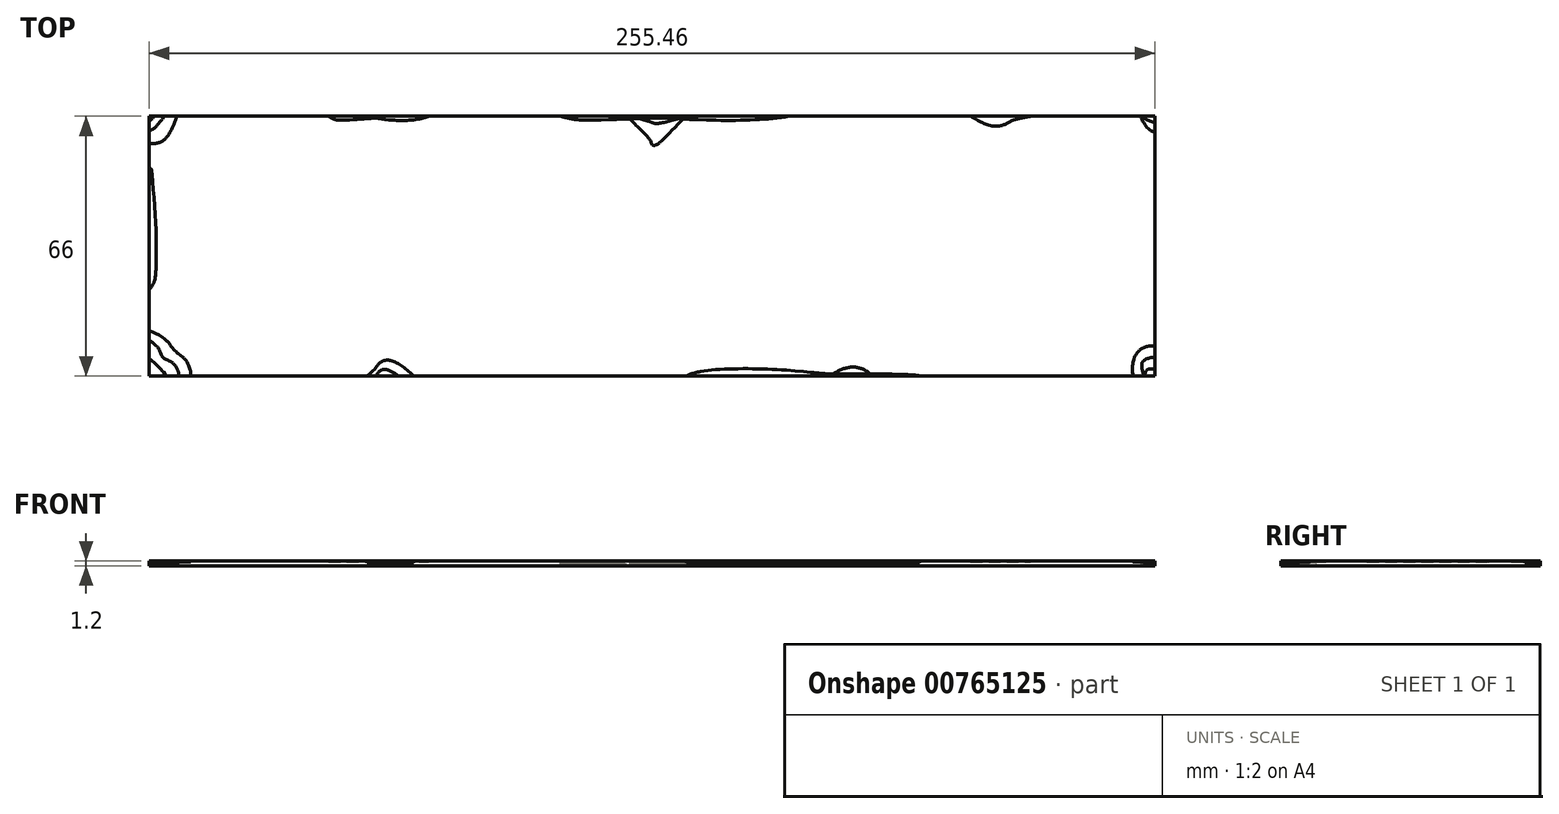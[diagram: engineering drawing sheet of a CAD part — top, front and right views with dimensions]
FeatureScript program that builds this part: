
annotation { "Feature Type Name" : "Feature", "Feature Type Description" : "" }
export const myFeature = defineFeature(function(context is Context, id is Id, definition is map)
    precondition{}
    {
        {
            var Q0;
            Q0=qCreatedBy(makeId("Top.planeOp"),FACE);
            var sketch = newSketch(context, id + "F0", { "sketchPlane" : qUnion([Q0])});
            skLineSegment(sketch, "E0.bottom", {"start": v(2.88, 34.46) * mm, "end": v(258.34, 34.46) * mm});
            skLineSegment(sketch, "E0.top", {"start": v(2.88, 100.46) * mm, "end": v(258.34, 100.46) * mm});
            skLineSegment(sketch, "E0.left", {"start": v(2.88, 34.46) * mm, "end": v(2.88, 100.46) * mm});
            skLineSegment(sketch, "E0.right", {"start": v(258.34, 34.46) * mm, "end": v(258.34, 100.46) * mm});
            skSolve(sketch);
        }
        {
            var Q0;
            Q0 = qSketchRegion(id + "F0", true);
            extrude(context, id + "F1", {"entities" : qUnion([Q0]), "depth" : 1.2 * mm, "offsetDistance" : 25 * mm});
        }
        {
            var Q0;
            Q0=makeQuery(id+"F1.opExtrude","CAP_FACE",FACE,{"disambiguationData":[OSD([sQuery(id+"F0.wireOp",EDGE,"E0.bottom"),sQuery(id+"F0.wireOp",EDGE,"E0.top"),sQuery(id+"F0.wireOp",EDGE,"E0.left"),sQuery(id+"F0.wireOp",EDGE,"E0.right")])],"isStart":false});
            var sketch = newSketch(context, id + "F2", { "sketchPlane" : qUnion([Q0])});
            skLineSegment(sketch, "E1", {"start": v(93.94, 37.46) * mm, "end": v(93.94, 97.46) * mm});
            skLineSegment(sketch, "E2", {"start": v(167.28, 38.41) * mm, "end": v(167.28, 98.41) * mm});
            skLineSegment(sketch, "E3", {"start": v(216.3, 60.97) * mm, "end": v(218.16, 60.97) * mm});
            skLineSegment(sketch, "E4", {"start": v(218.16, 60.97) * mm, "end": v(218.22, 60.98) * mm});
            skLineSegment(sketch, "E5", {"start": v(218.22, 60.98) * mm, "end": v(218.27, 61) * mm});
            skLineSegment(sketch, "E6", {"start": v(218.27, 61) * mm, "end": v(218.32, 61.03) * mm});
            skLineSegment(sketch, "E7", {"start": v(218.32, 61.03) * mm, "end": v(218.36, 61.07) * mm});
            skLineSegment(sketch, "E8", {"start": v(218.36, 61.07) * mm, "end": v(218.4, 61.12) * mm});
            skLineSegment(sketch, "E9", {"start": v(218.4, 61.12) * mm, "end": v(218.43, 61.2) * mm});
            skLineSegment(sketch, "E10", {"start": v(218.43, 61.2) * mm, "end": v(218.48, 61.42) * mm});
            skLineSegment(sketch, "E11", {"start": v(218.48, 61.42) * mm, "end": v(218.51, 61.51) * mm});
            skLineSegment(sketch, "E12", {"start": v(218.51, 61.51) * mm, "end": v(218.55, 61.56) * mm});
            skLineSegment(sketch, "E13", {"start": v(218.55, 61.56) * mm, "end": v(218.63, 61.6) * mm});
            skLineSegment(sketch, "E14", {"start": v(218.63, 61.6) * mm, "end": v(218.76, 61.6) * mm});
            skLineSegment(sketch, "E15", {"start": v(218.76, 61.6) * mm, "end": v(218.86, 61.6) * mm});
            skLineSegment(sketch, "E16", {"start": v(218.86, 61.6) * mm, "end": v(218.93, 61.57) * mm});
            skLineSegment(sketch, "E17", {"start": v(218.93, 61.57) * mm, "end": v(218.97, 61.54) * mm});
            skLineSegment(sketch, "E18", {"start": v(218.97, 61.54) * mm, "end": v(218.99, 61.5) * mm});
            skLineSegment(sketch, "E19", {"start": v(218.99, 61.5) * mm, "end": v(218.98, 61.42) * mm});
            skLineSegment(sketch, "E20", {"start": v(218.98, 61.42) * mm, "end": v(218.9, 60.94) * mm});
            skLineSegment(sketch, "E21", {"start": v(218.9, 60.94) * mm, "end": v(218.77, 60.22) * mm});
            skLineSegment(sketch, "E22", {"start": v(218.77, 60.22) * mm, "end": v(218.71, 59.99) * mm});
            skLineSegment(sketch, "E23", {"start": v(218.71, 59.99) * mm, "end": v(218.69, 59.92) * mm});
            skLineSegment(sketch, "E24", {"start": v(218.69, 59.92) * mm, "end": v(218.67, 59.89) * mm});
            skLineSegment(sketch, "E25", {"start": v(218.67, 59.89) * mm, "end": v(218.61, 59.86) * mm});
            skLineSegment(sketch, "E26", {"start": v(218.61, 59.86) * mm, "end": v(218.5, 59.86) * mm});
            skLineSegment(sketch, "E27", {"start": v(218.5, 59.86) * mm, "end": v(215.57, 59.86) * mm});
            skLineSegment(sketch, "E28", {"start": v(215.57, 59.86) * mm, "end": v(215.57, 60.73) * mm});
            skLineSegment(sketch, "E29", {"start": v(215.57, 60.73) * mm, "end": v(215.58, 60.82) * mm});
            skLineSegment(sketch, "E30", {"start": v(215.58, 60.82) * mm, "end": v(215.64, 60.93) * mm});
            skLineSegment(sketch, "E31", {"start": v(215.64, 60.93) * mm, "end": v(215.74, 61.05) * mm});
            skLineSegment(sketch, "E32", {"start": v(215.74, 61.05) * mm, "end": v(215.88, 61.19) * mm});
            skLineSegment(sketch, "E33", {"start": v(215.88, 61.19) * mm, "end": v(215.98, 61.3) * mm});
            skLineSegment(sketch, "E34", {"start": v(215.98, 61.3) * mm, "end": v(216.14, 61.47) * mm});
            skLineSegment(sketch, "E35", {"start": v(216.14, 61.47) * mm, "end": v(216.6, 62.04) * mm});
            skLineSegment(sketch, "E36", {"start": v(216.6, 62.04) * mm, "end": v(216.86, 62.38) * mm});
            skLineSegment(sketch, "E37", {"start": v(216.86, 62.38) * mm, "end": v(217.07, 62.68) * mm});
            skLineSegment(sketch, "E38", {"start": v(217.07, 62.68) * mm, "end": v(217.23, 62.96) * mm});
            skLineSegment(sketch, "E39", {"start": v(217.23, 62.96) * mm, "end": v(217.33, 63.2) * mm});
            skLineSegment(sketch, "E40", {"start": v(217.33, 63.2) * mm, "end": v(217.4, 63.44) * mm});
            skLineSegment(sketch, "E41", {"start": v(217.4, 63.44) * mm, "end": v(217.46, 63.72) * mm});
            skLineSegment(sketch, "E42", {"start": v(217.46, 63.72) * mm, "end": v(217.5, 64.04) * mm});
            skLineSegment(sketch, "E43", {"start": v(217.5, 64.04) * mm, "end": v(217.5, 64.4) * mm});
            skLineSegment(sketch, "E44", {"start": v(217.5, 64.4) * mm, "end": v(217.5, 64.69) * mm});
            skLineSegment(sketch, "E45", {"start": v(217.5, 64.69) * mm, "end": v(217.47, 64.92) * mm});
            skLineSegment(sketch, "E46", {"start": v(217.47, 64.92) * mm, "end": v(217.43, 65.09) * mm});
            skLineSegment(sketch, "E47", {"start": v(217.43, 65.09) * mm, "end": v(217.4, 65.16) * mm});
            skLineSegment(sketch, "E48", {"start": v(217.4, 65.16) * mm, "end": v(217.38, 65.2) * mm});
            skLineSegment(sketch, "E49", {"start": v(217.38, 65.2) * mm, "end": v(217.31, 65.29) * mm});
            skLineSegment(sketch, "E50", {"start": v(217.31, 65.29) * mm, "end": v(217.23, 65.34) * mm});
            skLineSegment(sketch, "E51", {"start": v(217.23, 65.34) * mm, "end": v(217.14, 65.38) * mm});
            skLineSegment(sketch, "E52", {"start": v(217.14, 65.38) * mm, "end": v(217.03, 65.39) * mm});
            skLineSegment(sketch, "E53", {"start": v(217.03, 65.39) * mm, "end": v(216.95, 65.38) * mm});
            skLineSegment(sketch, "E54", {"start": v(216.95, 65.38) * mm, "end": v(216.88, 65.36) * mm});
            skLineSegment(sketch, "E55", {"start": v(216.88, 65.36) * mm, "end": v(216.82, 65.33) * mm});
            skLineSegment(sketch, "E56", {"start": v(216.82, 65.33) * mm, "end": v(216.77, 65.3) * mm});
            skLineSegment(sketch, "E57", {"start": v(216.77, 65.3) * mm, "end": v(216.72, 65.24) * mm});
            skLineSegment(sketch, "E58", {"start": v(216.72, 65.24) * mm, "end": v(216.7, 65.18) * mm});
            skLineSegment(sketch, "E59", {"start": v(216.7, 65.18) * mm, "end": v(216.68, 65.11) * mm});
            skLineSegment(sketch, "E60", {"start": v(216.68, 65.11) * mm, "end": v(216.67, 65.04) * mm});
            skLineSegment(sketch, "E61", {"start": v(216.67, 65.04) * mm, "end": v(216.69, 64.82) * mm});
            skLineSegment(sketch, "E62", {"start": v(216.69, 64.82) * mm, "end": v(216.7, 64.66) * mm});
            skLineSegment(sketch, "E63", {"start": v(216.7, 64.66) * mm, "end": v(216.71, 64.5) * mm});
            skLineSegment(sketch, "E64", {"start": v(216.71, 64.5) * mm, "end": v(216.7, 64.34) * mm});
            skLineSegment(sketch, "E65", {"start": v(216.7, 64.34) * mm, "end": v(216.67, 64.2) * mm});
            skLineSegment(sketch, "E66", {"start": v(216.67, 64.2) * mm, "end": v(216.62, 64.08) * mm});
            skLineSegment(sketch, "E67", {"start": v(216.62, 64.08) * mm, "end": v(216.56, 63.98) * mm});
            skLineSegment(sketch, "E68", {"start": v(216.56, 63.98) * mm, "end": v(216.47, 63.9) * mm});
            skLineSegment(sketch, "E69", {"start": v(216.47, 63.9) * mm, "end": v(216.38, 63.84) * mm});
            skLineSegment(sketch, "E70", {"start": v(216.38, 63.84) * mm, "end": v(216.28, 63.8) * mm});
            skLineSegment(sketch, "E71", {"start": v(216.28, 63.8) * mm, "end": v(216.16, 63.79) * mm});
            skLineSegment(sketch, "E72", {"start": v(216.16, 63.79) * mm, "end": v(216.04, 63.8) * mm});
            skLineSegment(sketch, "E73", {"start": v(216.04, 63.8) * mm, "end": v(215.94, 63.84) * mm});
            skLineSegment(sketch, "E74", {"start": v(215.94, 63.84) * mm, "end": v(215.84, 63.9) * mm});
            skLineSegment(sketch, "E75", {"start": v(215.84, 63.9) * mm, "end": v(215.76, 64) * mm});
            skLineSegment(sketch, "E76", {"start": v(215.76, 64) * mm, "end": v(215.7, 64.1) * mm});
            skLineSegment(sketch, "E77", {"start": v(215.7, 64.1) * mm, "end": v(215.65, 64.21) * mm});
            skLineSegment(sketch, "E78", {"start": v(215.65, 64.21) * mm, "end": v(215.62, 64.34) * mm});
            skLineSegment(sketch, "E79", {"start": v(215.62, 64.34) * mm, "end": v(215.61, 64.47) * mm});
            skLineSegment(sketch, "E80", {"start": v(215.61, 64.47) * mm, "end": v(215.62, 64.62) * mm});
            skLineSegment(sketch, "E81", {"start": v(215.62, 64.62) * mm, "end": v(215.64, 64.76) * mm});
            skLineSegment(sketch, "E82", {"start": v(215.64, 64.76) * mm, "end": v(215.68, 64.89) * mm});
            skLineSegment(sketch, "E83", {"start": v(215.68, 64.89) * mm, "end": v(215.72, 65.02) * mm});
            skLineSegment(sketch, "E84", {"start": v(215.72, 65.02) * mm, "end": v(215.79, 65.14) * mm});
            skLineSegment(sketch, "E85", {"start": v(215.79, 65.14) * mm, "end": v(215.86, 65.26) * mm});
            skLineSegment(sketch, "E86", {"start": v(215.86, 65.26) * mm, "end": v(215.95, 65.37) * mm});
            skLineSegment(sketch, "E87", {"start": v(215.95, 65.37) * mm, "end": v(216.05, 65.47) * mm});
            skLineSegment(sketch, "E88", {"start": v(216.05, 65.47) * mm, "end": v(216.17, 65.57) * mm});
            skLineSegment(sketch, "E89", {"start": v(216.17, 65.57) * mm, "end": v(216.3, 65.65) * mm});
            skLineSegment(sketch, "E90", {"start": v(216.3, 65.65) * mm, "end": v(216.42, 65.72) * mm});
            skLineSegment(sketch, "E91", {"start": v(216.42, 65.72) * mm, "end": v(216.57, 65.78) * mm});
            skLineSegment(sketch, "E92", {"start": v(216.57, 65.78) * mm, "end": v(216.72, 65.82) * mm});
            skLineSegment(sketch, "E93", {"start": v(216.72, 65.82) * mm, "end": v(216.88, 65.86) * mm});
            skLineSegment(sketch, "E94", {"start": v(216.88, 65.86) * mm, "end": v(217.05, 65.88) * mm});
            skLineSegment(sketch, "E95", {"start": v(217.05, 65.88) * mm, "end": v(217.23, 65.88) * mm});
            skLineSegment(sketch, "E96", {"start": v(217.23, 65.88) * mm, "end": v(217.4, 65.88) * mm});
            skLineSegment(sketch, "E97", {"start": v(217.4, 65.88) * mm, "end": v(217.58, 65.85) * mm});
            skLineSegment(sketch, "E98", {"start": v(217.58, 65.85) * mm, "end": v(217.75, 65.82) * mm});
            skLineSegment(sketch, "E99", {"start": v(217.75, 65.82) * mm, "end": v(217.9, 65.76) * mm});
            skLineSegment(sketch, "E100", {"start": v(217.9, 65.76) * mm, "end": v(218.06, 65.7) * mm});
            skLineSegment(sketch, "E101", {"start": v(218.06, 65.7) * mm, "end": v(218.2, 65.62) * mm});
            skLineSegment(sketch, "E102", {"start": v(218.2, 65.62) * mm, "end": v(218.33, 65.52) * mm});
            skLineSegment(sketch, "E103", {"start": v(218.33, 65.52) * mm, "end": v(218.46, 65.41) * mm});
            skLineSegment(sketch, "E104", {"start": v(218.46, 65.41) * mm, "end": v(218.57, 65.29) * mm});
            skLineSegment(sketch, "E105", {"start": v(218.57, 65.29) * mm, "end": v(218.67, 65.16) * mm});
            skLineSegment(sketch, "E106", {"start": v(218.67, 65.16) * mm, "end": v(218.75, 65.02) * mm});
            skLineSegment(sketch, "E107", {"start": v(218.75, 65.02) * mm, "end": v(218.82, 64.87) * mm});
            skLineSegment(sketch, "E108", {"start": v(218.82, 64.87) * mm, "end": v(218.87, 64.71) * mm});
            skLineSegment(sketch, "E109", {"start": v(218.87, 64.71) * mm, "end": v(218.9, 64.55) * mm});
            skLineSegment(sketch, "E110", {"start": v(218.9, 64.55) * mm, "end": v(218.93, 64.37) * mm});
            skLineSegment(sketch, "E111", {"start": v(218.93, 64.37) * mm, "end": v(218.94, 64.19) * mm});
            skLineSegment(sketch, "E112", {"start": v(218.94, 64.19) * mm, "end": v(218.93, 63.98) * mm});
            skLineSegment(sketch, "E113", {"start": v(218.93, 63.98) * mm, "end": v(218.9, 63.78) * mm});
            skLineSegment(sketch, "E114", {"start": v(218.9, 63.78) * mm, "end": v(218.84, 63.58) * mm});
            skLineSegment(sketch, "E115", {"start": v(218.84, 63.58) * mm, "end": v(218.77, 63.39) * mm});
            skLineSegment(sketch, "E116", {"start": v(218.77, 63.39) * mm, "end": v(218.67, 63.2) * mm});
            skLineSegment(sketch, "E117", {"start": v(218.67, 63.2) * mm, "end": v(218.56, 63.03) * mm});
            skLineSegment(sketch, "E118", {"start": v(218.56, 63.03) * mm, "end": v(218.44, 62.87) * mm});
            skLineSegment(sketch, "E119", {"start": v(218.44, 62.87) * mm, "end": v(218.3, 62.71) * mm});
            skLineSegment(sketch, "E120", {"start": v(218.3, 62.71) * mm, "end": v(218.13, 62.56) * mm});
            skLineSegment(sketch, "E121", {"start": v(218.13, 62.56) * mm, "end": v(217.94, 62.38) * mm});
            skLineSegment(sketch, "E122", {"start": v(217.94, 62.38) * mm, "end": v(217.44, 61.97) * mm});
            skLineSegment(sketch, "E123", {"start": v(217.44, 61.97) * mm, "end": v(217.07, 61.68) * mm});
            skLineSegment(sketch, "E124", {"start": v(217.07, 61.68) * mm, "end": v(216.76, 61.42) * mm});
            skLineSegment(sketch, "E125", {"start": v(216.76, 61.42) * mm, "end": v(216.5, 61.18) * mm});
            skLineSegment(sketch, "E126", {"start": v(216.5, 61.18) * mm, "end": v(216.3, 60.97) * mm});
            skLineSegment(sketch, "E127", {"start": v(191.83, 62) * mm, "end": v(192.15, 62) * mm});
            skLineSegment(sketch, "E128", {"start": v(192.15, 62) * mm, "end": v(192.25, 62) * mm});
            skLineSegment(sketch, "E129", {"start": v(192.25, 62) * mm, "end": v(192.28, 61.98) * mm});
            skLineSegment(sketch, "E130", {"start": v(192.28, 61.98) * mm, "end": v(192.3, 61.96) * mm});
            skLineSegment(sketch, "E131", {"start": v(192.3, 61.96) * mm, "end": v(192.33, 61.9) * mm});
            skLineSegment(sketch, "E132", {"start": v(192.33, 61.9) * mm, "end": v(192.34, 61.8) * mm});
            skLineSegment(sketch, "E133", {"start": v(192.34, 61.8) * mm, "end": v(192.34, 61.58) * mm});
            skLineSegment(sketch, "E134", {"start": v(192.34, 61.58) * mm, "end": v(192.33, 61.5) * mm});
            skLineSegment(sketch, "E135", {"start": v(192.33, 61.5) * mm, "end": v(192.31, 61.45) * mm});
            skLineSegment(sketch, "E136", {"start": v(192.31, 61.45) * mm, "end": v(192.26, 61.43) * mm});
            skLineSegment(sketch, "E137", {"start": v(192.26, 61.43) * mm, "end": v(192.17, 61.42) * mm});
            skLineSegment(sketch, "E138", {"start": v(192.17, 61.42) * mm, "end": v(191.83, 61.42) * mm});
            skLineSegment(sketch, "E139", {"start": v(191.83, 61.42) * mm, "end": v(191.83, 60.72) * mm});
            skLineSegment(sketch, "E140", {"start": v(191.83, 60.72) * mm, "end": v(191.85, 60.6) * mm});
            skLineSegment(sketch, "E141", {"start": v(191.85, 60.6) * mm, "end": v(191.89, 60.5) * mm});
            skLineSegment(sketch, "E142", {"start": v(191.89, 60.5) * mm, "end": v(191.95, 60.42) * mm});
            skLineSegment(sketch, "E143", {"start": v(191.95, 60.42) * mm, "end": v(192.04, 60.36) * mm});
            skLineSegment(sketch, "E144", {"start": v(192.04, 60.36) * mm, "end": v(192.1, 60.32) * mm});
            skLineSegment(sketch, "E145", {"start": v(192.1, 60.32) * mm, "end": v(192.13, 60.28) * mm});
            skLineSegment(sketch, "E146", {"start": v(192.13, 60.28) * mm, "end": v(192.15, 60.22) * mm});
            skLineSegment(sketch, "E147", {"start": v(192.15, 60.22) * mm, "end": v(192.16, 60.15) * mm});
            skLineSegment(sketch, "E148", {"start": v(192.16, 60.15) * mm, "end": v(192.16, 59.98) * mm});
            skLineSegment(sketch, "E149", {"start": v(192.16, 59.98) * mm, "end": v(192.15, 59.92) * mm});
            skLineSegment(sketch, "E150", {"start": v(192.15, 59.92) * mm, "end": v(192.13, 59.88) * mm});
            skLineSegment(sketch, "E151", {"start": v(192.13, 59.88) * mm, "end": v(192.08, 59.86) * mm});
            skLineSegment(sketch, "E152", {"start": v(192.08, 59.86) * mm, "end": v(192, 59.86) * mm});
            skLineSegment(sketch, "E153", {"start": v(192, 59.86) * mm, "end": v(190.43, 59.86) * mm});
            skLineSegment(sketch, "E154", {"start": v(190.43, 59.86) * mm, "end": v(190.34, 59.87) * mm});
            skLineSegment(sketch, "E155", {"start": v(190.34, 59.87) * mm, "end": v(190.3, 59.88) * mm});
            skLineSegment(sketch, "E156", {"start": v(190.3, 59.88) * mm, "end": v(190.29, 59.9) * mm});
            skLineSegment(sketch, "E157", {"start": v(190.29, 59.9) * mm, "end": v(190.27, 59.98) * mm});
            skLineSegment(sketch, "E158", {"start": v(190.27, 59.98) * mm, "end": v(190.26, 60.16) * mm});
            skLineSegment(sketch, "E159", {"start": v(190.26, 60.16) * mm, "end": v(190.27, 60.22) * mm});
            skLineSegment(sketch, "E160", {"start": v(190.27, 60.22) * mm, "end": v(190.3, 60.27) * mm});
            skLineSegment(sketch, "E161", {"start": v(190.3, 60.27) * mm, "end": v(190.33, 60.32) * mm});
            skLineSegment(sketch, "E162", {"start": v(190.33, 60.32) * mm, "end": v(190.38, 60.35) * mm});
            skLineSegment(sketch, "E163", {"start": v(190.38, 60.35) * mm, "end": v(190.44, 60.4) * mm});
            skLineSegment(sketch, "E164", {"start": v(190.44, 60.4) * mm, "end": v(190.48, 60.45) * mm});
            skLineSegment(sketch, "E165", {"start": v(190.48, 60.45) * mm, "end": v(190.5, 60.51) * mm});
            skLineSegment(sketch, "E166", {"start": v(190.5, 60.51) * mm, "end": v(190.52, 60.58) * mm});
            skLineSegment(sketch, "E167", {"start": v(190.52, 60.58) * mm, "end": v(190.52, 61.42) * mm});
            skLineSegment(sketch, "E168", {"start": v(190.52, 61.42) * mm, "end": v(189.04, 61.42) * mm});
            skLineSegment(sketch, "E169", {"start": v(189.04, 61.42) * mm, "end": v(188.95, 61.42) * mm});
            skLineSegment(sketch, "E170", {"start": v(188.95, 61.42) * mm, "end": v(188.9, 61.45) * mm});
            skLineSegment(sketch, "E171", {"start": v(188.9, 61.45) * mm, "end": v(188.89, 61.5) * mm});
            skLineSegment(sketch, "E172", {"start": v(188.89, 61.5) * mm, "end": v(188.88, 61.57) * mm});
            skLineSegment(sketch, "E173", {"start": v(188.88, 61.57) * mm, "end": v(188.88, 62) * mm});
            skLineSegment(sketch, "E174", {"start": v(188.88, 62) * mm, "end": v(188.9, 62.11) * mm});
            skLineSegment(sketch, "E175", {"start": v(188.9, 62.11) * mm, "end": v(188.94, 62.2) * mm});
            skLineSegment(sketch, "E176", {"start": v(188.94, 62.2) * mm, "end": v(189.05, 62.39) * mm});
            skLineSegment(sketch, "E177", {"start": v(189.05, 62.39) * mm, "end": v(191.14, 65.73) * mm});
            skLineSegment(sketch, "E178", {"start": v(191.14, 65.73) * mm, "end": v(191.2, 65.8) * mm});
            skLineSegment(sketch, "E179", {"start": v(191.2, 65.8) * mm, "end": v(191.28, 65.85) * mm});
            skLineSegment(sketch, "E180", {"start": v(191.28, 65.85) * mm, "end": v(191.39, 65.87) * mm});
            skLineSegment(sketch, "E181", {"start": v(191.39, 65.87) * mm, "end": v(191.57, 65.88) * mm});
            skLineSegment(sketch, "E182", {"start": v(191.57, 65.88) * mm, "end": v(191.73, 65.88) * mm});
            skLineSegment(sketch, "E183", {"start": v(191.73, 65.88) * mm, "end": v(191.8, 65.86) * mm});
            skLineSegment(sketch, "E184", {"start": v(191.8, 65.86) * mm, "end": v(191.82, 65.81) * mm});
            skLineSegment(sketch, "E185", {"start": v(191.82, 65.81) * mm, "end": v(191.83, 65.73) * mm});
            skLineSegment(sketch, "E186", {"start": v(191.83, 65.73) * mm, "end": v(191.83, 62) * mm});
            skLineSegment(sketch, "E187", {"start": v(190.52, 63.83) * mm, "end": v(189.38, 62) * mm});
            skLineSegment(sketch, "E188", {"start": v(189.38, 62) * mm, "end": v(190.52, 62) * mm});
            skLineSegment(sketch, "E189", {"start": v(190.52, 62) * mm, "end": v(190.52, 63.83) * mm});
            skLineSegment(sketch, "E190", {"start": v(156.99, 63.9) * mm, "end": v(157.07, 63.98) * mm});
            skLineSegment(sketch, "E191", {"start": v(157.07, 63.98) * mm, "end": v(157.16, 64.06) * mm});
            skLineSegment(sketch, "E192", {"start": v(157.16, 64.06) * mm, "end": v(157.25, 64.13) * mm});
            skLineSegment(sketch, "E193", {"start": v(157.25, 64.13) * mm, "end": v(157.34, 64.18) * mm});
            skLineSegment(sketch, "E194", {"start": v(157.34, 64.18) * mm, "end": v(157.43, 64.22) * mm});
            skLineSegment(sketch, "E195", {"start": v(157.43, 64.22) * mm, "end": v(157.52, 64.25) * mm});
            skLineSegment(sketch, "E196", {"start": v(157.52, 64.25) * mm, "end": v(157.62, 64.27) * mm});
            skLineSegment(sketch, "E197", {"start": v(157.62, 64.27) * mm, "end": v(157.71, 64.27) * mm});
            skLineSegment(sketch, "E198", {"start": v(157.71, 64.27) * mm, "end": v(157.84, 64.27) * mm});
            skLineSegment(sketch, "E199", {"start": v(157.84, 64.27) * mm, "end": v(157.97, 64.24) * mm});
            skLineSegment(sketch, "E200", {"start": v(157.97, 64.24) * mm, "end": v(158.09, 64.2) * mm});
            skLineSegment(sketch, "E201", {"start": v(158.09, 64.2) * mm, "end": v(158.2, 64.14) * mm});
            skLineSegment(sketch, "E202", {"start": v(158.2, 64.14) * mm, "end": v(158.31, 64.07) * mm});
            skLineSegment(sketch, "E203", {"start": v(158.31, 64.07) * mm, "end": v(158.42, 63.98) * mm});
            skLineSegment(sketch, "E204", {"start": v(158.42, 63.98) * mm, "end": v(158.52, 63.87) * mm});
            skLineSegment(sketch, "E205", {"start": v(158.52, 63.87) * mm, "end": v(158.62, 63.75) * mm});
            skLineSegment(sketch, "E206", {"start": v(158.62, 63.75) * mm, "end": v(158.7, 63.61) * mm});
            skLineSegment(sketch, "E207", {"start": v(158.7, 63.61) * mm, "end": v(158.78, 63.46) * mm});
            skLineSegment(sketch, "E208", {"start": v(158.78, 63.46) * mm, "end": v(158.85, 63.3) * mm});
            skLineSegment(sketch, "E209", {"start": v(158.85, 63.3) * mm, "end": v(158.9, 63.1) * mm});
            skLineSegment(sketch, "E210", {"start": v(158.9, 63.1) * mm, "end": v(158.94, 62.9) * mm});
            skLineSegment(sketch, "E211", {"start": v(158.94, 62.9) * mm, "end": v(158.97, 62.7) * mm});
            skLineSegment(sketch, "E212", {"start": v(158.97, 62.7) * mm, "end": v(158.99, 62.47) * mm});
            skLineSegment(sketch, "E213", {"start": v(158.99, 62.47) * mm, "end": v(159, 62.23) * mm});
            skLineSegment(sketch, "E214", {"start": v(159, 62.23) * mm, "end": v(158.99, 61.97) * mm});
            skLineSegment(sketch, "E215", {"start": v(158.99, 61.97) * mm, "end": v(158.96, 61.73) * mm});
            skLineSegment(sketch, "E216", {"start": v(158.96, 61.73) * mm, "end": v(158.93, 61.5) * mm});
            skLineSegment(sketch, "E217", {"start": v(158.93, 61.5) * mm, "end": v(158.88, 61.27) * mm});
            skLineSegment(sketch, "E218", {"start": v(158.88, 61.27) * mm, "end": v(158.8, 61.06) * mm});
            skLineSegment(sketch, "E219", {"start": v(158.8, 61.06) * mm, "end": v(158.73, 60.87) * mm});
            skLineSegment(sketch, "E220", {"start": v(158.73, 60.87) * mm, "end": v(158.63, 60.68) * mm});
            skLineSegment(sketch, "E221", {"start": v(158.63, 60.68) * mm, "end": v(158.52, 60.5) * mm});
            skLineSegment(sketch, "E222", {"start": v(158.52, 60.5) * mm, "end": v(158.4, 60.34) * mm});
            skLineSegment(sketch, "E223", {"start": v(158.4, 60.34) * mm, "end": v(158.27, 60.2) * mm});
            skLineSegment(sketch, "E224", {"start": v(158.27, 60.2) * mm, "end": v(158.13, 60.09) * mm});
            skLineSegment(sketch, "E225", {"start": v(158.13, 60.09) * mm, "end": v(157.97, 60) * mm});
            skLineSegment(sketch, "E226", {"start": v(157.97, 60) * mm, "end": v(157.81, 59.92) * mm});
            skLineSegment(sketch, "E227", {"start": v(157.81, 59.92) * mm, "end": v(157.64, 59.86) * mm});
            skLineSegment(sketch, "E228", {"start": v(157.64, 59.86) * mm, "end": v(157.46, 59.83) * mm});
            skLineSegment(sketch, "E229", {"start": v(157.46, 59.83) * mm, "end": v(157.27, 59.82) * mm});
            skLineSegment(sketch, "E230", {"start": v(157.27, 59.82) * mm, "end": v(157.14, 59.83) * mm});
            skLineSegment(sketch, "E231", {"start": v(157.14, 59.83) * mm, "end": v(157.02, 59.84) * mm});
            skLineSegment(sketch, "E232", {"start": v(157.02, 59.84) * mm, "end": v(156.9, 59.86) * mm});
            skLineSegment(sketch, "E233", {"start": v(156.9, 59.86) * mm, "end": v(156.8, 59.9) * mm});
            skLineSegment(sketch, "E234", {"start": v(156.8, 59.9) * mm, "end": v(156.68, 59.93) * mm});
            skLineSegment(sketch, "E235", {"start": v(156.68, 59.93) * mm, "end": v(156.58, 59.98) * mm});
            skLineSegment(sketch, "E236", {"start": v(156.58, 59.98) * mm, "end": v(156.48, 60.04) * mm});
            skLineSegment(sketch, "E237", {"start": v(156.48, 60.04) * mm, "end": v(156.39, 60.1) * mm});
            skLineSegment(sketch, "E238", {"start": v(156.39, 60.1) * mm, "end": v(156.3, 60.18) * mm});
            skLineSegment(sketch, "E239", {"start": v(156.3, 60.18) * mm, "end": v(156.2, 60.26) * mm});
            skLineSegment(sketch, "E240", {"start": v(156.2, 60.26) * mm, "end": v(156.13, 60.36) * mm});
            skLineSegment(sketch, "E241", {"start": v(156.13, 60.36) * mm, "end": v(156.05, 60.47) * mm});
            skLineSegment(sketch, "E242", {"start": v(156.05, 60.47) * mm, "end": v(155.98, 60.59) * mm});
            skLineSegment(sketch, "E243", {"start": v(155.98, 60.59) * mm, "end": v(155.91, 60.71) * mm});
            skLineSegment(sketch, "E244", {"start": v(155.91, 60.71) * mm, "end": v(155.79, 61) * mm});
            skLineSegment(sketch, "E245", {"start": v(155.79, 61) * mm, "end": v(155.74, 61.16) * mm});
            skLineSegment(sketch, "E246", {"start": v(155.74, 61.16) * mm, "end": v(155.69, 61.33) * mm});
            skLineSegment(sketch, "E247", {"start": v(155.69, 61.33) * mm, "end": v(155.65, 61.52) * mm});
            skLineSegment(sketch, "E248", {"start": v(155.65, 61.52) * mm, "end": v(155.62, 61.71) * mm});
            skLineSegment(sketch, "E249", {"start": v(155.62, 61.71) * mm, "end": v(155.58, 62.14) * mm});
            skLineSegment(sketch, "E250", {"start": v(155.58, 62.14) * mm, "end": v(155.56, 62.61) * mm});
            skLineSegment(sketch, "E251", {"start": v(155.56, 62.61) * mm, "end": v(155.57, 62.9) * mm});
            skLineSegment(sketch, "E252", {"start": v(155.57, 62.9) * mm, "end": v(155.58, 63.18) * mm});
            skLineSegment(sketch, "E253", {"start": v(155.58, 63.18) * mm, "end": v(155.6, 63.44) * mm});
            skLineSegment(sketch, "E254", {"start": v(155.6, 63.44) * mm, "end": v(155.65, 63.7) * mm});
            skLineSegment(sketch, "E255", {"start": v(155.65, 63.7) * mm, "end": v(155.7, 63.93) * mm});
            skLineSegment(sketch, "E256", {"start": v(155.7, 63.93) * mm, "end": v(155.75, 64.15) * mm});
            skLineSegment(sketch, "E257", {"start": v(155.75, 64.15) * mm, "end": v(155.82, 64.35) * mm});
            skLineSegment(sketch, "E258", {"start": v(155.82, 64.35) * mm, "end": v(155.9, 64.54) * mm});
            skLineSegment(sketch, "E259", {"start": v(155.9, 64.54) * mm, "end": v(155.99, 64.72) * mm});
            skLineSegment(sketch, "E260", {"start": v(155.99, 64.72) * mm, "end": v(156.09, 64.88) * mm});
            skLineSegment(sketch, "E261", {"start": v(156.09, 64.88) * mm, "end": v(156.2, 65.03) * mm});
            skLineSegment(sketch, "E262", {"start": v(156.2, 65.03) * mm, "end": v(156.31, 65.17) * mm});
            skLineSegment(sketch, "E263", {"start": v(156.31, 65.17) * mm, "end": v(156.44, 65.3) * mm});
            skLineSegment(sketch, "E264", {"start": v(156.44, 65.3) * mm, "end": v(156.57, 65.4) * mm});
            skLineSegment(sketch, "E265", {"start": v(156.57, 65.4) * mm, "end": v(156.72, 65.5) * mm});
            skLineSegment(sketch, "E266", {"start": v(156.72, 65.5) * mm, "end": v(156.87, 65.6) * mm});
            skLineSegment(sketch, "E267", {"start": v(156.87, 65.6) * mm, "end": v(157.03, 65.67) * mm});
            skLineSegment(sketch, "E268", {"start": v(157.03, 65.67) * mm, "end": v(157.2, 65.74) * mm});
            skLineSegment(sketch, "E269", {"start": v(157.2, 65.74) * mm, "end": v(157.36, 65.8) * mm});
            skLineSegment(sketch, "E270", {"start": v(157.36, 65.8) * mm, "end": v(157.53, 65.84) * mm});
            skLineSegment(sketch, "E271", {"start": v(157.53, 65.84) * mm, "end": v(157.7, 65.87) * mm});
            skLineSegment(sketch, "E272", {"start": v(157.7, 65.87) * mm, "end": v(157.87, 65.9) * mm});
            skLineSegment(sketch, "E273", {"start": v(157.87, 65.9) * mm, "end": v(158.05, 65.91) * mm});
            skLineSegment(sketch, "E274", {"start": v(158.05, 65.91) * mm, "end": v(158.22, 65.92) * mm});
            skLineSegment(sketch, "E275", {"start": v(158.22, 65.92) * mm, "end": v(158.39, 65.91) * mm});
            skLineSegment(sketch, "E276", {"start": v(158.39, 65.91) * mm, "end": v(158.49, 65.9) * mm});
            skLineSegment(sketch, "E277", {"start": v(158.49, 65.9) * mm, "end": v(158.52, 65.88) * mm});
            skLineSegment(sketch, "E278", {"start": v(158.52, 65.88) * mm, "end": v(158.54, 65.85) * mm});
            skLineSegment(sketch, "E279", {"start": v(158.54, 65.85) * mm, "end": v(158.56, 65.83) * mm});
            skLineSegment(sketch, "E280", {"start": v(158.56, 65.83) * mm, "end": v(158.56, 65.8) * mm});
            skLineSegment(sketch, "E281", {"start": v(158.56, 65.8) * mm, "end": v(158.56, 65.57) * mm});
            skLineSegment(sketch, "E282", {"start": v(158.56, 65.57) * mm, "end": v(158.54, 65.46) * mm});
            skLineSegment(sketch, "E283", {"start": v(158.54, 65.46) * mm, "end": v(158.51, 65.44) * mm});
            skLineSegment(sketch, "E284", {"start": v(158.51, 65.44) * mm, "end": v(158.48, 65.42) * mm});
            skLineSegment(sketch, "E285", {"start": v(158.48, 65.42) * mm, "end": v(158.35, 65.4) * mm});
            skLineSegment(sketch, "E286", {"start": v(158.35, 65.4) * mm, "end": v(158.18, 65.4) * mm});
            skLineSegment(sketch, "E287", {"start": v(158.18, 65.4) * mm, "end": v(158, 65.36) * mm});
            skLineSegment(sketch, "E288", {"start": v(158, 65.36) * mm, "end": v(157.82, 65.31) * mm});
            skLineSegment(sketch, "E289", {"start": v(157.82, 65.31) * mm, "end": v(157.64, 65.24) * mm});
            skLineSegment(sketch, "E290", {"start": v(157.64, 65.24) * mm, "end": v(157.47, 65.15) * mm});
            skLineSegment(sketch, "E291", {"start": v(157.47, 65.15) * mm, "end": v(157.33, 65.05) * mm});
            skLineSegment(sketch, "E292", {"start": v(157.33, 65.05) * mm, "end": v(157.22, 64.93) * mm});
            skLineSegment(sketch, "E293", {"start": v(157.22, 64.93) * mm, "end": v(157.13, 64.79) * mm});
            skLineSegment(sketch, "E294", {"start": v(157.13, 64.79) * mm, "end": v(157.07, 64.62) * mm});
            skLineSegment(sketch, "E295", {"start": v(157.07, 64.62) * mm, "end": v(157.02, 64.41) * mm});
            skLineSegment(sketch, "E296", {"start": v(157.02, 64.41) * mm, "end": v(157, 64.17) * mm});
            skLineSegment(sketch, "E297", {"start": v(157, 64.17) * mm, "end": v(156.99, 63.9) * mm});
            skLineSegment(sketch, "E298", {"start": v(157.55, 63.36) * mm, "end": v(157.54, 63.47) * mm});
            skLineSegment(sketch, "E299", {"start": v(157.54, 63.47) * mm, "end": v(157.52, 63.52) * mm});
            skLineSegment(sketch, "E300", {"start": v(157.52, 63.52) * mm, "end": v(157.49, 63.56) * mm});
            skLineSegment(sketch, "E301", {"start": v(157.49, 63.56) * mm, "end": v(157.45, 63.6) * mm});
            skLineSegment(sketch, "E302", {"start": v(157.45, 63.6) * mm, "end": v(157.4, 63.63) * mm});
            skLineSegment(sketch, "E303", {"start": v(157.4, 63.63) * mm, "end": v(157.36, 63.64) * mm});
            skLineSegment(sketch, "E304", {"start": v(157.36, 63.64) * mm, "end": v(157.3, 63.65) * mm});
            skLineSegment(sketch, "E305", {"start": v(157.3, 63.65) * mm, "end": v(157.24, 63.64) * mm});
            skLineSegment(sketch, "E306", {"start": v(157.24, 63.64) * mm, "end": v(157.18, 63.62) * mm});
            skLineSegment(sketch, "E307", {"start": v(157.18, 63.62) * mm, "end": v(157.13, 63.59) * mm});
            skLineSegment(sketch, "E308", {"start": v(157.13, 63.59) * mm, "end": v(157.1, 63.54) * mm});
            skLineSegment(sketch, "E309", {"start": v(157.1, 63.54) * mm, "end": v(157.06, 63.48) * mm});
            skLineSegment(sketch, "E310", {"start": v(157.06, 63.48) * mm, "end": v(157.04, 63.4) * mm});
            skLineSegment(sketch, "E311", {"start": v(157.04, 63.4) * mm, "end": v(157.02, 63.32) * mm});
            skLineSegment(sketch, "E312", {"start": v(157.02, 63.32) * mm, "end": v(157.02, 63.22) * mm});
            skLineSegment(sketch, "E313", {"start": v(157.02, 63.22) * mm, "end": v(157.02, 60.56) * mm});
            skLineSegment(sketch, "E314", {"start": v(157.02, 60.56) * mm, "end": v(157.02, 60.5) * mm});
            skLineSegment(sketch, "E315", {"start": v(157.02, 60.5) * mm, "end": v(157.04, 60.46) * mm});
            skLineSegment(sketch, "E316", {"start": v(157.04, 60.46) * mm, "end": v(157.06, 60.41) * mm});
            skLineSegment(sketch, "E317", {"start": v(157.06, 60.41) * mm, "end": v(157.1, 60.38) * mm});
            skLineSegment(sketch, "E318", {"start": v(157.1, 60.38) * mm, "end": v(157.14, 60.34) * mm});
            skLineSegment(sketch, "E319", {"start": v(157.14, 60.34) * mm, "end": v(157.18, 60.32) * mm});
            skLineSegment(sketch, "E320", {"start": v(157.18, 60.32) * mm, "end": v(157.23, 60.3) * mm});
            skLineSegment(sketch, "E321", {"start": v(157.23, 60.3) * mm, "end": v(157.28, 60.3) * mm});
            skLineSegment(sketch, "E322", {"start": v(157.28, 60.3) * mm, "end": v(157.34, 60.3) * mm});
            skLineSegment(sketch, "E323", {"start": v(157.34, 60.3) * mm, "end": v(157.4, 60.33) * mm});
            skLineSegment(sketch, "E324", {"start": v(157.4, 60.33) * mm, "end": v(157.44, 60.36) * mm});
            skLineSegment(sketch, "E325", {"start": v(157.44, 60.36) * mm, "end": v(157.48, 60.41) * mm});
            skLineSegment(sketch, "E326", {"start": v(157.48, 60.41) * mm, "end": v(157.51, 60.48) * mm});
            skLineSegment(sketch, "E327", {"start": v(157.51, 60.48) * mm, "end": v(157.54, 60.58) * mm});
            skLineSegment(sketch, "E328", {"start": v(157.54, 60.58) * mm, "end": v(157.55, 60.72) * mm});
            skLineSegment(sketch, "E329", {"start": v(157.55, 60.72) * mm, "end": v(157.55, 60.88) * mm});
            skLineSegment(sketch, "E330", {"start": v(157.55, 60.88) * mm, "end": v(157.55, 63.36) * mm});
            skLineSegment(sketch, "E331", {"start": v(129.75, 62.91) * mm, "end": v(129.58, 63.07) * mm});
            skLineSegment(sketch, "E332", {"start": v(129.58, 63.07) * mm, "end": v(129.44, 63.23) * mm});
            skLineSegment(sketch, "E333", {"start": v(129.44, 63.23) * mm, "end": v(129.32, 63.4) * mm});
            skLineSegment(sketch, "E334", {"start": v(129.32, 63.4) * mm, "end": v(129.22, 63.57) * mm});
            skLineSegment(sketch, "E335", {"start": v(129.22, 63.57) * mm, "end": v(129.14, 63.76) * mm});
            skLineSegment(sketch, "E336", {"start": v(129.14, 63.76) * mm, "end": v(129.09, 63.96) * mm});
            skLineSegment(sketch, "E337", {"start": v(129.09, 63.96) * mm, "end": v(129.05, 64.16) * mm});
            skLineSegment(sketch, "E338", {"start": v(129.05, 64.16) * mm, "end": v(129.04, 64.38) * mm});
            skLineSegment(sketch, "E339", {"start": v(129.04, 64.38) * mm, "end": v(129.05, 64.55) * mm});
            skLineSegment(sketch, "E340", {"start": v(129.05, 64.55) * mm, "end": v(129.07, 64.7) * mm});
            skLineSegment(sketch, "E341", {"start": v(129.07, 64.7) * mm, "end": v(129.1, 64.86) * mm});
            skLineSegment(sketch, "E342", {"start": v(129.1, 64.86) * mm, "end": v(129.15, 65) * mm});
            skLineSegment(sketch, "E343", {"start": v(129.15, 65) * mm, "end": v(129.21, 65.14) * mm});
            skLineSegment(sketch, "E344", {"start": v(129.21, 65.14) * mm, "end": v(129.29, 65.27) * mm});
            skLineSegment(sketch, "E345", {"start": v(129.29, 65.27) * mm, "end": v(129.38, 65.39) * mm});
            skLineSegment(sketch, "E346", {"start": v(129.38, 65.39) * mm, "end": v(129.48, 65.5) * mm});
            skLineSegment(sketch, "E347", {"start": v(129.48, 65.5) * mm, "end": v(129.59, 65.6) * mm});
            skLineSegment(sketch, "E348", {"start": v(129.59, 65.6) * mm, "end": v(129.71, 65.68) * mm});
            skLineSegment(sketch, "E349", {"start": v(129.71, 65.68) * mm, "end": v(129.84, 65.75) * mm});
            skLineSegment(sketch, "E350", {"start": v(129.84, 65.75) * mm, "end": v(129.98, 65.81) * mm});
            skLineSegment(sketch, "E351", {"start": v(129.98, 65.81) * mm, "end": v(130.13, 65.86) * mm});
            skLineSegment(sketch, "E352", {"start": v(130.13, 65.86) * mm, "end": v(130.29, 65.9) * mm});
            skLineSegment(sketch, "E353", {"start": v(130.29, 65.9) * mm, "end": v(130.46, 65.91) * mm});
            skLineSegment(sketch, "E354", {"start": v(130.46, 65.91) * mm, "end": v(130.63, 65.92) * mm});
            skLineSegment(sketch, "E355", {"start": v(130.63, 65.92) * mm, "end": v(130.81, 65.91) * mm});
            skLineSegment(sketch, "E356", {"start": v(130.81, 65.91) * mm, "end": v(130.98, 65.9) * mm});
            skLineSegment(sketch, "E357", {"start": v(130.98, 65.9) * mm, "end": v(131.14, 65.86) * mm});
            skLineSegment(sketch, "E358", {"start": v(131.14, 65.86) * mm, "end": v(131.29, 65.82) * mm});
            skLineSegment(sketch, "E359", {"start": v(131.29, 65.82) * mm, "end": v(131.43, 65.76) * mm});
            skLineSegment(sketch, "E360", {"start": v(131.43, 65.76) * mm, "end": v(131.56, 65.7) * mm});
            skLineSegment(sketch, "E361", {"start": v(131.56, 65.7) * mm, "end": v(131.68, 65.6) * mm});
            skLineSegment(sketch, "E362", {"start": v(131.68, 65.6) * mm, "end": v(131.79, 65.51) * mm});
            skLineSegment(sketch, "E363", {"start": v(131.79, 65.51) * mm, "end": v(131.89, 65.41) * mm});
            skLineSegment(sketch, "E364", {"start": v(131.89, 65.41) * mm, "end": v(131.97, 65.3) * mm});
            skLineSegment(sketch, "E365", {"start": v(131.97, 65.3) * mm, "end": v(132.04, 65.19) * mm});
            skLineSegment(sketch, "E366", {"start": v(132.04, 65.19) * mm, "end": v(132.1, 65.07) * mm});
            skLineSegment(sketch, "E367", {"start": v(132.1, 65.07) * mm, "end": v(132.15, 64.95) * mm});
            skLineSegment(sketch, "E368", {"start": v(132.15, 64.95) * mm, "end": v(132.18, 64.82) * mm});
            skLineSegment(sketch, "E369", {"start": v(132.18, 64.82) * mm, "end": v(132.2, 64.7) * mm});
            skLineSegment(sketch, "E370", {"start": v(132.2, 64.7) * mm, "end": v(132.2, 64.56) * mm});
            skLineSegment(sketch, "E371", {"start": v(132.2, 64.56) * mm, "end": v(132.2, 64.38) * mm});
            skLineSegment(sketch, "E372", {"start": v(132.2, 64.38) * mm, "end": v(132.16, 64.2) * mm});
            skLineSegment(sketch, "E373", {"start": v(132.16, 64.2) * mm, "end": v(132.1, 64.04) * mm});
            skLineSegment(sketch, "E374", {"start": v(132.1, 64.04) * mm, "end": v(132.02, 63.89) * mm});
            skLineSegment(sketch, "E375", {"start": v(132.02, 63.89) * mm, "end": v(131.91, 63.74) * mm});
            skLineSegment(sketch, "E376", {"start": v(131.91, 63.74) * mm, "end": v(131.78, 63.6) * mm});
            skLineSegment(sketch, "E377", {"start": v(131.78, 63.6) * mm, "end": v(131.63, 63.47) * mm});
            skLineSegment(sketch, "E378", {"start": v(131.63, 63.47) * mm, "end": v(131.46, 63.35) * mm});
            skLineSegment(sketch, "E379", {"start": v(131.46, 63.35) * mm, "end": v(131.67, 63.17) * mm});
            skLineSegment(sketch, "E380", {"start": v(131.67, 63.17) * mm, "end": v(131.85, 62.98) * mm});
            skLineSegment(sketch, "E381", {"start": v(131.85, 62.98) * mm, "end": v(132, 62.8) * mm});
            skLineSegment(sketch, "E382", {"start": v(132, 62.8) * mm, "end": v(132.11, 62.6) * mm});
            skLineSegment(sketch, "E383", {"start": v(132.11, 62.6) * mm, "end": v(132.2, 62.41) * mm});
            skLineSegment(sketch, "E384", {"start": v(132.2, 62.41) * mm, "end": v(132.26, 62.2) * mm});
            skLineSegment(sketch, "E385", {"start": v(132.26, 62.2) * mm, "end": v(132.3, 61.98) * mm});
            skLineSegment(sketch, "E386", {"start": v(132.3, 61.98) * mm, "end": v(132.3, 61.74) * mm});
            skLineSegment(sketch, "E387", {"start": v(132.3, 61.74) * mm, "end": v(132.3, 61.52) * mm});
            skLineSegment(sketch, "E388", {"start": v(132.3, 61.52) * mm, "end": v(132.28, 61.32) * mm});
            skLineSegment(sketch, "E389", {"start": v(132.28, 61.32) * mm, "end": v(132.24, 61.13) * mm});
            skLineSegment(sketch, "E390", {"start": v(132.24, 61.13) * mm, "end": v(132.18, 60.95) * mm});
            skLineSegment(sketch, "E391", {"start": v(132.18, 60.95) * mm, "end": v(132.1, 60.78) * mm});
            skLineSegment(sketch, "E392", {"start": v(132.1, 60.78) * mm, "end": v(132.02, 60.62) * mm});
            skLineSegment(sketch, "E393", {"start": v(132.02, 60.62) * mm, "end": v(131.91, 60.47) * mm});
            skLineSegment(sketch, "E394", {"start": v(131.91, 60.47) * mm, "end": v(131.8, 60.34) * mm});
            skLineSegment(sketch, "E395", {"start": v(131.8, 60.34) * mm, "end": v(131.66, 60.22) * mm});
            skLineSegment(sketch, "E396", {"start": v(131.66, 60.22) * mm, "end": v(131.52, 60.11) * mm});
            skLineSegment(sketch, "E397", {"start": v(131.52, 60.11) * mm, "end": v(131.38, 60.02) * mm});
            skLineSegment(sketch, "E398", {"start": v(131.38, 60.02) * mm, "end": v(131.22, 59.95) * mm});
            skLineSegment(sketch, "E399", {"start": v(131.22, 59.95) * mm, "end": v(131.06, 59.9) * mm});
            skLineSegment(sketch, "E400", {"start": v(131.06, 59.9) * mm, "end": v(130.9, 59.85) * mm});
            skLineSegment(sketch, "E401", {"start": v(130.9, 59.85) * mm, "end": v(130.73, 59.83) * mm});
            skLineSegment(sketch, "E402", {"start": v(130.73, 59.83) * mm, "end": v(130.55, 59.82) * mm});
            skLineSegment(sketch, "E403", {"start": v(130.55, 59.82) * mm, "end": v(130.37, 59.83) * mm});
            skLineSegment(sketch, "E404", {"start": v(130.37, 59.83) * mm, "end": v(130.2, 59.85) * mm});
            skLineSegment(sketch, "E405", {"start": v(130.2, 59.85) * mm, "end": v(130.05, 59.89) * mm});
            skLineSegment(sketch, "E406", {"start": v(130.05, 59.89) * mm, "end": v(129.9, 59.94) * mm});
            skLineSegment(sketch, "E407", {"start": v(129.9, 59.94) * mm, "end": v(129.76, 60) * mm});
            skLineSegment(sketch, "E408", {"start": v(129.76, 60) * mm, "end": v(129.62, 60.09) * mm});
            skLineSegment(sketch, "E409", {"start": v(129.62, 60.09) * mm, "end": v(129.5, 60.19) * mm});
            skLineSegment(sketch, "E410", {"start": v(129.5, 60.19) * mm, "end": v(129.38, 60.3) * mm});
            skLineSegment(sketch, "E411", {"start": v(129.38, 60.3) * mm, "end": v(129.27, 60.42) * mm});
            skLineSegment(sketch, "E412", {"start": v(129.27, 60.42) * mm, "end": v(129.17, 60.55) * mm});
            skLineSegment(sketch, "E413", {"start": v(129.17, 60.55) * mm, "end": v(129.1, 60.69) * mm});
            skLineSegment(sketch, "E414", {"start": v(129.1, 60.69) * mm, "end": v(129.03, 60.83) * mm});
            skLineSegment(sketch, "E415", {"start": v(129.03, 60.83) * mm, "end": v(128.98, 60.98) * mm});
            skLineSegment(sketch, "E416", {"start": v(128.98, 60.98) * mm, "end": v(128.94, 61.14) * mm});
            skLineSegment(sketch, "E417", {"start": v(128.94, 61.14) * mm, "end": v(128.92, 61.3) * mm});
            skLineSegment(sketch, "E418", {"start": v(128.92, 61.3) * mm, "end": v(128.91, 61.48) * mm});
            skLineSegment(sketch, "E419", {"start": v(128.91, 61.48) * mm, "end": v(128.93, 61.7) * mm});
            skLineSegment(sketch, "E420", {"start": v(128.93, 61.7) * mm, "end": v(128.97, 61.9) * mm});
            skLineSegment(sketch, "E421", {"start": v(128.97, 61.9) * mm, "end": v(129.03, 62.1) * mm});
            skLineSegment(sketch, "E422", {"start": v(129.03, 62.1) * mm, "end": v(129.12, 62.3) * mm});
            skLineSegment(sketch, "E423", {"start": v(129.12, 62.3) * mm, "end": v(129.24, 62.47) * mm});
            skLineSegment(sketch, "E424", {"start": v(129.24, 62.47) * mm, "end": v(129.38, 62.63) * mm});
            skLineSegment(sketch, "E425", {"start": v(129.38, 62.63) * mm, "end": v(129.55, 62.78) * mm});
            skLineSegment(sketch, "E426", {"start": v(129.55, 62.78) * mm, "end": v(129.75, 62.91) * mm});
            skLineSegment(sketch, "E427", {"start": v(131.06, 63.65) * mm, "end": v(131.14, 63.73) * mm});
            skLineSegment(sketch, "E428", {"start": v(131.14, 63.73) * mm, "end": v(131.2, 63.81) * mm});
            skLineSegment(sketch, "E429", {"start": v(131.2, 63.81) * mm, "end": v(131.25, 63.91) * mm});
            skLineSegment(sketch, "E430", {"start": v(131.25, 63.91) * mm, "end": v(131.3, 64.02) * mm});
            skLineSegment(sketch, "E431", {"start": v(131.3, 64.02) * mm, "end": v(131.33, 64.13) * mm});
            skLineSegment(sketch, "E432", {"start": v(131.33, 64.13) * mm, "end": v(131.36, 64.26) * mm});
            skLineSegment(sketch, "E433", {"start": v(131.36, 64.26) * mm, "end": v(131.37, 64.4) * mm});
            skLineSegment(sketch, "E434", {"start": v(131.37, 64.4) * mm, "end": v(131.37, 64.54) * mm});
            skLineSegment(sketch, "E435", {"start": v(131.37, 64.54) * mm, "end": v(131.36, 64.75) * mm});
            skLineSegment(sketch, "E436", {"start": v(131.36, 64.75) * mm, "end": v(131.33, 64.93) * mm});
            skLineSegment(sketch, "E437", {"start": v(131.33, 64.93) * mm, "end": v(131.28, 65.08) * mm});
            skLineSegment(sketch, "E438", {"start": v(131.28, 65.08) * mm, "end": v(131.21, 65.2) * mm});
            skLineSegment(sketch, "E439", {"start": v(131.21, 65.2) * mm, "end": v(131.12, 65.3) * mm});
            skLineSegment(sketch, "E440", {"start": v(131.12, 65.3) * mm, "end": v(131, 65.38) * mm});
            skLineSegment(sketch, "E441", {"start": v(131, 65.38) * mm, "end": v(130.87, 65.42) * mm});
            skLineSegment(sketch, "E442", {"start": v(130.87, 65.42) * mm, "end": v(130.72, 65.43) * mm});
            skLineSegment(sketch, "E443", {"start": v(130.72, 65.43) * mm, "end": v(130.58, 65.42) * mm});
            skLineSegment(sketch, "E444", {"start": v(130.58, 65.42) * mm, "end": v(130.46, 65.38) * mm});
            skLineSegment(sketch, "E445", {"start": v(130.46, 65.38) * mm, "end": v(130.34, 65.32) * mm});
            skLineSegment(sketch, "E446", {"start": v(130.34, 65.32) * mm, "end": v(130.25, 65.23) * mm});
            skLineSegment(sketch, "E447", {"start": v(130.25, 65.23) * mm, "end": v(130.17, 65.13) * mm});
            skLineSegment(sketch, "E448", {"start": v(130.17, 65.13) * mm, "end": v(130.11, 65.02) * mm});
            skLineSegment(sketch, "E449", {"start": v(130.11, 65.02) * mm, "end": v(130.08, 64.9) * mm});
            skLineSegment(sketch, "E450", {"start": v(130.08, 64.9) * mm, "end": v(130.07, 64.79) * mm});
            skLineSegment(sketch, "E451", {"start": v(130.07, 64.79) * mm, "end": v(130.08, 64.66) * mm});
            skLineSegment(sketch, "E452", {"start": v(130.08, 64.66) * mm, "end": v(130.12, 64.53) * mm});
            skLineSegment(sketch, "E453", {"start": v(130.12, 64.53) * mm, "end": v(130.2, 64.4) * mm});
            skLineSegment(sketch, "E454", {"start": v(130.2, 64.4) * mm, "end": v(130.29, 64.27) * mm});
            skLineSegment(sketch, "E455", {"start": v(130.29, 64.27) * mm, "end": v(130.41, 64.14) * mm});
            skLineSegment(sketch, "E456", {"start": v(130.41, 64.14) * mm, "end": v(130.59, 63.99) * mm});
            skLineSegment(sketch, "E457", {"start": v(130.59, 63.99) * mm, "end": v(130.8, 63.83) * mm});
            skLineSegment(sketch, "E458", {"start": v(130.8, 63.83) * mm, "end": v(131.06, 63.65) * mm});
            skLineSegment(sketch, "E459", {"start": v(130.11, 62.6) * mm, "end": v(130.03, 62.52) * mm});
            skLineSegment(sketch, "E460", {"start": v(130.03, 62.52) * mm, "end": v(129.96, 62.43) * mm});
            skLineSegment(sketch, "E461", {"start": v(129.96, 62.43) * mm, "end": v(129.9, 62.33) * mm});
            skLineSegment(sketch, "E462", {"start": v(129.9, 62.33) * mm, "end": v(129.86, 62.23) * mm});
            skLineSegment(sketch, "E463", {"start": v(129.86, 62.23) * mm, "end": v(129.83, 62.1) * mm});
            skLineSegment(sketch, "E464", {"start": v(129.83, 62.1) * mm, "end": v(129.8, 61.95) * mm});
            skLineSegment(sketch, "E465", {"start": v(129.8, 61.95) * mm, "end": v(129.8, 61.78) * mm});
            skLineSegment(sketch, "E466", {"start": v(129.8, 61.78) * mm, "end": v(129.8, 61.57) * mm});
            skLineSegment(sketch, "E467", {"start": v(129.8, 61.57) * mm, "end": v(129.8, 61.28) * mm});
            skLineSegment(sketch, "E468", {"start": v(129.8, 61.28) * mm, "end": v(129.84, 61.03) * mm});
            skLineSegment(sketch, "E469", {"start": v(129.84, 61.03) * mm, "end": v(129.9, 60.82) * mm});
            skLineSegment(sketch, "E470", {"start": v(129.9, 60.82) * mm, "end": v(129.93, 60.73) * mm});
            skLineSegment(sketch, "E471", {"start": v(129.93, 60.73) * mm, "end": v(129.97, 60.66) * mm});
            skLineSegment(sketch, "E472", {"start": v(129.97, 60.66) * mm, "end": v(130.02, 60.59) * mm});
            skLineSegment(sketch, "E473", {"start": v(130.02, 60.59) * mm, "end": v(130.08, 60.53) * mm});
            skLineSegment(sketch, "E474", {"start": v(130.08, 60.53) * mm, "end": v(130.15, 60.48) * mm});
            skLineSegment(sketch, "E475", {"start": v(130.15, 60.48) * mm, "end": v(130.22, 60.44) * mm});
            skLineSegment(sketch, "E476", {"start": v(130.22, 60.44) * mm, "end": v(130.3, 60.4) * mm});
            skLineSegment(sketch, "E477", {"start": v(130.3, 60.4) * mm, "end": v(130.38, 60.38) * mm});
            skLineSegment(sketch, "E478", {"start": v(130.38, 60.38) * mm, "end": v(130.48, 60.37) * mm});
            skLineSegment(sketch, "E479", {"start": v(130.48, 60.37) * mm, "end": v(130.58, 60.36) * mm});
            skLineSegment(sketch, "E480", {"start": v(130.58, 60.36) * mm, "end": v(130.73, 60.38) * mm});
            skLineSegment(sketch, "E481", {"start": v(130.73, 60.38) * mm, "end": v(130.88, 60.41) * mm});
            skLineSegment(sketch, "E482", {"start": v(130.88, 60.41) * mm, "end": v(131, 60.48) * mm});
            skLineSegment(sketch, "E483", {"start": v(131, 60.48) * mm, "end": v(131.12, 60.56) * mm});
            skLineSegment(sketch, "E484", {"start": v(131.12, 60.56) * mm, "end": v(131.21, 60.67) * mm});
            skLineSegment(sketch, "E485", {"start": v(131.21, 60.67) * mm, "end": v(131.28, 60.8) * mm});
            skLineSegment(sketch, "E486", {"start": v(131.28, 60.8) * mm, "end": v(131.32, 60.95) * mm});
            skLineSegment(sketch, "E487", {"start": v(131.32, 60.95) * mm, "end": v(131.33, 61.11) * mm});
            skLineSegment(sketch, "E488", {"start": v(131.33, 61.11) * mm, "end": v(131.32, 61.27) * mm});
            skLineSegment(sketch, "E489", {"start": v(131.32, 61.27) * mm, "end": v(131.3, 61.42) * mm});
            skLineSegment(sketch, "E490", {"start": v(131.3, 61.42) * mm, "end": v(131.25, 61.55) * mm});
            skLineSegment(sketch, "E491", {"start": v(131.25, 61.55) * mm, "end": v(131.18, 61.67) * mm});
            skLineSegment(sketch, "E492", {"start": v(131.18, 61.67) * mm, "end": v(131.08, 61.78) * mm});
            skLineSegment(sketch, "E493", {"start": v(131.08, 61.78) * mm, "end": v(130.96, 61.91) * mm});
            skLineSegment(sketch, "E494", {"start": v(130.96, 61.91) * mm, "end": v(130.81, 62.05) * mm});
            skLineSegment(sketch, "E495", {"start": v(130.81, 62.05) * mm, "end": v(130.63, 62.2) * mm});
            skLineSegment(sketch, "E496", {"start": v(130.63, 62.2) * mm, "end": v(130.11, 62.6) * mm});
            skLineSegment(sketch, "E497", {"start": v(101.46, 64.29) * mm, "end": v(101.3, 64.24) * mm});
            skLineSegment(sketch, "E498", {"start": v(101.3, 64.24) * mm, "end": v(101.15, 64.2) * mm});
            skLineSegment(sketch, "E499", {"start": v(101.15, 64.2) * mm, "end": v(101.02, 64.18) * mm});
            skLineSegment(sketch, "E500", {"start": v(101.02, 64.18) * mm, "end": v(100.9, 64.17) * mm});
            skLineSegment(sketch, "E501", {"start": v(100.9, 64.17) * mm, "end": v(100.85, 64.18) * mm});
            skLineSegment(sketch, "E502", {"start": v(100.85, 64.18) * mm, "end": v(100.8, 64.2) * mm});
            skLineSegment(sketch, "E503", {"start": v(100.8, 64.2) * mm, "end": v(100.79, 64.24) * mm});
            skLineSegment(sketch, "E504", {"start": v(100.79, 64.24) * mm, "end": v(100.78, 64.3) * mm});
            skLineSegment(sketch, "E505", {"start": v(100.78, 64.3) * mm, "end": v(100.78, 64.45) * mm});
            skLineSegment(sketch, "E506", {"start": v(100.78, 64.45) * mm, "end": v(100.79, 64.52) * mm});
            skLineSegment(sketch, "E507", {"start": v(100.79, 64.52) * mm, "end": v(100.81, 64.57) * mm});
            skLineSegment(sketch, "E508", {"start": v(100.81, 64.57) * mm, "end": v(100.87, 64.62) * mm});
            skLineSegment(sketch, "E509", {"start": v(100.87, 64.62) * mm, "end": v(100.98, 64.67) * mm});
            skLineSegment(sketch, "E510", {"start": v(100.98, 64.67) * mm, "end": v(101.08, 64.72) * mm});
            skLineSegment(sketch, "E511", {"start": v(101.08, 64.72) * mm, "end": v(101.2, 64.78) * mm});
            skLineSegment(sketch, "E512", {"start": v(101.2, 64.78) * mm, "end": v(101.47, 64.97) * mm});
            skLineSegment(sketch, "E513", {"start": v(101.47, 64.97) * mm, "end": v(101.62, 65.1) * mm});
            skLineSegment(sketch, "E514", {"start": v(101.62, 65.1) * mm, "end": v(101.77, 65.23) * mm});
            skLineSegment(sketch, "E515", {"start": v(101.77, 65.23) * mm, "end": v(101.92, 65.4) * mm});
            skLineSegment(sketch, "E516", {"start": v(101.92, 65.4) * mm, "end": v(102.07, 65.58) * mm});
            skLineSegment(sketch, "E517", {"start": v(102.07, 65.58) * mm, "end": v(102.25, 65.8) * mm});
            skLineSegment(sketch, "E518", {"start": v(102.25, 65.8) * mm, "end": v(102.34, 65.9) * mm});
            skLineSegment(sketch, "E519", {"start": v(102.34, 65.9) * mm, "end": v(102.4, 65.91) * mm});
            skLineSegment(sketch, "E520", {"start": v(102.4, 65.91) * mm, "end": v(102.48, 65.92) * mm});
            skLineSegment(sketch, "E521", {"start": v(102.48, 65.92) * mm, "end": v(102.79, 65.92) * mm});
            skLineSegment(sketch, "E522", {"start": v(102.79, 65.92) * mm, "end": v(102.79, 60.54) * mm});
            skLineSegment(sketch, "E523", {"start": v(102.79, 60.54) * mm, "end": v(102.8, 60.5) * mm});
            skLineSegment(sketch, "E524", {"start": v(102.8, 60.5) * mm, "end": v(102.82, 60.46) * mm});
            skLineSegment(sketch, "E525", {"start": v(102.82, 60.46) * mm, "end": v(102.86, 60.43) * mm});
            skLineSegment(sketch, "E526", {"start": v(102.86, 60.43) * mm, "end": v(102.91, 60.4) * mm});
            skLineSegment(sketch, "E527", {"start": v(102.91, 60.4) * mm, "end": v(103, 60.34) * mm});
            skLineSegment(sketch, "E528", {"start": v(103, 60.34) * mm, "end": v(103.05, 60.28) * mm});
            skLineSegment(sketch, "E529", {"start": v(103.05, 60.28) * mm, "end": v(103.06, 60.18) * mm});
            skLineSegment(sketch, "E530", {"start": v(103.06, 60.18) * mm, "end": v(103.07, 59.98) * mm});
            skLineSegment(sketch, "E531", {"start": v(103.07, 59.98) * mm, "end": v(103.06, 59.94) * mm});
            skLineSegment(sketch, "E532", {"start": v(103.06, 59.94) * mm, "end": v(103.04, 59.9) * mm});
            skLineSegment(sketch, "E533", {"start": v(103.04, 59.9) * mm, "end": v(103, 59.9) * mm});
            skLineSegment(sketch, "E534", {"start": v(103, 59.9) * mm, "end": v(102.94, 59.88) * mm});
            skLineSegment(sketch, "E535", {"start": v(102.94, 59.88) * mm, "end": v(101.24, 59.88) * mm});
            skLineSegment(sketch, "E536", {"start": v(101.24, 59.88) * mm, "end": v(101.15, 59.9) * mm});
            skLineSegment(sketch, "E537", {"start": v(101.15, 59.9) * mm, "end": v(101.1, 59.92) * mm});
            skLineSegment(sketch, "E538", {"start": v(101.1, 59.92) * mm, "end": v(101.09, 59.98) * mm});
            skLineSegment(sketch, "E539", {"start": v(101.09, 59.98) * mm, "end": v(101.08, 60.08) * mm});
            skLineSegment(sketch, "E540", {"start": v(101.08, 60.08) * mm, "end": v(101.09, 60.23) * mm});
            skLineSegment(sketch, "E541", {"start": v(101.09, 60.23) * mm, "end": v(101.1, 60.31) * mm});
            skLineSegment(sketch, "E542", {"start": v(101.1, 60.31) * mm, "end": v(101.12, 60.33) * mm});
            skLineSegment(sketch, "E543", {"start": v(101.12, 60.33) * mm, "end": v(101.15, 60.36) * mm});
            skLineSegment(sketch, "E544", {"start": v(101.15, 60.36) * mm, "end": v(101.26, 60.4) * mm});
            skLineSegment(sketch, "E545", {"start": v(101.26, 60.4) * mm, "end": v(101.35, 60.43) * mm});
            skLineSegment(sketch, "E546", {"start": v(101.35, 60.43) * mm, "end": v(101.41, 60.47) * mm});
            skLineSegment(sketch, "E547", {"start": v(101.41, 60.47) * mm, "end": v(101.45, 60.52) * mm});
            skLineSegment(sketch, "E548", {"start": v(101.45, 60.52) * mm, "end": v(101.46, 60.58) * mm});
            skLineSegment(sketch, "E549", {"start": v(101.46, 60.58) * mm, "end": v(101.46, 64.29) * mm});
            skLineSegment(sketch, "E550", {"start": v(105.43, 65.91) * mm, "end": v(105.55, 65.9) * mm});
            skLineSegment(sketch, "E551", {"start": v(105.55, 65.9) * mm, "end": v(105.66, 65.89) * mm});
            skLineSegment(sketch, "E552", {"start": v(105.66, 65.89) * mm, "end": v(105.77, 65.86) * mm});
            skLineSegment(sketch, "E553", {"start": v(105.77, 65.86) * mm, "end": v(105.88, 65.81) * mm});
            skLineSegment(sketch, "E554", {"start": v(105.88, 65.81) * mm, "end": v(106, 65.76) * mm});
            skLineSegment(sketch, "E555", {"start": v(106, 65.76) * mm, "end": v(106.1, 65.7) * mm});
            skLineSegment(sketch, "E556", {"start": v(106.1, 65.7) * mm, "end": v(106.2, 65.61) * mm});
            skLineSegment(sketch, "E557", {"start": v(106.2, 65.61) * mm, "end": v(106.3, 65.52) * mm});
            skLineSegment(sketch, "E558", {"start": v(106.3, 65.52) * mm, "end": v(106.4, 65.42) * mm});
            skLineSegment(sketch, "E559", {"start": v(106.4, 65.42) * mm, "end": v(106.5, 65.31) * mm});
            skLineSegment(sketch, "E560", {"start": v(106.5, 65.31) * mm, "end": v(106.58, 65.2) * mm});
            skLineSegment(sketch, "E561", {"start": v(106.58, 65.2) * mm, "end": v(106.66, 65.07) * mm});
            skLineSegment(sketch, "E562", {"start": v(106.66, 65.07) * mm, "end": v(106.73, 64.93) * mm});
            skLineSegment(sketch, "E563", {"start": v(106.73, 64.93) * mm, "end": v(106.8, 64.79) * mm});
            skLineSegment(sketch, "E564", {"start": v(106.8, 64.79) * mm, "end": v(106.9, 64.47) * mm});
            skLineSegment(sketch, "E565", {"start": v(106.9, 64.47) * mm, "end": v(107, 64.13) * mm});
            skLineSegment(sketch, "E566", {"start": v(107, 64.13) * mm, "end": v(107.06, 63.75) * mm});
            skLineSegment(sketch, "E567", {"start": v(107.06, 63.75) * mm, "end": v(107.1, 63.34) * mm});
            skLineSegment(sketch, "E568", {"start": v(107.1, 63.34) * mm, "end": v(107.1, 62.9) * mm});
            skLineSegment(sketch, "E569", {"start": v(107.1, 62.9) * mm, "end": v(107.1, 62.53) * mm});
            skLineSegment(sketch, "E570", {"start": v(107.1, 62.53) * mm, "end": v(107.08, 62.19) * mm});
            skLineSegment(sketch, "E571", {"start": v(107.08, 62.19) * mm, "end": v(107.04, 61.87) * mm});
            skLineSegment(sketch, "E572", {"start": v(107.04, 61.87) * mm, "end": v(106.98, 61.57) * mm});
            skLineSegment(sketch, "E573", {"start": v(106.98, 61.57) * mm, "end": v(106.91, 61.3) * mm});
            skLineSegment(sketch, "E574", {"start": v(106.91, 61.3) * mm, "end": v(106.82, 61.04) * mm});
            skLineSegment(sketch, "E575", {"start": v(106.82, 61.04) * mm, "end": v(106.72, 60.8) * mm});
            skLineSegment(sketch, "E576", {"start": v(106.72, 60.8) * mm, "end": v(106.6, 60.6) * mm});
            skLineSegment(sketch, "E577", {"start": v(106.6, 60.6) * mm, "end": v(106.47, 60.42) * mm});
            skLineSegment(sketch, "E578", {"start": v(106.47, 60.42) * mm, "end": v(106.34, 60.26) * mm});
            skLineSegment(sketch, "E579", {"start": v(106.34, 60.26) * mm, "end": v(106.2, 60.13) * mm});
            skLineSegment(sketch, "E580", {"start": v(106.2, 60.13) * mm, "end": v(106.05, 60.02) * mm});
            skLineSegment(sketch, "E581", {"start": v(106.05, 60.02) * mm, "end": v(105.89, 59.93) * mm});
            skLineSegment(sketch, "E582", {"start": v(105.89, 59.93) * mm, "end": v(105.73, 59.87) * mm});
            skLineSegment(sketch, "E583", {"start": v(105.73, 59.87) * mm, "end": v(105.56, 59.83) * mm});
            skLineSegment(sketch, "E584", {"start": v(105.56, 59.83) * mm, "end": v(105.38, 59.82) * mm});
            skLineSegment(sketch, "E585", {"start": v(105.38, 59.82) * mm, "end": v(105.21, 59.83) * mm});
            skLineSegment(sketch, "E586", {"start": v(105.21, 59.83) * mm, "end": v(105.05, 59.87) * mm});
            skLineSegment(sketch, "E587", {"start": v(105.05, 59.87) * mm, "end": v(104.9, 59.93) * mm});
            skLineSegment(sketch, "E588", {"start": v(104.9, 59.93) * mm, "end": v(104.74, 60) * mm});
            skLineSegment(sketch, "E589", {"start": v(104.74, 60) * mm, "end": v(104.6, 60.11) * mm});
            skLineSegment(sketch, "E590", {"start": v(104.6, 60.11) * mm, "end": v(104.46, 60.24) * mm});
            skLineSegment(sketch, "E591", {"start": v(104.46, 60.24) * mm, "end": v(104.33, 60.4) * mm});
            skLineSegment(sketch, "E592", {"start": v(104.33, 60.4) * mm, "end": v(104.2, 60.56) * mm});
            skLineSegment(sketch, "E593", {"start": v(104.2, 60.56) * mm, "end": v(104.08, 60.76) * mm});
            skLineSegment(sketch, "E594", {"start": v(104.08, 60.76) * mm, "end": v(103.98, 60.99) * mm});
            skLineSegment(sketch, "E595", {"start": v(103.98, 60.99) * mm, "end": v(103.9, 61.23) * mm});
            skLineSegment(sketch, "E596", {"start": v(103.9, 61.23) * mm, "end": v(103.83, 61.5) * mm});
            skLineSegment(sketch, "E597", {"start": v(103.83, 61.5) * mm, "end": v(103.78, 61.8) * mm});
            skLineSegment(sketch, "E598", {"start": v(103.78, 61.8) * mm, "end": v(103.74, 62.12) * mm});
            skLineSegment(sketch, "E599", {"start": v(103.74, 62.12) * mm, "end": v(103.71, 62.47) * mm});
            skLineSegment(sketch, "E600", {"start": v(103.71, 62.47) * mm, "end": v(103.7, 62.84) * mm});
            skLineSegment(sketch, "E601", {"start": v(103.7, 62.84) * mm, "end": v(103.71, 63.2) * mm});
            skLineSegment(sketch, "E602", {"start": v(103.71, 63.2) * mm, "end": v(103.74, 63.55) * mm});
            skLineSegment(sketch, "E603", {"start": v(103.74, 63.55) * mm, "end": v(103.77, 63.88) * mm});
            skLineSegment(sketch, "E604", {"start": v(103.77, 63.88) * mm, "end": v(103.83, 64.18) * mm});
            skLineSegment(sketch, "E605", {"start": v(103.83, 64.18) * mm, "end": v(103.9, 64.45) * mm});
            skLineSegment(sketch, "E606", {"start": v(103.9, 64.45) * mm, "end": v(103.98, 64.7) * mm});
            skLineSegment(sketch, "E607", {"start": v(103.98, 64.7) * mm, "end": v(104.08, 64.93) * mm});
            skLineSegment(sketch, "E608", {"start": v(104.08, 64.93) * mm, "end": v(104.2, 65.14) * mm});
            skLineSegment(sketch, "E609", {"start": v(104.2, 65.14) * mm, "end": v(104.32, 65.32) * mm});
            skLineSegment(sketch, "E610", {"start": v(104.32, 65.32) * mm, "end": v(104.46, 65.48) * mm});
            skLineSegment(sketch, "E611", {"start": v(104.46, 65.48) * mm, "end": v(104.6, 65.6) * mm});
            skLineSegment(sketch, "E612", {"start": v(104.6, 65.6) * mm, "end": v(104.75, 65.72) * mm});
            skLineSegment(sketch, "E613", {"start": v(104.75, 65.72) * mm, "end": v(104.9, 65.8) * mm});
            skLineSegment(sketch, "E614", {"start": v(104.9, 65.8) * mm, "end": v(105.07, 65.86) * mm});
            skLineSegment(sketch, "E615", {"start": v(105.07, 65.86) * mm, "end": v(105.25, 65.9) * mm});
            skLineSegment(sketch, "E616", {"start": v(105.25, 65.9) * mm, "end": v(105.43, 65.91) * mm});
            skLineSegment(sketch, "E617", {"start": v(105.66, 64.96) * mm, "end": v(105.66, 65.08) * mm});
            skLineSegment(sketch, "E618", {"start": v(105.66, 65.08) * mm, "end": v(105.65, 65.18) * mm});
            skLineSegment(sketch, "E619", {"start": v(105.65, 65.18) * mm, "end": v(105.63, 65.26) * mm});
            skLineSegment(sketch, "E620", {"start": v(105.63, 65.26) * mm, "end": v(105.6, 65.32) * mm});
            skLineSegment(sketch, "E621", {"start": v(105.6, 65.32) * mm, "end": v(105.56, 65.37) * mm});
            skLineSegment(sketch, "E622", {"start": v(105.56, 65.37) * mm, "end": v(105.52, 65.4) * mm});
            skLineSegment(sketch, "E623", {"start": v(105.52, 65.4) * mm, "end": v(105.46, 65.42) * mm});
            skLineSegment(sketch, "E624", {"start": v(105.46, 65.42) * mm, "end": v(105.4, 65.43) * mm});
            skLineSegment(sketch, "E625", {"start": v(105.4, 65.43) * mm, "end": v(105.33, 65.42) * mm});
            skLineSegment(sketch, "E626", {"start": v(105.33, 65.42) * mm, "end": v(105.28, 65.4) * mm});
            skLineSegment(sketch, "E627", {"start": v(105.28, 65.4) * mm, "end": v(105.23, 65.36) * mm});
            skLineSegment(sketch, "E628", {"start": v(105.23, 65.36) * mm, "end": v(105.2, 65.3) * mm});
            skLineSegment(sketch, "E629", {"start": v(105.2, 65.3) * mm, "end": v(105.16, 65.24) * mm});
            skLineSegment(sketch, "E630", {"start": v(105.16, 65.24) * mm, "end": v(105.14, 65.16) * mm});
            skLineSegment(sketch, "E631", {"start": v(105.14, 65.16) * mm, "end": v(105.13, 65.07) * mm});
            skLineSegment(sketch, "E632", {"start": v(105.13, 65.07) * mm, "end": v(105.12, 64.96) * mm});
            skLineSegment(sketch, "E633", {"start": v(105.12, 64.96) * mm, "end": v(105.12, 60.65) * mm});
            skLineSegment(sketch, "E634", {"start": v(105.12, 60.65) * mm, "end": v(105.13, 60.57) * mm});
            skLineSegment(sketch, "E635", {"start": v(105.13, 60.57) * mm, "end": v(105.14, 60.5) * mm});
            skLineSegment(sketch, "E636", {"start": v(105.14, 60.5) * mm, "end": v(105.16, 60.43) * mm});
            skLineSegment(sketch, "E637", {"start": v(105.16, 60.43) * mm, "end": v(105.19, 60.38) * mm});
            skLineSegment(sketch, "E638", {"start": v(105.19, 60.38) * mm, "end": v(105.22, 60.34) * mm});
            skLineSegment(sketch, "E639", {"start": v(105.22, 60.34) * mm, "end": v(105.27, 60.31) * mm});
            skLineSegment(sketch, "E640", {"start": v(105.27, 60.31) * mm, "end": v(105.32, 60.3) * mm});
            skLineSegment(sketch, "E641", {"start": v(105.32, 60.3) * mm, "end": v(105.38, 60.29) * mm});
            skLineSegment(sketch, "E642", {"start": v(105.38, 60.29) * mm, "end": v(105.44, 60.3) * mm});
            skLineSegment(sketch, "E643", {"start": v(105.44, 60.3) * mm, "end": v(105.5, 60.32) * mm});
            skLineSegment(sketch, "E644", {"start": v(105.5, 60.32) * mm, "end": v(105.54, 60.35) * mm});
            skLineSegment(sketch, "E645", {"start": v(105.54, 60.35) * mm, "end": v(105.59, 60.4) * mm});
            skLineSegment(sketch, "E646", {"start": v(105.59, 60.4) * mm, "end": v(105.62, 60.45) * mm});
            skLineSegment(sketch, "E647", {"start": v(105.62, 60.45) * mm, "end": v(105.64, 60.52) * mm});
            skLineSegment(sketch, "E648", {"start": v(105.64, 60.52) * mm, "end": v(105.66, 60.58) * mm});
            skLineSegment(sketch, "E649", {"start": v(105.66, 60.58) * mm, "end": v(105.66, 60.65) * mm});
            skLineSegment(sketch, "E650", {"start": v(105.66, 60.65) * mm, "end": v(105.66, 64.96) * mm});
            skLineSegment(sketch, "E651", {"start": v(68.12, 64.25) * mm, "end": v(67.96, 64.2) * mm});
            skLineSegment(sketch, "E652", {"start": v(67.96, 64.2) * mm, "end": v(67.8, 64.17) * mm});
            skLineSegment(sketch, "E653", {"start": v(67.8, 64.17) * mm, "end": v(67.67, 64.15) * mm});
            skLineSegment(sketch, "E654", {"start": v(67.67, 64.15) * mm, "end": v(67.55, 64.14) * mm});
            skLineSegment(sketch, "E655", {"start": v(67.55, 64.14) * mm, "end": v(67.5, 64.15) * mm});
            skLineSegment(sketch, "E656", {"start": v(67.5, 64.15) * mm, "end": v(67.46, 64.17) * mm});
            skLineSegment(sketch, "E657", {"start": v(67.46, 64.17) * mm, "end": v(67.44, 64.21) * mm});
            skLineSegment(sketch, "E658", {"start": v(67.44, 64.21) * mm, "end": v(67.43, 64.27) * mm});
            skLineSegment(sketch, "E659", {"start": v(67.43, 64.27) * mm, "end": v(67.43, 64.41) * mm});
            skLineSegment(sketch, "E660", {"start": v(67.43, 64.41) * mm, "end": v(67.44, 64.49) * mm});
            skLineSegment(sketch, "E661", {"start": v(67.44, 64.49) * mm, "end": v(67.47, 64.54) * mm});
            skLineSegment(sketch, "E662", {"start": v(67.47, 64.54) * mm, "end": v(67.52, 64.59) * mm});
            skLineSegment(sketch, "E663", {"start": v(67.52, 64.59) * mm, "end": v(67.63, 64.64) * mm});
            skLineSegment(sketch, "E664", {"start": v(67.63, 64.64) * mm, "end": v(67.73, 64.68) * mm});
            skLineSegment(sketch, "E665", {"start": v(67.73, 64.68) * mm, "end": v(67.84, 64.75) * mm});
            skLineSegment(sketch, "E666", {"start": v(67.84, 64.75) * mm, "end": v(68.12, 64.94) * mm});
            skLineSegment(sketch, "E667", {"start": v(68.12, 64.94) * mm, "end": v(68.27, 65.06) * mm});
            skLineSegment(sketch, "E668", {"start": v(68.27, 65.06) * mm, "end": v(68.42, 65.2) * mm});
            skLineSegment(sketch, "E669", {"start": v(68.42, 65.2) * mm, "end": v(68.57, 65.36) * mm});
            skLineSegment(sketch, "E670", {"start": v(68.57, 65.36) * mm, "end": v(68.72, 65.54) * mm});
            skLineSegment(sketch, "E671", {"start": v(68.72, 65.54) * mm, "end": v(68.9, 65.77) * mm});
            skLineSegment(sketch, "E672", {"start": v(68.9, 65.77) * mm, "end": v(68.99, 65.86) * mm});
            skLineSegment(sketch, "E673", {"start": v(68.99, 65.86) * mm, "end": v(69.05, 65.88) * mm});
            skLineSegment(sketch, "E674", {"start": v(69.05, 65.88) * mm, "end": v(69.13, 65.89) * mm});
            skLineSegment(sketch, "E675", {"start": v(69.13, 65.89) * mm, "end": v(69.44, 65.89) * mm});
            skLineSegment(sketch, "E676", {"start": v(69.44, 65.89) * mm, "end": v(69.44, 60.5) * mm});
            skLineSegment(sketch, "E677", {"start": v(69.44, 60.5) * mm, "end": v(69.45, 60.47) * mm});
            skLineSegment(sketch, "E678", {"start": v(69.45, 60.47) * mm, "end": v(69.47, 60.43) * mm});
            skLineSegment(sketch, "E679", {"start": v(69.47, 60.43) * mm, "end": v(69.51, 60.4) * mm});
            skLineSegment(sketch, "E680", {"start": v(69.51, 60.4) * mm, "end": v(69.57, 60.36) * mm});
            skLineSegment(sketch, "E681", {"start": v(69.57, 60.36) * mm, "end": v(69.65, 60.3) * mm});
            skLineSegment(sketch, "E682", {"start": v(69.65, 60.3) * mm, "end": v(69.7, 60.25) * mm});
            skLineSegment(sketch, "E683", {"start": v(69.7, 60.25) * mm, "end": v(69.72, 60.15) * mm});
            skLineSegment(sketch, "E684", {"start": v(69.72, 60.15) * mm, "end": v(69.72, 59.95) * mm});
            skLineSegment(sketch, "E685", {"start": v(69.72, 59.95) * mm, "end": v(69.71, 59.9) * mm});
            skLineSegment(sketch, "E686", {"start": v(69.71, 59.9) * mm, "end": v(69.69, 59.88) * mm});
            skLineSegment(sketch, "E687", {"start": v(69.69, 59.88) * mm, "end": v(69.65, 59.86) * mm});
            skLineSegment(sketch, "E688", {"start": v(69.65, 59.86) * mm, "end": v(69.6, 59.85) * mm});
            skLineSegment(sketch, "E689", {"start": v(69.6, 59.85) * mm, "end": v(67.89, 59.85) * mm});
            skLineSegment(sketch, "E690", {"start": v(67.89, 59.85) * mm, "end": v(67.8, 59.86) * mm});
            skLineSegment(sketch, "E691", {"start": v(67.8, 59.86) * mm, "end": v(67.76, 59.89) * mm});
            skLineSegment(sketch, "E692", {"start": v(67.76, 59.89) * mm, "end": v(67.74, 59.94) * mm});
            skLineSegment(sketch, "E693", {"start": v(67.74, 59.94) * mm, "end": v(67.73, 60.05) * mm});
            skLineSegment(sketch, "E694", {"start": v(67.73, 60.05) * mm, "end": v(67.74, 60.2) * mm});
            skLineSegment(sketch, "E695", {"start": v(67.74, 60.2) * mm, "end": v(67.75, 60.28) * mm});
            skLineSegment(sketch, "E696", {"start": v(67.75, 60.28) * mm, "end": v(67.77, 60.3) * mm});
            skLineSegment(sketch, "E697", {"start": v(67.77, 60.3) * mm, "end": v(67.8, 60.32) * mm});
            skLineSegment(sketch, "E698", {"start": v(67.8, 60.32) * mm, "end": v(67.9, 60.37) * mm});
            skLineSegment(sketch, "E699", {"start": v(67.9, 60.37) * mm, "end": v(68, 60.4) * mm});
            skLineSegment(sketch, "E700", {"start": v(68, 60.4) * mm, "end": v(68.06, 60.44) * mm});
            skLineSegment(sketch, "E701", {"start": v(68.06, 60.44) * mm, "end": v(68.1, 60.5) * mm});
            skLineSegment(sketch, "E702", {"start": v(68.1, 60.5) * mm, "end": v(68.12, 60.55) * mm});
            skLineSegment(sketch, "E703", {"start": v(68.12, 60.55) * mm, "end": v(68.12, 64.25) * mm});
            skLineSegment(sketch, "E704", {"start": v(71.1, 60.97) * mm, "end": v(72.96, 60.97) * mm});
            skLineSegment(sketch, "E705", {"start": v(72.96, 60.97) * mm, "end": v(73.02, 60.97) * mm});
            skLineSegment(sketch, "E706", {"start": v(73.02, 60.97) * mm, "end": v(73.07, 61) * mm});
            skLineSegment(sketch, "E707", {"start": v(73.07, 61) * mm, "end": v(73.12, 61.02) * mm});
            skLineSegment(sketch, "E708", {"start": v(73.12, 61.02) * mm, "end": v(73.16, 61.06) * mm});
            skLineSegment(sketch, "E709", {"start": v(73.16, 61.06) * mm, "end": v(73.2, 61.12) * mm});
            skLineSegment(sketch, "E710", {"start": v(73.2, 61.12) * mm, "end": v(73.23, 61.2) * mm});
            skLineSegment(sketch, "E711", {"start": v(73.23, 61.2) * mm, "end": v(73.28, 61.42) * mm});
            skLineSegment(sketch, "E712", {"start": v(73.28, 61.42) * mm, "end": v(73.31, 61.5) * mm});
            skLineSegment(sketch, "E713", {"start": v(73.31, 61.5) * mm, "end": v(73.35, 61.56) * mm});
            skLineSegment(sketch, "E714", {"start": v(73.35, 61.56) * mm, "end": v(73.43, 61.59) * mm});
            skLineSegment(sketch, "E715", {"start": v(73.43, 61.59) * mm, "end": v(73.56, 61.6) * mm});
            skLineSegment(sketch, "E716", {"start": v(73.56, 61.6) * mm, "end": v(73.66, 61.59) * mm});
            skLineSegment(sketch, "E717", {"start": v(73.66, 61.59) * mm, "end": v(73.73, 61.57) * mm});
            skLineSegment(sketch, "E718", {"start": v(73.73, 61.57) * mm, "end": v(73.77, 61.54) * mm});
            skLineSegment(sketch, "E719", {"start": v(73.77, 61.54) * mm, "end": v(73.79, 61.5) * mm});
            skLineSegment(sketch, "E720", {"start": v(73.79, 61.5) * mm, "end": v(73.78, 61.42) * mm});
            skLineSegment(sketch, "E721", {"start": v(73.78, 61.42) * mm, "end": v(73.7, 60.94) * mm});
            skLineSegment(sketch, "E722", {"start": v(73.7, 60.94) * mm, "end": v(73.57, 60.22) * mm});
            skLineSegment(sketch, "E723", {"start": v(73.57, 60.22) * mm, "end": v(73.51, 59.98) * mm});
            skLineSegment(sketch, "E724", {"start": v(73.51, 59.98) * mm, "end": v(73.49, 59.91) * mm});
            skLineSegment(sketch, "E725", {"start": v(73.49, 59.91) * mm, "end": v(73.47, 59.88) * mm});
            skLineSegment(sketch, "E726", {"start": v(73.47, 59.88) * mm, "end": v(73.41, 59.86) * mm});
            skLineSegment(sketch, "E727", {"start": v(73.41, 59.86) * mm, "end": v(73.3, 59.85) * mm});
            skLineSegment(sketch, "E728", {"start": v(73.3, 59.85) * mm, "end": v(70.37, 59.85) * mm});
            skLineSegment(sketch, "E729", {"start": v(70.37, 59.85) * mm, "end": v(70.37, 60.72) * mm});
            skLineSegment(sketch, "E730", {"start": v(70.37, 60.72) * mm, "end": v(70.38, 60.82) * mm});
            skLineSegment(sketch, "E731", {"start": v(70.38, 60.82) * mm, "end": v(70.44, 60.93) * mm});
            skLineSegment(sketch, "E732", {"start": v(70.44, 60.93) * mm, "end": v(70.54, 61.05) * mm});
            skLineSegment(sketch, "E733", {"start": v(70.54, 61.05) * mm, "end": v(70.68, 61.18) * mm});
            skLineSegment(sketch, "E734", {"start": v(70.68, 61.18) * mm, "end": v(70.78, 61.29) * mm});
            skLineSegment(sketch, "E735", {"start": v(70.78, 61.29) * mm, "end": v(70.94, 61.47) * mm});
            skLineSegment(sketch, "E736", {"start": v(70.94, 61.47) * mm, "end": v(71.4, 62.03) * mm});
            skLineSegment(sketch, "E737", {"start": v(71.4, 62.03) * mm, "end": v(71.66, 62.37) * mm});
            skLineSegment(sketch, "E738", {"start": v(71.66, 62.37) * mm, "end": v(71.87, 62.68) * mm});
            skLineSegment(sketch, "E739", {"start": v(71.87, 62.68) * mm, "end": v(72.03, 62.95) * mm});
            skLineSegment(sketch, "E740", {"start": v(72.03, 62.95) * mm, "end": v(72.13, 63.2) * mm});
            skLineSegment(sketch, "E741", {"start": v(72.13, 63.2) * mm, "end": v(72.2, 63.44) * mm});
            skLineSegment(sketch, "E742", {"start": v(72.2, 63.44) * mm, "end": v(72.26, 63.72) * mm});
            skLineSegment(sketch, "E743", {"start": v(72.26, 63.72) * mm, "end": v(72.3, 64.04) * mm});
            skLineSegment(sketch, "E744", {"start": v(72.3, 64.04) * mm, "end": v(72.3, 64.4) * mm});
            skLineSegment(sketch, "E745", {"start": v(72.3, 64.4) * mm, "end": v(72.3, 64.68) * mm});
            skLineSegment(sketch, "E746", {"start": v(72.3, 64.68) * mm, "end": v(72.27, 64.91) * mm});
            skLineSegment(sketch, "E747", {"start": v(72.27, 64.91) * mm, "end": v(72.23, 65.09) * mm});
            skLineSegment(sketch, "E748", {"start": v(72.23, 65.09) * mm, "end": v(72.2, 65.15) * mm});
            skLineSegment(sketch, "E749", {"start": v(72.2, 65.15) * mm, "end": v(72.18, 65.2) * mm});
            skLineSegment(sketch, "E750", {"start": v(72.18, 65.2) * mm, "end": v(72.11, 65.28) * mm});
            skLineSegment(sketch, "E751", {"start": v(72.11, 65.28) * mm, "end": v(72.03, 65.34) * mm});
            skLineSegment(sketch, "E752", {"start": v(72.03, 65.34) * mm, "end": v(71.94, 65.37) * mm});
            skLineSegment(sketch, "E753", {"start": v(71.94, 65.37) * mm, "end": v(71.83, 65.38) * mm});
            skLineSegment(sketch, "E754", {"start": v(71.83, 65.38) * mm, "end": v(71.75, 65.38) * mm});
            skLineSegment(sketch, "E755", {"start": v(71.75, 65.38) * mm, "end": v(71.68, 65.36) * mm});
            skLineSegment(sketch, "E756", {"start": v(71.68, 65.36) * mm, "end": v(71.62, 65.33) * mm});
            skLineSegment(sketch, "E757", {"start": v(71.62, 65.33) * mm, "end": v(71.57, 65.29) * mm});
            skLineSegment(sketch, "E758", {"start": v(71.57, 65.29) * mm, "end": v(71.52, 65.24) * mm});
            skLineSegment(sketch, "E759", {"start": v(71.52, 65.24) * mm, "end": v(71.5, 65.18) * mm});
            skLineSegment(sketch, "E760", {"start": v(71.5, 65.18) * mm, "end": v(71.48, 65.1) * mm});
            skLineSegment(sketch, "E761", {"start": v(71.48, 65.1) * mm, "end": v(71.47, 65.03) * mm});
            skLineSegment(sketch, "E762", {"start": v(71.47, 65.03) * mm, "end": v(71.49, 64.82) * mm});
            skLineSegment(sketch, "E763", {"start": v(71.49, 64.82) * mm, "end": v(71.5, 64.65) * mm});
            skLineSegment(sketch, "E764", {"start": v(71.5, 64.65) * mm, "end": v(71.51, 64.5) * mm});
            skLineSegment(sketch, "E765", {"start": v(71.51, 64.5) * mm, "end": v(71.5, 64.34) * mm});
            skLineSegment(sketch, "E766", {"start": v(71.5, 64.34) * mm, "end": v(71.47, 64.2) * mm});
            skLineSegment(sketch, "E767", {"start": v(71.47, 64.2) * mm, "end": v(71.42, 64.07) * mm});
            skLineSegment(sketch, "E768", {"start": v(71.42, 64.07) * mm, "end": v(71.36, 63.97) * mm});
            skLineSegment(sketch, "E769", {"start": v(71.36, 63.97) * mm, "end": v(71.27, 63.9) * mm});
            skLineSegment(sketch, "E770", {"start": v(71.27, 63.9) * mm, "end": v(71.18, 63.83) * mm});
            skLineSegment(sketch, "E771", {"start": v(71.18, 63.83) * mm, "end": v(71.08, 63.8) * mm});
            skLineSegment(sketch, "E772", {"start": v(71.08, 63.8) * mm, "end": v(70.96, 63.79) * mm});
            skLineSegment(sketch, "E773", {"start": v(70.96, 63.79) * mm, "end": v(70.84, 63.8) * mm});
            skLineSegment(sketch, "E774", {"start": v(70.84, 63.8) * mm, "end": v(70.74, 63.84) * mm});
            skLineSegment(sketch, "E775", {"start": v(70.74, 63.84) * mm, "end": v(70.64, 63.9) * mm});
            skLineSegment(sketch, "E776", {"start": v(70.64, 63.9) * mm, "end": v(70.56, 63.99) * mm});
            skLineSegment(sketch, "E777", {"start": v(70.56, 63.99) * mm, "end": v(70.5, 64.1) * mm});
            skLineSegment(sketch, "E778", {"start": v(70.5, 64.1) * mm, "end": v(70.45, 64.2) * mm});
            skLineSegment(sketch, "E779", {"start": v(70.45, 64.2) * mm, "end": v(70.42, 64.33) * mm});
            skLineSegment(sketch, "E780", {"start": v(70.42, 64.33) * mm, "end": v(70.41, 64.47) * mm});
            skLineSegment(sketch, "E781", {"start": v(70.41, 64.47) * mm, "end": v(70.42, 64.61) * mm});
            skLineSegment(sketch, "E782", {"start": v(70.42, 64.61) * mm, "end": v(70.44, 64.75) * mm});
            skLineSegment(sketch, "E783", {"start": v(70.44, 64.75) * mm, "end": v(70.48, 64.89) * mm});
            skLineSegment(sketch, "E784", {"start": v(70.48, 64.89) * mm, "end": v(70.52, 65.01) * mm});
            skLineSegment(sketch, "E785", {"start": v(70.52, 65.01) * mm, "end": v(70.58, 65.14) * mm});
            skLineSegment(sketch, "E786", {"start": v(70.58, 65.14) * mm, "end": v(70.66, 65.25) * mm});
            skLineSegment(sketch, "E787", {"start": v(70.66, 65.25) * mm, "end": v(70.75, 65.36) * mm});
            skLineSegment(sketch, "E788", {"start": v(70.75, 65.36) * mm, "end": v(70.85, 65.47) * mm});
            skLineSegment(sketch, "E789", {"start": v(70.85, 65.47) * mm, "end": v(70.97, 65.56) * mm});
            skLineSegment(sketch, "E790", {"start": v(70.97, 65.56) * mm, "end": v(71.1, 65.65) * mm});
            skLineSegment(sketch, "E791", {"start": v(71.1, 65.65) * mm, "end": v(71.22, 65.72) * mm});
            skLineSegment(sketch, "E792", {"start": v(71.22, 65.72) * mm, "end": v(71.37, 65.78) * mm});
            skLineSegment(sketch, "E793", {"start": v(71.37, 65.78) * mm, "end": v(71.52, 65.82) * mm});
            skLineSegment(sketch, "E794", {"start": v(71.52, 65.82) * mm, "end": v(71.68, 65.85) * mm});
            skLineSegment(sketch, "E795", {"start": v(71.68, 65.85) * mm, "end": v(71.85, 65.87) * mm});
            skLineSegment(sketch, "E796", {"start": v(71.85, 65.87) * mm, "end": v(72.03, 65.88) * mm});
            skLineSegment(sketch, "E797", {"start": v(72.03, 65.88) * mm, "end": v(72.2, 65.87) * mm});
            skLineSegment(sketch, "E798", {"start": v(72.2, 65.87) * mm, "end": v(72.38, 65.85) * mm});
            skLineSegment(sketch, "E799", {"start": v(72.38, 65.85) * mm, "end": v(72.55, 65.81) * mm});
            skLineSegment(sketch, "E800", {"start": v(72.55, 65.81) * mm, "end": v(72.7, 65.76) * mm});
            skLineSegment(sketch, "E801", {"start": v(72.7, 65.76) * mm, "end": v(72.86, 65.7) * mm});
            skLineSegment(sketch, "E802", {"start": v(72.86, 65.7) * mm, "end": v(73, 65.61) * mm});
            skLineSegment(sketch, "E803", {"start": v(73, 65.61) * mm, "end": v(73.13, 65.52) * mm});
            skLineSegment(sketch, "E804", {"start": v(73.13, 65.52) * mm, "end": v(73.26, 65.4) * mm});
            skLineSegment(sketch, "E805", {"start": v(73.26, 65.4) * mm, "end": v(73.37, 65.28) * mm});
            skLineSegment(sketch, "E806", {"start": v(73.37, 65.28) * mm, "end": v(73.47, 65.15) * mm});
            skLineSegment(sketch, "E807", {"start": v(73.47, 65.15) * mm, "end": v(73.55, 65.01) * mm});
            skLineSegment(sketch, "E808", {"start": v(73.55, 65.01) * mm, "end": v(73.62, 64.86) * mm});
            skLineSegment(sketch, "E809", {"start": v(73.62, 64.86) * mm, "end": v(73.67, 64.7) * mm});
            skLineSegment(sketch, "E810", {"start": v(73.67, 64.7) * mm, "end": v(73.7, 64.54) * mm});
            skLineSegment(sketch, "E811", {"start": v(73.7, 64.54) * mm, "end": v(73.73, 64.37) * mm});
            skLineSegment(sketch, "E812", {"start": v(73.73, 64.37) * mm, "end": v(73.74, 64.18) * mm});
            skLineSegment(sketch, "E813", {"start": v(73.74, 64.18) * mm, "end": v(73.73, 63.98) * mm});
            skLineSegment(sketch, "E814", {"start": v(73.73, 63.98) * mm, "end": v(73.7, 63.78) * mm});
            skLineSegment(sketch, "E815", {"start": v(73.7, 63.78) * mm, "end": v(73.64, 63.58) * mm});
            skLineSegment(sketch, "E816", {"start": v(73.64, 63.58) * mm, "end": v(73.57, 63.39) * mm});
            skLineSegment(sketch, "E817", {"start": v(73.57, 63.39) * mm, "end": v(73.47, 63.2) * mm});
            skLineSegment(sketch, "E818", {"start": v(73.47, 63.2) * mm, "end": v(73.36, 63.03) * mm});
            skLineSegment(sketch, "E819", {"start": v(73.36, 63.03) * mm, "end": v(73.24, 62.86) * mm});
            skLineSegment(sketch, "E820", {"start": v(73.24, 62.86) * mm, "end": v(73.1, 62.7) * mm});
            skLineSegment(sketch, "E821", {"start": v(73.1, 62.7) * mm, "end": v(72.93, 62.55) * mm});
            skLineSegment(sketch, "E822", {"start": v(72.93, 62.55) * mm, "end": v(72.74, 62.38) * mm});
            skLineSegment(sketch, "E823", {"start": v(72.74, 62.38) * mm, "end": v(72.24, 61.97) * mm});
            skLineSegment(sketch, "E824", {"start": v(72.24, 61.97) * mm, "end": v(71.87, 61.68) * mm});
            skLineSegment(sketch, "E825", {"start": v(71.87, 61.68) * mm, "end": v(71.56, 61.42) * mm});
            skLineSegment(sketch, "E826", {"start": v(71.56, 61.42) * mm, "end": v(71.3, 61.18) * mm});
            skLineSegment(sketch, "E827", {"start": v(71.3, 61.18) * mm, "end": v(71.1, 60.97) * mm});
            skLineSegment(sketch, "E828", {"start": v(41.45, 64.25) * mm, "end": v(41.29, 64.2) * mm});
            skLineSegment(sketch, "E829", {"start": v(41.29, 64.2) * mm, "end": v(41.14, 64.17) * mm});
            skLineSegment(sketch, "E830", {"start": v(41.14, 64.17) * mm, "end": v(41, 64.15) * mm});
            skLineSegment(sketch, "E831", {"start": v(41, 64.15) * mm, "end": v(40.88, 64.14) * mm});
            skLineSegment(sketch, "E832", {"start": v(40.88, 64.14) * mm, "end": v(40.83, 64.15) * mm});
            skLineSegment(sketch, "E833", {"start": v(40.83, 64.15) * mm, "end": v(40.8, 64.17) * mm});
            skLineSegment(sketch, "E834", {"start": v(40.8, 64.17) * mm, "end": v(40.77, 64.21) * mm});
            skLineSegment(sketch, "E835", {"start": v(40.77, 64.21) * mm, "end": v(40.76, 64.27) * mm});
            skLineSegment(sketch, "E836", {"start": v(40.76, 64.27) * mm, "end": v(40.76, 64.41) * mm});
            skLineSegment(sketch, "E837", {"start": v(40.76, 64.41) * mm, "end": v(40.77, 64.49) * mm});
            skLineSegment(sketch, "E838", {"start": v(40.77, 64.49) * mm, "end": v(40.8, 64.54) * mm});
            skLineSegment(sketch, "E839", {"start": v(40.8, 64.54) * mm, "end": v(40.86, 64.59) * mm});
            skLineSegment(sketch, "E840", {"start": v(40.86, 64.59) * mm, "end": v(40.96, 64.64) * mm});
            skLineSegment(sketch, "E841", {"start": v(40.96, 64.64) * mm, "end": v(41.06, 64.68) * mm});
            skLineSegment(sketch, "E842", {"start": v(41.06, 64.68) * mm, "end": v(41.18, 64.75) * mm});
            skLineSegment(sketch, "E843", {"start": v(41.18, 64.75) * mm, "end": v(41.45, 64.94) * mm});
            skLineSegment(sketch, "E844", {"start": v(41.45, 64.94) * mm, "end": v(41.6, 65.06) * mm});
            skLineSegment(sketch, "E845", {"start": v(41.6, 65.06) * mm, "end": v(41.76, 65.2) * mm});
            skLineSegment(sketch, "E846", {"start": v(41.76, 65.2) * mm, "end": v(41.9, 65.36) * mm});
            skLineSegment(sketch, "E847", {"start": v(41.9, 65.36) * mm, "end": v(42.05, 65.54) * mm});
            skLineSegment(sketch, "E848", {"start": v(42.05, 65.54) * mm, "end": v(42.23, 65.77) * mm});
            skLineSegment(sketch, "E849", {"start": v(42.23, 65.77) * mm, "end": v(42.32, 65.86) * mm});
            skLineSegment(sketch, "E850", {"start": v(42.32, 65.86) * mm, "end": v(42.38, 65.88) * mm});
            skLineSegment(sketch, "E851", {"start": v(42.38, 65.88) * mm, "end": v(42.46, 65.89) * mm});
            skLineSegment(sketch, "E852", {"start": v(42.46, 65.89) * mm, "end": v(42.77, 65.89) * mm});
            skLineSegment(sketch, "E853", {"start": v(42.77, 65.89) * mm, "end": v(42.77, 60.5) * mm});
            skLineSegment(sketch, "E854", {"start": v(42.77, 60.5) * mm, "end": v(42.78, 60.47) * mm});
            skLineSegment(sketch, "E855", {"start": v(42.78, 60.47) * mm, "end": v(42.8, 60.43) * mm});
            skLineSegment(sketch, "E856", {"start": v(42.8, 60.43) * mm, "end": v(42.84, 60.4) * mm});
            skLineSegment(sketch, "E857", {"start": v(42.84, 60.4) * mm, "end": v(42.9, 60.36) * mm});
            skLineSegment(sketch, "E858", {"start": v(42.9, 60.36) * mm, "end": v(42.98, 60.3) * mm});
            skLineSegment(sketch, "E859", {"start": v(42.98, 60.3) * mm, "end": v(43.03, 60.25) * mm});
            skLineSegment(sketch, "E860", {"start": v(43.03, 60.25) * mm, "end": v(43.05, 60.15) * mm});
            skLineSegment(sketch, "E861", {"start": v(43.05, 60.15) * mm, "end": v(43.05, 59.95) * mm});
            skLineSegment(sketch, "E862", {"start": v(43.05, 59.95) * mm, "end": v(43.05, 59.9) * mm});
            skLineSegment(sketch, "E863", {"start": v(43.05, 59.9) * mm, "end": v(43.02, 59.88) * mm});
            skLineSegment(sketch, "E864", {"start": v(43.02, 59.88) * mm, "end": v(42.98, 59.86) * mm});
            skLineSegment(sketch, "E865", {"start": v(42.98, 59.86) * mm, "end": v(42.92, 59.85) * mm});
            skLineSegment(sketch, "E866", {"start": v(42.92, 59.85) * mm, "end": v(41.22, 59.85) * mm});
            skLineSegment(sketch, "E867", {"start": v(41.22, 59.85) * mm, "end": v(41.13, 59.86) * mm});
            skLineSegment(sketch, "E868", {"start": v(41.13, 59.86) * mm, "end": v(41.09, 59.89) * mm});
            skLineSegment(sketch, "E869", {"start": v(41.09, 59.89) * mm, "end": v(41.07, 59.94) * mm});
            skLineSegment(sketch, "E870", {"start": v(41.07, 59.94) * mm, "end": v(41.06, 60.05) * mm});
            skLineSegment(sketch, "E871", {"start": v(41.06, 60.05) * mm, "end": v(41.07, 60.2) * mm});
            skLineSegment(sketch, "E872", {"start": v(41.07, 60.2) * mm, "end": v(41.09, 60.28) * mm});
            skLineSegment(sketch, "E873", {"start": v(41.09, 60.28) * mm, "end": v(41.1, 60.3) * mm});
            skLineSegment(sketch, "E874", {"start": v(41.1, 60.3) * mm, "end": v(41.13, 60.32) * mm});
            skLineSegment(sketch, "E875", {"start": v(41.13, 60.32) * mm, "end": v(41.24, 60.37) * mm});
            skLineSegment(sketch, "E876", {"start": v(41.24, 60.37) * mm, "end": v(41.33, 60.4) * mm});
            skLineSegment(sketch, "E877", {"start": v(41.33, 60.4) * mm, "end": v(41.4, 60.44) * mm});
            skLineSegment(sketch, "E878", {"start": v(41.4, 60.44) * mm, "end": v(41.43, 60.5) * mm});
            skLineSegment(sketch, "E879", {"start": v(41.43, 60.5) * mm, "end": v(41.45, 60.55) * mm});
            skLineSegment(sketch, "E880", {"start": v(41.45, 60.55) * mm, "end": v(41.45, 64.25) * mm});
            skLineSegment(sketch, "E881", {"start": v(46.61, 62) * mm, "end": v(46.93, 62) * mm});
            skLineSegment(sketch, "E882", {"start": v(46.93, 62) * mm, "end": v(47.03, 62) * mm});
            skLineSegment(sketch, "E883", {"start": v(47.03, 62) * mm, "end": v(47.06, 61.98) * mm});
            skLineSegment(sketch, "E884", {"start": v(47.06, 61.98) * mm, "end": v(47.09, 61.96) * mm});
            skLineSegment(sketch, "E885", {"start": v(47.09, 61.96) * mm, "end": v(47.11, 61.9) * mm});
            skLineSegment(sketch, "E886", {"start": v(47.11, 61.9) * mm, "end": v(47.12, 61.8) * mm});
            skLineSegment(sketch, "E887", {"start": v(47.12, 61.8) * mm, "end": v(47.12, 61.58) * mm});
            skLineSegment(sketch, "E888", {"start": v(47.12, 61.58) * mm, "end": v(47.12, 61.5) * mm});
            skLineSegment(sketch, "E889", {"start": v(47.12, 61.5) * mm, "end": v(47.1, 61.45) * mm});
            skLineSegment(sketch, "E890", {"start": v(47.1, 61.45) * mm, "end": v(47.04, 61.42) * mm});
            skLineSegment(sketch, "E891", {"start": v(47.04, 61.42) * mm, "end": v(46.95, 61.41) * mm});
            skLineSegment(sketch, "E892", {"start": v(46.95, 61.41) * mm, "end": v(46.61, 61.41) * mm});
            skLineSegment(sketch, "E893", {"start": v(46.61, 61.41) * mm, "end": v(46.61, 60.72) * mm});
            skLineSegment(sketch, "E894", {"start": v(46.61, 60.72) * mm, "end": v(46.63, 60.6) * mm});
            skLineSegment(sketch, "E895", {"start": v(46.63, 60.6) * mm, "end": v(46.67, 60.5) * mm});
            skLineSegment(sketch, "E896", {"start": v(46.67, 60.5) * mm, "end": v(46.73, 60.42) * mm});
            skLineSegment(sketch, "E897", {"start": v(46.73, 60.42) * mm, "end": v(46.83, 60.35) * mm});
            skLineSegment(sketch, "E898", {"start": v(46.83, 60.35) * mm, "end": v(46.88, 60.32) * mm});
            skLineSegment(sketch, "E899", {"start": v(46.88, 60.32) * mm, "end": v(46.91, 60.27) * mm});
            skLineSegment(sketch, "E900", {"start": v(46.91, 60.27) * mm, "end": v(46.93, 60.22) * mm});
            skLineSegment(sketch, "E901", {"start": v(46.93, 60.22) * mm, "end": v(46.94, 60.15) * mm});
            skLineSegment(sketch, "E902", {"start": v(46.94, 60.15) * mm, "end": v(46.94, 59.98) * mm});
            skLineSegment(sketch, "E903", {"start": v(46.94, 59.98) * mm, "end": v(46.93, 59.91) * mm});
            skLineSegment(sketch, "E904", {"start": v(46.93, 59.91) * mm, "end": v(46.91, 59.88) * mm});
            skLineSegment(sketch, "E905", {"start": v(46.91, 59.88) * mm, "end": v(46.86, 59.86) * mm});
            skLineSegment(sketch, "E906", {"start": v(46.86, 59.86) * mm, "end": v(46.77, 59.85) * mm});
            skLineSegment(sketch, "E907", {"start": v(46.77, 59.85) * mm, "end": v(45.2, 59.85) * mm});
            skLineSegment(sketch, "E908", {"start": v(45.2, 59.85) * mm, "end": v(45.12, 59.86) * mm});
            skLineSegment(sketch, "E909", {"start": v(45.12, 59.86) * mm, "end": v(45.1, 59.87) * mm});
            skLineSegment(sketch, "E910", {"start": v(45.1, 59.87) * mm, "end": v(45.07, 59.9) * mm});
            skLineSegment(sketch, "E911", {"start": v(45.07, 59.9) * mm, "end": v(45.05, 59.98) * mm});
            skLineSegment(sketch, "E912", {"start": v(45.05, 59.98) * mm, "end": v(45.05, 60.15) * mm});
            skLineSegment(sketch, "E913", {"start": v(45.05, 60.15) * mm, "end": v(45.05, 60.22) * mm});
            skLineSegment(sketch, "E914", {"start": v(45.05, 60.22) * mm, "end": v(45.07, 60.27) * mm});
            skLineSegment(sketch, "E915", {"start": v(45.07, 60.27) * mm, "end": v(45.1, 60.31) * mm});
            skLineSegment(sketch, "E916", {"start": v(45.1, 60.31) * mm, "end": v(45.16, 60.35) * mm});
            skLineSegment(sketch, "E917", {"start": v(45.16, 60.35) * mm, "end": v(45.22, 60.4) * mm});
            skLineSegment(sketch, "E918", {"start": v(45.22, 60.4) * mm, "end": v(45.26, 60.45) * mm});
            skLineSegment(sketch, "E919", {"start": v(45.26, 60.45) * mm, "end": v(45.3, 60.5) * mm});
            skLineSegment(sketch, "E920", {"start": v(45.3, 60.5) * mm, "end": v(45.3, 60.58) * mm});
            skLineSegment(sketch, "E921", {"start": v(45.3, 60.58) * mm, "end": v(45.3, 61.41) * mm});
            skLineSegment(sketch, "E922", {"start": v(45.3, 61.41) * mm, "end": v(43.83, 61.41) * mm});
            skLineSegment(sketch, "E923", {"start": v(43.83, 61.41) * mm, "end": v(43.73, 61.42) * mm});
            skLineSegment(sketch, "E924", {"start": v(43.73, 61.42) * mm, "end": v(43.69, 61.44) * mm});
            skLineSegment(sketch, "E925", {"start": v(43.69, 61.44) * mm, "end": v(43.67, 61.49) * mm});
            skLineSegment(sketch, "E926", {"start": v(43.67, 61.49) * mm, "end": v(43.66, 61.57) * mm});
            skLineSegment(sketch, "E927", {"start": v(43.66, 61.57) * mm, "end": v(43.66, 62) * mm});
            skLineSegment(sketch, "E928", {"start": v(43.66, 62) * mm, "end": v(43.67, 62.1) * mm});
            skLineSegment(sketch, "E929", {"start": v(43.67, 62.1) * mm, "end": v(43.72, 62.2) * mm});
            skLineSegment(sketch, "E930", {"start": v(43.72, 62.2) * mm, "end": v(43.83, 62.38) * mm});
            skLineSegment(sketch, "E931", {"start": v(43.83, 62.38) * mm, "end": v(45.92, 65.73) * mm});
            skLineSegment(sketch, "E932", {"start": v(45.92, 65.73) * mm, "end": v(45.98, 65.8) * mm});
            skLineSegment(sketch, "E933", {"start": v(45.98, 65.8) * mm, "end": v(46.06, 65.85) * mm});
            skLineSegment(sketch, "E934", {"start": v(46.06, 65.85) * mm, "end": v(46.17, 65.87) * mm});
            skLineSegment(sketch, "E935", {"start": v(46.17, 65.87) * mm, "end": v(46.35, 65.88) * mm});
            skLineSegment(sketch, "E936", {"start": v(46.35, 65.88) * mm, "end": v(46.51, 65.87) * mm});
            skLineSegment(sketch, "E937", {"start": v(46.51, 65.87) * mm, "end": v(46.59, 65.85) * mm});
            skLineSegment(sketch, "E938", {"start": v(46.59, 65.85) * mm, "end": v(46.6, 65.8) * mm});
            skLineSegment(sketch, "E939", {"start": v(46.6, 65.8) * mm, "end": v(46.61, 65.72) * mm});
            skLineSegment(sketch, "E940", {"start": v(46.61, 65.72) * mm, "end": v(46.61, 62) * mm});
            skLineSegment(sketch, "E941", {"start": v(14.63, 65.65) * mm, "end": v(21.12, 62.96) * mm});
            skLineSegment(sketch, "E942", {"start": v(21.12, 62.96) * mm, "end": v(14.63, 60.1) * mm});
            skLineSegment(sketch, "E943", {"start": v(14.63, 60.1) * mm, "end": v(15.81, 62.9) * mm});
            skLineSegment(sketch, "E944", {"start": v(15.81, 62.9) * mm, "end": v(14.63, 65.65) * mm});
            skLineSegment(sketch, "E945", {"start": v(246.6, 60.1) * mm, "end": v(240.1, 62.78) * mm});
            skLineSegment(sketch, "E946", {"start": v(240.1, 62.78) * mm, "end": v(246.6, 65.65) * mm});
            skLineSegment(sketch, "E947", {"start": v(246.6, 65.65) * mm, "end": v(245.41, 62.84) * mm});
            skLineSegment(sketch, "E948", {"start": v(245.41, 62.84) * mm, "end": v(246.6, 60.1) * mm});
            skLineSegment(sketch, "E949", {"start": v(2.88, 34.46) * mm, "end": v(2.88, 100.46) * mm});
            skLineSegment(sketch, "E950", {"start": v(2.88, 100.46) * mm, "end": v(258.34, 100.46) * mm});
            skLineSegment(sketch, "E951", {"start": v(258.34, 100.46) * mm, "end": v(258.34, 34.46) * mm});
            skLineSegment(sketch, "E952", {"start": v(258.34, 34.46) * mm, "end": v(2.88, 34.46) * mm});
            skLineSegment(sketch, "E953", {"start": v(82.53, 76.9) * mm, "end": v(81.7, 77.49) * mm});
            skLineSegment(sketch, "E954", {"start": v(81.7, 77.49) * mm, "end": v(80.59, 77.49) * mm});
            skLineSegment(sketch, "E955", {"start": v(80.59, 77.49) * mm, "end": v(79.63, 77) * mm});
            skLineSegment(sketch, "E956", {"start": v(79.63, 77) * mm, "end": v(79.16, 76.07) * mm});
            skLineSegment(sketch, "E957", {"start": v(79.16, 76.07) * mm, "end": v(79.03, 74.76) * mm});
            skLineSegment(sketch, "E958", {"start": v(79.03, 74.76) * mm, "end": v(79.18, 73.77) * mm});
            skLineSegment(sketch, "E959", {"start": v(79.18, 73.77) * mm, "end": v(79.89, 72.87) * mm});
            skLineSegment(sketch, "E960", {"start": v(79.89, 72.87) * mm, "end": v(80.9, 72.33) * mm});
            skLineSegment(sketch, "E961", {"start": v(80.9, 72.33) * mm, "end": v(81.93, 72.22) * mm});
            skLineSegment(sketch, "E962", {"start": v(81.93, 72.22) * mm, "end": v(82.23, 72.44) * mm});
            skLineSegment(sketch, "E963", {"start": v(82.23, 72.44) * mm, "end": v(82.23, 73.38) * mm});
            skLineSegment(sketch, "E964", {"start": v(82.23, 73.38) * mm, "end": v(82.03, 73.85) * mm});
            skLineSegment(sketch, "E965", {"start": v(82.03, 73.85) * mm, "end": v(81.44, 74) * mm});
            skLineSegment(sketch, "E966", {"start": v(81.44, 74) * mm, "end": v(81.56, 74.43) * mm});
            skLineSegment(sketch, "E967", {"start": v(81.56, 74.43) * mm, "end": v(82.53, 74.29) * mm});
            skLineSegment(sketch, "E968", {"start": v(82.53, 74.29) * mm, "end": v(83.57, 74.43) * mm});
            skLineSegment(sketch, "E969", {"start": v(83.57, 74.43) * mm, "end": v(83.59, 74.1) * mm});
            skLineSegment(sketch, "E970", {"start": v(83.59, 74.1) * mm, "end": v(83.07, 73.79) * mm});
            skLineSegment(sketch, "E971", {"start": v(83.07, 73.79) * mm, "end": v(83.12, 72.85) * mm});
            skLineSegment(sketch, "E972", {"start": v(83.12, 72.85) * mm, "end": v(83.46, 72.39) * mm});
            skLineSegment(sketch, "E973", {"start": v(83.46, 72.39) * mm, "end": v(82.6, 71.97) * mm});
            skLineSegment(sketch, "E974", {"start": v(82.6, 71.97) * mm, "end": v(81.77, 71.85) * mm});
            skLineSegment(sketch, "E975", {"start": v(81.77, 71.85) * mm, "end": v(80.32, 71.85) * mm});
            skLineSegment(sketch, "E976", {"start": v(80.32, 71.85) * mm, "end": v(79.03, 72.4) * mm});
            skLineSegment(sketch, "E977", {"start": v(79.03, 72.4) * mm, "end": v(78.1, 73.53) * mm});
            skLineSegment(sketch, "E978", {"start": v(78.1, 73.53) * mm, "end": v(77.94, 75.4) * mm});
            skLineSegment(sketch, "E979", {"start": v(77.94, 75.4) * mm, "end": v(78.63, 76.78) * mm});
            skLineSegment(sketch, "E980", {"start": v(78.63, 76.78) * mm, "end": v(79.94, 77.74) * mm});
            skLineSegment(sketch, "E981", {"start": v(79.94, 77.74) * mm, "end": v(81.64, 77.9) * mm});
            skLineSegment(sketch, "E982", {"start": v(81.64, 77.9) * mm, "end": v(83.27, 77.56) * mm});
            skLineSegment(sketch, "E983", {"start": v(83.27, 77.56) * mm, "end": v(83.1, 76.8) * mm});
            skLineSegment(sketch, "E984", {"start": v(83.1, 76.8) * mm, "end": v(83.16, 75.9) * mm});
            skLineSegment(sketch, "E985", {"start": v(83.16, 75.9) * mm, "end": v(82.84, 75.94) * mm});
            skLineSegment(sketch, "E986", {"start": v(82.84, 75.94) * mm, "end": v(82.53, 76.9) * mm});
            skLineSegment(sketch, "E987", {"start": v(86.23, 77.45) * mm, "end": v(85.74, 77.43) * mm});
            skLineSegment(sketch, "E988", {"start": v(85.74, 77.43) * mm, "end": v(85.74, 73.3) * mm});
            skLineSegment(sketch, "E989", {"start": v(85.74, 73.3) * mm, "end": v(85.89, 72.72) * mm});
            skLineSegment(sketch, "E990", {"start": v(85.89, 72.72) * mm, "end": v(86.53, 72.23) * mm});
            skLineSegment(sketch, "E991", {"start": v(86.53, 72.23) * mm, "end": v(87.6, 72.38) * mm});
            skLineSegment(sketch, "E992", {"start": v(87.6, 72.38) * mm, "end": v(88.36, 72.99) * mm});
            skLineSegment(sketch, "E993", {"start": v(88.36, 72.99) * mm, "end": v(88.78, 73.92) * mm});
            skLineSegment(sketch, "E994", {"start": v(88.78, 73.92) * mm, "end": v(88.78, 75.28) * mm});
            skLineSegment(sketch, "E995", {"start": v(88.78, 75.28) * mm, "end": v(88.34, 76.43) * mm});
            skLineSegment(sketch, "E996", {"start": v(88.34, 76.43) * mm, "end": v(87.36, 77.13) * mm});
            skLineSegment(sketch, "E997", {"start": v(87.36, 77.13) * mm, "end": v(86.23, 77.45) * mm});
            skLineSegment(sketch, "E998", {"start": v(85.16, 77.74) * mm, "end": v(85.98, 77.87) * mm});
            skLineSegment(sketch, "E999", {"start": v(85.98, 77.87) * mm, "end": v(86.9, 77.87) * mm});
            skLineSegment(sketch, "E1000", {"start": v(86.9, 77.87) * mm, "end": v(88.24, 77.47) * mm});
            skLineSegment(sketch, "E1001", {"start": v(88.24, 77.47) * mm, "end": v(89.49, 76.48) * mm});
            skLineSegment(sketch, "E1002", {"start": v(89.49, 76.48) * mm, "end": v(89.94, 75.1) * mm});
            skLineSegment(sketch, "E1003", {"start": v(89.94, 75.1) * mm, "end": v(89.74, 73.59) * mm});
            skLineSegment(sketch, "E1004", {"start": v(89.74, 73.59) * mm, "end": v(88.7, 72.5) * mm});
            skLineSegment(sketch, "E1005", {"start": v(88.7, 72.5) * mm, "end": v(87.52, 71.96) * mm});
            skLineSegment(sketch, "E1006", {"start": v(87.52, 71.96) * mm, "end": v(86.32, 71.87) * mm});
            skLineSegment(sketch, "E1007", {"start": v(86.32, 71.87) * mm, "end": v(85.34, 71.93) * mm});
            skLineSegment(sketch, "E1008", {"start": v(85.34, 71.93) * mm, "end": v(84.14, 71.83) * mm});
            skLineSegment(sketch, "E1009", {"start": v(84.14, 71.83) * mm, "end": v(84.09, 72.18) * mm});
            skLineSegment(sketch, "E1010", {"start": v(84.09, 72.18) * mm, "end": v(84.62, 72.36) * mm});
            skLineSegment(sketch, "E1011", {"start": v(84.62, 72.36) * mm, "end": v(84.93, 72.9) * mm});
            skLineSegment(sketch, "E1012", {"start": v(84.93, 72.9) * mm, "end": v(84.93, 76.83) * mm});
            skLineSegment(sketch, "E1013", {"start": v(84.93, 76.83) * mm, "end": v(84.63, 77.39) * mm});
            skLineSegment(sketch, "E1014", {"start": v(84.63, 77.39) * mm, "end": v(84.18, 77.39) * mm});
            skLineSegment(sketch, "E1015", {"start": v(84.18, 77.39) * mm, "end": v(84.17, 77.77) * mm});
            skLineSegment(sketch, "E1016", {"start": v(84.17, 77.77) * mm, "end": v(85.16, 77.74) * mm});
            skLineSegment(sketch, "E1017", {"start": v(155.86, 53.08) * mm, "end": v(155.03, 53.67) * mm});
            skLineSegment(sketch, "E1018", {"start": v(155.03, 53.67) * mm, "end": v(153.92, 53.67) * mm});
            skLineSegment(sketch, "E1019", {"start": v(153.92, 53.67) * mm, "end": v(152.97, 53.18) * mm});
            skLineSegment(sketch, "E1020", {"start": v(152.97, 53.18) * mm, "end": v(152.5, 52.25) * mm});
            skLineSegment(sketch, "E1021", {"start": v(152.5, 52.25) * mm, "end": v(152.36, 50.94) * mm});
            skLineSegment(sketch, "E1022", {"start": v(152.36, 50.94) * mm, "end": v(152.51, 49.95) * mm});
            skLineSegment(sketch, "E1023", {"start": v(152.51, 49.95) * mm, "end": v(153.22, 49.05) * mm});
            skLineSegment(sketch, "E1024", {"start": v(153.22, 49.05) * mm, "end": v(154.24, 48.5) * mm});
            skLineSegment(sketch, "E1025", {"start": v(154.24, 48.5) * mm, "end": v(155.26, 48.4) * mm});
            skLineSegment(sketch, "E1026", {"start": v(155.26, 48.4) * mm, "end": v(155.57, 48.62) * mm});
            skLineSegment(sketch, "E1027", {"start": v(155.57, 48.62) * mm, "end": v(155.57, 49.56) * mm});
            skLineSegment(sketch, "E1028", {"start": v(155.57, 49.56) * mm, "end": v(155.36, 50.03) * mm});
            skLineSegment(sketch, "E1029", {"start": v(155.36, 50.03) * mm, "end": v(154.78, 50.18) * mm});
            skLineSegment(sketch, "E1030", {"start": v(154.78, 50.18) * mm, "end": v(154.9, 50.6) * mm});
            skLineSegment(sketch, "E1031", {"start": v(154.9, 50.6) * mm, "end": v(155.87, 50.47) * mm});
            skLineSegment(sketch, "E1032", {"start": v(155.87, 50.47) * mm, "end": v(156.9, 50.6) * mm});
            skLineSegment(sketch, "E1033", {"start": v(156.9, 50.6) * mm, "end": v(156.92, 50.28) * mm});
            skLineSegment(sketch, "E1034", {"start": v(156.92, 50.28) * mm, "end": v(156.4, 49.97) * mm});
            skLineSegment(sketch, "E1035", {"start": v(156.4, 49.97) * mm, "end": v(156.45, 49.03) * mm});
            skLineSegment(sketch, "E1036", {"start": v(156.45, 49.03) * mm, "end": v(156.8, 48.57) * mm});
            skLineSegment(sketch, "E1037", {"start": v(156.8, 48.57) * mm, "end": v(155.94, 48.15) * mm});
            skLineSegment(sketch, "E1038", {"start": v(155.94, 48.15) * mm, "end": v(155.1, 48.03) * mm});
            skLineSegment(sketch, "E1039", {"start": v(155.1, 48.03) * mm, "end": v(153.65, 48.03) * mm});
            skLineSegment(sketch, "E1040", {"start": v(153.65, 48.03) * mm, "end": v(152.36, 48.58) * mm});
            skLineSegment(sketch, "E1041", {"start": v(152.36, 48.58) * mm, "end": v(151.44, 49.71) * mm});
            skLineSegment(sketch, "E1042", {"start": v(151.44, 49.71) * mm, "end": v(151.28, 51.58) * mm});
            skLineSegment(sketch, "E1043", {"start": v(151.28, 51.58) * mm, "end": v(151.96, 52.96) * mm});
            skLineSegment(sketch, "E1044", {"start": v(151.96, 52.96) * mm, "end": v(153.28, 53.92) * mm});
            skLineSegment(sketch, "E1045", {"start": v(153.28, 53.92) * mm, "end": v(154.98, 54.08) * mm});
            skLineSegment(sketch, "E1046", {"start": v(154.98, 54.08) * mm, "end": v(156.6, 53.74) * mm});
            skLineSegment(sketch, "E1047", {"start": v(156.6, 53.74) * mm, "end": v(156.44, 52.98) * mm});
            skLineSegment(sketch, "E1048", {"start": v(156.44, 52.98) * mm, "end": v(156.5, 52.08) * mm});
            skLineSegment(sketch, "E1049", {"start": v(156.5, 52.08) * mm, "end": v(156.18, 52.12) * mm});
            skLineSegment(sketch, "E1050", {"start": v(156.18, 52.12) * mm, "end": v(155.86, 53.08) * mm});
            skLineSegment(sketch, "E1051", {"start": v(159.57, 53.63) * mm, "end": v(159.08, 53.61) * mm});
            skLineSegment(sketch, "E1052", {"start": v(159.08, 53.61) * mm, "end": v(159.08, 49.48) * mm});
            skLineSegment(sketch, "E1053", {"start": v(159.08, 49.48) * mm, "end": v(159.22, 48.9) * mm});
            skLineSegment(sketch, "E1054", {"start": v(159.22, 48.9) * mm, "end": v(159.87, 48.41) * mm});
            skLineSegment(sketch, "E1055", {"start": v(159.87, 48.41) * mm, "end": v(160.93, 48.56) * mm});
            skLineSegment(sketch, "E1056", {"start": v(160.93, 48.56) * mm, "end": v(161.7, 49.17) * mm});
            skLineSegment(sketch, "E1057", {"start": v(161.7, 49.17) * mm, "end": v(162.11, 50.1) * mm});
            skLineSegment(sketch, "E1058", {"start": v(162.11, 50.1) * mm, "end": v(162.11, 51.46) * mm});
            skLineSegment(sketch, "E1059", {"start": v(162.11, 51.46) * mm, "end": v(161.68, 52.61) * mm});
            skLineSegment(sketch, "E1060", {"start": v(161.68, 52.61) * mm, "end": v(160.7, 53.3) * mm});
            skLineSegment(sketch, "E1061", {"start": v(160.7, 53.3) * mm, "end": v(159.57, 53.63) * mm});
            skLineSegment(sketch, "E1062", {"start": v(158.5, 53.92) * mm, "end": v(159.31, 54.05) * mm});
            skLineSegment(sketch, "E1063", {"start": v(159.31, 54.05) * mm, "end": v(160.24, 54.05) * mm});
            skLineSegment(sketch, "E1064", {"start": v(160.24, 54.05) * mm, "end": v(161.58, 53.65) * mm});
            skLineSegment(sketch, "E1065", {"start": v(161.58, 53.65) * mm, "end": v(162.82, 52.66) * mm});
            skLineSegment(sketch, "E1066", {"start": v(162.82, 52.66) * mm, "end": v(163.28, 51.28) * mm});
            skLineSegment(sketch, "E1067", {"start": v(163.28, 51.28) * mm, "end": v(163.08, 49.77) * mm});
            skLineSegment(sketch, "E1068", {"start": v(163.08, 49.77) * mm, "end": v(162.04, 48.68) * mm});
            skLineSegment(sketch, "E1069", {"start": v(162.04, 48.68) * mm, "end": v(160.85, 48.14) * mm});
            skLineSegment(sketch, "E1070", {"start": v(160.85, 48.14) * mm, "end": v(159.65, 48.05) * mm});
            skLineSegment(sketch, "E1071", {"start": v(159.65, 48.05) * mm, "end": v(158.68, 48.11) * mm});
            skLineSegment(sketch, "E1072", {"start": v(158.68, 48.11) * mm, "end": v(157.48, 48.01) * mm});
            skLineSegment(sketch, "E1073", {"start": v(157.48, 48.01) * mm, "end": v(157.42, 48.36) * mm});
            skLineSegment(sketch, "E1074", {"start": v(157.42, 48.36) * mm, "end": v(157.95, 48.54) * mm});
            skLineSegment(sketch, "E1075", {"start": v(157.95, 48.54) * mm, "end": v(158.26, 49.08) * mm});
            skLineSegment(sketch, "E1076", {"start": v(158.26, 49.08) * mm, "end": v(158.26, 53) * mm});
            skLineSegment(sketch, "E1077", {"start": v(158.26, 53) * mm, "end": v(157.96, 53.57) * mm});
            skLineSegment(sketch, "E1078", {"start": v(157.96, 53.57) * mm, "end": v(157.51, 53.57) * mm});
            skLineSegment(sketch, "E1079", {"start": v(157.51, 53.57) * mm, "end": v(157.5, 53.95) * mm});
            skLineSegment(sketch, "E1080", {"start": v(157.5, 53.95) * mm, "end": v(158.5, 53.92) * mm});
            skLineSegment(sketch, "E1081", {"start": v(230.15, 88.25) * mm, "end": v(229.99, 88.2) * mm});
            skLineSegment(sketch, "E1082", {"start": v(229.99, 88.2) * mm, "end": v(229.84, 88.17) * mm});
            skLineSegment(sketch, "E1083", {"start": v(229.84, 88.17) * mm, "end": v(229.7, 88.15) * mm});
            skLineSegment(sketch, "E1084", {"start": v(229.7, 88.15) * mm, "end": v(229.58, 88.14) * mm});
            skLineSegment(sketch, "E1085", {"start": v(229.58, 88.14) * mm, "end": v(229.53, 88.15) * mm});
            skLineSegment(sketch, "E1086", {"start": v(229.53, 88.15) * mm, "end": v(229.5, 88.17) * mm});
            skLineSegment(sketch, "E1087", {"start": v(229.5, 88.17) * mm, "end": v(229.47, 88.21) * mm});
            skLineSegment(sketch, "E1088", {"start": v(229.47, 88.21) * mm, "end": v(229.47, 88.27) * mm});
            skLineSegment(sketch, "E1089", {"start": v(229.47, 88.27) * mm, "end": v(229.47, 88.41) * mm});
            skLineSegment(sketch, "E1090", {"start": v(229.47, 88.41) * mm, "end": v(229.47, 88.49) * mm});
            skLineSegment(sketch, "E1091", {"start": v(229.47, 88.49) * mm, "end": v(229.5, 88.54) * mm});
            skLineSegment(sketch, "E1092", {"start": v(229.5, 88.54) * mm, "end": v(229.56, 88.59) * mm});
            skLineSegment(sketch, "E1093", {"start": v(229.56, 88.59) * mm, "end": v(229.67, 88.64) * mm});
            skLineSegment(sketch, "E1094", {"start": v(229.67, 88.64) * mm, "end": v(229.76, 88.68) * mm});
            skLineSegment(sketch, "E1095", {"start": v(229.76, 88.68) * mm, "end": v(229.88, 88.75) * mm});
            skLineSegment(sketch, "E1096", {"start": v(229.88, 88.75) * mm, "end": v(230.15, 88.94) * mm});
            skLineSegment(sketch, "E1097", {"start": v(230.15, 88.94) * mm, "end": v(230.3, 89.06) * mm});
            skLineSegment(sketch, "E1098", {"start": v(230.3, 89.06) * mm, "end": v(230.46, 89.2) * mm});
            skLineSegment(sketch, "E1099", {"start": v(230.46, 89.2) * mm, "end": v(230.6, 89.36) * mm});
            skLineSegment(sketch, "E1100", {"start": v(230.6, 89.36) * mm, "end": v(230.76, 89.54) * mm});
            skLineSegment(sketch, "E1101", {"start": v(230.76, 89.54) * mm, "end": v(230.94, 89.77) * mm});
            skLineSegment(sketch, "E1102", {"start": v(230.94, 89.77) * mm, "end": v(231.02, 89.86) * mm});
            skLineSegment(sketch, "E1103", {"start": v(231.02, 89.86) * mm, "end": v(231.08, 89.88) * mm});
            skLineSegment(sketch, "E1104", {"start": v(231.08, 89.88) * mm, "end": v(231.16, 89.89) * mm});
            skLineSegment(sketch, "E1105", {"start": v(231.16, 89.89) * mm, "end": v(231.47, 89.89) * mm});
            skLineSegment(sketch, "E1106", {"start": v(231.47, 89.89) * mm, "end": v(231.47, 84.5) * mm});
            skLineSegment(sketch, "E1107", {"start": v(231.47, 84.5) * mm, "end": v(231.48, 84.47) * mm});
            skLineSegment(sketch, "E1108", {"start": v(231.48, 84.47) * mm, "end": v(231.5, 84.43) * mm});
            skLineSegment(sketch, "E1109", {"start": v(231.5, 84.43) * mm, "end": v(231.54, 84.4) * mm});
            skLineSegment(sketch, "E1110", {"start": v(231.54, 84.4) * mm, "end": v(231.6, 84.36) * mm});
            skLineSegment(sketch, "E1111", {"start": v(231.6, 84.36) * mm, "end": v(231.69, 84.3) * mm});
            skLineSegment(sketch, "E1112", {"start": v(231.69, 84.3) * mm, "end": v(231.73, 84.25) * mm});
            skLineSegment(sketch, "E1113", {"start": v(231.73, 84.25) * mm, "end": v(231.75, 84.15) * mm});
            skLineSegment(sketch, "E1114", {"start": v(231.75, 84.15) * mm, "end": v(231.76, 83.95) * mm});
            skLineSegment(sketch, "E1115", {"start": v(231.76, 83.95) * mm, "end": v(231.75, 83.9) * mm});
            skLineSegment(sketch, "E1116", {"start": v(231.75, 83.9) * mm, "end": v(231.72, 83.88) * mm});
            skLineSegment(sketch, "E1117", {"start": v(231.72, 83.88) * mm, "end": v(231.68, 83.86) * mm});
            skLineSegment(sketch, "E1118", {"start": v(231.68, 83.86) * mm, "end": v(231.63, 83.85) * mm});
            skLineSegment(sketch, "E1119", {"start": v(231.63, 83.85) * mm, "end": v(229.92, 83.85) * mm});
            skLineSegment(sketch, "E1120", {"start": v(229.92, 83.85) * mm, "end": v(229.84, 83.86) * mm});
            skLineSegment(sketch, "E1121", {"start": v(229.84, 83.86) * mm, "end": v(229.8, 83.89) * mm});
            skLineSegment(sketch, "E1122", {"start": v(229.8, 83.89) * mm, "end": v(229.77, 83.94) * mm});
            skLineSegment(sketch, "E1123", {"start": v(229.77, 83.94) * mm, "end": v(229.77, 84.05) * mm});
            skLineSegment(sketch, "E1124", {"start": v(229.77, 84.05) * mm, "end": v(229.77, 84.2) * mm});
            skLineSegment(sketch, "E1125", {"start": v(229.77, 84.2) * mm, "end": v(229.79, 84.28) * mm});
            skLineSegment(sketch, "E1126", {"start": v(229.79, 84.28) * mm, "end": v(229.8, 84.3) * mm});
            skLineSegment(sketch, "E1127", {"start": v(229.8, 84.3) * mm, "end": v(229.84, 84.32) * mm});
            skLineSegment(sketch, "E1128", {"start": v(229.84, 84.32) * mm, "end": v(229.94, 84.37) * mm});
            skLineSegment(sketch, "E1129", {"start": v(229.94, 84.37) * mm, "end": v(230.03, 84.4) * mm});
            skLineSegment(sketch, "E1130", {"start": v(230.03, 84.4) * mm, "end": v(230.1, 84.44) * mm});
            skLineSegment(sketch, "E1131", {"start": v(230.1, 84.44) * mm, "end": v(230.14, 84.5) * mm});
            skLineSegment(sketch, "E1132", {"start": v(230.14, 84.5) * mm, "end": v(230.15, 84.55) * mm});
            skLineSegment(sketch, "E1133", {"start": v(230.15, 84.55) * mm, "end": v(230.15, 88.25) * mm});
            skLineSegment(sketch, "E1134", {"start": v(204.25, 87.08) * mm, "end": v(204.4, 87.04) * mm});
            skLineSegment(sketch, "E1135", {"start": v(204.4, 87.04) * mm, "end": v(204.56, 86.98) * mm});
            skLineSegment(sketch, "E1136", {"start": v(204.56, 86.98) * mm, "end": v(204.7, 86.92) * mm});
            skLineSegment(sketch, "E1137", {"start": v(204.7, 86.92) * mm, "end": v(204.83, 86.86) * mm});
            skLineSegment(sketch, "E1138", {"start": v(204.83, 86.86) * mm, "end": v(204.95, 86.78) * mm});
            skLineSegment(sketch, "E1139", {"start": v(204.95, 86.78) * mm, "end": v(205.06, 86.7) * mm});
            skLineSegment(sketch, "E1140", {"start": v(205.06, 86.7) * mm, "end": v(205.16, 86.61) * mm});
            skLineSegment(sketch, "E1141", {"start": v(205.16, 86.61) * mm, "end": v(205.25, 86.52) * mm});
            skLineSegment(sketch, "E1142", {"start": v(205.25, 86.52) * mm, "end": v(205.32, 86.42) * mm});
            skLineSegment(sketch, "E1143", {"start": v(205.32, 86.42) * mm, "end": v(205.4, 86.31) * mm});
            skLineSegment(sketch, "E1144", {"start": v(205.4, 86.31) * mm, "end": v(205.45, 86.2) * mm});
            skLineSegment(sketch, "E1145", {"start": v(205.45, 86.2) * mm, "end": v(205.5, 86.08) * mm});
            skLineSegment(sketch, "E1146", {"start": v(205.5, 86.08) * mm, "end": v(205.53, 85.95) * mm});
            skLineSegment(sketch, "E1147", {"start": v(205.53, 85.95) * mm, "end": v(205.56, 85.81) * mm});
            skLineSegment(sketch, "E1148", {"start": v(205.56, 85.81) * mm, "end": v(205.57, 85.67) * mm});
            skLineSegment(sketch, "E1149", {"start": v(205.57, 85.67) * mm, "end": v(205.58, 85.52) * mm});
            skLineSegment(sketch, "E1150", {"start": v(205.58, 85.52) * mm, "end": v(205.56, 85.27) * mm});
            skLineSegment(sketch, "E1151", {"start": v(205.56, 85.27) * mm, "end": v(205.52, 85.04) * mm});
            skLineSegment(sketch, "E1152", {"start": v(205.52, 85.04) * mm, "end": v(205.44, 84.82) * mm});
            skLineSegment(sketch, "E1153", {"start": v(205.44, 84.82) * mm, "end": v(205.33, 84.61) * mm});
            skLineSegment(sketch, "E1154", {"start": v(205.33, 84.61) * mm, "end": v(205.2, 84.43) * mm});
            skLineSegment(sketch, "E1155", {"start": v(205.2, 84.43) * mm, "end": v(205.04, 84.27) * mm});
            skLineSegment(sketch, "E1156", {"start": v(205.04, 84.27) * mm, "end": v(204.86, 84.13) * mm});
            skLineSegment(sketch, "E1157", {"start": v(204.86, 84.13) * mm, "end": v(204.66, 84.01) * mm});
            skLineSegment(sketch, "E1158", {"start": v(204.66, 84.01) * mm, "end": v(204.44, 83.92) * mm});
            skLineSegment(sketch, "E1159", {"start": v(204.44, 83.92) * mm, "end": v(204.21, 83.85) * mm});
            skLineSegment(sketch, "E1160", {"start": v(204.21, 83.85) * mm, "end": v(203.98, 83.81) * mm});
            skLineSegment(sketch, "E1161", {"start": v(203.98, 83.81) * mm, "end": v(203.75, 83.8) * mm});
            skLineSegment(sketch, "E1162", {"start": v(203.75, 83.8) * mm, "end": v(203.59, 83.8) * mm});
            skLineSegment(sketch, "E1163", {"start": v(203.59, 83.8) * mm, "end": v(203.44, 83.82) * mm});
            skLineSegment(sketch, "E1164", {"start": v(203.44, 83.82) * mm, "end": v(203.3, 83.85) * mm});
            skLineSegment(sketch, "E1165", {"start": v(203.3, 83.85) * mm, "end": v(203.16, 83.9) * mm});
            skLineSegment(sketch, "E1166", {"start": v(203.16, 83.9) * mm, "end": v(203.03, 83.95) * mm});
            skLineSegment(sketch, "E1167", {"start": v(203.03, 83.95) * mm, "end": v(202.91, 84.02) * mm});
            skLineSegment(sketch, "E1168", {"start": v(202.91, 84.02) * mm, "end": v(202.8, 84.1) * mm});
            skLineSegment(sketch, "E1169", {"start": v(202.8, 84.1) * mm, "end": v(202.7, 84.2) * mm});
            skLineSegment(sketch, "E1170", {"start": v(202.7, 84.2) * mm, "end": v(202.61, 84.3) * mm});
            skLineSegment(sketch, "E1171", {"start": v(202.61, 84.3) * mm, "end": v(202.53, 84.4) * mm});
            skLineSegment(sketch, "E1172", {"start": v(202.53, 84.4) * mm, "end": v(202.46, 84.51) * mm});
            skLineSegment(sketch, "E1173", {"start": v(202.46, 84.51) * mm, "end": v(202.4, 84.63) * mm});
            skLineSegment(sketch, "E1174", {"start": v(202.4, 84.63) * mm, "end": v(202.37, 84.75) * mm});
            skLineSegment(sketch, "E1175", {"start": v(202.37, 84.75) * mm, "end": v(202.33, 84.87) * mm});
            skLineSegment(sketch, "E1176", {"start": v(202.33, 84.87) * mm, "end": v(202.32, 85) * mm});
            skLineSegment(sketch, "E1177", {"start": v(202.32, 85) * mm, "end": v(202.31, 85.13) * mm});
            skLineSegment(sketch, "E1178", {"start": v(202.31, 85.13) * mm, "end": v(202.32, 85.26) * mm});
            skLineSegment(sketch, "E1179", {"start": v(202.32, 85.26) * mm, "end": v(202.34, 85.38) * mm});
            skLineSegment(sketch, "E1180", {"start": v(202.34, 85.38) * mm, "end": v(202.39, 85.49) * mm});
            skLineSegment(sketch, "E1181", {"start": v(202.39, 85.49) * mm, "end": v(202.45, 85.59) * mm});
            skLineSegment(sketch, "E1182", {"start": v(202.45, 85.59) * mm, "end": v(202.52, 85.67) * mm});
            skLineSegment(sketch, "E1183", {"start": v(202.52, 85.67) * mm, "end": v(202.61, 85.73) * mm});
            skLineSegment(sketch, "E1184", {"start": v(202.61, 85.73) * mm, "end": v(202.72, 85.76) * mm});
            skLineSegment(sketch, "E1185", {"start": v(202.72, 85.76) * mm, "end": v(202.84, 85.77) * mm});
            skLineSegment(sketch, "E1186", {"start": v(202.84, 85.77) * mm, "end": v(202.95, 85.76) * mm});
            skLineSegment(sketch, "E1187", {"start": v(202.95, 85.76) * mm, "end": v(203.06, 85.73) * mm});
            skLineSegment(sketch, "E1188", {"start": v(203.06, 85.73) * mm, "end": v(203.14, 85.68) * mm});
            skLineSegment(sketch, "E1189", {"start": v(203.14, 85.68) * mm, "end": v(203.22, 85.6) * mm});
            skLineSegment(sketch, "E1190", {"start": v(203.22, 85.6) * mm, "end": v(203.28, 85.52) * mm});
            skLineSegment(sketch, "E1191", {"start": v(203.28, 85.52) * mm, "end": v(203.32, 85.42) * mm});
            skLineSegment(sketch, "E1192", {"start": v(203.32, 85.42) * mm, "end": v(203.34, 85.31) * mm});
            skLineSegment(sketch, "E1193", {"start": v(203.34, 85.31) * mm, "end": v(203.35, 85.2) * mm});
            skLineSegment(sketch, "E1194", {"start": v(203.35, 85.2) * mm, "end": v(203.34, 85.06) * mm});
            skLineSegment(sketch, "E1195", {"start": v(203.34, 85.06) * mm, "end": v(203.31, 84.86) * mm});
            skLineSegment(sketch, "E1196", {"start": v(203.31, 84.86) * mm, "end": v(203.3, 84.76) * mm});
            skLineSegment(sketch, "E1197", {"start": v(203.3, 84.76) * mm, "end": v(203.29, 84.67) * mm});
            skLineSegment(sketch, "E1198", {"start": v(203.29, 84.67) * mm, "end": v(203.3, 84.59) * mm});
            skLineSegment(sketch, "E1199", {"start": v(203.3, 84.59) * mm, "end": v(203.31, 84.52) * mm});
            skLineSegment(sketch, "E1200", {"start": v(203.31, 84.52) * mm, "end": v(203.34, 84.45) * mm});
            skLineSegment(sketch, "E1201", {"start": v(203.34, 84.45) * mm, "end": v(203.39, 84.4) * mm});
            skLineSegment(sketch, "E1202", {"start": v(203.39, 84.4) * mm, "end": v(203.44, 84.34) * mm});
            skLineSegment(sketch, "E1203", {"start": v(203.44, 84.34) * mm, "end": v(203.5, 84.3) * mm});
            skLineSegment(sketch, "E1204", {"start": v(203.5, 84.3) * mm, "end": v(203.58, 84.29) * mm});
            skLineSegment(sketch, "E1205", {"start": v(203.58, 84.29) * mm, "end": v(203.67, 84.28) * mm});
            skLineSegment(sketch, "E1206", {"start": v(203.67, 84.28) * mm, "end": v(203.78, 84.3) * mm});
            skLineSegment(sketch, "E1207", {"start": v(203.78, 84.3) * mm, "end": v(203.87, 84.33) * mm});
            skLineSegment(sketch, "E1208", {"start": v(203.87, 84.33) * mm, "end": v(203.95, 84.4) * mm});
            skLineSegment(sketch, "E1209", {"start": v(203.95, 84.4) * mm, "end": v(204.01, 84.48) * mm});
            skLineSegment(sketch, "E1210", {"start": v(204.01, 84.48) * mm, "end": v(204.06, 84.59) * mm});
            skLineSegment(sketch, "E1211", {"start": v(204.06, 84.59) * mm, "end": v(204.1, 84.73) * mm});
            skLineSegment(sketch, "E1212", {"start": v(204.1, 84.73) * mm, "end": v(204.12, 84.9) * mm});
            skLineSegment(sketch, "E1213", {"start": v(204.12, 84.9) * mm, "end": v(204.13, 85.1) * mm});
            skLineSegment(sketch, "E1214", {"start": v(204.13, 85.1) * mm, "end": v(204.12, 85.32) * mm});
            skLineSegment(sketch, "E1215", {"start": v(204.12, 85.32) * mm, "end": v(204.08, 86.24) * mm});
            skLineSegment(sketch, "E1216", {"start": v(204.08, 86.24) * mm, "end": v(204.04, 86.37) * mm});
            skLineSegment(sketch, "E1217", {"start": v(204.04, 86.37) * mm, "end": v(204, 86.48) * mm});
            skLineSegment(sketch, "E1218", {"start": v(204, 86.48) * mm, "end": v(203.95, 86.57) * mm});
            skLineSegment(sketch, "E1219", {"start": v(203.95, 86.57) * mm, "end": v(203.9, 86.64) * mm});
            skLineSegment(sketch, "E1220", {"start": v(203.9, 86.64) * mm, "end": v(203.83, 86.7) * mm});
            skLineSegment(sketch, "E1221", {"start": v(203.83, 86.7) * mm, "end": v(203.76, 86.74) * mm});
            skLineSegment(sketch, "E1222", {"start": v(203.76, 86.74) * mm, "end": v(203.7, 86.78) * mm});
            skLineSegment(sketch, "E1223", {"start": v(203.7, 86.78) * mm, "end": v(203.63, 86.8) * mm});
            skLineSegment(sketch, "E1224", {"start": v(203.63, 86.8) * mm, "end": v(203.45, 86.82) * mm});
            skLineSegment(sketch, "E1225", {"start": v(203.45, 86.82) * mm, "end": v(203.18, 86.82) * mm});
            skLineSegment(sketch, "E1226", {"start": v(203.18, 86.82) * mm, "end": v(203.08, 86.82) * mm});
            skLineSegment(sketch, "E1227", {"start": v(203.08, 86.82) * mm, "end": v(203.03, 86.83) * mm});
            skLineSegment(sketch, "E1228", {"start": v(203.03, 86.83) * mm, "end": v(203, 86.85) * mm});
            skLineSegment(sketch, "E1229", {"start": v(203, 86.85) * mm, "end": v(202.97, 86.88) * mm});
            skLineSegment(sketch, "E1230", {"start": v(202.97, 86.88) * mm, "end": v(202.96, 86.93) * mm});
            skLineSegment(sketch, "E1231", {"start": v(202.96, 86.93) * mm, "end": v(202.95, 87.1) * mm});
            skLineSegment(sketch, "E1232", {"start": v(202.95, 87.1) * mm, "end": v(202.95, 87.14) * mm});
            skLineSegment(sketch, "E1233", {"start": v(202.95, 87.14) * mm, "end": v(202.96, 87.22) * mm});
            skLineSegment(sketch, "E1234", {"start": v(202.96, 87.22) * mm, "end": v(202.99, 87.27) * mm});
            skLineSegment(sketch, "E1235", {"start": v(202.99, 87.27) * mm, "end": v(203.04, 87.3) * mm});
            skLineSegment(sketch, "E1236", {"start": v(203.04, 87.3) * mm, "end": v(203.11, 87.3) * mm});
            skLineSegment(sketch, "E1237", {"start": v(203.11, 87.3) * mm, "end": v(203.31, 87.31) * mm});
            skLineSegment(sketch, "E1238", {"start": v(203.31, 87.31) * mm, "end": v(203.48, 87.33) * mm});
            skLineSegment(sketch, "E1239", {"start": v(203.48, 87.33) * mm, "end": v(203.61, 87.35) * mm});
            skLineSegment(sketch, "E1240", {"start": v(203.61, 87.35) * mm, "end": v(203.72, 87.38) * mm});
            skLineSegment(sketch, "E1241", {"start": v(203.72, 87.38) * mm, "end": v(203.8, 87.42) * mm});
            skLineSegment(sketch, "E1242", {"start": v(203.8, 87.42) * mm, "end": v(203.87, 87.47) * mm});
            skLineSegment(sketch, "E1243", {"start": v(203.87, 87.47) * mm, "end": v(203.93, 87.53) * mm});
            skLineSegment(sketch, "E1244", {"start": v(203.93, 87.53) * mm, "end": v(203.97, 87.6) * mm});
            skLineSegment(sketch, "E1245", {"start": v(203.97, 87.6) * mm, "end": v(204, 87.7) * mm});
            skLineSegment(sketch, "E1246", {"start": v(204, 87.7) * mm, "end": v(204.02, 87.84) * mm});
            skLineSegment(sketch, "E1247", {"start": v(204.02, 87.84) * mm, "end": v(204.03, 88.03) * mm});
            skLineSegment(sketch, "E1248", {"start": v(204.03, 88.03) * mm, "end": v(204.03, 88.25) * mm});
            skLineSegment(sketch, "E1249", {"start": v(204.03, 88.25) * mm, "end": v(204.03, 88.58) * mm});
            skLineSegment(sketch, "E1250", {"start": v(204.03, 88.58) * mm, "end": v(204.01, 88.85) * mm});
            skLineSegment(sketch, "E1251", {"start": v(204.01, 88.85) * mm, "end": v(203.99, 89.05) * mm});
            skLineSegment(sketch, "E1252", {"start": v(203.99, 89.05) * mm, "end": v(203.96, 89.2) * mm});
            skLineSegment(sketch, "E1253", {"start": v(203.96, 89.2) * mm, "end": v(203.91, 89.3) * mm});
            skLineSegment(sketch, "E1254", {"start": v(203.91, 89.3) * mm, "end": v(203.84, 89.37) * mm});
            skLineSegment(sketch, "E1255", {"start": v(203.84, 89.37) * mm, "end": v(203.76, 89.42) * mm});
            skLineSegment(sketch, "E1256", {"start": v(203.76, 89.42) * mm, "end": v(203.65, 89.43) * mm});
            skLineSegment(sketch, "E1257", {"start": v(203.65, 89.43) * mm, "end": v(203.58, 89.43) * mm});
            skLineSegment(sketch, "E1258", {"start": v(203.58, 89.43) * mm, "end": v(203.52, 89.4) * mm});
            skLineSegment(sketch, "E1259", {"start": v(203.52, 89.4) * mm, "end": v(203.46, 89.38) * mm});
            skLineSegment(sketch, "E1260", {"start": v(203.46, 89.38) * mm, "end": v(203.4, 89.34) * mm});
            skLineSegment(sketch, "E1261", {"start": v(203.4, 89.34) * mm, "end": v(203.36, 89.29) * mm});
            skLineSegment(sketch, "E1262", {"start": v(203.36, 89.29) * mm, "end": v(203.33, 89.23) * mm});
            skLineSegment(sketch, "E1263", {"start": v(203.33, 89.23) * mm, "end": v(203.3, 89.17) * mm});
            skLineSegment(sketch, "E1264", {"start": v(203.3, 89.17) * mm, "end": v(203.3, 89.1) * mm});
            skLineSegment(sketch, "E1265", {"start": v(203.3, 89.1) * mm, "end": v(203.3, 88.98) * mm});
            skLineSegment(sketch, "E1266", {"start": v(203.3, 88.98) * mm, "end": v(203.33, 88.82) * mm});
            skLineSegment(sketch, "E1267", {"start": v(203.33, 88.82) * mm, "end": v(203.37, 88.6) * mm});
            skLineSegment(sketch, "E1268", {"start": v(203.37, 88.6) * mm, "end": v(203.38, 88.44) * mm});
            skLineSegment(sketch, "E1269", {"start": v(203.38, 88.44) * mm, "end": v(203.37, 88.33) * mm});
            skLineSegment(sketch, "E1270", {"start": v(203.37, 88.33) * mm, "end": v(203.34, 88.24) * mm});
            skLineSegment(sketch, "E1271", {"start": v(203.34, 88.24) * mm, "end": v(203.3, 88.16) * mm});
            skLineSegment(sketch, "E1272", {"start": v(203.3, 88.16) * mm, "end": v(203.24, 88.1) * mm});
            skLineSegment(sketch, "E1273", {"start": v(203.24, 88.1) * mm, "end": v(203.16, 88.04) * mm});
            skLineSegment(sketch, "E1274", {"start": v(203.16, 88.04) * mm, "end": v(203.08, 88) * mm});
            skLineSegment(sketch, "E1275", {"start": v(203.08, 88) * mm, "end": v(202.99, 87.98) * mm});
            skLineSegment(sketch, "E1276", {"start": v(202.99, 87.98) * mm, "end": v(202.9, 87.97) * mm});
            skLineSegment(sketch, "E1277", {"start": v(202.9, 87.97) * mm, "end": v(202.77, 87.98) * mm});
            skLineSegment(sketch, "E1278", {"start": v(202.77, 87.98) * mm, "end": v(202.67, 88.02) * mm});
            skLineSegment(sketch, "E1279", {"start": v(202.67, 88.02) * mm, "end": v(202.58, 88.08) * mm});
            skLineSegment(sketch, "E1280", {"start": v(202.58, 88.08) * mm, "end": v(202.5, 88.16) * mm});
            skLineSegment(sketch, "E1281", {"start": v(202.5, 88.16) * mm, "end": v(202.44, 88.27) * mm});
            skLineSegment(sketch, "E1282", {"start": v(202.44, 88.27) * mm, "end": v(202.4, 88.39) * mm});
            skLineSegment(sketch, "E1283", {"start": v(202.4, 88.39) * mm, "end": v(202.37, 88.51) * mm});
            skLineSegment(sketch, "E1284", {"start": v(202.37, 88.51) * mm, "end": v(202.36, 88.66) * mm});
            skLineSegment(sketch, "E1285", {"start": v(202.36, 88.66) * mm, "end": v(202.37, 88.78) * mm});
            skLineSegment(sketch, "E1286", {"start": v(202.37, 88.78) * mm, "end": v(202.39, 88.9) * mm});
            skLineSegment(sketch, "E1287", {"start": v(202.39, 88.9) * mm, "end": v(202.42, 89.02) * mm});
            skLineSegment(sketch, "E1288", {"start": v(202.42, 89.02) * mm, "end": v(202.46, 89.14) * mm});
            skLineSegment(sketch, "E1289", {"start": v(202.46, 89.14) * mm, "end": v(202.52, 89.25) * mm});
            skLineSegment(sketch, "E1290", {"start": v(202.52, 89.25) * mm, "end": v(202.59, 89.35) * mm});
            skLineSegment(sketch, "E1291", {"start": v(202.59, 89.35) * mm, "end": v(202.67, 89.46) * mm});
            skLineSegment(sketch, "E1292", {"start": v(202.67, 89.46) * mm, "end": v(202.76, 89.56) * mm});
            skLineSegment(sketch, "E1293", {"start": v(202.76, 89.56) * mm, "end": v(202.86, 89.65) * mm});
            skLineSegment(sketch, "E1294", {"start": v(202.86, 89.65) * mm, "end": v(202.98, 89.72) * mm});
            skLineSegment(sketch, "E1295", {"start": v(202.98, 89.72) * mm, "end": v(203.1, 89.8) * mm});
            skLineSegment(sketch, "E1296", {"start": v(203.1, 89.8) * mm, "end": v(203.23, 89.85) * mm});
            skLineSegment(sketch, "E1297", {"start": v(203.23, 89.85) * mm, "end": v(203.37, 89.89) * mm});
            skLineSegment(sketch, "E1298", {"start": v(203.37, 89.89) * mm, "end": v(203.51, 89.92) * mm});
            skLineSegment(sketch, "E1299", {"start": v(203.51, 89.92) * mm, "end": v(203.67, 89.94) * mm});
            skLineSegment(sketch, "E1300", {"start": v(203.67, 89.94) * mm, "end": v(203.83, 89.94) * mm});
            skLineSegment(sketch, "E1301", {"start": v(203.83, 89.94) * mm, "end": v(204.02, 89.93) * mm});
            skLineSegment(sketch, "E1302", {"start": v(204.02, 89.93) * mm, "end": v(204.2, 89.91) * mm});
            skLineSegment(sketch, "E1303", {"start": v(204.2, 89.91) * mm, "end": v(204.37, 89.87) * mm});
            skLineSegment(sketch, "E1304", {"start": v(204.37, 89.87) * mm, "end": v(204.52, 89.82) * mm});
            skLineSegment(sketch, "E1305", {"start": v(204.52, 89.82) * mm, "end": v(204.66, 89.76) * mm});
            skLineSegment(sketch, "E1306", {"start": v(204.66, 89.76) * mm, "end": v(204.8, 89.67) * mm});
            skLineSegment(sketch, "E1307", {"start": v(204.8, 89.67) * mm, "end": v(204.92, 89.58) * mm});
            skLineSegment(sketch, "E1308", {"start": v(204.92, 89.58) * mm, "end": v(205.02, 89.47) * mm});
            skLineSegment(sketch, "E1309", {"start": v(205.02, 89.47) * mm, "end": v(205.12, 89.35) * mm});
            skLineSegment(sketch, "E1310", {"start": v(205.12, 89.35) * mm, "end": v(205.2, 89.22) * mm});
            skLineSegment(sketch, "E1311", {"start": v(205.2, 89.22) * mm, "end": v(205.27, 89.1) * mm});
            skLineSegment(sketch, "E1312", {"start": v(205.27, 89.1) * mm, "end": v(205.33, 88.97) * mm});
            skLineSegment(sketch, "E1313", {"start": v(205.33, 88.97) * mm, "end": v(205.38, 88.83) * mm});
            skLineSegment(sketch, "E1314", {"start": v(205.38, 88.83) * mm, "end": v(205.4, 88.7) * mm});
            skLineSegment(sketch, "E1315", {"start": v(205.4, 88.7) * mm, "end": v(205.43, 88.56) * mm});
            skLineSegment(sketch, "E1316", {"start": v(205.43, 88.56) * mm, "end": v(205.43, 88.42) * mm});
            skLineSegment(sketch, "E1317", {"start": v(205.43, 88.42) * mm, "end": v(205.42, 88.2) * mm});
            skLineSegment(sketch, "E1318", {"start": v(205.42, 88.2) * mm, "end": v(205.4, 88.1) * mm});
            skLineSegment(sketch, "E1319", {"start": v(205.4, 88.1) * mm, "end": v(205.36, 88) * mm});
            skLineSegment(sketch, "E1320", {"start": v(205.36, 88) * mm, "end": v(205.33, 87.9) * mm});
            skLineSegment(sketch, "E1321", {"start": v(205.33, 87.9) * mm, "end": v(205.28, 87.8) * mm});
            skLineSegment(sketch, "E1322", {"start": v(205.28, 87.8) * mm, "end": v(205.16, 87.62) * mm});
            skLineSegment(sketch, "E1323", {"start": v(205.16, 87.62) * mm, "end": v(205.09, 87.54) * mm});
            skLineSegment(sketch, "E1324", {"start": v(205.09, 87.54) * mm, "end": v(205, 87.46) * mm});
            skLineSegment(sketch, "E1325", {"start": v(205, 87.46) * mm, "end": v(204.92, 87.38) * mm});
            skLineSegment(sketch, "E1326", {"start": v(204.92, 87.38) * mm, "end": v(204.82, 87.32) * mm});
            skLineSegment(sketch, "E1327", {"start": v(204.82, 87.32) * mm, "end": v(204.72, 87.26) * mm});
            skLineSegment(sketch, "E1328", {"start": v(204.72, 87.26) * mm, "end": v(204.6, 87.2) * mm});
            skLineSegment(sketch, "E1329", {"start": v(204.6, 87.2) * mm, "end": v(204.36, 87.12) * mm});
            skLineSegment(sketch, "E1330", {"start": v(204.36, 87.12) * mm, "end": v(204.25, 87.08) * mm});
            skLineSegment(sketch, "E1331", {"start": v(176.08, 89.8) * mm, "end": v(177.86, 89.8) * mm});
            skLineSegment(sketch, "E1332", {"start": v(177.86, 89.8) * mm, "end": v(177.96, 89.8) * mm});
            skLineSegment(sketch, "E1333", {"start": v(177.96, 89.8) * mm, "end": v(178, 89.83) * mm});
            skLineSegment(sketch, "E1334", {"start": v(178, 89.83) * mm, "end": v(178.03, 89.85) * mm});
            skLineSegment(sketch, "E1335", {"start": v(178.03, 89.85) * mm, "end": v(178.08, 89.9) * mm});
            skLineSegment(sketch, "E1336", {"start": v(178.08, 89.9) * mm, "end": v(178.12, 89.93) * mm});
            skLineSegment(sketch, "E1337", {"start": v(178.12, 89.93) * mm, "end": v(178.17, 89.94) * mm});
            skLineSegment(sketch, "E1338", {"start": v(178.17, 89.94) * mm, "end": v(178.25, 89.94) * mm});
            skLineSegment(sketch, "E1339", {"start": v(178.25, 89.94) * mm, "end": v(178.38, 89.94) * mm});
            skLineSegment(sketch, "E1340", {"start": v(178.38, 89.94) * mm, "end": v(178.45, 89.92) * mm});
            skLineSegment(sketch, "E1341", {"start": v(178.45, 89.92) * mm, "end": v(178.48, 89.88) * mm});
            skLineSegment(sketch, "E1342", {"start": v(178.48, 89.88) * mm, "end": v(178.49, 89.82) * mm});
            skLineSegment(sketch, "E1343", {"start": v(178.49, 89.82) * mm, "end": v(178.48, 89.7) * mm});
            skLineSegment(sketch, "E1344", {"start": v(178.48, 89.7) * mm, "end": v(178.41, 88.9) * mm});
            skLineSegment(sketch, "E1345", {"start": v(178.41, 88.9) * mm, "end": v(178.4, 88.8) * mm});
            skLineSegment(sketch, "E1346", {"start": v(178.4, 88.8) * mm, "end": v(178.37, 88.75) * mm});
            skLineSegment(sketch, "E1347", {"start": v(178.37, 88.75) * mm, "end": v(178.32, 88.73) * mm});
            skLineSegment(sketch, "E1348", {"start": v(178.32, 88.73) * mm, "end": v(178.24, 88.72) * mm});
            skLineSegment(sketch, "E1349", {"start": v(178.24, 88.72) * mm, "end": v(176.49, 88.72) * mm});
            skLineSegment(sketch, "E1350", {"start": v(176.49, 88.72) * mm, "end": v(176.43, 87.58) * mm});
            skLineSegment(sketch, "E1351", {"start": v(176.43, 87.58) * mm, "end": v(176.61, 87.68) * mm});
            skLineSegment(sketch, "E1352", {"start": v(176.61, 87.68) * mm, "end": v(176.81, 87.76) * mm});
            skLineSegment(sketch, "E1353", {"start": v(176.81, 87.76) * mm, "end": v(177.02, 87.8) * mm});
            skLineSegment(sketch, "E1354", {"start": v(177.02, 87.8) * mm, "end": v(177.24, 87.82) * mm});
            skLineSegment(sketch, "E1355", {"start": v(177.24, 87.82) * mm, "end": v(177.42, 87.81) * mm});
            skLineSegment(sketch, "E1356", {"start": v(177.42, 87.81) * mm, "end": v(177.6, 87.79) * mm});
            skLineSegment(sketch, "E1357", {"start": v(177.6, 87.79) * mm, "end": v(177.75, 87.74) * mm});
            skLineSegment(sketch, "E1358", {"start": v(177.75, 87.74) * mm, "end": v(177.9, 87.68) * mm});
            skLineSegment(sketch, "E1359", {"start": v(177.9, 87.68) * mm, "end": v(178.06, 87.6) * mm});
            skLineSegment(sketch, "E1360", {"start": v(178.06, 87.6) * mm, "end": v(178.2, 87.51) * mm});
            skLineSegment(sketch, "E1361", {"start": v(178.2, 87.51) * mm, "end": v(178.32, 87.4) * mm});
            skLineSegment(sketch, "E1362", {"start": v(178.32, 87.4) * mm, "end": v(178.44, 87.27) * mm});
            skLineSegment(sketch, "E1363", {"start": v(178.44, 87.27) * mm, "end": v(178.55, 87.13) * mm});
            skLineSegment(sketch, "E1364", {"start": v(178.55, 87.13) * mm, "end": v(178.65, 86.98) * mm});
            skLineSegment(sketch, "E1365", {"start": v(178.65, 86.98) * mm, "end": v(178.73, 86.82) * mm});
            skLineSegment(sketch, "E1366", {"start": v(178.73, 86.82) * mm, "end": v(178.8, 86.64) * mm});
            skLineSegment(sketch, "E1367", {"start": v(178.8, 86.64) * mm, "end": v(178.85, 86.46) * mm});
            skLineSegment(sketch, "E1368", {"start": v(178.85, 86.46) * mm, "end": v(178.88, 86.27) * mm});
            skLineSegment(sketch, "E1369", {"start": v(178.88, 86.27) * mm, "end": v(178.9, 86.07) * mm});
            skLineSegment(sketch, "E1370", {"start": v(178.9, 86.07) * mm, "end": v(178.91, 85.87) * mm});
            skLineSegment(sketch, "E1371", {"start": v(178.91, 85.87) * mm, "end": v(178.9, 85.64) * mm});
            skLineSegment(sketch, "E1372", {"start": v(178.9, 85.64) * mm, "end": v(178.88, 85.42) * mm});
            skLineSegment(sketch, "E1373", {"start": v(178.88, 85.42) * mm, "end": v(178.84, 85.22) * mm});
            skLineSegment(sketch, "E1374", {"start": v(178.84, 85.22) * mm, "end": v(178.78, 85.03) * mm});
            skLineSegment(sketch, "E1375", {"start": v(178.78, 85.03) * mm, "end": v(178.7, 84.85) * mm});
            skLineSegment(sketch, "E1376", {"start": v(178.7, 84.85) * mm, "end": v(178.6, 84.68) * mm});
            skLineSegment(sketch, "E1377", {"start": v(178.6, 84.68) * mm, "end": v(178.5, 84.52) * mm});
            skLineSegment(sketch, "E1378", {"start": v(178.5, 84.52) * mm, "end": v(178.37, 84.37) * mm});
            skLineSegment(sketch, "E1379", {"start": v(178.37, 84.37) * mm, "end": v(178.23, 84.23) * mm});
            skLineSegment(sketch, "E1380", {"start": v(178.23, 84.23) * mm, "end": v(178.09, 84.12) * mm});
            skLineSegment(sketch, "E1381", {"start": v(178.09, 84.12) * mm, "end": v(177.93, 84.02) * mm});
            skLineSegment(sketch, "E1382", {"start": v(177.93, 84.02) * mm, "end": v(177.77, 83.94) * mm});
            skLineSegment(sketch, "E1383", {"start": v(177.77, 83.94) * mm, "end": v(177.6, 83.88) * mm});
            skLineSegment(sketch, "E1384", {"start": v(177.6, 83.88) * mm, "end": v(177.41, 83.83) * mm});
            skLineSegment(sketch, "E1385", {"start": v(177.41, 83.83) * mm, "end": v(177.22, 83.8) * mm});
            skLineSegment(sketch, "E1386", {"start": v(177.22, 83.8) * mm, "end": v(177.03, 83.8) * mm});
            skLineSegment(sketch, "E1387", {"start": v(177.03, 83.8) * mm, "end": v(176.87, 83.8) * mm});
            skLineSegment(sketch, "E1388", {"start": v(176.87, 83.8) * mm, "end": v(176.71, 83.82) * mm});
            skLineSegment(sketch, "E1389", {"start": v(176.71, 83.82) * mm, "end": v(176.57, 83.85) * mm});
            skLineSegment(sketch, "E1390", {"start": v(176.57, 83.85) * mm, "end": v(176.44, 83.9) * mm});
            skLineSegment(sketch, "E1391", {"start": v(176.44, 83.9) * mm, "end": v(176.32, 83.96) * mm});
            skLineSegment(sketch, "E1392", {"start": v(176.32, 83.96) * mm, "end": v(176.2, 84.03) * mm});
            skLineSegment(sketch, "E1393", {"start": v(176.2, 84.03) * mm, "end": v(176.1, 84.12) * mm});
            skLineSegment(sketch, "E1394", {"start": v(176.1, 84.12) * mm, "end": v(176, 84.22) * mm});
            skLineSegment(sketch, "E1395", {"start": v(176, 84.22) * mm, "end": v(175.92, 84.32) * mm});
            skLineSegment(sketch, "E1396", {"start": v(175.92, 84.32) * mm, "end": v(175.84, 84.43) * mm});
            skLineSegment(sketch, "E1397", {"start": v(175.84, 84.43) * mm, "end": v(175.78, 84.54) * mm});
            skLineSegment(sketch, "E1398", {"start": v(175.78, 84.54) * mm, "end": v(175.73, 84.64) * mm});
            skLineSegment(sketch, "E1399", {"start": v(175.73, 84.64) * mm, "end": v(175.7, 84.75) * mm});
            skLineSegment(sketch, "E1400", {"start": v(175.7, 84.75) * mm, "end": v(175.66, 84.87) * mm});
            skLineSegment(sketch, "E1401", {"start": v(175.66, 84.87) * mm, "end": v(175.65, 84.98) * mm});
            skLineSegment(sketch, "E1402", {"start": v(175.65, 84.98) * mm, "end": v(175.64, 85.1) * mm});
            skLineSegment(sketch, "E1403", {"start": v(175.64, 85.1) * mm, "end": v(175.65, 85.22) * mm});
            skLineSegment(sketch, "E1404", {"start": v(175.65, 85.22) * mm, "end": v(175.68, 85.34) * mm});
            skLineSegment(sketch, "E1405", {"start": v(175.68, 85.34) * mm, "end": v(175.72, 85.45) * mm});
            skLineSegment(sketch, "E1406", {"start": v(175.72, 85.45) * mm, "end": v(175.78, 85.55) * mm});
            skLineSegment(sketch, "E1407", {"start": v(175.78, 85.55) * mm, "end": v(175.86, 85.63) * mm});
            skLineSegment(sketch, "E1408", {"start": v(175.86, 85.63) * mm, "end": v(175.95, 85.7) * mm});
            skLineSegment(sketch, "E1409", {"start": v(175.95, 85.7) * mm, "end": v(176.05, 85.73) * mm});
            skLineSegment(sketch, "E1410", {"start": v(176.05, 85.73) * mm, "end": v(176.17, 85.74) * mm});
            skLineSegment(sketch, "E1411", {"start": v(176.17, 85.74) * mm, "end": v(176.28, 85.73) * mm});
            skLineSegment(sketch, "E1412", {"start": v(176.28, 85.73) * mm, "end": v(176.38, 85.7) * mm});
            skLineSegment(sketch, "E1413", {"start": v(176.38, 85.7) * mm, "end": v(176.46, 85.66) * mm});
            skLineSegment(sketch, "E1414", {"start": v(176.46, 85.66) * mm, "end": v(176.53, 85.6) * mm});
            skLineSegment(sketch, "E1415", {"start": v(176.53, 85.6) * mm, "end": v(176.6, 85.5) * mm});
            skLineSegment(sketch, "E1416", {"start": v(176.6, 85.5) * mm, "end": v(176.63, 85.41) * mm});
            skLineSegment(sketch, "E1417", {"start": v(176.63, 85.41) * mm, "end": v(176.66, 85.3) * mm});
            skLineSegment(sketch, "E1418", {"start": v(176.66, 85.3) * mm, "end": v(176.67, 85.18) * mm});
            skLineSegment(sketch, "E1419", {"start": v(176.67, 85.18) * mm, "end": v(176.66, 85.06) * mm});
            skLineSegment(sketch, "E1420", {"start": v(176.66, 85.06) * mm, "end": v(176.64, 84.93) * mm});
            skLineSegment(sketch, "E1421", {"start": v(176.64, 84.93) * mm, "end": v(176.6, 84.75) * mm});
            skLineSegment(sketch, "E1422", {"start": v(176.6, 84.75) * mm, "end": v(176.59, 84.64) * mm});
            skLineSegment(sketch, "E1423", {"start": v(176.59, 84.64) * mm, "end": v(176.6, 84.58) * mm});
            skLineSegment(sketch, "E1424", {"start": v(176.6, 84.58) * mm, "end": v(176.61, 84.52) * mm});
            skLineSegment(sketch, "E1425", {"start": v(176.61, 84.52) * mm, "end": v(176.64, 84.46) * mm});
            skLineSegment(sketch, "E1426", {"start": v(176.64, 84.46) * mm, "end": v(176.69, 84.4) * mm});
            skLineSegment(sketch, "E1427", {"start": v(176.69, 84.4) * mm, "end": v(176.74, 84.35) * mm});
            skLineSegment(sketch, "E1428", {"start": v(176.74, 84.35) * mm, "end": v(176.81, 84.3) * mm});
            skLineSegment(sketch, "E1429", {"start": v(176.81, 84.3) * mm, "end": v(176.9, 84.29) * mm});
            skLineSegment(sketch, "E1430", {"start": v(176.9, 84.29) * mm, "end": v(176.99, 84.28) * mm});
            skLineSegment(sketch, "E1431", {"start": v(176.99, 84.28) * mm, "end": v(177.07, 84.28) * mm});
            skLineSegment(sketch, "E1432", {"start": v(177.07, 84.28) * mm, "end": v(177.15, 84.3) * mm});
            skLineSegment(sketch, "E1433", {"start": v(177.15, 84.3) * mm, "end": v(177.22, 84.33) * mm});
            skLineSegment(sketch, "E1434", {"start": v(177.22, 84.33) * mm, "end": v(177.28, 84.37) * mm});
            skLineSegment(sketch, "E1435", {"start": v(177.28, 84.37) * mm, "end": v(177.34, 84.42) * mm});
            skLineSegment(sketch, "E1436", {"start": v(177.34, 84.42) * mm, "end": v(177.38, 84.48) * mm});
            skLineSegment(sketch, "E1437", {"start": v(177.38, 84.48) * mm, "end": v(177.41, 84.55) * mm});
            skLineSegment(sketch, "E1438", {"start": v(177.41, 84.55) * mm, "end": v(177.44, 84.63) * mm});
            skLineSegment(sketch, "E1439", {"start": v(177.44, 84.63) * mm, "end": v(177.45, 84.73) * mm});
            skLineSegment(sketch, "E1440", {"start": v(177.45, 84.73) * mm, "end": v(177.47, 84.88) * mm});
            skLineSegment(sketch, "E1441", {"start": v(177.47, 84.88) * mm, "end": v(177.47, 85.3) * mm});
            skLineSegment(sketch, "E1442", {"start": v(177.47, 85.3) * mm, "end": v(177.47, 85.97) * mm});
            skLineSegment(sketch, "E1443", {"start": v(177.47, 85.97) * mm, "end": v(177.46, 86.32) * mm});
            skLineSegment(sketch, "E1444", {"start": v(177.46, 86.32) * mm, "end": v(177.44, 86.6) * mm});
            skLineSegment(sketch, "E1445", {"start": v(177.44, 86.6) * mm, "end": v(177.4, 86.84) * mm});
            skLineSegment(sketch, "E1446", {"start": v(177.4, 86.84) * mm, "end": v(177.35, 87.01) * mm});
            skLineSegment(sketch, "E1447", {"start": v(177.35, 87.01) * mm, "end": v(177.28, 87.13) * mm});
            skLineSegment(sketch, "E1448", {"start": v(177.28, 87.13) * mm, "end": v(177.24, 87.18) * mm});
            skLineSegment(sketch, "E1449", {"start": v(177.24, 87.18) * mm, "end": v(177.2, 87.22) * mm});
            skLineSegment(sketch, "E1450", {"start": v(177.2, 87.22) * mm, "end": v(177.14, 87.25) * mm});
            skLineSegment(sketch, "E1451", {"start": v(177.14, 87.25) * mm, "end": v(177.08, 87.28) * mm});
            skLineSegment(sketch, "E1452", {"start": v(177.08, 87.28) * mm, "end": v(177.02, 87.29) * mm});
            skLineSegment(sketch, "E1453", {"start": v(177.02, 87.29) * mm, "end": v(176.95, 87.3) * mm});
            skLineSegment(sketch, "E1454", {"start": v(176.95, 87.3) * mm, "end": v(176.86, 87.29) * mm});
            skLineSegment(sketch, "E1455", {"start": v(176.86, 87.29) * mm, "end": v(176.77, 87.26) * mm});
            skLineSegment(sketch, "E1456", {"start": v(176.77, 87.26) * mm, "end": v(176.69, 87.22) * mm});
            skLineSegment(sketch, "E1457", {"start": v(176.69, 87.22) * mm, "end": v(176.62, 87.17) * mm});
            skLineSegment(sketch, "E1458", {"start": v(176.62, 87.17) * mm, "end": v(176.55, 87.1) * mm});
            skLineSegment(sketch, "E1459", {"start": v(176.55, 87.1) * mm, "end": v(176.5, 87) * mm});
            skLineSegment(sketch, "E1460", {"start": v(176.5, 87) * mm, "end": v(176.44, 86.9) * mm});
            skLineSegment(sketch, "E1461", {"start": v(176.44, 86.9) * mm, "end": v(176.4, 86.78) * mm});
            skLineSegment(sketch, "E1462", {"start": v(176.4, 86.78) * mm, "end": v(176.36, 86.69) * mm});
            skLineSegment(sketch, "E1463", {"start": v(176.36, 86.69) * mm, "end": v(176.32, 86.63) * mm});
            skLineSegment(sketch, "E1464", {"start": v(176.32, 86.63) * mm, "end": v(176.27, 86.6) * mm});
            skLineSegment(sketch, "E1465", {"start": v(176.27, 86.6) * mm, "end": v(176.18, 86.6) * mm});
            skLineSegment(sketch, "E1466", {"start": v(176.18, 86.6) * mm, "end": v(176.02, 86.59) * mm});
            skLineSegment(sketch, "E1467", {"start": v(176.02, 86.59) * mm, "end": v(175.96, 86.6) * mm});
            skLineSegment(sketch, "E1468", {"start": v(175.96, 86.6) * mm, "end": v(175.92, 86.61) * mm});
            skLineSegment(sketch, "E1469", {"start": v(175.92, 86.61) * mm, "end": v(175.9, 86.65) * mm});
            skLineSegment(sketch, "E1470", {"start": v(175.9, 86.65) * mm, "end": v(175.88, 86.7) * mm});
            skLineSegment(sketch, "E1471", {"start": v(175.88, 86.7) * mm, "end": v(175.89, 86.8) * mm});
            skLineSegment(sketch, "E1472", {"start": v(175.89, 86.8) * mm, "end": v(176.08, 89.8) * mm});
            skLineSegment(sketch, "E1473", {"start": v(144.68, 88.7) * mm, "end": v(143.13, 88.7) * mm});
            skLineSegment(sketch, "E1474", {"start": v(143.13, 88.7) * mm, "end": v(143.04, 88.7) * mm});
            skLineSegment(sketch, "E1475", {"start": v(143.04, 88.7) * mm, "end": v(142.97, 88.65) * mm});
            skLineSegment(sketch, "E1476", {"start": v(142.97, 88.65) * mm, "end": v(142.9, 88.57) * mm});
            skLineSegment(sketch, "E1477", {"start": v(142.9, 88.57) * mm, "end": v(142.85, 88.46) * mm});
            skLineSegment(sketch, "E1478", {"start": v(142.85, 88.46) * mm, "end": v(142.76, 88.28) * mm});
            skLineSegment(sketch, "E1479", {"start": v(142.76, 88.28) * mm, "end": v(142.72, 88.26) * mm});
            skLineSegment(sketch, "E1480", {"start": v(142.72, 88.26) * mm, "end": v(142.65, 88.24) * mm});
            skLineSegment(sketch, "E1481", {"start": v(142.65, 88.24) * mm, "end": v(142.54, 88.23) * mm});
            skLineSegment(sketch, "E1482", {"start": v(142.54, 88.23) * mm, "end": v(142.4, 88.22) * mm});
            skLineSegment(sketch, "E1483", {"start": v(142.4, 88.22) * mm, "end": v(142.34, 88.23) * mm});
            skLineSegment(sketch, "E1484", {"start": v(142.34, 88.23) * mm, "end": v(142.3, 88.25) * mm});
            skLineSegment(sketch, "E1485", {"start": v(142.3, 88.25) * mm, "end": v(142.28, 88.27) * mm});
            skLineSegment(sketch, "E1486", {"start": v(142.28, 88.27) * mm, "end": v(142.28, 88.3) * mm});
            skLineSegment(sketch, "E1487", {"start": v(142.28, 88.3) * mm, "end": v(142.28, 88.35) * mm});
            skLineSegment(sketch, "E1488", {"start": v(142.28, 88.35) * mm, "end": v(142.38, 89.61) * mm});
            skLineSegment(sketch, "E1489", {"start": v(142.38, 89.61) * mm, "end": v(142.4, 89.74) * mm});
            skLineSegment(sketch, "E1490", {"start": v(142.4, 89.74) * mm, "end": v(142.42, 89.78) * mm});
            skLineSegment(sketch, "E1491", {"start": v(142.42, 89.78) * mm, "end": v(142.44, 89.8) * mm});
            skLineSegment(sketch, "E1492", {"start": v(142.44, 89.8) * mm, "end": v(142.47, 89.82) * mm});
            skLineSegment(sketch, "E1493", {"start": v(142.47, 89.82) * mm, "end": v(142.51, 89.83) * mm});
            skLineSegment(sketch, "E1494", {"start": v(142.51, 89.83) * mm, "end": v(142.64, 89.84) * mm});
            skLineSegment(sketch, "E1495", {"start": v(142.64, 89.84) * mm, "end": v(145.5, 89.84) * mm});
            skLineSegment(sketch, "E1496", {"start": v(145.5, 89.84) * mm, "end": v(145.56, 89.84) * mm});
            skLineSegment(sketch, "E1497", {"start": v(145.56, 89.84) * mm, "end": v(145.6, 89.83) * mm});
            skLineSegment(sketch, "E1498", {"start": v(145.6, 89.83) * mm, "end": v(145.6, 89.8) * mm});
            skLineSegment(sketch, "E1499", {"start": v(145.6, 89.8) * mm, "end": v(145.61, 89.75) * mm});
            skLineSegment(sketch, "E1500", {"start": v(145.61, 89.75) * mm, "end": v(145.61, 89.6) * mm});
            skLineSegment(sketch, "E1501", {"start": v(145.61, 89.6) * mm, "end": v(145.6, 89.53) * mm});
            skLineSegment(sketch, "E1502", {"start": v(145.6, 89.53) * mm, "end": v(145.59, 89.46) * mm});
            skLineSegment(sketch, "E1503", {"start": v(145.59, 89.46) * mm, "end": v(145.5, 89.29) * mm});
            skLineSegment(sketch, "E1504", {"start": v(145.5, 89.29) * mm, "end": v(145.37, 89) * mm});
            skLineSegment(sketch, "E1505", {"start": v(145.37, 89) * mm, "end": v(145.23, 88.63) * mm});
            skLineSegment(sketch, "E1506", {"start": v(145.23, 88.63) * mm, "end": v(145.07, 88.18) * mm});
            skLineSegment(sketch, "E1507", {"start": v(145.07, 88.18) * mm, "end": v(144.9, 87.65) * mm});
            skLineSegment(sketch, "E1508", {"start": v(144.9, 87.65) * mm, "end": v(144.82, 87.36) * mm});
            skLineSegment(sketch, "E1509", {"start": v(144.82, 87.36) * mm, "end": v(144.75, 87.07) * mm});
            skLineSegment(sketch, "E1510", {"start": v(144.75, 87.07) * mm, "end": v(144.7, 86.77) * mm});
            skLineSegment(sketch, "E1511", {"start": v(144.7, 86.77) * mm, "end": v(144.64, 86.47) * mm});
            skLineSegment(sketch, "E1512", {"start": v(144.64, 86.47) * mm, "end": v(144.6, 86.15) * mm});
            skLineSegment(sketch, "E1513", {"start": v(144.6, 86.15) * mm, "end": v(144.58, 85.84) * mm});
            skLineSegment(sketch, "E1514", {"start": v(144.58, 85.84) * mm, "end": v(144.56, 85.51) * mm});
            skLineSegment(sketch, "E1515", {"start": v(144.56, 85.51) * mm, "end": v(144.56, 85.18) * mm});
            skLineSegment(sketch, "E1516", {"start": v(144.56, 85.18) * mm, "end": v(144.57, 84.75) * mm});
            skLineSegment(sketch, "E1517", {"start": v(144.57, 84.75) * mm, "end": v(144.58, 84.61) * mm});
            skLineSegment(sketch, "E1518", {"start": v(144.58, 84.61) * mm, "end": v(144.6, 84.53) * mm});
            skLineSegment(sketch, "E1519", {"start": v(144.6, 84.53) * mm, "end": v(144.62, 84.48) * mm});
            skLineSegment(sketch, "E1520", {"start": v(144.62, 84.48) * mm, "end": v(144.66, 84.44) * mm});
            skLineSegment(sketch, "E1521", {"start": v(144.66, 84.44) * mm, "end": v(144.7, 84.4) * mm});
            skLineSegment(sketch, "E1522", {"start": v(144.7, 84.4) * mm, "end": v(144.76, 84.37) * mm});
            skLineSegment(sketch, "E1523", {"start": v(144.76, 84.37) * mm, "end": v(144.8, 84.34) * mm});
            skLineSegment(sketch, "E1524", {"start": v(144.8, 84.34) * mm, "end": v(144.81, 84.3) * mm});
            skLineSegment(sketch, "E1525", {"start": v(144.81, 84.3) * mm, "end": v(144.83, 84.24) * mm});
            skLineSegment(sketch, "E1526", {"start": v(144.83, 84.24) * mm, "end": v(144.83, 84.16) * mm});
            skLineSegment(sketch, "E1527", {"start": v(144.83, 84.16) * mm, "end": v(144.83, 84) * mm});
            skLineSegment(sketch, "E1528", {"start": v(144.83, 84) * mm, "end": v(144.82, 83.93) * mm});
            skLineSegment(sketch, "E1529", {"start": v(144.82, 83.93) * mm, "end": v(144.78, 83.9) * mm});
            skLineSegment(sketch, "E1530", {"start": v(144.78, 83.9) * mm, "end": v(144.7, 83.9) * mm});
            skLineSegment(sketch, "E1531", {"start": v(144.7, 83.9) * mm, "end": v(143.12, 83.9) * mm});
            skLineSegment(sketch, "E1532", {"start": v(143.12, 83.9) * mm, "end": v(143.04, 83.9) * mm});
            skLineSegment(sketch, "E1533", {"start": v(143.04, 83.9) * mm, "end": v(143, 83.93) * mm});
            skLineSegment(sketch, "E1534", {"start": v(143, 83.93) * mm, "end": v(142.98, 84) * mm});
            skLineSegment(sketch, "E1535", {"start": v(142.98, 84) * mm, "end": v(142.97, 84.12) * mm});
            skLineSegment(sketch, "E1536", {"start": v(142.97, 84.12) * mm, "end": v(142.98, 84.25) * mm});
            skLineSegment(sketch, "E1537", {"start": v(142.98, 84.25) * mm, "end": v(143, 84.32) * mm});
            skLineSegment(sketch, "E1538", {"start": v(143, 84.32) * mm, "end": v(143.03, 84.37) * mm});
            skLineSegment(sketch, "E1539", {"start": v(143.03, 84.37) * mm, "end": v(143.11, 84.41) * mm});
            skLineSegment(sketch, "E1540", {"start": v(143.11, 84.41) * mm, "end": v(143.17, 84.46) * mm});
            skLineSegment(sketch, "E1541", {"start": v(143.17, 84.46) * mm, "end": v(143.2, 84.51) * mm});
            skLineSegment(sketch, "E1542", {"start": v(143.2, 84.51) * mm, "end": v(143.21, 84.6) * mm});
            skLineSegment(sketch, "E1543", {"start": v(143.21, 84.6) * mm, "end": v(143.22, 84.73) * mm});
            skLineSegment(sketch, "E1544", {"start": v(143.22, 84.73) * mm, "end": v(143.23, 85) * mm});
            skLineSegment(sketch, "E1545", {"start": v(143.23, 85) * mm, "end": v(143.27, 85.3) * mm});
            skLineSegment(sketch, "E1546", {"start": v(143.27, 85.3) * mm, "end": v(143.34, 85.65) * mm});
            skLineSegment(sketch, "E1547", {"start": v(143.34, 85.65) * mm, "end": v(143.44, 86.04) * mm});
            skLineSegment(sketch, "E1548", {"start": v(143.44, 86.04) * mm, "end": v(143.57, 86.44) * mm});
            skLineSegment(sketch, "E1549", {"start": v(143.57, 86.44) * mm, "end": v(143.72, 86.84) * mm});
            skLineSegment(sketch, "E1550", {"start": v(143.72, 86.84) * mm, "end": v(143.9, 87.24) * mm});
            skLineSegment(sketch, "E1551", {"start": v(143.9, 87.24) * mm, "end": v(144.1, 87.62) * mm});
            skLineSegment(sketch, "E1552", {"start": v(144.1, 87.62) * mm, "end": v(144.68, 88.7) * mm});
            skLineSegment(sketch, "E1553", {"start": v(117.54, 85.87) * mm, "end": v(117.45, 85.78) * mm});
            skLineSegment(sketch, "E1554", {"start": v(117.45, 85.78) * mm, "end": v(117.36, 85.7) * mm});
            skLineSegment(sketch, "E1555", {"start": v(117.36, 85.7) * mm, "end": v(117.27, 85.64) * mm});
            skLineSegment(sketch, "E1556", {"start": v(117.27, 85.64) * mm, "end": v(117.18, 85.59) * mm});
            skLineSegment(sketch, "E1557", {"start": v(117.18, 85.59) * mm, "end": v(117.09, 85.55) * mm});
            skLineSegment(sketch, "E1558", {"start": v(117.09, 85.55) * mm, "end": v(117, 85.52) * mm});
            skLineSegment(sketch, "E1559", {"start": v(117, 85.52) * mm, "end": v(116.9, 85.5) * mm});
            skLineSegment(sketch, "E1560", {"start": v(116.9, 85.5) * mm, "end": v(116.8, 85.5) * mm});
            skLineSegment(sketch, "E1561", {"start": v(116.8, 85.5) * mm, "end": v(116.67, 85.5) * mm});
            skLineSegment(sketch, "E1562", {"start": v(116.67, 85.5) * mm, "end": v(116.56, 85.53) * mm});
            skLineSegment(sketch, "E1563", {"start": v(116.56, 85.53) * mm, "end": v(116.44, 85.57) * mm});
            skLineSegment(sketch, "E1564", {"start": v(116.44, 85.57) * mm, "end": v(116.33, 85.63) * mm});
            skLineSegment(sketch, "E1565", {"start": v(116.33, 85.63) * mm, "end": v(116.22, 85.7) * mm});
            skLineSegment(sketch, "E1566", {"start": v(116.22, 85.7) * mm, "end": v(116.12, 85.8) * mm});
            skLineSegment(sketch, "E1567", {"start": v(116.12, 85.8) * mm, "end": v(116.03, 85.9) * mm});
            skLineSegment(sketch, "E1568", {"start": v(116.03, 85.9) * mm, "end": v(115.93, 86.02) * mm});
            skLineSegment(sketch, "E1569", {"start": v(115.93, 86.02) * mm, "end": v(115.85, 86.16) * mm});
            skLineSegment(sketch, "E1570", {"start": v(115.85, 86.16) * mm, "end": v(115.77, 86.31) * mm});
            skLineSegment(sketch, "E1571", {"start": v(115.77, 86.31) * mm, "end": v(115.7, 86.48) * mm});
            skLineSegment(sketch, "E1572", {"start": v(115.7, 86.48) * mm, "end": v(115.66, 86.66) * mm});
            skLineSegment(sketch, "E1573", {"start": v(115.66, 86.66) * mm, "end": v(115.62, 86.85) * mm});
            skLineSegment(sketch, "E1574", {"start": v(115.62, 86.85) * mm, "end": v(115.59, 87.06) * mm});
            skLineSegment(sketch, "E1575", {"start": v(115.59, 87.06) * mm, "end": v(115.57, 87.27) * mm});
            skLineSegment(sketch, "E1576", {"start": v(115.57, 87.27) * mm, "end": v(115.57, 87.5) * mm});
            skLineSegment(sketch, "E1577", {"start": v(115.57, 87.5) * mm, "end": v(115.58, 87.78) * mm});
            skLineSegment(sketch, "E1578", {"start": v(115.58, 87.78) * mm, "end": v(115.6, 88.06) * mm});
            skLineSegment(sketch, "E1579", {"start": v(115.6, 88.06) * mm, "end": v(115.66, 88.33) * mm});
            skLineSegment(sketch, "E1580", {"start": v(115.66, 88.33) * mm, "end": v(115.73, 88.6) * mm});
            skLineSegment(sketch, "E1581", {"start": v(115.73, 88.6) * mm, "end": v(115.83, 88.87) * mm});
            skLineSegment(sketch, "E1582", {"start": v(115.83, 88.87) * mm, "end": v(115.95, 89.11) * mm});
            skLineSegment(sketch, "E1583", {"start": v(115.95, 89.11) * mm, "end": v(116.1, 89.33) * mm});
            skLineSegment(sketch, "E1584", {"start": v(116.1, 89.33) * mm, "end": v(116.28, 89.53) * mm});
            skLineSegment(sketch, "E1585", {"start": v(116.28, 89.53) * mm, "end": v(116.38, 89.62) * mm});
            skLineSegment(sketch, "E1586", {"start": v(116.38, 89.62) * mm, "end": v(116.48, 89.7) * mm});
            skLineSegment(sketch, "E1587", {"start": v(116.48, 89.7) * mm, "end": v(116.6, 89.77) * mm});
            skLineSegment(sketch, "E1588", {"start": v(116.6, 89.77) * mm, "end": v(116.72, 89.82) * mm});
            skLineSegment(sketch, "E1589", {"start": v(116.72, 89.82) * mm, "end": v(116.85, 89.86) * mm});
            skLineSegment(sketch, "E1590", {"start": v(116.85, 89.86) * mm, "end": v(116.98, 89.9) * mm});
            skLineSegment(sketch, "E1591", {"start": v(116.98, 89.9) * mm, "end": v(117.13, 89.9) * mm});
            skLineSegment(sketch, "E1592", {"start": v(117.13, 89.9) * mm, "end": v(117.28, 89.91) * mm});
            skLineSegment(sketch, "E1593", {"start": v(117.28, 89.91) * mm, "end": v(117.47, 89.9) * mm});
            skLineSegment(sketch, "E1594", {"start": v(117.47, 89.9) * mm, "end": v(117.65, 89.87) * mm});
            skLineSegment(sketch, "E1595", {"start": v(117.65, 89.87) * mm, "end": v(117.83, 89.82) * mm});
            skLineSegment(sketch, "E1596", {"start": v(117.83, 89.82) * mm, "end": v(117.99, 89.75) * mm});
            skLineSegment(sketch, "E1597", {"start": v(117.99, 89.75) * mm, "end": v(118.14, 89.66) * mm});
            skLineSegment(sketch, "E1598", {"start": v(118.14, 89.66) * mm, "end": v(118.28, 89.55) * mm});
            skLineSegment(sketch, "E1599", {"start": v(118.28, 89.55) * mm, "end": v(118.41, 89.42) * mm});
            skLineSegment(sketch, "E1600", {"start": v(118.41, 89.42) * mm, "end": v(118.53, 89.27) * mm});
            skLineSegment(sketch, "E1601", {"start": v(118.53, 89.27) * mm, "end": v(118.64, 89.1) * mm});
            skLineSegment(sketch, "E1602", {"start": v(118.64, 89.1) * mm, "end": v(118.73, 88.9) * mm});
            skLineSegment(sketch, "E1603", {"start": v(118.73, 88.9) * mm, "end": v(118.8, 88.66) * mm});
            skLineSegment(sketch, "E1604", {"start": v(118.8, 88.66) * mm, "end": v(118.87, 88.4) * mm});
            skLineSegment(sketch, "E1605", {"start": v(118.87, 88.4) * mm, "end": v(118.92, 88.12) * mm});
            skLineSegment(sketch, "E1606", {"start": v(118.92, 88.12) * mm, "end": v(118.96, 87.8) * mm});
            skLineSegment(sketch, "E1607", {"start": v(118.96, 87.8) * mm, "end": v(118.98, 87.46) * mm});
            skLineSegment(sketch, "E1608", {"start": v(118.98, 87.46) * mm, "end": v(118.99, 87.09) * mm});
            skLineSegment(sketch, "E1609", {"start": v(118.99, 87.09) * mm, "end": v(118.98, 86.66) * mm});
            skLineSegment(sketch, "E1610", {"start": v(118.98, 86.66) * mm, "end": v(118.94, 86.27) * mm});
            skLineSegment(sketch, "E1611", {"start": v(118.94, 86.27) * mm, "end": v(118.88, 85.9) * mm});
            skLineSegment(sketch, "E1612", {"start": v(118.88, 85.9) * mm, "end": v(118.8, 85.58) * mm});
            skLineSegment(sketch, "E1613", {"start": v(118.8, 85.58) * mm, "end": v(118.7, 85.28) * mm});
            skLineSegment(sketch, "E1614", {"start": v(118.7, 85.28) * mm, "end": v(118.57, 85.02) * mm});
            skLineSegment(sketch, "E1615", {"start": v(118.57, 85.02) * mm, "end": v(118.5, 84.9) * mm});
            skLineSegment(sketch, "E1616", {"start": v(118.5, 84.9) * mm, "end": v(118.42, 84.78) * mm});
            skLineSegment(sketch, "E1617", {"start": v(118.42, 84.78) * mm, "end": v(118.34, 84.68) * mm});
            skLineSegment(sketch, "E1618", {"start": v(118.34, 84.68) * mm, "end": v(118.25, 84.58) * mm});
            skLineSegment(sketch, "E1619", {"start": v(118.25, 84.58) * mm, "end": v(118.05, 84.4) * mm});
            skLineSegment(sketch, "E1620", {"start": v(118.05, 84.4) * mm, "end": v(117.84, 84.25) * mm});
            skLineSegment(sketch, "E1621", {"start": v(117.84, 84.25) * mm, "end": v(117.62, 84.12) * mm});
            skLineSegment(sketch, "E1622", {"start": v(117.62, 84.12) * mm, "end": v(117.39, 84.01) * mm});
            skLineSegment(sketch, "E1623", {"start": v(117.39, 84.01) * mm, "end": v(117.13, 83.93) * mm});
            skLineSegment(sketch, "E1624", {"start": v(117.13, 83.93) * mm, "end": v(116.87, 83.87) * mm});
            skLineSegment(sketch, "E1625", {"start": v(116.87, 83.87) * mm, "end": v(116.59, 83.84) * mm});
            skLineSegment(sketch, "E1626", {"start": v(116.59, 83.84) * mm, "end": v(116.3, 83.82) * mm});
            skLineSegment(sketch, "E1627", {"start": v(116.3, 83.82) * mm, "end": v(116.12, 83.83) * mm});
            skLineSegment(sketch, "E1628", {"start": v(116.12, 83.83) * mm, "end": v(116.03, 83.85) * mm});
            skLineSegment(sketch, "E1629", {"start": v(116.03, 83.85) * mm, "end": v(116.01, 83.87) * mm});
            skLineSegment(sketch, "E1630", {"start": v(116.01, 83.87) * mm, "end": v(116, 83.9) * mm});
            skLineSegment(sketch, "E1631", {"start": v(116, 83.9) * mm, "end": v(115.99, 84.01) * mm});
            skLineSegment(sketch, "E1632", {"start": v(115.99, 84.01) * mm, "end": v(116, 84.18) * mm});
            skLineSegment(sketch, "E1633", {"start": v(116, 84.18) * mm, "end": v(116, 84.27) * mm});
            skLineSegment(sketch, "E1634", {"start": v(116, 84.27) * mm, "end": v(116.04, 84.3) * mm});
            skLineSegment(sketch, "E1635", {"start": v(116.04, 84.3) * mm, "end": v(116.1, 84.33) * mm});
            skLineSegment(sketch, "E1636", {"start": v(116.1, 84.33) * mm, "end": v(116.35, 84.36) * mm});
            skLineSegment(sketch, "E1637", {"start": v(116.35, 84.36) * mm, "end": v(116.58, 84.4) * mm});
            skLineSegment(sketch, "E1638", {"start": v(116.58, 84.4) * mm, "end": v(116.77, 84.45) * mm});
            skLineSegment(sketch, "E1639", {"start": v(116.77, 84.45) * mm, "end": v(116.94, 84.51) * mm});
            skLineSegment(sketch, "E1640", {"start": v(116.94, 84.51) * mm, "end": v(117.07, 84.58) * mm});
            skLineSegment(sketch, "E1641", {"start": v(117.07, 84.58) * mm, "end": v(117.2, 84.67) * mm});
            skLineSegment(sketch, "E1642", {"start": v(117.2, 84.67) * mm, "end": v(117.3, 84.78) * mm});
            skLineSegment(sketch, "E1643", {"start": v(117.3, 84.78) * mm, "end": v(117.39, 84.9) * mm});
            skLineSegment(sketch, "E1644", {"start": v(117.39, 84.9) * mm, "end": v(117.46, 85.05) * mm});
            skLineSegment(sketch, "E1645", {"start": v(117.46, 85.05) * mm, "end": v(117.5, 85.22) * mm});
            skLineSegment(sketch, "E1646", {"start": v(117.5, 85.22) * mm, "end": v(117.54, 85.4) * mm});
            skLineSegment(sketch, "E1647", {"start": v(117.54, 85.4) * mm, "end": v(117.55, 85.62) * mm});
            skLineSegment(sketch, "E1648", {"start": v(117.55, 85.62) * mm, "end": v(117.54, 85.87) * mm});
            skLineSegment(sketch, "E1649", {"start": v(117.54, 89.13) * mm, "end": v(117.53, 89.2) * mm});
            skLineSegment(sketch, "E1650", {"start": v(117.53, 89.2) * mm, "end": v(117.52, 89.27) * mm});
            skLineSegment(sketch, "E1651", {"start": v(117.52, 89.27) * mm, "end": v(117.5, 89.33) * mm});
            skLineSegment(sketch, "E1652", {"start": v(117.5, 89.33) * mm, "end": v(117.47, 89.38) * mm});
            skLineSegment(sketch, "E1653", {"start": v(117.47, 89.38) * mm, "end": v(117.43, 89.41) * mm});
            skLineSegment(sketch, "E1654", {"start": v(117.43, 89.41) * mm, "end": v(117.39, 89.44) * mm});
            skLineSegment(sketch, "E1655", {"start": v(117.39, 89.44) * mm, "end": v(117.33, 89.45) * mm});
            skLineSegment(sketch, "E1656", {"start": v(117.33, 89.45) * mm, "end": v(117.27, 89.46) * mm});
            skLineSegment(sketch, "E1657", {"start": v(117.27, 89.46) * mm, "end": v(117.2, 89.45) * mm});
            skLineSegment(sketch, "E1658", {"start": v(117.2, 89.45) * mm, "end": v(117.15, 89.43) * mm});
            skLineSegment(sketch, "E1659", {"start": v(117.15, 89.43) * mm, "end": v(117.1, 89.4) * mm});
            skLineSegment(sketch, "E1660", {"start": v(117.1, 89.4) * mm, "end": v(117.07, 89.37) * mm});
            skLineSegment(sketch, "E1661", {"start": v(117.07, 89.37) * mm, "end": v(117.04, 89.32) * mm});
            skLineSegment(sketch, "E1662", {"start": v(117.04, 89.32) * mm, "end": v(117.02, 89.26) * mm});
            skLineSegment(sketch, "E1663", {"start": v(117.02, 89.26) * mm, "end": v(117, 89.18) * mm});
            skLineSegment(sketch, "E1664", {"start": v(117, 89.18) * mm, "end": v(117, 89.1) * mm});
            skLineSegment(sketch, "E1665", {"start": v(117, 89.1) * mm, "end": v(117, 86.43) * mm});
            skLineSegment(sketch, "E1666", {"start": v(117, 86.43) * mm, "end": v(117, 86.37) * mm});
            skLineSegment(sketch, "E1667", {"start": v(117, 86.37) * mm, "end": v(117.02, 86.3) * mm});
            skLineSegment(sketch, "E1668", {"start": v(117.02, 86.3) * mm, "end": v(117.04, 86.25) * mm});
            skLineSegment(sketch, "E1669", {"start": v(117.04, 86.25) * mm, "end": v(117.07, 86.2) * mm});
            skLineSegment(sketch, "E1670", {"start": v(117.07, 86.2) * mm, "end": v(117.11, 86.15) * mm});
            skLineSegment(sketch, "E1671", {"start": v(117.11, 86.15) * mm, "end": v(117.16, 86.12) * mm});
            skLineSegment(sketch, "E1672", {"start": v(117.16, 86.12) * mm, "end": v(117.2, 86.1) * mm});
            skLineSegment(sketch, "E1673", {"start": v(117.2, 86.1) * mm, "end": v(117.26, 86.1) * mm});
            skLineSegment(sketch, "E1674", {"start": v(117.26, 86.1) * mm, "end": v(117.32, 86.1) * mm});
            skLineSegment(sketch, "E1675", {"start": v(117.32, 86.1) * mm, "end": v(117.37, 86.13) * mm});
            skLineSegment(sketch, "E1676", {"start": v(117.37, 86.13) * mm, "end": v(117.42, 86.17) * mm});
            skLineSegment(sketch, "E1677", {"start": v(117.42, 86.17) * mm, "end": v(117.46, 86.22) * mm});
            skLineSegment(sketch, "E1678", {"start": v(117.46, 86.22) * mm, "end": v(117.5, 86.29) * mm});
            skLineSegment(sketch, "E1679", {"start": v(117.5, 86.29) * mm, "end": v(117.52, 86.35) * mm});
            skLineSegment(sketch, "E1680", {"start": v(117.52, 86.35) * mm, "end": v(117.53, 86.43) * mm});
            skLineSegment(sketch, "E1681", {"start": v(117.53, 86.43) * mm, "end": v(117.54, 86.5) * mm});
            skLineSegment(sketch, "E1682", {"start": v(117.54, 86.5) * mm, "end": v(117.54, 89.13) * mm});
            skLineSegment(sketch, "E1683", {"start": v(82.06, 88.25) * mm, "end": v(81.9, 88.2) * mm});
            skLineSegment(sketch, "E1684", {"start": v(81.9, 88.2) * mm, "end": v(81.75, 88.17) * mm});
            skLineSegment(sketch, "E1685", {"start": v(81.75, 88.17) * mm, "end": v(81.61, 88.15) * mm});
            skLineSegment(sketch, "E1686", {"start": v(81.61, 88.15) * mm, "end": v(81.49, 88.14) * mm});
            skLineSegment(sketch, "E1687", {"start": v(81.49, 88.14) * mm, "end": v(81.44, 88.15) * mm});
            skLineSegment(sketch, "E1688", {"start": v(81.44, 88.15) * mm, "end": v(81.4, 88.17) * mm});
            skLineSegment(sketch, "E1689", {"start": v(81.4, 88.17) * mm, "end": v(81.38, 88.21) * mm});
            skLineSegment(sketch, "E1690", {"start": v(81.38, 88.21) * mm, "end": v(81.37, 88.27) * mm});
            skLineSegment(sketch, "E1691", {"start": v(81.37, 88.27) * mm, "end": v(81.37, 88.41) * mm});
            skLineSegment(sketch, "E1692", {"start": v(81.37, 88.41) * mm, "end": v(81.38, 88.49) * mm});
            skLineSegment(sketch, "E1693", {"start": v(81.38, 88.49) * mm, "end": v(81.4, 88.54) * mm});
            skLineSegment(sketch, "E1694", {"start": v(81.4, 88.54) * mm, "end": v(81.46, 88.59) * mm});
            skLineSegment(sketch, "E1695", {"start": v(81.46, 88.59) * mm, "end": v(81.57, 88.64) * mm});
            skLineSegment(sketch, "E1696", {"start": v(81.57, 88.64) * mm, "end": v(81.67, 88.68) * mm});
            skLineSegment(sketch, "E1697", {"start": v(81.67, 88.68) * mm, "end": v(81.78, 88.75) * mm});
            skLineSegment(sketch, "E1698", {"start": v(81.78, 88.75) * mm, "end": v(82.06, 88.94) * mm});
            skLineSegment(sketch, "E1699", {"start": v(82.06, 88.94) * mm, "end": v(82.21, 89.06) * mm});
            skLineSegment(sketch, "E1700", {"start": v(82.21, 89.06) * mm, "end": v(82.36, 89.2) * mm});
            skLineSegment(sketch, "E1701", {"start": v(82.36, 89.2) * mm, "end": v(82.51, 89.36) * mm});
            skLineSegment(sketch, "E1702", {"start": v(82.51, 89.36) * mm, "end": v(82.66, 89.54) * mm});
            skLineSegment(sketch, "E1703", {"start": v(82.66, 89.54) * mm, "end": v(82.84, 89.77) * mm});
            skLineSegment(sketch, "E1704", {"start": v(82.84, 89.77) * mm, "end": v(82.93, 89.86) * mm});
            skLineSegment(sketch, "E1705", {"start": v(82.93, 89.86) * mm, "end": v(82.98, 89.88) * mm});
            skLineSegment(sketch, "E1706", {"start": v(82.98, 89.88) * mm, "end": v(83.07, 89.89) * mm});
            skLineSegment(sketch, "E1707", {"start": v(83.07, 89.89) * mm, "end": v(83.38, 89.89) * mm});
            skLineSegment(sketch, "E1708", {"start": v(83.38, 89.89) * mm, "end": v(83.38, 84.5) * mm});
            skLineSegment(sketch, "E1709", {"start": v(83.38, 84.5) * mm, "end": v(83.39, 84.47) * mm});
            skLineSegment(sketch, "E1710", {"start": v(83.39, 84.47) * mm, "end": v(83.41, 84.43) * mm});
            skLineSegment(sketch, "E1711", {"start": v(83.41, 84.43) * mm, "end": v(83.45, 84.4) * mm});
            skLineSegment(sketch, "E1712", {"start": v(83.45, 84.4) * mm, "end": v(83.5, 84.36) * mm});
            skLineSegment(sketch, "E1713", {"start": v(83.5, 84.36) * mm, "end": v(83.6, 84.3) * mm});
            skLineSegment(sketch, "E1714", {"start": v(83.6, 84.3) * mm, "end": v(83.64, 84.25) * mm});
            skLineSegment(sketch, "E1715", {"start": v(83.64, 84.25) * mm, "end": v(83.66, 84.15) * mm});
            skLineSegment(sketch, "E1716", {"start": v(83.66, 84.15) * mm, "end": v(83.66, 83.95) * mm});
            skLineSegment(sketch, "E1717", {"start": v(83.66, 83.95) * mm, "end": v(83.65, 83.9) * mm});
            skLineSegment(sketch, "E1718", {"start": v(83.65, 83.9) * mm, "end": v(83.63, 83.88) * mm});
            skLineSegment(sketch, "E1719", {"start": v(83.63, 83.88) * mm, "end": v(83.59, 83.86) * mm});
            skLineSegment(sketch, "E1720", {"start": v(83.59, 83.86) * mm, "end": v(83.53, 83.85) * mm});
            skLineSegment(sketch, "E1721", {"start": v(83.53, 83.85) * mm, "end": v(81.83, 83.85) * mm});
            skLineSegment(sketch, "E1722", {"start": v(81.83, 83.85) * mm, "end": v(81.74, 83.86) * mm});
            skLineSegment(sketch, "E1723", {"start": v(81.74, 83.86) * mm, "end": v(81.7, 83.89) * mm});
            skLineSegment(sketch, "E1724", {"start": v(81.7, 83.89) * mm, "end": v(81.68, 83.94) * mm});
            skLineSegment(sketch, "E1725", {"start": v(81.68, 83.94) * mm, "end": v(81.67, 84.05) * mm});
            skLineSegment(sketch, "E1726", {"start": v(81.67, 84.05) * mm, "end": v(81.68, 84.2) * mm});
            skLineSegment(sketch, "E1727", {"start": v(81.68, 84.2) * mm, "end": v(81.7, 84.28) * mm});
            skLineSegment(sketch, "E1728", {"start": v(81.7, 84.28) * mm, "end": v(81.71, 84.3) * mm});
            skLineSegment(sketch, "E1729", {"start": v(81.71, 84.3) * mm, "end": v(81.74, 84.32) * mm});
            skLineSegment(sketch, "E1730", {"start": v(81.74, 84.32) * mm, "end": v(81.85, 84.37) * mm});
            skLineSegment(sketch, "E1731", {"start": v(81.85, 84.37) * mm, "end": v(81.94, 84.4) * mm});
            skLineSegment(sketch, "E1732", {"start": v(81.94, 84.4) * mm, "end": v(82, 84.44) * mm});
            skLineSegment(sketch, "E1733", {"start": v(82, 84.44) * mm, "end": v(82.04, 84.5) * mm});
            skLineSegment(sketch, "E1734", {"start": v(82.04, 84.5) * mm, "end": v(82.06, 84.55) * mm});
            skLineSegment(sketch, "E1735", {"start": v(82.06, 84.55) * mm, "end": v(82.06, 88.25) * mm});
            skLineSegment(sketch, "E1736", {"start": v(84.91, 88.25) * mm, "end": v(84.75, 88.2) * mm});
            skLineSegment(sketch, "E1737", {"start": v(84.75, 88.2) * mm, "end": v(84.6, 88.17) * mm});
            skLineSegment(sketch, "E1738", {"start": v(84.6, 88.17) * mm, "end": v(84.47, 88.15) * mm});
            skLineSegment(sketch, "E1739", {"start": v(84.47, 88.15) * mm, "end": v(84.34, 88.14) * mm});
            skLineSegment(sketch, "E1740", {"start": v(84.34, 88.14) * mm, "end": v(84.3, 88.15) * mm});
            skLineSegment(sketch, "E1741", {"start": v(84.3, 88.15) * mm, "end": v(84.26, 88.17) * mm});
            skLineSegment(sketch, "E1742", {"start": v(84.26, 88.17) * mm, "end": v(84.23, 88.21) * mm});
            skLineSegment(sketch, "E1743", {"start": v(84.23, 88.21) * mm, "end": v(84.23, 88.27) * mm});
            skLineSegment(sketch, "E1744", {"start": v(84.23, 88.27) * mm, "end": v(84.23, 88.41) * mm});
            skLineSegment(sketch, "E1745", {"start": v(84.23, 88.41) * mm, "end": v(84.23, 88.49) * mm});
            skLineSegment(sketch, "E1746", {"start": v(84.23, 88.49) * mm, "end": v(84.26, 88.54) * mm});
            skLineSegment(sketch, "E1747", {"start": v(84.26, 88.54) * mm, "end": v(84.32, 88.59) * mm});
            skLineSegment(sketch, "E1748", {"start": v(84.32, 88.59) * mm, "end": v(84.43, 88.64) * mm});
            skLineSegment(sketch, "E1749", {"start": v(84.43, 88.64) * mm, "end": v(84.52, 88.68) * mm});
            skLineSegment(sketch, "E1750", {"start": v(84.52, 88.68) * mm, "end": v(84.64, 88.75) * mm});
            skLineSegment(sketch, "E1751", {"start": v(84.64, 88.75) * mm, "end": v(84.91, 88.94) * mm});
            skLineSegment(sketch, "E1752", {"start": v(84.91, 88.94) * mm, "end": v(85.07, 89.06) * mm});
            skLineSegment(sketch, "E1753", {"start": v(85.07, 89.06) * mm, "end": v(85.22, 89.2) * mm});
            skLineSegment(sketch, "E1754", {"start": v(85.22, 89.2) * mm, "end": v(85.37, 89.36) * mm});
            skLineSegment(sketch, "E1755", {"start": v(85.37, 89.36) * mm, "end": v(85.52, 89.54) * mm});
            skLineSegment(sketch, "E1756", {"start": v(85.52, 89.54) * mm, "end": v(85.7, 89.77) * mm});
            skLineSegment(sketch, "E1757", {"start": v(85.7, 89.77) * mm, "end": v(85.78, 89.86) * mm});
            skLineSegment(sketch, "E1758", {"start": v(85.78, 89.86) * mm, "end": v(85.84, 89.88) * mm});
            skLineSegment(sketch, "E1759", {"start": v(85.84, 89.88) * mm, "end": v(85.93, 89.89) * mm});
            skLineSegment(sketch, "E1760", {"start": v(85.93, 89.89) * mm, "end": v(86.23, 89.89) * mm});
            skLineSegment(sketch, "E1761", {"start": v(86.23, 89.89) * mm, "end": v(86.23, 84.5) * mm});
            skLineSegment(sketch, "E1762", {"start": v(86.23, 84.5) * mm, "end": v(86.24, 84.47) * mm});
            skLineSegment(sketch, "E1763", {"start": v(86.24, 84.47) * mm, "end": v(86.27, 84.43) * mm});
            skLineSegment(sketch, "E1764", {"start": v(86.27, 84.43) * mm, "end": v(86.3, 84.4) * mm});
            skLineSegment(sketch, "E1765", {"start": v(86.3, 84.4) * mm, "end": v(86.36, 84.36) * mm});
            skLineSegment(sketch, "E1766", {"start": v(86.36, 84.36) * mm, "end": v(86.45, 84.3) * mm});
            skLineSegment(sketch, "E1767", {"start": v(86.45, 84.3) * mm, "end": v(86.5, 84.25) * mm});
            skLineSegment(sketch, "E1768", {"start": v(86.5, 84.25) * mm, "end": v(86.51, 84.15) * mm});
            skLineSegment(sketch, "E1769", {"start": v(86.51, 84.15) * mm, "end": v(86.52, 83.95) * mm});
            skLineSegment(sketch, "E1770", {"start": v(86.52, 83.95) * mm, "end": v(86.5, 83.9) * mm});
            skLineSegment(sketch, "E1771", {"start": v(86.5, 83.9) * mm, "end": v(86.48, 83.88) * mm});
            skLineSegment(sketch, "E1772", {"start": v(86.48, 83.88) * mm, "end": v(86.44, 83.86) * mm});
            skLineSegment(sketch, "E1773", {"start": v(86.44, 83.86) * mm, "end": v(86.39, 83.85) * mm});
            skLineSegment(sketch, "E1774", {"start": v(86.39, 83.85) * mm, "end": v(84.68, 83.85) * mm});
            skLineSegment(sketch, "E1775", {"start": v(84.68, 83.85) * mm, "end": v(84.6, 83.86) * mm});
            skLineSegment(sketch, "E1776", {"start": v(84.6, 83.86) * mm, "end": v(84.55, 83.89) * mm});
            skLineSegment(sketch, "E1777", {"start": v(84.55, 83.89) * mm, "end": v(84.53, 83.94) * mm});
            skLineSegment(sketch, "E1778", {"start": v(84.53, 83.94) * mm, "end": v(84.53, 84.05) * mm});
            skLineSegment(sketch, "E1779", {"start": v(84.53, 84.05) * mm, "end": v(84.53, 84.2) * mm});
            skLineSegment(sketch, "E1780", {"start": v(84.53, 84.2) * mm, "end": v(84.55, 84.28) * mm});
            skLineSegment(sketch, "E1781", {"start": v(84.55, 84.28) * mm, "end": v(84.57, 84.3) * mm});
            skLineSegment(sketch, "E1782", {"start": v(84.57, 84.3) * mm, "end": v(84.6, 84.32) * mm});
            skLineSegment(sketch, "E1783", {"start": v(84.6, 84.32) * mm, "end": v(84.7, 84.37) * mm});
            skLineSegment(sketch, "E1784", {"start": v(84.7, 84.37) * mm, "end": v(84.8, 84.4) * mm});
            skLineSegment(sketch, "E1785", {"start": v(84.8, 84.4) * mm, "end": v(84.86, 84.44) * mm});
            skLineSegment(sketch, "E1786", {"start": v(84.86, 84.44) * mm, "end": v(84.9, 84.5) * mm});
            skLineSegment(sketch, "E1787", {"start": v(84.9, 84.5) * mm, "end": v(84.91, 84.55) * mm});
            skLineSegment(sketch, "E1788", {"start": v(84.91, 84.55) * mm, "end": v(84.91, 88.25) * mm});
            skLineSegment(sketch, "E1789", {"start": v(54.81, 88.26) * mm, "end": v(54.65, 88.21) * mm});
            skLineSegment(sketch, "E1790", {"start": v(54.65, 88.21) * mm, "end": v(54.5, 88.18) * mm});
            skLineSegment(sketch, "E1791", {"start": v(54.5, 88.18) * mm, "end": v(54.37, 88.15) * mm});
            skLineSegment(sketch, "E1792", {"start": v(54.37, 88.15) * mm, "end": v(54.24, 88.15) * mm});
            skLineSegment(sketch, "E1793", {"start": v(54.24, 88.15) * mm, "end": v(54.2, 88.15) * mm});
            skLineSegment(sketch, "E1794", {"start": v(54.2, 88.15) * mm, "end": v(54.16, 88.18) * mm});
            skLineSegment(sketch, "E1795", {"start": v(54.16, 88.18) * mm, "end": v(54.14, 88.22) * mm});
            skLineSegment(sketch, "E1796", {"start": v(54.14, 88.22) * mm, "end": v(54.13, 88.27) * mm});
            skLineSegment(sketch, "E1797", {"start": v(54.13, 88.27) * mm, "end": v(54.13, 88.42) * mm});
            skLineSegment(sketch, "E1798", {"start": v(54.13, 88.42) * mm, "end": v(54.14, 88.5) * mm});
            skLineSegment(sketch, "E1799", {"start": v(54.14, 88.5) * mm, "end": v(54.16, 88.55) * mm});
            skLineSegment(sketch, "E1800", {"start": v(54.16, 88.55) * mm, "end": v(54.22, 88.6) * mm});
            skLineSegment(sketch, "E1801", {"start": v(54.22, 88.6) * mm, "end": v(54.33, 88.64) * mm});
            skLineSegment(sketch, "E1802", {"start": v(54.33, 88.64) * mm, "end": v(54.43, 88.7) * mm});
            skLineSegment(sketch, "E1803", {"start": v(54.43, 88.7) * mm, "end": v(54.54, 88.76) * mm});
            skLineSegment(sketch, "E1804", {"start": v(54.54, 88.76) * mm, "end": v(54.82, 88.95) * mm});
            skLineSegment(sketch, "E1805", {"start": v(54.82, 88.95) * mm, "end": v(54.97, 89.07) * mm});
            skLineSegment(sketch, "E1806", {"start": v(54.97, 89.07) * mm, "end": v(55.12, 89.21) * mm});
            skLineSegment(sketch, "E1807", {"start": v(55.12, 89.21) * mm, "end": v(55.27, 89.37) * mm});
            skLineSegment(sketch, "E1808", {"start": v(55.27, 89.37) * mm, "end": v(55.42, 89.55) * mm});
            skLineSegment(sketch, "E1809", {"start": v(55.42, 89.55) * mm, "end": v(55.6, 89.78) * mm});
            skLineSegment(sketch, "E1810", {"start": v(55.6, 89.78) * mm, "end": v(55.69, 89.87) * mm});
            skLineSegment(sketch, "E1811", {"start": v(55.69, 89.87) * mm, "end": v(55.74, 89.89) * mm});
            skLineSegment(sketch, "E1812", {"start": v(55.74, 89.89) * mm, "end": v(55.83, 89.9) * mm});
            skLineSegment(sketch, "E1813", {"start": v(55.83, 89.9) * mm, "end": v(56.14, 89.9) * mm});
            skLineSegment(sketch, "E1814", {"start": v(56.14, 89.9) * mm, "end": v(56.14, 84.51) * mm});
            skLineSegment(sketch, "E1815", {"start": v(56.14, 84.51) * mm, "end": v(56.14, 84.47) * mm});
            skLineSegment(sketch, "E1816", {"start": v(56.14, 84.47) * mm, "end": v(56.17, 84.44) * mm});
            skLineSegment(sketch, "E1817", {"start": v(56.17, 84.44) * mm, "end": v(56.2, 84.4) * mm});
            skLineSegment(sketch, "E1818", {"start": v(56.2, 84.4) * mm, "end": v(56.26, 84.37) * mm});
            skLineSegment(sketch, "E1819", {"start": v(56.26, 84.37) * mm, "end": v(56.35, 84.32) * mm});
            skLineSegment(sketch, "E1820", {"start": v(56.35, 84.32) * mm, "end": v(56.4, 84.26) * mm});
            skLineSegment(sketch, "E1821", {"start": v(56.4, 84.26) * mm, "end": v(56.41, 84.16) * mm});
            skLineSegment(sketch, "E1822", {"start": v(56.41, 84.16) * mm, "end": v(56.42, 83.96) * mm});
            skLineSegment(sketch, "E1823", {"start": v(56.42, 83.96) * mm, "end": v(56.41, 83.91) * mm});
            skLineSegment(sketch, "E1824", {"start": v(56.41, 83.91) * mm, "end": v(56.39, 83.88) * mm});
            skLineSegment(sketch, "E1825", {"start": v(56.39, 83.88) * mm, "end": v(56.35, 83.87) * mm});
            skLineSegment(sketch, "E1826", {"start": v(56.35, 83.87) * mm, "end": v(56.29, 83.86) * mm});
            skLineSegment(sketch, "E1827", {"start": v(56.29, 83.86) * mm, "end": v(54.59, 83.86) * mm});
            skLineSegment(sketch, "E1828", {"start": v(54.59, 83.86) * mm, "end": v(54.5, 83.87) * mm});
            skLineSegment(sketch, "E1829", {"start": v(54.5, 83.87) * mm, "end": v(54.45, 83.9) * mm});
            skLineSegment(sketch, "E1830", {"start": v(54.45, 83.9) * mm, "end": v(54.44, 83.95) * mm});
            skLineSegment(sketch, "E1831", {"start": v(54.44, 83.95) * mm, "end": v(54.43, 84.06) * mm});
            skLineSegment(sketch, "E1832", {"start": v(54.43, 84.06) * mm, "end": v(54.43, 84.2) * mm});
            skLineSegment(sketch, "E1833", {"start": v(54.43, 84.2) * mm, "end": v(54.45, 84.29) * mm});
            skLineSegment(sketch, "E1834", {"start": v(54.45, 84.29) * mm, "end": v(54.47, 84.3) * mm});
            skLineSegment(sketch, "E1835", {"start": v(54.47, 84.3) * mm, "end": v(54.5, 84.33) * mm});
            skLineSegment(sketch, "E1836", {"start": v(54.5, 84.33) * mm, "end": v(54.6, 84.37) * mm});
            skLineSegment(sketch, "E1837", {"start": v(54.6, 84.37) * mm, "end": v(54.7, 84.4) * mm});
            skLineSegment(sketch, "E1838", {"start": v(54.7, 84.4) * mm, "end": v(54.76, 84.45) * mm});
            skLineSegment(sketch, "E1839", {"start": v(54.76, 84.45) * mm, "end": v(54.8, 84.5) * mm});
            skLineSegment(sketch, "E1840", {"start": v(54.8, 84.5) * mm, "end": v(54.81, 84.56) * mm});
            skLineSegment(sketch, "E1841", {"start": v(54.81, 84.56) * mm, "end": v(54.81, 88.26) * mm});
            skLineSegment(sketch, "E1842", {"start": v(59.1, 87.08) * mm, "end": v(59.26, 87.04) * mm});
            skLineSegment(sketch, "E1843", {"start": v(59.26, 87.04) * mm, "end": v(59.4, 86.98) * mm});
            skLineSegment(sketch, "E1844", {"start": v(59.4, 86.98) * mm, "end": v(59.55, 86.92) * mm});
            skLineSegment(sketch, "E1845", {"start": v(59.55, 86.92) * mm, "end": v(59.68, 86.86) * mm});
            skLineSegment(sketch, "E1846", {"start": v(59.68, 86.86) * mm, "end": v(59.8, 86.78) * mm});
            skLineSegment(sketch, "E1847", {"start": v(59.8, 86.78) * mm, "end": v(59.9, 86.7) * mm});
            skLineSegment(sketch, "E1848", {"start": v(59.9, 86.7) * mm, "end": v(60, 86.61) * mm});
            skLineSegment(sketch, "E1849", {"start": v(60, 86.61) * mm, "end": v(60.1, 86.52) * mm});
            skLineSegment(sketch, "E1850", {"start": v(60.1, 86.52) * mm, "end": v(60.17, 86.42) * mm});
            skLineSegment(sketch, "E1851", {"start": v(60.17, 86.42) * mm, "end": v(60.24, 86.31) * mm});
            skLineSegment(sketch, "E1852", {"start": v(60.24, 86.31) * mm, "end": v(60.3, 86.2) * mm});
            skLineSegment(sketch, "E1853", {"start": v(60.3, 86.2) * mm, "end": v(60.34, 86.08) * mm});
            skLineSegment(sketch, "E1854", {"start": v(60.34, 86.08) * mm, "end": v(60.38, 85.95) * mm});
            skLineSegment(sketch, "E1855", {"start": v(60.38, 85.95) * mm, "end": v(60.4, 85.81) * mm});
            skLineSegment(sketch, "E1856", {"start": v(60.4, 85.81) * mm, "end": v(60.42, 85.67) * mm});
            skLineSegment(sketch, "E1857", {"start": v(60.42, 85.67) * mm, "end": v(60.43, 85.52) * mm});
            skLineSegment(sketch, "E1858", {"start": v(60.43, 85.52) * mm, "end": v(60.41, 85.27) * mm});
            skLineSegment(sketch, "E1859", {"start": v(60.41, 85.27) * mm, "end": v(60.36, 85.04) * mm});
            skLineSegment(sketch, "E1860", {"start": v(60.36, 85.04) * mm, "end": v(60.29, 84.82) * mm});
            skLineSegment(sketch, "E1861", {"start": v(60.29, 84.82) * mm, "end": v(60.18, 84.61) * mm});
            skLineSegment(sketch, "E1862", {"start": v(60.18, 84.61) * mm, "end": v(60.05, 84.43) * mm});
            skLineSegment(sketch, "E1863", {"start": v(60.05, 84.43) * mm, "end": v(59.89, 84.27) * mm});
            skLineSegment(sketch, "E1864", {"start": v(59.89, 84.27) * mm, "end": v(59.7, 84.13) * mm});
            skLineSegment(sketch, "E1865", {"start": v(59.7, 84.13) * mm, "end": v(59.5, 84.01) * mm});
            skLineSegment(sketch, "E1866", {"start": v(59.5, 84.01) * mm, "end": v(59.29, 83.92) * mm});
            skLineSegment(sketch, "E1867", {"start": v(59.29, 83.92) * mm, "end": v(59.06, 83.85) * mm});
            skLineSegment(sketch, "E1868", {"start": v(59.06, 83.85) * mm, "end": v(58.83, 83.81) * mm});
            skLineSegment(sketch, "E1869", {"start": v(58.83, 83.81) * mm, "end": v(58.6, 83.8) * mm});
            skLineSegment(sketch, "E1870", {"start": v(58.6, 83.8) * mm, "end": v(58.43, 83.8) * mm});
            skLineSegment(sketch, "E1871", {"start": v(58.43, 83.8) * mm, "end": v(58.28, 83.82) * mm});
            skLineSegment(sketch, "E1872", {"start": v(58.28, 83.82) * mm, "end": v(58.14, 83.85) * mm});
            skLineSegment(sketch, "E1873", {"start": v(58.14, 83.85) * mm, "end": v(58, 83.9) * mm});
            skLineSegment(sketch, "E1874", {"start": v(58, 83.9) * mm, "end": v(57.88, 83.95) * mm});
            skLineSegment(sketch, "E1875", {"start": v(57.88, 83.95) * mm, "end": v(57.76, 84.02) * mm});
            skLineSegment(sketch, "E1876", {"start": v(57.76, 84.02) * mm, "end": v(57.65, 84.1) * mm});
            skLineSegment(sketch, "E1877", {"start": v(57.65, 84.1) * mm, "end": v(57.55, 84.2) * mm});
            skLineSegment(sketch, "E1878", {"start": v(57.55, 84.2) * mm, "end": v(57.46, 84.3) * mm});
            skLineSegment(sketch, "E1879", {"start": v(57.46, 84.3) * mm, "end": v(57.38, 84.4) * mm});
            skLineSegment(sketch, "E1880", {"start": v(57.38, 84.4) * mm, "end": v(57.31, 84.51) * mm});
            skLineSegment(sketch, "E1881", {"start": v(57.31, 84.51) * mm, "end": v(57.26, 84.63) * mm});
            skLineSegment(sketch, "E1882", {"start": v(57.26, 84.63) * mm, "end": v(57.21, 84.75) * mm});
            skLineSegment(sketch, "E1883", {"start": v(57.21, 84.75) * mm, "end": v(57.18, 84.87) * mm});
            skLineSegment(sketch, "E1884", {"start": v(57.18, 84.87) * mm, "end": v(57.16, 85) * mm});
            skLineSegment(sketch, "E1885", {"start": v(57.16, 85) * mm, "end": v(57.16, 85.13) * mm});
            skLineSegment(sketch, "E1886", {"start": v(57.16, 85.13) * mm, "end": v(57.17, 85.26) * mm});
            skLineSegment(sketch, "E1887", {"start": v(57.17, 85.26) * mm, "end": v(57.2, 85.38) * mm});
            skLineSegment(sketch, "E1888", {"start": v(57.2, 85.38) * mm, "end": v(57.24, 85.49) * mm});
            skLineSegment(sketch, "E1889", {"start": v(57.24, 85.49) * mm, "end": v(57.3, 85.59) * mm});
            skLineSegment(sketch, "E1890", {"start": v(57.3, 85.59) * mm, "end": v(57.37, 85.67) * mm});
            skLineSegment(sketch, "E1891", {"start": v(57.37, 85.67) * mm, "end": v(57.46, 85.73) * mm});
            skLineSegment(sketch, "E1892", {"start": v(57.46, 85.73) * mm, "end": v(57.57, 85.76) * mm});
            skLineSegment(sketch, "E1893", {"start": v(57.57, 85.76) * mm, "end": v(57.69, 85.77) * mm});
            skLineSegment(sketch, "E1894", {"start": v(57.69, 85.77) * mm, "end": v(57.8, 85.76) * mm});
            skLineSegment(sketch, "E1895", {"start": v(57.8, 85.76) * mm, "end": v(57.9, 85.73) * mm});
            skLineSegment(sketch, "E1896", {"start": v(57.9, 85.73) * mm, "end": v(58, 85.68) * mm});
            skLineSegment(sketch, "E1897", {"start": v(58, 85.68) * mm, "end": v(58.07, 85.6) * mm});
            skLineSegment(sketch, "E1898", {"start": v(58.07, 85.6) * mm, "end": v(58.12, 85.52) * mm});
            skLineSegment(sketch, "E1899", {"start": v(58.12, 85.52) * mm, "end": v(58.17, 85.42) * mm});
            skLineSegment(sketch, "E1900", {"start": v(58.17, 85.42) * mm, "end": v(58.2, 85.31) * mm});
            skLineSegment(sketch, "E1901", {"start": v(58.2, 85.31) * mm, "end": v(58.2, 85.2) * mm});
            skLineSegment(sketch, "E1902", {"start": v(58.2, 85.2) * mm, "end": v(58.19, 85.06) * mm});
            skLineSegment(sketch, "E1903", {"start": v(58.19, 85.06) * mm, "end": v(58.16, 84.86) * mm});
            skLineSegment(sketch, "E1904", {"start": v(58.16, 84.86) * mm, "end": v(58.14, 84.76) * mm});
            skLineSegment(sketch, "E1905", {"start": v(58.14, 84.76) * mm, "end": v(58.14, 84.67) * mm});
            skLineSegment(sketch, "E1906", {"start": v(58.14, 84.67) * mm, "end": v(58.14, 84.59) * mm});
            skLineSegment(sketch, "E1907", {"start": v(58.14, 84.59) * mm, "end": v(58.16, 84.52) * mm});
            skLineSegment(sketch, "E1908", {"start": v(58.16, 84.52) * mm, "end": v(58.2, 84.45) * mm});
            skLineSegment(sketch, "E1909", {"start": v(58.2, 84.45) * mm, "end": v(58.24, 84.4) * mm});
            skLineSegment(sketch, "E1910", {"start": v(58.24, 84.4) * mm, "end": v(58.3, 84.34) * mm});
            skLineSegment(sketch, "E1911", {"start": v(58.3, 84.34) * mm, "end": v(58.36, 84.3) * mm});
            skLineSegment(sketch, "E1912", {"start": v(58.36, 84.3) * mm, "end": v(58.43, 84.29) * mm});
            skLineSegment(sketch, "E1913", {"start": v(58.43, 84.29) * mm, "end": v(58.52, 84.28) * mm});
            skLineSegment(sketch, "E1914", {"start": v(58.52, 84.28) * mm, "end": v(58.62, 84.3) * mm});
            skLineSegment(sketch, "E1915", {"start": v(58.62, 84.3) * mm, "end": v(58.72, 84.33) * mm});
            skLineSegment(sketch, "E1916", {"start": v(58.72, 84.33) * mm, "end": v(58.8, 84.4) * mm});
            skLineSegment(sketch, "E1917", {"start": v(58.8, 84.4) * mm, "end": v(58.86, 84.48) * mm});
            skLineSegment(sketch, "E1918", {"start": v(58.86, 84.48) * mm, "end": v(58.91, 84.59) * mm});
            skLineSegment(sketch, "E1919", {"start": v(58.91, 84.59) * mm, "end": v(58.95, 84.73) * mm});
            skLineSegment(sketch, "E1920", {"start": v(58.95, 84.73) * mm, "end": v(58.97, 84.9) * mm});
            skLineSegment(sketch, "E1921", {"start": v(58.97, 84.9) * mm, "end": v(58.98, 85.1) * mm});
            skLineSegment(sketch, "E1922", {"start": v(58.98, 85.1) * mm, "end": v(58.97, 85.32) * mm});
            skLineSegment(sketch, "E1923", {"start": v(58.97, 85.32) * mm, "end": v(58.92, 86.24) * mm});
            skLineSegment(sketch, "E1924", {"start": v(58.92, 86.24) * mm, "end": v(58.9, 86.37) * mm});
            skLineSegment(sketch, "E1925", {"start": v(58.9, 86.37) * mm, "end": v(58.85, 86.48) * mm});
            skLineSegment(sketch, "E1926", {"start": v(58.85, 86.48) * mm, "end": v(58.8, 86.57) * mm});
            skLineSegment(sketch, "E1927", {"start": v(58.8, 86.57) * mm, "end": v(58.74, 86.64) * mm});
            skLineSegment(sketch, "E1928", {"start": v(58.74, 86.64) * mm, "end": v(58.68, 86.7) * mm});
            skLineSegment(sketch, "E1929", {"start": v(58.68, 86.7) * mm, "end": v(58.61, 86.74) * mm});
            skLineSegment(sketch, "E1930", {"start": v(58.61, 86.74) * mm, "end": v(58.55, 86.78) * mm});
            skLineSegment(sketch, "E1931", {"start": v(58.55, 86.78) * mm, "end": v(58.48, 86.8) * mm});
            skLineSegment(sketch, "E1932", {"start": v(58.48, 86.8) * mm, "end": v(58.3, 86.82) * mm});
            skLineSegment(sketch, "E1933", {"start": v(58.3, 86.82) * mm, "end": v(58.03, 86.82) * mm});
            skLineSegment(sketch, "E1934", {"start": v(58.03, 86.82) * mm, "end": v(57.92, 86.82) * mm});
            skLineSegment(sketch, "E1935", {"start": v(57.92, 86.82) * mm, "end": v(57.87, 86.83) * mm});
            skLineSegment(sketch, "E1936", {"start": v(57.87, 86.83) * mm, "end": v(57.84, 86.85) * mm});
            skLineSegment(sketch, "E1937", {"start": v(57.84, 86.85) * mm, "end": v(57.82, 86.88) * mm});
            skLineSegment(sketch, "E1938", {"start": v(57.82, 86.88) * mm, "end": v(57.8, 86.93) * mm});
            skLineSegment(sketch, "E1939", {"start": v(57.8, 86.93) * mm, "end": v(57.8, 87.1) * mm});
            skLineSegment(sketch, "E1940", {"start": v(57.8, 87.1) * mm, "end": v(57.8, 87.14) * mm});
            skLineSegment(sketch, "E1941", {"start": v(57.8, 87.14) * mm, "end": v(57.8, 87.22) * mm});
            skLineSegment(sketch, "E1942", {"start": v(57.8, 87.22) * mm, "end": v(57.84, 87.27) * mm});
            skLineSegment(sketch, "E1943", {"start": v(57.84, 87.27) * mm, "end": v(57.89, 87.3) * mm});
            skLineSegment(sketch, "E1944", {"start": v(57.89, 87.3) * mm, "end": v(57.96, 87.3) * mm});
            skLineSegment(sketch, "E1945", {"start": v(57.96, 87.3) * mm, "end": v(58.16, 87.31) * mm});
            skLineSegment(sketch, "E1946", {"start": v(58.16, 87.31) * mm, "end": v(58.33, 87.33) * mm});
            skLineSegment(sketch, "E1947", {"start": v(58.33, 87.33) * mm, "end": v(58.46, 87.35) * mm});
            skLineSegment(sketch, "E1948", {"start": v(58.46, 87.35) * mm, "end": v(58.57, 87.38) * mm});
            skLineSegment(sketch, "E1949", {"start": v(58.57, 87.38) * mm, "end": v(58.65, 87.42) * mm});
            skLineSegment(sketch, "E1950", {"start": v(58.65, 87.42) * mm, "end": v(58.72, 87.47) * mm});
            skLineSegment(sketch, "E1951", {"start": v(58.72, 87.47) * mm, "end": v(58.78, 87.53) * mm});
            skLineSegment(sketch, "E1952", {"start": v(58.78, 87.53) * mm, "end": v(58.82, 87.6) * mm});
            skLineSegment(sketch, "E1953", {"start": v(58.82, 87.6) * mm, "end": v(58.84, 87.7) * mm});
            skLineSegment(sketch, "E1954", {"start": v(58.84, 87.7) * mm, "end": v(58.86, 87.84) * mm});
            skLineSegment(sketch, "E1955", {"start": v(58.86, 87.84) * mm, "end": v(58.88, 88.03) * mm});
            skLineSegment(sketch, "E1956", {"start": v(58.88, 88.03) * mm, "end": v(58.88, 88.25) * mm});
            skLineSegment(sketch, "E1957", {"start": v(58.88, 88.25) * mm, "end": v(58.87, 88.58) * mm});
            skLineSegment(sketch, "E1958", {"start": v(58.87, 88.58) * mm, "end": v(58.86, 88.85) * mm});
            skLineSegment(sketch, "E1959", {"start": v(58.86, 88.85) * mm, "end": v(58.84, 89.05) * mm});
            skLineSegment(sketch, "E1960", {"start": v(58.84, 89.05) * mm, "end": v(58.8, 89.2) * mm});
            skLineSegment(sketch, "E1961", {"start": v(58.8, 89.2) * mm, "end": v(58.76, 89.3) * mm});
            skLineSegment(sketch, "E1962", {"start": v(58.76, 89.3) * mm, "end": v(58.7, 89.37) * mm});
            skLineSegment(sketch, "E1963", {"start": v(58.7, 89.37) * mm, "end": v(58.6, 89.42) * mm});
            skLineSegment(sketch, "E1964", {"start": v(58.6, 89.42) * mm, "end": v(58.5, 89.43) * mm});
            skLineSegment(sketch, "E1965", {"start": v(58.5, 89.43) * mm, "end": v(58.43, 89.43) * mm});
            skLineSegment(sketch, "E1966", {"start": v(58.43, 89.43) * mm, "end": v(58.37, 89.4) * mm});
            skLineSegment(sketch, "E1967", {"start": v(58.37, 89.4) * mm, "end": v(58.3, 89.38) * mm});
            skLineSegment(sketch, "E1968", {"start": v(58.3, 89.38) * mm, "end": v(58.25, 89.34) * mm});
            skLineSegment(sketch, "E1969", {"start": v(58.25, 89.34) * mm, "end": v(58.2, 89.29) * mm});
            skLineSegment(sketch, "E1970", {"start": v(58.2, 89.29) * mm, "end": v(58.17, 89.23) * mm});
            skLineSegment(sketch, "E1971", {"start": v(58.17, 89.23) * mm, "end": v(58.15, 89.17) * mm});
            skLineSegment(sketch, "E1972", {"start": v(58.15, 89.17) * mm, "end": v(58.15, 89.1) * mm});
            skLineSegment(sketch, "E1973", {"start": v(58.15, 89.1) * mm, "end": v(58.16, 88.98) * mm});
            skLineSegment(sketch, "E1974", {"start": v(58.16, 88.98) * mm, "end": v(58.18, 88.82) * mm});
            skLineSegment(sketch, "E1975", {"start": v(58.18, 88.82) * mm, "end": v(58.22, 88.6) * mm});
            skLineSegment(sketch, "E1976", {"start": v(58.22, 88.6) * mm, "end": v(58.23, 88.44) * mm});
            skLineSegment(sketch, "E1977", {"start": v(58.23, 88.44) * mm, "end": v(58.22, 88.33) * mm});
            skLineSegment(sketch, "E1978", {"start": v(58.22, 88.33) * mm, "end": v(58.2, 88.24) * mm});
            skLineSegment(sketch, "E1979", {"start": v(58.2, 88.24) * mm, "end": v(58.15, 88.16) * mm});
            skLineSegment(sketch, "E1980", {"start": v(58.15, 88.16) * mm, "end": v(58.08, 88.1) * mm});
            skLineSegment(sketch, "E1981", {"start": v(58.08, 88.1) * mm, "end": v(58, 88.04) * mm});
            skLineSegment(sketch, "E1982", {"start": v(58, 88.04) * mm, "end": v(57.93, 88) * mm});
            skLineSegment(sketch, "E1983", {"start": v(57.93, 88) * mm, "end": v(57.84, 87.98) * mm});
            skLineSegment(sketch, "E1984", {"start": v(57.84, 87.98) * mm, "end": v(57.74, 87.97) * mm});
            skLineSegment(sketch, "E1985", {"start": v(57.74, 87.97) * mm, "end": v(57.62, 87.98) * mm});
            skLineSegment(sketch, "E1986", {"start": v(57.62, 87.98) * mm, "end": v(57.52, 88.02) * mm});
            skLineSegment(sketch, "E1987", {"start": v(57.52, 88.02) * mm, "end": v(57.43, 88.08) * mm});
            skLineSegment(sketch, "E1988", {"start": v(57.43, 88.08) * mm, "end": v(57.35, 88.16) * mm});
            skLineSegment(sketch, "E1989", {"start": v(57.35, 88.16) * mm, "end": v(57.29, 88.27) * mm});
            skLineSegment(sketch, "E1990", {"start": v(57.29, 88.27) * mm, "end": v(57.25, 88.39) * mm});
            skLineSegment(sketch, "E1991", {"start": v(57.25, 88.39) * mm, "end": v(57.22, 88.51) * mm});
            skLineSegment(sketch, "E1992", {"start": v(57.22, 88.51) * mm, "end": v(57.21, 88.66) * mm});
            skLineSegment(sketch, "E1993", {"start": v(57.21, 88.66) * mm, "end": v(57.22, 88.78) * mm});
            skLineSegment(sketch, "E1994", {"start": v(57.22, 88.78) * mm, "end": v(57.24, 88.9) * mm});
            skLineSegment(sketch, "E1995", {"start": v(57.24, 88.9) * mm, "end": v(57.27, 89.02) * mm});
            skLineSegment(sketch, "E1996", {"start": v(57.27, 89.02) * mm, "end": v(57.3, 89.14) * mm});
            skLineSegment(sketch, "E1997", {"start": v(57.3, 89.14) * mm, "end": v(57.37, 89.25) * mm});
            skLineSegment(sketch, "E1998", {"start": v(57.37, 89.25) * mm, "end": v(57.43, 89.35) * mm});
            skLineSegment(sketch, "E1999", {"start": v(57.43, 89.35) * mm, "end": v(57.51, 89.46) * mm});
            skLineSegment(sketch, "E2000", {"start": v(57.51, 89.46) * mm, "end": v(57.6, 89.56) * mm});
            skLineSegment(sketch, "E2001", {"start": v(57.6, 89.56) * mm, "end": v(57.71, 89.65) * mm});
            skLineSegment(sketch, "E2002", {"start": v(57.71, 89.65) * mm, "end": v(57.82, 89.72) * mm});
            skLineSegment(sketch, "E2003", {"start": v(57.82, 89.72) * mm, "end": v(57.95, 89.8) * mm});
            skLineSegment(sketch, "E2004", {"start": v(57.95, 89.8) * mm, "end": v(58.08, 89.85) * mm});
            skLineSegment(sketch, "E2005", {"start": v(58.08, 89.85) * mm, "end": v(58.21, 89.89) * mm});
            skLineSegment(sketch, "E2006", {"start": v(58.21, 89.89) * mm, "end": v(58.36, 89.92) * mm});
            skLineSegment(sketch, "E2007", {"start": v(58.36, 89.92) * mm, "end": v(58.52, 89.94) * mm});
            skLineSegment(sketch, "E2008", {"start": v(58.52, 89.94) * mm, "end": v(58.68, 89.94) * mm});
            skLineSegment(sketch, "E2009", {"start": v(58.68, 89.94) * mm, "end": v(58.87, 89.93) * mm});
            skLineSegment(sketch, "E2010", {"start": v(58.87, 89.93) * mm, "end": v(59.05, 89.91) * mm});
            skLineSegment(sketch, "E2011", {"start": v(59.05, 89.91) * mm, "end": v(59.22, 89.87) * mm});
            skLineSegment(sketch, "E2012", {"start": v(59.22, 89.87) * mm, "end": v(59.37, 89.82) * mm});
            skLineSegment(sketch, "E2013", {"start": v(59.37, 89.82) * mm, "end": v(59.51, 89.76) * mm});
            skLineSegment(sketch, "E2014", {"start": v(59.51, 89.76) * mm, "end": v(59.64, 89.67) * mm});
            skLineSegment(sketch, "E2015", {"start": v(59.64, 89.67) * mm, "end": v(59.76, 89.58) * mm});
            skLineSegment(sketch, "E2016", {"start": v(59.76, 89.58) * mm, "end": v(59.87, 89.47) * mm});
            skLineSegment(sketch, "E2017", {"start": v(59.87, 89.47) * mm, "end": v(59.97, 89.35) * mm});
            skLineSegment(sketch, "E2018", {"start": v(59.97, 89.35) * mm, "end": v(60.05, 89.22) * mm});
            skLineSegment(sketch, "E2019", {"start": v(60.05, 89.22) * mm, "end": v(60.12, 89.1) * mm});
            skLineSegment(sketch, "E2020", {"start": v(60.12, 89.1) * mm, "end": v(60.18, 88.97) * mm});
            skLineSegment(sketch, "E2021", {"start": v(60.18, 88.97) * mm, "end": v(60.22, 88.83) * mm});
            skLineSegment(sketch, "E2022", {"start": v(60.22, 88.83) * mm, "end": v(60.26, 88.7) * mm});
            skLineSegment(sketch, "E2023", {"start": v(60.26, 88.7) * mm, "end": v(60.27, 88.56) * mm});
            skLineSegment(sketch, "E2024", {"start": v(60.27, 88.56) * mm, "end": v(60.28, 88.42) * mm});
            skLineSegment(sketch, "E2025", {"start": v(60.28, 88.42) * mm, "end": v(60.26, 88.2) * mm});
            skLineSegment(sketch, "E2026", {"start": v(60.26, 88.2) * mm, "end": v(60.24, 88.1) * mm});
            skLineSegment(sketch, "E2027", {"start": v(60.24, 88.1) * mm, "end": v(60.21, 88) * mm});
            skLineSegment(sketch, "E2028", {"start": v(60.21, 88) * mm, "end": v(60.17, 87.9) * mm});
            skLineSegment(sketch, "E2029", {"start": v(60.17, 87.9) * mm, "end": v(60.13, 87.8) * mm});
            skLineSegment(sketch, "E2030", {"start": v(60.13, 87.8) * mm, "end": v(60, 87.62) * mm});
            skLineSegment(sketch, "E2031", {"start": v(60, 87.62) * mm, "end": v(59.93, 87.54) * mm});
            skLineSegment(sketch, "E2032", {"start": v(59.93, 87.54) * mm, "end": v(59.85, 87.46) * mm});
            skLineSegment(sketch, "E2033", {"start": v(59.85, 87.46) * mm, "end": v(59.76, 87.38) * mm});
            skLineSegment(sketch, "E2034", {"start": v(59.76, 87.38) * mm, "end": v(59.67, 87.32) * mm});
            skLineSegment(sketch, "E2035", {"start": v(59.67, 87.32) * mm, "end": v(59.56, 87.26) * mm});
            skLineSegment(sketch, "E2036", {"start": v(59.56, 87.26) * mm, "end": v(59.45, 87.2) * mm});
            skLineSegment(sketch, "E2037", {"start": v(59.45, 87.2) * mm, "end": v(59.2, 87.12) * mm});
            skLineSegment(sketch, "E2038", {"start": v(59.2, 87.12) * mm, "end": v(59.1, 87.08) * mm});
            skLineSegment(sketch, "E2039", {"start": v(29.2, 76.9) * mm, "end": v(28.37, 77.49) * mm});
            skLineSegment(sketch, "E2040", {"start": v(28.37, 77.49) * mm, "end": v(27.26, 77.49) * mm});
            skLineSegment(sketch, "E2041", {"start": v(27.26, 77.49) * mm, "end": v(26.3, 77) * mm});
            skLineSegment(sketch, "E2042", {"start": v(26.3, 77) * mm, "end": v(25.83, 76.07) * mm});
            skLineSegment(sketch, "E2043", {"start": v(25.83, 76.07) * mm, "end": v(25.7, 74.76) * mm});
            skLineSegment(sketch, "E2044", {"start": v(25.7, 74.76) * mm, "end": v(25.85, 73.77) * mm});
            skLineSegment(sketch, "E2045", {"start": v(25.85, 73.77) * mm, "end": v(26.56, 72.87) * mm});
            skLineSegment(sketch, "E2046", {"start": v(26.56, 72.87) * mm, "end": v(27.57, 72.33) * mm});
            skLineSegment(sketch, "E2047", {"start": v(27.57, 72.33) * mm, "end": v(28.6, 72.22) * mm});
            skLineSegment(sketch, "E2048", {"start": v(28.6, 72.22) * mm, "end": v(28.9, 72.44) * mm});
            skLineSegment(sketch, "E2049", {"start": v(28.9, 72.44) * mm, "end": v(28.9, 73.38) * mm});
            skLineSegment(sketch, "E2050", {"start": v(28.9, 73.38) * mm, "end": v(28.7, 73.85) * mm});
            skLineSegment(sketch, "E2051", {"start": v(28.7, 73.85) * mm, "end": v(28.11, 74) * mm});
            skLineSegment(sketch, "E2052", {"start": v(28.11, 74) * mm, "end": v(28.23, 74.43) * mm});
            skLineSegment(sketch, "E2053", {"start": v(28.23, 74.43) * mm, "end": v(29.2, 74.29) * mm});
            skLineSegment(sketch, "E2054", {"start": v(29.2, 74.29) * mm, "end": v(30.24, 74.43) * mm});
            skLineSegment(sketch, "E2055", {"start": v(30.24, 74.43) * mm, "end": v(30.26, 74.1) * mm});
            skLineSegment(sketch, "E2056", {"start": v(30.26, 74.1) * mm, "end": v(29.74, 73.79) * mm});
            skLineSegment(sketch, "E2057", {"start": v(29.74, 73.79) * mm, "end": v(29.78, 72.85) * mm});
            skLineSegment(sketch, "E2058", {"start": v(29.78, 72.85) * mm, "end": v(30.13, 72.39) * mm});
            skLineSegment(sketch, "E2059", {"start": v(30.13, 72.39) * mm, "end": v(29.27, 71.97) * mm});
            skLineSegment(sketch, "E2060", {"start": v(29.27, 71.97) * mm, "end": v(28.44, 71.85) * mm});
            skLineSegment(sketch, "E2061", {"start": v(28.44, 71.85) * mm, "end": v(26.98, 71.85) * mm});
            skLineSegment(sketch, "E2062", {"start": v(26.98, 71.85) * mm, "end": v(25.7, 72.4) * mm});
            skLineSegment(sketch, "E2063", {"start": v(25.7, 72.4) * mm, "end": v(24.77, 73.53) * mm});
            skLineSegment(sketch, "E2064", {"start": v(24.77, 73.53) * mm, "end": v(24.61, 75.4) * mm});
            skLineSegment(sketch, "E2065", {"start": v(24.61, 75.4) * mm, "end": v(25.3, 76.78) * mm});
            skLineSegment(sketch, "E2066", {"start": v(25.3, 76.78) * mm, "end": v(26.61, 77.74) * mm});
            skLineSegment(sketch, "E2067", {"start": v(26.61, 77.74) * mm, "end": v(28.31, 77.9) * mm});
            skLineSegment(sketch, "E2068", {"start": v(28.31, 77.9) * mm, "end": v(29.94, 77.56) * mm});
            skLineSegment(sketch, "E2069", {"start": v(29.94, 77.56) * mm, "end": v(29.77, 76.8) * mm});
            skLineSegment(sketch, "E2070", {"start": v(29.77, 76.8) * mm, "end": v(29.83, 75.9) * mm});
            skLineSegment(sketch, "E2071", {"start": v(29.83, 75.9) * mm, "end": v(29.51, 75.94) * mm});
            skLineSegment(sketch, "E2072", {"start": v(29.51, 75.94) * mm, "end": v(29.2, 76.9) * mm});
            skLineSegment(sketch, "E2073", {"start": v(32.9, 77.45) * mm, "end": v(32.41, 77.43) * mm});
            skLineSegment(sketch, "E2074", {"start": v(32.41, 77.43) * mm, "end": v(32.41, 73.3) * mm});
            skLineSegment(sketch, "E2075", {"start": v(32.41, 73.3) * mm, "end": v(32.56, 72.72) * mm});
            skLineSegment(sketch, "E2076", {"start": v(32.56, 72.72) * mm, "end": v(33.2, 72.23) * mm});
            skLineSegment(sketch, "E2077", {"start": v(33.2, 72.23) * mm, "end": v(34.27, 72.38) * mm});
            skLineSegment(sketch, "E2078", {"start": v(34.27, 72.38) * mm, "end": v(35.03, 72.99) * mm});
            skLineSegment(sketch, "E2079", {"start": v(35.03, 72.99) * mm, "end": v(35.45, 73.92) * mm});
            skLineSegment(sketch, "E2080", {"start": v(35.45, 73.92) * mm, "end": v(35.45, 75.28) * mm});
            skLineSegment(sketch, "E2081", {"start": v(35.45, 75.28) * mm, "end": v(35.01, 76.43) * mm});
            skLineSegment(sketch, "E2082", {"start": v(35.01, 76.43) * mm, "end": v(34.03, 77.13) * mm});
            skLineSegment(sketch, "E2083", {"start": v(34.03, 77.13) * mm, "end": v(32.9, 77.45) * mm});
            skLineSegment(sketch, "E2084", {"start": v(31.83, 77.74) * mm, "end": v(32.65, 77.87) * mm});
            skLineSegment(sketch, "E2085", {"start": v(32.65, 77.87) * mm, "end": v(33.57, 77.87) * mm});
            skLineSegment(sketch, "E2086", {"start": v(33.57, 77.87) * mm, "end": v(34.91, 77.47) * mm});
            skLineSegment(sketch, "E2087", {"start": v(34.91, 77.47) * mm, "end": v(36.16, 76.48) * mm});
            skLineSegment(sketch, "E2088", {"start": v(36.16, 76.48) * mm, "end": v(36.61, 75.1) * mm});
            skLineSegment(sketch, "E2089", {"start": v(36.61, 75.1) * mm, "end": v(36.41, 73.59) * mm});
            skLineSegment(sketch, "E2090", {"start": v(36.41, 73.59) * mm, "end": v(35.37, 72.5) * mm});
            skLineSegment(sketch, "E2091", {"start": v(35.37, 72.5) * mm, "end": v(34.18, 71.96) * mm});
            skLineSegment(sketch, "E2092", {"start": v(34.18, 71.96) * mm, "end": v(32.98, 71.87) * mm});
            skLineSegment(sketch, "E2093", {"start": v(32.98, 71.87) * mm, "end": v(32.01, 71.93) * mm});
            skLineSegment(sketch, "E2094", {"start": v(32.01, 71.93) * mm, "end": v(30.81, 71.83) * mm});
            skLineSegment(sketch, "E2095", {"start": v(30.81, 71.83) * mm, "end": v(30.76, 72.18) * mm});
            skLineSegment(sketch, "E2096", {"start": v(30.76, 72.18) * mm, "end": v(31.28, 72.36) * mm});
            skLineSegment(sketch, "E2097", {"start": v(31.28, 72.36) * mm, "end": v(31.6, 72.9) * mm});
            skLineSegment(sketch, "E2098", {"start": v(31.6, 72.9) * mm, "end": v(31.6, 76.83) * mm});
            skLineSegment(sketch, "E2099", {"start": v(31.6, 76.83) * mm, "end": v(31.3, 77.39) * mm});
            skLineSegment(sketch, "E2100", {"start": v(31.3, 77.39) * mm, "end": v(30.85, 77.39) * mm});
            skLineSegment(sketch, "E2101", {"start": v(30.85, 77.39) * mm, "end": v(30.84, 77.77) * mm});
            skLineSegment(sketch, "E2102", {"start": v(30.84, 77.77) * mm, "end": v(31.83, 77.74) * mm});
            skLineSegment(sketch, "E2103", {"start": v(45, 50.87) * mm, "end": v(49.2, 51.24) * mm});
            skLineSegment(sketch, "E2104", {"start": v(49.2, 51.24) * mm, "end": v(45.09, 44.17) * mm});
            skLineSegment(sketch, "E2105", {"start": v(45.09, 44.17) * mm, "end": v(42.27, 38.2) * mm});
            skLineSegment(sketch, "E2106", {"start": v(42.27, 38.2) * mm, "end": v(40.32, 38.1) * mm});
            skLineSegment(sketch, "E2107", {"start": v(40.32, 38.1) * mm, "end": v(46.88, 49.2) * mm});
            skLineSegment(sketch, "E2108", {"start": v(46.88, 49.2) * mm, "end": v(46.76, 49.13) * mm});
            skLineSegment(sketch, "E2109", {"start": v(46.76, 49.13) * mm, "end": v(42.37, 49.23) * mm});
            skLineSegment(sketch, "E2110", {"start": v(42.37, 49.23) * mm, "end": v(41.13, 48.4) * mm});
            skLineSegment(sketch, "E2111", {"start": v(41.13, 48.4) * mm, "end": v(40.76, 47.36) * mm});
            skLineSegment(sketch, "E2112", {"start": v(40.76, 47.36) * mm, "end": v(40, 47.54) * mm});
            skLineSegment(sketch, "E2113", {"start": v(40, 47.54) * mm, "end": v(40.84, 51.06) * mm});
            skLineSegment(sketch, "E2114", {"start": v(40.84, 51.06) * mm, "end": v(45, 50.87) * mm});
            skLineSegment(sketch, "E2115", {"start": v(53.6, 47.87) * mm, "end": v(53.34, 44.56) * mm});
            skLineSegment(sketch, "E2116", {"start": v(53.34, 44.56) * mm, "end": v(56.12, 44.4) * mm});
            skLineSegment(sketch, "E2117", {"start": v(56.12, 44.4) * mm, "end": v(55.9, 43.05) * mm});
            skLineSegment(sketch, "E2118", {"start": v(55.9, 43.05) * mm, "end": v(53.38, 42.95) * mm});
            skLineSegment(sketch, "E2119", {"start": v(53.38, 42.95) * mm, "end": v(53.7, 39.74) * mm});
            skLineSegment(sketch, "E2120", {"start": v(53.7, 39.74) * mm, "end": v(52.08, 39.91) * mm});
            skLineSegment(sketch, "E2121", {"start": v(52.08, 39.91) * mm, "end": v(52.18, 42.89) * mm});
            skLineSegment(sketch, "E2122", {"start": v(52.18, 42.89) * mm, "end": v(49.38, 42.8) * mm});
            skLineSegment(sketch, "E2123", {"start": v(49.38, 42.8) * mm, "end": v(49.44, 44.7) * mm});
            skLineSegment(sketch, "E2124", {"start": v(49.44, 44.7) * mm, "end": v(52.24, 44.44) * mm});
            skLineSegment(sketch, "E2125", {"start": v(52.24, 44.44) * mm, "end": v(52.24, 47.75) * mm});
            skLineSegment(sketch, "E2126", {"start": v(52.24, 47.75) * mm, "end": v(53.6, 47.87) * mm});
            skLineSegment(sketch, "E2127", {"start": v(127.01, 45.59) * mm, "end": v(127.42, 45.88) * mm});
            skLineSegment(sketch, "E2128", {"start": v(127.42, 45.88) * mm, "end": v(127.92, 47.44) * mm});
            skLineSegment(sketch, "E2129", {"start": v(127.92, 47.44) * mm, "end": v(128.11, 49) * mm});
            skLineSegment(sketch, "E2130", {"start": v(128.11, 49) * mm, "end": v(127.44, 50.06) * mm});
            skLineSegment(sketch, "E2131", {"start": v(127.44, 50.06) * mm, "end": v(126.52, 50.55) * mm});
            skLineSegment(sketch, "E2132", {"start": v(126.52, 50.55) * mm, "end": v(125.2, 50.22) * mm});
            skLineSegment(sketch, "E2133", {"start": v(125.2, 50.22) * mm, "end": v(124.53, 49.5) * mm});
            skLineSegment(sketch, "E2134", {"start": v(124.53, 49.5) * mm, "end": v(124.5, 48.23) * mm});
            skLineSegment(sketch, "E2135", {"start": v(124.5, 48.23) * mm, "end": v(125.26, 46.73) * mm});
            skLineSegment(sketch, "E2136", {"start": v(125.26, 46.73) * mm, "end": v(126.42, 45.96) * mm});
            skLineSegment(sketch, "E2137", {"start": v(126.42, 45.96) * mm, "end": v(127.01, 45.59) * mm});
            skLineSegment(sketch, "E2138", {"start": v(125.8, 44.35) * mm, "end": v(125.16, 43.87) * mm});
            skLineSegment(sketch, "E2139", {"start": v(125.16, 43.87) * mm, "end": v(124.47, 42.18) * mm});
            skLineSegment(sketch, "E2140", {"start": v(124.47, 42.18) * mm, "end": v(124.35, 40.45) * mm});
            skLineSegment(sketch, "E2141", {"start": v(124.35, 40.45) * mm, "end": v(124.73, 39.4) * mm});
            skLineSegment(sketch, "E2142", {"start": v(124.73, 39.4) * mm, "end": v(125.85, 38.87) * mm});
            skLineSegment(sketch, "E2143", {"start": v(125.85, 38.87) * mm, "end": v(127.19, 38.83) * mm});
            skLineSegment(sketch, "E2144", {"start": v(127.19, 38.83) * mm, "end": v(128.4, 39.78) * mm});
            skLineSegment(sketch, "E2145", {"start": v(128.4, 39.78) * mm, "end": v(128.53, 41.41) * mm});
            skLineSegment(sketch, "E2146", {"start": v(128.53, 41.41) * mm, "end": v(127.86, 42.79) * mm});
            skLineSegment(sketch, "E2147", {"start": v(127.86, 42.79) * mm, "end": v(126.95, 43.72) * mm});
            skLineSegment(sketch, "E2148", {"start": v(126.95, 43.72) * mm, "end": v(125.8, 44.35) * mm});
            skLineSegment(sketch, "E2149", {"start": v(124.08, 44.17) * mm, "end": v(125.1, 44.8) * mm});
            skLineSegment(sketch, "E2150", {"start": v(125.1, 44.8) * mm, "end": v(123.6, 45.92) * mm});
            skLineSegment(sketch, "E2151", {"start": v(123.6, 45.92) * mm, "end": v(122.76, 47.87) * mm});
            skLineSegment(sketch, "E2152", {"start": v(122.76, 47.87) * mm, "end": v(123.3, 49.96) * mm});
            skLineSegment(sketch, "E2153", {"start": v(123.3, 49.96) * mm, "end": v(125.22, 51.06) * mm});
            skLineSegment(sketch, "E2154", {"start": v(125.22, 51.06) * mm, "end": v(127.33, 51.3) * mm});
            skLineSegment(sketch, "E2155", {"start": v(127.33, 51.3) * mm, "end": v(129.3, 50.45) * mm});
            skLineSegment(sketch, "E2156", {"start": v(129.3, 50.45) * mm, "end": v(130, 48.64) * mm});
            skLineSegment(sketch, "E2157", {"start": v(130, 48.64) * mm, "end": v(129.7, 46.95) * mm});
            skLineSegment(sketch, "E2158", {"start": v(129.7, 46.95) * mm, "end": v(128.76, 45.92) * mm});
            skLineSegment(sketch, "E2159", {"start": v(128.76, 45.92) * mm, "end": v(127.78, 45.27) * mm});
            skLineSegment(sketch, "E2160", {"start": v(127.78, 45.27) * mm, "end": v(129.08, 44.15) * mm});
            skLineSegment(sketch, "E2161", {"start": v(129.08, 44.15) * mm, "end": v(130.28, 42.12) * mm});
            skLineSegment(sketch, "E2162", {"start": v(130.28, 42.12) * mm, "end": v(130.16, 40.17) * mm});
            skLineSegment(sketch, "E2163", {"start": v(130.16, 40.17) * mm, "end": v(128.86, 38.61) * mm});
            skLineSegment(sketch, "E2164", {"start": v(128.86, 38.61) * mm, "end": v(126.93, 38.02) * mm});
            skLineSegment(sketch, "E2165", {"start": v(126.93, 38.02) * mm, "end": v(125, 38.12) * mm});
            skLineSegment(sketch, "E2166", {"start": v(125, 38.12) * mm, "end": v(123.35, 39) * mm});
            skLineSegment(sketch, "E2167", {"start": v(123.35, 39) * mm, "end": v(122.48, 40.66) * mm});
            skLineSegment(sketch, "E2168", {"start": v(122.48, 40.66) * mm, "end": v(122.76, 42.79) * mm});
            skLineSegment(sketch, "E2169", {"start": v(122.76, 42.79) * mm, "end": v(124.08, 44.17) * mm});
            skLineSegment(sketch, "E2170", {"start": v(135.82, 47.87) * mm, "end": v(135.56, 44.56) * mm});
            skLineSegment(sketch, "E2171", {"start": v(135.56, 44.56) * mm, "end": v(138.34, 44.4) * mm});
            skLineSegment(sketch, "E2172", {"start": v(138.34, 44.4) * mm, "end": v(138.12, 43.05) * mm});
            skLineSegment(sketch, "E2173", {"start": v(138.12, 43.05) * mm, "end": v(135.6, 42.95) * mm});
            skLineSegment(sketch, "E2174", {"start": v(135.6, 42.95) * mm, "end": v(135.91, 39.74) * mm});
            skLineSegment(sketch, "E2175", {"start": v(135.91, 39.74) * mm, "end": v(134.3, 39.91) * mm});
            skLineSegment(sketch, "E2176", {"start": v(134.3, 39.91) * mm, "end": v(134.4, 42.89) * mm});
            skLineSegment(sketch, "E2177", {"start": v(134.4, 42.89) * mm, "end": v(131.6, 42.8) * mm});
            skLineSegment(sketch, "E2178", {"start": v(131.6, 42.8) * mm, "end": v(131.66, 44.7) * mm});
            skLineSegment(sketch, "E2179", {"start": v(131.66, 44.7) * mm, "end": v(134.46, 44.44) * mm});
            skLineSegment(sketch, "E2180", {"start": v(134.46, 44.44) * mm, "end": v(134.46, 47.75) * mm});
            skLineSegment(sketch, "E2181", {"start": v(134.46, 47.75) * mm, "end": v(135.82, 47.87) * mm});
            skLineSegment(sketch, "E2182", {"start": v(207.2, 46.08) * mm, "end": v(207.87, 44.8) * mm});
            skLineSegment(sketch, "E2183", {"start": v(207.87, 44.8) * mm, "end": v(209.13, 44) * mm});
            skLineSegment(sketch, "E2184", {"start": v(209.13, 44) * mm, "end": v(210.6, 44.17) * mm});
            skLineSegment(sketch, "E2185", {"start": v(210.6, 44.17) * mm, "end": v(211.46, 44.84) * mm});
            skLineSegment(sketch, "E2186", {"start": v(211.46, 44.84) * mm, "end": v(211.56, 47.4) * mm});
            skLineSegment(sketch, "E2187", {"start": v(211.56, 47.4) * mm, "end": v(211.32, 49.05) * mm});
            skLineSegment(sketch, "E2188", {"start": v(211.32, 49.05) * mm, "end": v(210.65, 50.04) * mm});
            skLineSegment(sketch, "E2189", {"start": v(210.65, 50.04) * mm, "end": v(209.57, 50.5) * mm});
            skLineSegment(sketch, "E2190", {"start": v(209.57, 50.5) * mm, "end": v(208.3, 50.3) * mm});
            skLineSegment(sketch, "E2191", {"start": v(208.3, 50.3) * mm, "end": v(207.36, 49.35) * mm});
            skLineSegment(sketch, "E2192", {"start": v(207.36, 49.35) * mm, "end": v(207, 47.85) * mm});
            skLineSegment(sketch, "E2193", {"start": v(207, 47.85) * mm, "end": v(207.2, 46.08) * mm});
            skLineSegment(sketch, "E2194", {"start": v(208.33, 40) * mm, "end": v(210.4, 42) * mm});
            skLineSegment(sketch, "E2195", {"start": v(210.4, 42) * mm, "end": v(211.03, 43.56) * mm});
            skLineSegment(sketch, "E2196", {"start": v(211.03, 43.56) * mm, "end": v(210.57, 43.28) * mm});
            skLineSegment(sketch, "E2197", {"start": v(210.57, 43.28) * mm, "end": v(208.25, 42.93) * mm});
            skLineSegment(sketch, "E2198", {"start": v(208.25, 42.93) * mm, "end": v(206.53, 43.6) * mm});
            skLineSegment(sketch, "E2199", {"start": v(206.53, 43.6) * mm, "end": v(205.45, 45.05) * mm});
            skLineSegment(sketch, "E2200", {"start": v(205.45, 45.05) * mm, "end": v(205.1, 47.42) * mm});
            skLineSegment(sketch, "E2201", {"start": v(205.1, 47.42) * mm, "end": v(206.14, 49.7) * mm});
            skLineSegment(sketch, "E2202", {"start": v(206.14, 49.7) * mm, "end": v(207.87, 51.04) * mm});
            skLineSegment(sketch, "E2203", {"start": v(207.87, 51.04) * mm, "end": v(210.36, 51.36) * mm});
            skLineSegment(sketch, "E2204", {"start": v(210.36, 51.36) * mm, "end": v(212.36, 50.14) * mm});
            skLineSegment(sketch, "E2205", {"start": v(212.36, 50.14) * mm, "end": v(213.53, 47.65) * mm});
            skLineSegment(sketch, "E2206", {"start": v(213.53, 47.65) * mm, "end": v(213.39, 44.29) * mm});
            skLineSegment(sketch, "E2207", {"start": v(213.39, 44.29) * mm, "end": v(211.81, 41.33) * mm});
            skLineSegment(sketch, "E2208", {"start": v(211.81, 41.33) * mm, "end": v(208.9, 38.93) * mm});
            skLineSegment(sketch, "E2209", {"start": v(208.9, 38.93) * mm, "end": v(206.26, 37.8) * mm});
            skLineSegment(sketch, "E2210", {"start": v(206.26, 37.8) * mm, "end": v(205.85, 38.34) * mm});
            skLineSegment(sketch, "E2211", {"start": v(205.85, 38.34) * mm, "end": v(208.33, 40) * mm});
            skLineSegment(sketch, "E2212", {"start": v(219.04, 47.87) * mm, "end": v(218.79, 44.56) * mm});
            skLineSegment(sketch, "E2213", {"start": v(218.79, 44.56) * mm, "end": v(221.56, 44.4) * mm});
            skLineSegment(sketch, "E2214", {"start": v(221.56, 44.4) * mm, "end": v(221.35, 43.05) * mm});
            skLineSegment(sketch, "E2215", {"start": v(221.35, 43.05) * mm, "end": v(218.83, 42.95) * mm});
            skLineSegment(sketch, "E2216", {"start": v(218.83, 42.95) * mm, "end": v(219.14, 39.74) * mm});
            skLineSegment(sketch, "E2217", {"start": v(219.14, 39.74) * mm, "end": v(217.53, 39.91) * mm});
            skLineSegment(sketch, "E2218", {"start": v(217.53, 39.91) * mm, "end": v(217.62, 42.89) * mm});
            skLineSegment(sketch, "E2219", {"start": v(217.62, 42.89) * mm, "end": v(214.83, 42.8) * mm});
            skLineSegment(sketch, "E2220", {"start": v(214.83, 42.8) * mm, "end": v(214.89, 44.7) * mm});
            skLineSegment(sketch, "E2221", {"start": v(214.89, 44.7) * mm, "end": v(217.68, 44.44) * mm});
            skLineSegment(sketch, "E2222", {"start": v(217.68, 44.44) * mm, "end": v(217.68, 47.75) * mm});
            skLineSegment(sketch, "E2223", {"start": v(217.68, 47.75) * mm, "end": v(219.04, 47.87) * mm});
            skLineSegment(sketch, "E2224", {"start": v(45.3, 63.82) * mm, "end": v(44.16, 62) * mm});
            skLineSegment(sketch, "E2225", {"start": v(44.16, 62) * mm, "end": v(45.3, 62) * mm});
            skLineSegment(sketch, "E2226", {"start": v(45.3, 62) * mm, "end": v(45.3, 63.82) * mm});
            skLineSegment(sketch, "E2227", {"start": v(26.55, 90.38) * mm, "end": v(27.74, 90.16) * mm});
            skLineSegment(sketch, "E2228", {"start": v(27.74, 90.16) * mm, "end": v(28.88, 90.29) * mm});
            skLineSegment(sketch, "E2229", {"start": v(28.88, 90.29) * mm, "end": v(28.75, 84.18) * mm});
            skLineSegment(sketch, "E2230", {"start": v(28.75, 84.18) * mm, "end": v(29.27, 83.48) * mm});
            skLineSegment(sketch, "E2231", {"start": v(29.27, 83.48) * mm, "end": v(30.09, 83.34) * mm});
            skLineSegment(sketch, "E2232", {"start": v(30.09, 83.34) * mm, "end": v(30.03, 82.87) * mm});
            skLineSegment(sketch, "E2233", {"start": v(30.03, 82.87) * mm, "end": v(28.34, 83) * mm});
            skLineSegment(sketch, "E2234", {"start": v(28.34, 83) * mm, "end": v(26.75, 82.88) * mm});
            skLineSegment(sketch, "E2235", {"start": v(26.75, 82.88) * mm, "end": v(26.53, 83.4) * mm});
            skLineSegment(sketch, "E2236", {"start": v(26.53, 83.4) * mm, "end": v(27.4, 83.45) * mm});
            skLineSegment(sketch, "E2237", {"start": v(27.4, 83.45) * mm, "end": v(27.74, 84.1) * mm});
            skLineSegment(sketch, "E2238", {"start": v(27.74, 84.1) * mm, "end": v(27.74, 89.28) * mm});
            skLineSegment(sketch, "E2239", {"start": v(27.74, 89.28) * mm, "end": v(27.21, 89.79) * mm});
            skLineSegment(sketch, "E2240", {"start": v(27.21, 89.79) * mm, "end": v(26.5, 89.79) * mm});
            skLineSegment(sketch, "E2241", {"start": v(26.5, 89.79) * mm, "end": v(26.55, 90.38) * mm});
            skLineSegment(sketch, "E2242", {"start": v(33.62, 90.26) * mm, "end": v(33.99, 90.53) * mm});
            skLineSegment(sketch, "E2243", {"start": v(33.99, 90.53) * mm, "end": v(34.16, 90.97) * mm});
            skLineSegment(sketch, "E2244", {"start": v(34.16, 90.97) * mm, "end": v(34.5, 90.73) * mm});
            skLineSegment(sketch, "E2245", {"start": v(34.5, 90.73) * mm, "end": v(34.1, 89.09) * mm});
            skLineSegment(sketch, "E2246", {"start": v(34.1, 89.09) * mm, "end": v(31.55, 89.21) * mm});
            skLineSegment(sketch, "E2247", {"start": v(31.55, 89.21) * mm, "end": v(31.34, 87.52) * mm});
            skLineSegment(sketch, "E2248", {"start": v(31.34, 87.52) * mm, "end": v(32.3, 87.82) * mm});
            skLineSegment(sketch, "E2249", {"start": v(32.3, 87.82) * mm, "end": v(33.85, 87.3) * mm});
            skLineSegment(sketch, "E2250", {"start": v(33.85, 87.3) * mm, "end": v(34.71, 86.1) * mm});
            skLineSegment(sketch, "E2251", {"start": v(34.71, 86.1) * mm, "end": v(34.67, 84.65) * mm});
            skLineSegment(sketch, "E2252", {"start": v(34.67, 84.65) * mm, "end": v(33.86, 83.31) * mm});
            skLineSegment(sketch, "E2253", {"start": v(33.86, 83.31) * mm, "end": v(32.43, 82.77) * mm});
            skLineSegment(sketch, "E2254", {"start": v(32.43, 82.77) * mm, "end": v(31.11, 83.03) * mm});
            skLineSegment(sketch, "E2255", {"start": v(31.11, 83.03) * mm, "end": v(30.43, 83.84) * mm});
            skLineSegment(sketch, "E2256", {"start": v(30.43, 83.84) * mm, "end": v(30.35, 84.24) * mm});
            skLineSegment(sketch, "E2257", {"start": v(30.35, 84.24) * mm, "end": v(31.14, 84.97) * mm});
            skLineSegment(sketch, "E2258", {"start": v(31.14, 84.97) * mm, "end": v(31.85, 84.14) * mm});
            skLineSegment(sketch, "E2259", {"start": v(31.85, 84.14) * mm, "end": v(31.59, 83.88) * mm});
            skLineSegment(sketch, "E2260", {"start": v(31.59, 83.88) * mm, "end": v(32.1, 83.36) * mm});
            skLineSegment(sketch, "E2261", {"start": v(32.1, 83.36) * mm, "end": v(32.68, 83.32) * mm});
            skLineSegment(sketch, "E2262", {"start": v(32.68, 83.32) * mm, "end": v(33.45, 83.94) * mm});
            skLineSegment(sketch, "E2263", {"start": v(33.45, 83.94) * mm, "end": v(33.67, 84.97) * mm});
            skLineSegment(sketch, "E2264", {"start": v(33.67, 84.97) * mm, "end": v(33.37, 86.28) * mm});
            skLineSegment(sketch, "E2265", {"start": v(33.37, 86.28) * mm, "end": v(32.49, 86.85) * mm});
            skLineSegment(sketch, "E2266", {"start": v(32.49, 86.85) * mm, "end": v(31.53, 86.7) * mm});
            skLineSegment(sketch, "E2267", {"start": v(31.53, 86.7) * mm, "end": v(30.94, 86.24) * mm});
            skLineSegment(sketch, "E2268", {"start": v(30.94, 86.24) * mm, "end": v(30.58, 86.43) * mm});
            skLineSegment(sketch, "E2269", {"start": v(30.58, 86.43) * mm, "end": v(30.95, 88.38) * mm});
            skLineSegment(sketch, "E2270", {"start": v(30.95, 88.38) * mm, "end": v(31.03, 90.26) * mm});
            skLineSegment(sketch, "E2271", {"start": v(31.03, 90.26) * mm, "end": v(33.62, 90.26) * mm});
            skArc(sketch, "E2272", {"start": v(17.28, 68.87) * mm, "mid": v(13.03, 67.11) * mm, "end": v(11.28, 62.87) * mm});
            skArc(sketch, "E2273", {"start": v(11.28, 62.87) * mm, "mid": v(13.03, 58.63) * mm, "end": v(17.28, 56.87) * mm});
            skArc(sketch, "E2274", {"start": v(17.28, 56.87) * mm, "mid": v(21.52, 58.63) * mm, "end": v(23.28, 62.87) * mm});
            skArc(sketch, "E2275", {"start": v(23.28, 62.87) * mm, "mid": v(21.52, 67.11) * mm, "end": v(17.28, 68.87) * mm});
            skArc(sketch, "E2276", {"start": v(30.61, 92.87) * mm, "mid": v(26.37, 91.11) * mm, "end": v(24.61, 86.87) * mm});
            skArc(sketch, "E2277", {"start": v(24.61, 86.87) * mm, "mid": v(26.37, 82.63) * mm, "end": v(30.61, 80.87) * mm});
            skArc(sketch, "E2278", {"start": v(30.61, 80.87) * mm, "mid": v(34.85, 82.63) * mm, "end": v(36.61, 86.87) * mm});
            skArc(sketch, "E2279", {"start": v(36.61, 86.87) * mm, "mid": v(34.85, 91.11) * mm, "end": v(30.61, 92.87) * mm});
            skArc(sketch, "E2280", {"start": v(57.28, 92.87) * mm, "mid": v(53.03, 91.11) * mm, "end": v(51.28, 86.87) * mm});
            skArc(sketch, "E2281", {"start": v(51.28, 86.87) * mm, "mid": v(53.03, 82.63) * mm, "end": v(57.28, 80.87) * mm});
            skArc(sketch, "E2282", {"start": v(57.28, 80.87) * mm, "mid": v(61.52, 82.63) * mm, "end": v(63.28, 86.87) * mm});
            skArc(sketch, "E2283", {"start": v(63.28, 86.87) * mm, "mid": v(61.52, 91.11) * mm, "end": v(57.28, 92.87) * mm});
            skArc(sketch, "E2284", {"start": v(43.94, 68.87) * mm, "mid": v(39.7, 67.11) * mm, "end": v(37.94, 62.87) * mm});
            skArc(sketch, "E2285", {"start": v(37.94, 62.87) * mm, "mid": v(39.7, 58.63) * mm, "end": v(43.94, 56.87) * mm});
            skArc(sketch, "E2286", {"start": v(43.94, 56.87) * mm, "mid": v(48.19, 58.63) * mm, "end": v(49.94, 62.87) * mm});
            skArc(sketch, "E2287", {"start": v(49.94, 62.87) * mm, "mid": v(48.19, 67.11) * mm, "end": v(43.94, 68.87) * mm});
            skArc(sketch, "E2288", {"start": v(70.61, 68.87) * mm, "mid": v(66.37, 67.11) * mm, "end": v(64.61, 62.87) * mm});
            skArc(sketch, "E2289", {"start": v(64.61, 62.87) * mm, "mid": v(66.37, 58.63) * mm, "end": v(70.61, 56.87) * mm});
            skArc(sketch, "E2290", {"start": v(70.61, 56.87) * mm, "mid": v(74.85, 58.63) * mm, "end": v(76.61, 62.87) * mm});
            skArc(sketch, "E2291", {"start": v(76.61, 62.87) * mm, "mid": v(74.85, 67.11) * mm, "end": v(70.61, 68.87) * mm});
            skArc(sketch, "E2292", {"start": v(83.94, 92.87) * mm, "mid": v(79.7, 91.11) * mm, "end": v(77.94, 86.87) * mm});
            skArc(sketch, "E2293", {"start": v(77.94, 86.87) * mm, "mid": v(79.7, 82.63) * mm, "end": v(83.94, 80.87) * mm});
            skArc(sketch, "E2294", {"start": v(83.94, 80.87) * mm, "mid": v(88.19, 82.63) * mm, "end": v(89.94, 86.87) * mm});
            skArc(sketch, "E2295", {"start": v(89.94, 86.87) * mm, "mid": v(88.19, 91.11) * mm, "end": v(83.94, 92.87) * mm});
            skArc(sketch, "E2296", {"start": v(103.94, 68.87) * mm, "mid": v(99.7, 67.11) * mm, "end": v(97.94, 62.87) * mm});
            skArc(sketch, "E2297", {"start": v(97.94, 62.87) * mm, "mid": v(99.7, 58.63) * mm, "end": v(103.94, 56.87) * mm});
            skArc(sketch, "E2298", {"start": v(103.94, 56.87) * mm, "mid": v(108.19, 58.63) * mm, "end": v(109.94, 62.87) * mm});
            skArc(sketch, "E2299", {"start": v(109.94, 62.87) * mm, "mid": v(108.19, 67.11) * mm, "end": v(103.94, 68.87) * mm});
            skArc(sketch, "E2300", {"start": v(117.28, 92.87) * mm, "mid": v(113.03, 91.11) * mm, "end": v(111.28, 86.87) * mm});
            skArc(sketch, "E2301", {"start": v(111.28, 86.87) * mm, "mid": v(113.03, 82.63) * mm, "end": v(117.28, 80.87) * mm});
            skArc(sketch, "E2302", {"start": v(117.28, 80.87) * mm, "mid": v(121.52, 82.63) * mm, "end": v(123.28, 86.87) * mm});
            skArc(sketch, "E2303", {"start": v(123.28, 86.87) * mm, "mid": v(121.52, 91.11) * mm, "end": v(117.28, 92.87) * mm});
            skArc(sketch, "E2304", {"start": v(130.61, 68.87) * mm, "mid": v(126.37, 67.11) * mm, "end": v(124.61, 62.87) * mm});
            skArc(sketch, "E2305", {"start": v(124.61, 62.87) * mm, "mid": v(126.37, 58.63) * mm, "end": v(130.61, 56.87) * mm});
            skArc(sketch, "E2306", {"start": v(130.61, 56.87) * mm, "mid": v(134.85, 58.63) * mm, "end": v(136.61, 62.87) * mm});
            skArc(sketch, "E2307", {"start": v(136.61, 62.87) * mm, "mid": v(134.85, 67.11) * mm, "end": v(130.61, 68.87) * mm});
            skArc(sketch, "E2308", {"start": v(143.94, 92.87) * mm, "mid": v(139.7, 91.11) * mm, "end": v(137.94, 86.87) * mm});
            skArc(sketch, "E2309", {"start": v(137.94, 86.87) * mm, "mid": v(139.7, 82.63) * mm, "end": v(143.94, 80.87) * mm});
            skArc(sketch, "E2310", {"start": v(143.94, 80.87) * mm, "mid": v(148.19, 82.63) * mm, "end": v(149.94, 86.87) * mm});
            skArc(sketch, "E2311", {"start": v(149.94, 86.87) * mm, "mid": v(148.19, 91.11) * mm, "end": v(143.94, 92.87) * mm});
            skArc(sketch, "E2312", {"start": v(157.28, 68.87) * mm, "mid": v(153.03, 67.11) * mm, "end": v(151.28, 62.87) * mm});
            skArc(sketch, "E2313", {"start": v(151.28, 62.87) * mm, "mid": v(153.03, 58.63) * mm, "end": v(157.28, 56.87) * mm});
            skArc(sketch, "E2314", {"start": v(157.28, 56.87) * mm, "mid": v(161.52, 58.63) * mm, "end": v(163.28, 62.87) * mm});
            skArc(sketch, "E2315", {"start": v(163.28, 62.87) * mm, "mid": v(161.52, 67.11) * mm, "end": v(157.28, 68.87) * mm});
            skArc(sketch, "E2316", {"start": v(177.28, 92.87) * mm, "mid": v(173.03, 91.11) * mm, "end": v(171.28, 86.87) * mm});
            skArc(sketch, "E2317", {"start": v(171.28, 86.87) * mm, "mid": v(173.03, 82.63) * mm, "end": v(177.28, 80.87) * mm});
            skArc(sketch, "E2318", {"start": v(177.28, 80.87) * mm, "mid": v(181.52, 82.63) * mm, "end": v(183.28, 86.87) * mm});
            skArc(sketch, "E2319", {"start": v(183.28, 86.87) * mm, "mid": v(181.52, 91.11) * mm, "end": v(177.28, 92.87) * mm});
            skArc(sketch, "E2320", {"start": v(190.61, 68.87) * mm, "mid": v(186.37, 67.11) * mm, "end": v(184.61, 62.87) * mm});
            skArc(sketch, "E2321", {"start": v(184.61, 62.87) * mm, "mid": v(186.37, 58.63) * mm, "end": v(190.61, 56.87) * mm});
            skArc(sketch, "E2322", {"start": v(190.61, 56.87) * mm, "mid": v(194.85, 58.63) * mm, "end": v(196.61, 62.87) * mm});
            skArc(sketch, "E2323", {"start": v(196.61, 62.87) * mm, "mid": v(194.85, 67.11) * mm, "end": v(190.61, 68.87) * mm});
            skArc(sketch, "E2324", {"start": v(203.94, 92.87) * mm, "mid": v(199.7, 91.11) * mm, "end": v(197.94, 86.87) * mm});
            skArc(sketch, "E2325", {"start": v(197.94, 86.87) * mm, "mid": v(199.7, 82.63) * mm, "end": v(203.94, 80.87) * mm});
            skArc(sketch, "E2326", {"start": v(203.94, 80.87) * mm, "mid": v(208.19, 82.63) * mm, "end": v(209.94, 86.87) * mm});
            skArc(sketch, "E2327", {"start": v(209.94, 86.87) * mm, "mid": v(208.19, 91.11) * mm, "end": v(203.94, 92.87) * mm});
            skArc(sketch, "E2328", {"start": v(217.28, 68.87) * mm, "mid": v(213.03, 67.11) * mm, "end": v(211.28, 62.87) * mm});
            skArc(sketch, "E2329", {"start": v(211.28, 62.87) * mm, "mid": v(213.03, 58.63) * mm, "end": v(217.28, 56.87) * mm});
            skArc(sketch, "E2330", {"start": v(217.28, 56.87) * mm, "mid": v(221.52, 58.63) * mm, "end": v(223.28, 62.87) * mm});
            skArc(sketch, "E2331", {"start": v(223.28, 62.87) * mm, "mid": v(221.52, 67.11) * mm, "end": v(217.28, 68.87) * mm});
            skArc(sketch, "E2332", {"start": v(230.61, 92.87) * mm, "mid": v(226.37, 91.11) * mm, "end": v(224.61, 86.87) * mm});
            skArc(sketch, "E2333", {"start": v(224.61, 86.87) * mm, "mid": v(226.37, 82.63) * mm, "end": v(230.61, 80.87) * mm});
            skArc(sketch, "E2334", {"start": v(230.61, 80.87) * mm, "mid": v(234.85, 82.63) * mm, "end": v(236.61, 86.87) * mm});
            skArc(sketch, "E2335", {"start": v(236.61, 86.87) * mm, "mid": v(234.85, 91.11) * mm, "end": v(230.61, 92.87) * mm});
            skArc(sketch, "E2336", {"start": v(243.94, 68.87) * mm, "mid": v(239.7, 67.11) * mm, "end": v(237.94, 62.87) * mm});
            skArc(sketch, "E2337", {"start": v(237.94, 62.87) * mm, "mid": v(239.7, 58.63) * mm, "end": v(243.94, 56.87) * mm});
            skArc(sketch, "E2338", {"start": v(243.94, 56.87) * mm, "mid": v(248.19, 58.63) * mm, "end": v(249.94, 62.87) * mm});
            skArc(sketch, "E2339", {"start": v(249.94, 62.87) * mm, "mid": v(248.19, 67.11) * mm, "end": v(243.94, 68.87) * mm});
            skArc(sketch, "E2340", {"start": v(92.94, 36.7) * mm, "mid": v(93.1, 36.36) * mm, "end": v(93.44, 36.2) * mm});
            skLineSegment(sketch, "E2341", {"start": v(93.44, 36.2) * mm, "end": v(94.44, 36.2) * mm});
            skArc(sketch, "E2342", {"start": v(94.44, 36.2) * mm, "mid": v(94.8, 36.36) * mm, "end": v(94.94, 36.7) * mm});
            skLineSegment(sketch, "E2343", {"start": v(94.94, 36.7) * mm, "end": v(94.94, 98.2) * mm});
            skArc(sketch, "E2344", {"start": v(94.94, 98.2) * mm, "mid": v(94.8, 98.56) * mm, "end": v(94.44, 98.7) * mm});
            skLineSegment(sketch, "E2345", {"start": v(94.44, 98.7) * mm, "end": v(93.44, 98.7) * mm});
            skArc(sketch, "E2346", {"start": v(93.44, 98.7) * mm, "mid": v(93.1, 98.56) * mm, "end": v(92.94, 98.2) * mm});
            skLineSegment(sketch, "E2347", {"start": v(92.94, 98.2) * mm, "end": v(92.94, 36.7) * mm});
            skArc(sketch, "E2348", {"start": v(166.28, 36.7) * mm, "mid": v(166.42, 36.36) * mm, "end": v(166.78, 36.2) * mm});
            skLineSegment(sketch, "E2349", {"start": v(166.78, 36.2) * mm, "end": v(167.78, 36.2) * mm});
            skArc(sketch, "E2350", {"start": v(167.78, 36.2) * mm, "mid": v(168.13, 36.36) * mm, "end": v(168.28, 36.7) * mm});
            skLineSegment(sketch, "E2351", {"start": v(168.28, 36.7) * mm, "end": v(168.28, 98.2) * mm});
            skArc(sketch, "E2352", {"start": v(168.28, 98.2) * mm, "mid": v(168.13, 98.56) * mm, "end": v(167.78, 98.7) * mm});
            skLineSegment(sketch, "E2353", {"start": v(167.78, 98.7) * mm, "end": v(166.78, 98.7) * mm});
            skArc(sketch, "E2354", {"start": v(166.78, 98.7) * mm, "mid": v(166.42, 98.56) * mm, "end": v(166.28, 98.2) * mm});
            skLineSegment(sketch, "E2355", {"start": v(166.28, 98.2) * mm, "end": v(166.28, 36.7) * mm});
            skArc(sketch, "E2356", {"start": v(123.11, 62.87) * mm, "mid": v(125.3, 57.57) * mm, "end": v(130.61, 55.37) * mm});
            skArc(sketch, "E2357", {"start": v(130.61, 55.37) * mm, "mid": v(135.91, 57.57) * mm, "end": v(138.11, 62.87) * mm});
            skArc(sketch, "E2358", {"start": v(138.11, 62.87) * mm, "mid": v(135.91, 68.17) * mm, "end": v(130.61, 70.37) * mm});
            skArc(sketch, "E2359", {"start": v(130.61, 70.37) * mm, "mid": v(125.3, 68.17) * mm, "end": v(123.11, 62.87) * mm});
            skArc(sketch, "E2360", {"start": v(103.94, 55.37) * mm, "mid": v(109.25, 57.57) * mm, "end": v(111.44, 62.87) * mm});
            skArc(sketch, "E2361", {"start": v(111.44, 62.87) * mm, "mid": v(109.25, 68.17) * mm, "end": v(103.94, 70.37) * mm});
            skArc(sketch, "E2362", {"start": v(103.94, 70.37) * mm, "mid": v(98.64, 68.17) * mm, "end": v(96.44, 62.87) * mm});
            skArc(sketch, "E2363", {"start": v(96.44, 62.87) * mm, "mid": v(98.64, 57.57) * mm, "end": v(103.94, 55.37) * mm});
            skArc(sketch, "E2364", {"start": v(117.28, 79.37) * mm, "mid": v(122.58, 81.57) * mm, "end": v(124.78, 86.87) * mm});
            skArc(sketch, "E2365", {"start": v(124.78, 86.87) * mm, "mid": v(122.58, 92.17) * mm, "end": v(117.28, 94.37) * mm});
            skArc(sketch, "E2366", {"start": v(117.28, 94.37) * mm, "mid": v(111.97, 92.17) * mm, "end": v(109.78, 86.87) * mm});
            skArc(sketch, "E2367", {"start": v(109.78, 86.87) * mm, "mid": v(111.97, 81.57) * mm, "end": v(117.28, 79.37) * mm});
            skArc(sketch, "E2368", {"start": v(91.44, 86.87) * mm, "mid": v(89.25, 92.17) * mm, "end": v(83.94, 94.37) * mm});
            skArc(sketch, "E2369", {"start": v(83.94, 94.37) * mm, "mid": v(78.64, 92.17) * mm, "end": v(76.44, 86.87) * mm});
            skArc(sketch, "E2370", {"start": v(76.44, 86.87) * mm, "mid": v(78.64, 81.57) * mm, "end": v(83.94, 79.37) * mm});
            skArc(sketch, "E2371", {"start": v(83.94, 79.37) * mm, "mid": v(89.25, 81.57) * mm, "end": v(91.44, 86.87) * mm});
            skArc(sketch, "E2372", {"start": v(64.78, 86.87) * mm, "mid": v(62.58, 92.17) * mm, "end": v(57.28, 94.37) * mm});
            skArc(sketch, "E2373", {"start": v(57.28, 94.37) * mm, "mid": v(51.97, 92.17) * mm, "end": v(49.78, 86.87) * mm});
            skArc(sketch, "E2374", {"start": v(49.78, 86.87) * mm, "mid": v(51.97, 81.57) * mm, "end": v(57.28, 79.37) * mm});
            skArc(sketch, "E2375", {"start": v(57.28, 79.37) * mm, "mid": v(62.58, 81.57) * mm, "end": v(64.78, 86.87) * mm});
            skArc(sketch, "E2376", {"start": v(38.11, 86.87) * mm, "mid": v(35.91, 92.17) * mm, "end": v(30.61, 94.37) * mm});
            skArc(sketch, "E2377", {"start": v(30.61, 94.37) * mm, "mid": v(25.3, 92.17) * mm, "end": v(23.11, 86.87) * mm});
            skArc(sketch, "E2378", {"start": v(23.11, 86.87) * mm, "mid": v(25.3, 81.57) * mm, "end": v(30.61, 79.37) * mm});
            skArc(sketch, "E2379", {"start": v(30.61, 79.37) * mm, "mid": v(35.91, 81.57) * mm, "end": v(38.11, 86.87) * mm});
            skArc(sketch, "E2380", {"start": v(17.28, 70.37) * mm, "mid": v(11.97, 68.17) * mm, "end": v(9.78, 62.87) * mm});
            skArc(sketch, "E2381", {"start": v(9.78, 62.87) * mm, "mid": v(11.97, 57.57) * mm, "end": v(17.28, 55.37) * mm});
            skArc(sketch, "E2382", {"start": v(17.28, 55.37) * mm, "mid": v(22.58, 57.57) * mm, "end": v(24.78, 62.87) * mm});
            skArc(sketch, "E2383", {"start": v(24.78, 62.87) * mm, "mid": v(22.58, 68.17) * mm, "end": v(17.28, 70.37) * mm});
            skArc(sketch, "E2384", {"start": v(36.44, 62.87) * mm, "mid": v(38.64, 57.57) * mm, "end": v(43.94, 55.37) * mm});
            skArc(sketch, "E2385", {"start": v(43.94, 55.37) * mm, "mid": v(49.25, 57.57) * mm, "end": v(51.44, 62.87) * mm});
            skArc(sketch, "E2386", {"start": v(51.44, 62.87) * mm, "mid": v(49.25, 68.17) * mm, "end": v(43.94, 70.37) * mm});
            skArc(sketch, "E2387", {"start": v(43.94, 70.37) * mm, "mid": v(38.64, 68.17) * mm, "end": v(36.44, 62.87) * mm});
            skArc(sketch, "E2388", {"start": v(63.11, 62.87) * mm, "mid": v(65.3, 57.57) * mm, "end": v(70.61, 55.37) * mm});
            skArc(sketch, "E2389", {"start": v(70.61, 55.37) * mm, "mid": v(75.91, 57.57) * mm, "end": v(78.11, 62.87) * mm});
            skArc(sketch, "E2390", {"start": v(78.11, 62.87) * mm, "mid": v(75.91, 68.17) * mm, "end": v(70.61, 70.37) * mm});
            skArc(sketch, "E2391", {"start": v(70.61, 70.37) * mm, "mid": v(65.3, 68.17) * mm, "end": v(63.11, 62.87) * mm});
            skArc(sketch, "E2392", {"start": v(136.44, 86.87) * mm, "mid": v(138.64, 81.57) * mm, "end": v(143.94, 79.37) * mm});
            skArc(sketch, "E2393", {"start": v(143.94, 79.37) * mm, "mid": v(149.25, 81.57) * mm, "end": v(151.44, 86.87) * mm});
            skArc(sketch, "E2394", {"start": v(151.44, 86.87) * mm, "mid": v(149.25, 92.17) * mm, "end": v(143.94, 94.37) * mm});
            skArc(sketch, "E2395", {"start": v(143.94, 94.37) * mm, "mid": v(138.64, 92.17) * mm, "end": v(136.44, 86.87) * mm});
            skArc(sketch, "E2396", {"start": v(157.28, 70.37) * mm, "mid": v(151.97, 68.17) * mm, "end": v(149.78, 62.87) * mm});
            skArc(sketch, "E2397", {"start": v(149.78, 62.87) * mm, "mid": v(151.97, 57.57) * mm, "end": v(157.28, 55.37) * mm});
            skArc(sketch, "E2398", {"start": v(157.28, 55.37) * mm, "mid": v(162.58, 57.57) * mm, "end": v(164.78, 62.87) * mm});
            skArc(sketch, "E2399", {"start": v(164.78, 62.87) * mm, "mid": v(162.58, 68.17) * mm, "end": v(157.28, 70.37) * mm});
            skArc(sketch, "E2400", {"start": v(183.11, 62.87) * mm, "mid": v(185.3, 57.57) * mm, "end": v(190.61, 55.37) * mm});
            skArc(sketch, "E2401", {"start": v(190.61, 55.37) * mm, "mid": v(195.91, 57.57) * mm, "end": v(198.11, 62.87) * mm});
            skArc(sketch, "E2402", {"start": v(198.11, 62.87) * mm, "mid": v(195.91, 68.17) * mm, "end": v(190.61, 70.37) * mm});
            skArc(sketch, "E2403", {"start": v(190.61, 70.37) * mm, "mid": v(185.3, 68.17) * mm, "end": v(183.11, 62.87) * mm});
            skArc(sketch, "E2404", {"start": v(209.78, 62.87) * mm, "mid": v(211.97, 57.57) * mm, "end": v(217.28, 55.37) * mm});
            skArc(sketch, "E2405", {"start": v(217.28, 55.37) * mm, "mid": v(222.58, 57.57) * mm, "end": v(224.78, 62.87) * mm});
            skArc(sketch, "E2406", {"start": v(224.78, 62.87) * mm, "mid": v(222.58, 68.17) * mm, "end": v(217.28, 70.37) * mm});
            skArc(sketch, "E2407", {"start": v(217.28, 70.37) * mm, "mid": v(211.97, 68.17) * mm, "end": v(209.78, 62.87) * mm});
            skArc(sketch, "E2408", {"start": v(236.44, 62.87) * mm, "mid": v(238.64, 57.57) * mm, "end": v(243.94, 55.37) * mm});
            skArc(sketch, "E2409", {"start": v(243.94, 55.37) * mm, "mid": v(249.25, 57.57) * mm, "end": v(251.44, 62.87) * mm});
            skArc(sketch, "E2410", {"start": v(251.44, 62.87) * mm, "mid": v(249.25, 68.17) * mm, "end": v(243.94, 70.37) * mm});
            skArc(sketch, "E2411", {"start": v(243.94, 70.37) * mm, "mid": v(238.64, 68.17) * mm, "end": v(236.44, 62.87) * mm});
            skArc(sketch, "E2412", {"start": v(230.61, 79.37) * mm, "mid": v(235.91, 81.57) * mm, "end": v(238.11, 86.87) * mm});
            skArc(sketch, "E2413", {"start": v(238.11, 86.87) * mm, "mid": v(235.91, 92.17) * mm, "end": v(230.61, 94.37) * mm});
            skArc(sketch, "E2414", {"start": v(230.61, 94.37) * mm, "mid": v(225.3, 92.17) * mm, "end": v(223.11, 86.87) * mm});
            skArc(sketch, "E2415", {"start": v(223.11, 86.87) * mm, "mid": v(225.3, 81.57) * mm, "end": v(230.61, 79.37) * mm});
            skArc(sketch, "E2416", {"start": v(211.44, 86.87) * mm, "mid": v(209.25, 92.17) * mm, "end": v(203.94, 94.37) * mm});
            skArc(sketch, "E2417", {"start": v(203.94, 94.37) * mm, "mid": v(198.64, 92.17) * mm, "end": v(196.44, 86.87) * mm});
            skArc(sketch, "E2418", {"start": v(196.44, 86.87) * mm, "mid": v(198.64, 81.57) * mm, "end": v(203.94, 79.37) * mm});
            skArc(sketch, "E2419", {"start": v(203.94, 79.37) * mm, "mid": v(209.25, 81.57) * mm, "end": v(211.44, 86.87) * mm});
            skArc(sketch, "E2420", {"start": v(184.78, 86.87) * mm, "mid": v(182.58, 92.17) * mm, "end": v(177.28, 94.37) * mm});
            skArc(sketch, "E2421", {"start": v(177.28, 94.37) * mm, "mid": v(171.97, 92.17) * mm, "end": v(169.78, 86.87) * mm});
            skArc(sketch, "E2422", {"start": v(169.78, 86.87) * mm, "mid": v(171.97, 81.57) * mm, "end": v(177.28, 79.37) * mm});
            skArc(sketch, "E2423", {"start": v(177.28, 79.37) * mm, "mid": v(182.58, 81.57) * mm, "end": v(184.78, 86.87) * mm});
            skLineSegment(sketch, "E2424", {"start": v(260.83, 99) * mm, "end": v(260.56, 98.89) * mm});
            skLineSegment(sketch, "E2425", {"start": v(260.56, 98.89) * mm, "end": v(260.28, 98.8) * mm});
            skLineSegment(sketch, "E2426", {"start": v(260.28, 98.8) * mm, "end": v(259.99, 98.75) * mm});
            skLineSegment(sketch, "E2427", {"start": v(259.99, 98.75) * mm, "end": v(259.69, 98.7) * mm});
            skLineSegment(sketch, "E2428", {"start": v(259.69, 98.7) * mm, "end": v(259.39, 98.7) * mm});
            skLineSegment(sketch, "E2429", {"start": v(259.39, 98.7) * mm, "end": v(259.08, 98.7) * mm});
            skLineSegment(sketch, "E2430", {"start": v(259.08, 98.7) * mm, "end": v(258.77, 98.73) * mm});
            skLineSegment(sketch, "E2431", {"start": v(258.77, 98.73) * mm, "end": v(258.45, 98.78) * mm});
            skLineSegment(sketch, "E2432", {"start": v(258.45, 98.78) * mm, "end": v(258.13, 98.85) * mm});
            skLineSegment(sketch, "E2433", {"start": v(258.13, 98.85) * mm, "end": v(257.81, 98.94) * mm});
            skLineSegment(sketch, "E2434", {"start": v(257.81, 98.94) * mm, "end": v(257.5, 99.04) * mm});
            skLineSegment(sketch, "E2435", {"start": v(257.5, 99.04) * mm, "end": v(257.17, 99.17) * mm});
            skLineSegment(sketch, "E2436", {"start": v(257.17, 99.17) * mm, "end": v(256.85, 99.3) * mm});
            skLineSegment(sketch, "E2437", {"start": v(256.85, 99.3) * mm, "end": v(256.53, 99.46) * mm});
            skLineSegment(sketch, "E2438", {"start": v(256.53, 99.46) * mm, "end": v(256.21, 99.63) * mm});
            skLineSegment(sketch, "E2439", {"start": v(256.21, 99.63) * mm, "end": v(255.9, 99.82) * mm});
            skLineSegment(sketch, "E2440", {"start": v(255.9, 99.82) * mm, "end": v(255.59, 100.02) * mm});
            skLineSegment(sketch, "E2441", {"start": v(255.59, 100.02) * mm, "end": v(255.28, 100.23) * mm});
            skLineSegment(sketch, "E2442", {"start": v(255.28, 100.23) * mm, "end": v(254.98, 100.45) * mm});
            skLineSegment(sketch, "E2443", {"start": v(254.98, 100.45) * mm, "end": v(254.68, 100.69) * mm});
            skLineSegment(sketch, "E2444", {"start": v(254.68, 100.69) * mm, "end": v(254.4, 100.94) * mm});
            skLineSegment(sketch, "E2445", {"start": v(254.4, 100.94) * mm, "end": v(254.12, 101.2) * mm});
            skLineSegment(sketch, "E2446", {"start": v(254.12, 101.2) * mm, "end": v(253.85, 101.46) * mm});
            skLineSegment(sketch, "E2447", {"start": v(253.85, 101.46) * mm, "end": v(253.59, 101.73) * mm});
            skLineSegment(sketch, "E2448", {"start": v(253.59, 101.73) * mm, "end": v(253.34, 102.02) * mm});
            skLineSegment(sketch, "E2449", {"start": v(253.34, 102.02) * mm, "end": v(253.1, 102.3) * mm});
            skLineSegment(sketch, "E2450", {"start": v(253.1, 102.3) * mm, "end": v(252.87, 102.6) * mm});
            skLineSegment(sketch, "E2451", {"start": v(252.87, 102.6) * mm, "end": v(252.66, 102.9) * mm});
            skLineSegment(sketch, "E2452", {"start": v(252.66, 102.9) * mm, "end": v(252.46, 103.22) * mm});
            skLineSegment(sketch, "E2453", {"start": v(252.46, 103.22) * mm, "end": v(252.27, 103.53) * mm});
            skLineSegment(sketch, "E2454", {"start": v(252.27, 103.53) * mm, "end": v(252.1, 103.85) * mm});
            skLineSegment(sketch, "E2455", {"start": v(252.1, 103.85) * mm, "end": v(251.95, 104.17) * mm});
            skLineSegment(sketch, "E2456", {"start": v(260.83, 96.84) * mm, "end": v(260.77, 96.83) * mm});
            skLineSegment(sketch, "E2457", {"start": v(260.77, 96.83) * mm, "end": v(260.3, 96.77) * mm});
            skLineSegment(sketch, "E2458", {"start": v(260.3, 96.77) * mm, "end": v(259.8, 96.7) * mm});
            skLineSegment(sketch, "E2459", {"start": v(259.8, 96.7) * mm, "end": v(259.3, 96.6) * mm});
            skLineSegment(sketch, "E2460", {"start": v(259.3, 96.6) * mm, "end": v(259.04, 96.58) * mm});
            skLineSegment(sketch, "E2461", {"start": v(259.04, 96.58) * mm, "end": v(258.8, 96.55) * mm});
            skLineSegment(sketch, "E2462", {"start": v(258.8, 96.55) * mm, "end": v(258.55, 96.54) * mm});
            skLineSegment(sketch, "E2463", {"start": v(258.55, 96.54) * mm, "end": v(258.3, 96.54) * mm});
            skLineSegment(sketch, "E2464", {"start": v(258.3, 96.54) * mm, "end": v(258.07, 96.55) * mm});
            skLineSegment(sketch, "E2465", {"start": v(258.07, 96.55) * mm, "end": v(257.85, 96.59) * mm});
            skLineSegment(sketch, "E2466", {"start": v(257.85, 96.59) * mm, "end": v(257.63, 96.64) * mm});
            skLineSegment(sketch, "E2467", {"start": v(257.63, 96.64) * mm, "end": v(257.42, 96.73) * mm});
            skLineSegment(sketch, "E2468", {"start": v(257.42, 96.73) * mm, "end": v(257.32, 96.78) * mm});
            skLineSegment(sketch, "E2469", {"start": v(257.32, 96.78) * mm, "end": v(257.23, 96.83) * mm});
            skLineSegment(sketch, "E2470", {"start": v(257.23, 96.83) * mm, "end": v(257.14, 96.9) * mm});
            skLineSegment(sketch, "E2471", {"start": v(257.14, 96.9) * mm, "end": v(257.05, 96.97) * mm});
            skLineSegment(sketch, "E2472", {"start": v(257.05, 96.97) * mm, "end": v(256.72, 97.29) * mm});
            skLineSegment(sketch, "E2473", {"start": v(256.72, 97.29) * mm, "end": v(256.4, 97.63) * mm});
            skLineSegment(sketch, "E2474", {"start": v(256.4, 97.63) * mm, "end": v(256.1, 98) * mm});
            skLineSegment(sketch, "E2475", {"start": v(256.1, 98) * mm, "end": v(255.8, 98.39) * mm});
            skLineSegment(sketch, "E2476", {"start": v(255.8, 98.39) * mm, "end": v(255.53, 98.8) * mm});
            skLineSegment(sketch, "E2477", {"start": v(255.53, 98.8) * mm, "end": v(255.26, 99.23) * mm});
            skLineSegment(sketch, "E2478", {"start": v(255.26, 99.23) * mm, "end": v(255.02, 99.68) * mm});
            skLineSegment(sketch, "E2479", {"start": v(255.02, 99.68) * mm, "end": v(254.79, 100.15) * mm});
            skLineSegment(sketch, "E2480", {"start": v(254.79, 100.15) * mm, "end": v(254.58, 100.63) * mm});
            skLineSegment(sketch, "E2481", {"start": v(254.58, 100.63) * mm, "end": v(254.39, 101.12) * mm});
            skLineSegment(sketch, "E2482", {"start": v(254.39, 101.12) * mm, "end": v(254.21, 101.61) * mm});
            skLineSegment(sketch, "E2483", {"start": v(254.21, 101.61) * mm, "end": v(254.06, 102.12) * mm});
            skLineSegment(sketch, "E2484", {"start": v(254.06, 102.12) * mm, "end": v(253.93, 102.63) * mm});
            skLineSegment(sketch, "E2485", {"start": v(253.93, 102.63) * mm, "end": v(253.82, 103.14) * mm});
            skLineSegment(sketch, "E2486", {"start": v(253.82, 103.14) * mm, "end": v(253.74, 103.66) * mm});
            skLineSegment(sketch, "E2487", {"start": v(253.74, 103.66) * mm, "end": v(253.67, 104.17) * mm});
            skLineSegment(sketch, "E2488", {"start": v(239.86, 104.46) * mm, "end": v(239.83, 104.34) * mm});
            skLineSegment(sketch, "E2489", {"start": v(239.83, 104.34) * mm, "end": v(239.78, 104.22) * mm});
            skLineSegment(sketch, "E2490", {"start": v(239.78, 104.22) * mm, "end": v(239.7, 104.1) * mm});
            skLineSegment(sketch, "E2491", {"start": v(239.7, 104.1) * mm, "end": v(239.62, 104) * mm});
            skLineSegment(sketch, "E2492", {"start": v(239.62, 104) * mm, "end": v(239.5, 103.88) * mm});
            skLineSegment(sketch, "E2493", {"start": v(239.5, 103.88) * mm, "end": v(239.37, 103.77) * mm});
            skLineSegment(sketch, "E2494", {"start": v(239.37, 103.77) * mm, "end": v(239.22, 103.66) * mm});
            skLineSegment(sketch, "E2495", {"start": v(239.22, 103.66) * mm, "end": v(239.05, 103.55) * mm});
            skLineSegment(sketch, "E2496", {"start": v(239.05, 103.55) * mm, "end": v(238.86, 103.44) * mm});
            skLineSegment(sketch, "E2497", {"start": v(238.86, 103.44) * mm, "end": v(238.65, 103.34) * mm});
            skLineSegment(sketch, "E2498", {"start": v(238.65, 103.34) * mm, "end": v(238.2, 103.13) * mm});
            skLineSegment(sketch, "E2499", {"start": v(238.2, 103.13) * mm, "end": v(237.68, 102.93) * mm});
            skLineSegment(sketch, "E2500", {"start": v(237.68, 102.93) * mm, "end": v(237.11, 102.73) * mm});
            skLineSegment(sketch, "E2501", {"start": v(237.11, 102.73) * mm, "end": v(236.5, 102.54) * mm});
            skLineSegment(sketch, "E2502", {"start": v(236.5, 102.54) * mm, "end": v(235.83, 102.36) * mm});
            skLineSegment(sketch, "E2503", {"start": v(235.83, 102.36) * mm, "end": v(235.13, 102.17) * mm});
            skLineSegment(sketch, "E2504", {"start": v(235.13, 102.17) * mm, "end": v(234.4, 102) * mm});
            skLineSegment(sketch, "E2505", {"start": v(234.4, 102) * mm, "end": v(233.65, 101.82) * mm});
            skLineSegment(sketch, "E2506", {"start": v(233.65, 101.82) * mm, "end": v(232.87, 101.65) * mm});
            skLineSegment(sketch, "E2507", {"start": v(232.87, 101.65) * mm, "end": v(231.28, 101.33) * mm});
            skLineSegment(sketch, "E2508", {"start": v(231.28, 101.33) * mm, "end": v(228.09, 100.72) * mm});
            skLineSegment(sketch, "E2509", {"start": v(228.09, 100.72) * mm, "end": v(226.57, 100.44) * mm});
            skLineSegment(sketch, "E2510", {"start": v(226.57, 100.44) * mm, "end": v(225.18, 100.16) * mm});
            skLineSegment(sketch, "E2511", {"start": v(225.18, 100.16) * mm, "end": v(224.53, 100.03) * mm});
            skLineSegment(sketch, "E2512", {"start": v(224.53, 100.03) * mm, "end": v(223.94, 99.9) * mm});
            skLineSegment(sketch, "E2513", {"start": v(223.94, 99.9) * mm, "end": v(223.4, 99.77) * mm});
            skLineSegment(sketch, "E2514", {"start": v(223.4, 99.77) * mm, "end": v(222.9, 99.64) * mm});
            skLineSegment(sketch, "E2515", {"start": v(222.9, 99.64) * mm, "end": v(222.47, 99.52) * mm});
            skLineSegment(sketch, "E2516", {"start": v(222.47, 99.52) * mm, "end": v(222.11, 99.4) * mm});
            skLineSegment(sketch, "E2517", {"start": v(222.11, 99.4) * mm, "end": v(221.82, 99.28) * mm});
            skLineSegment(sketch, "E2518", {"start": v(221.82, 99.28) * mm, "end": v(221.7, 99.22) * mm});
            skLineSegment(sketch, "E2519", {"start": v(221.7, 99.22) * mm, "end": v(221.61, 99.16) * mm});
            skLineSegment(sketch, "E2520", {"start": v(221.61, 99.16) * mm, "end": v(221.38, 99) * mm});
            skLineSegment(sketch, "E2521", {"start": v(221.38, 99) * mm, "end": v(221.15, 98.85) * mm});
            skLineSegment(sketch, "E2522", {"start": v(221.15, 98.85) * mm, "end": v(220.93, 98.72) * mm});
            skLineSegment(sketch, "E2523", {"start": v(220.93, 98.72) * mm, "end": v(220.7, 98.6) * mm});
            skLineSegment(sketch, "E2524", {"start": v(220.7, 98.6) * mm, "end": v(220.48, 98.49) * mm});
            skLineSegment(sketch, "E2525", {"start": v(220.48, 98.49) * mm, "end": v(220.26, 98.39) * mm});
            skLineSegment(sketch, "E2526", {"start": v(220.26, 98.39) * mm, "end": v(220.04, 98.3) * mm});
            skLineSegment(sketch, "E2527", {"start": v(220.04, 98.3) * mm, "end": v(219.82, 98.21) * mm});
            skLineSegment(sketch, "E2528", {"start": v(219.82, 98.21) * mm, "end": v(219.6, 98.14) * mm});
            skLineSegment(sketch, "E2529", {"start": v(219.6, 98.14) * mm, "end": v(219.4, 98.08) * mm});
            skLineSegment(sketch, "E2530", {"start": v(219.4, 98.08) * mm, "end": v(219.18, 98.03) * mm});
            skLineSegment(sketch, "E2531", {"start": v(219.18, 98.03) * mm, "end": v(218.97, 97.99) * mm});
            skLineSegment(sketch, "E2532", {"start": v(218.97, 97.99) * mm, "end": v(218.76, 97.95) * mm});
            skLineSegment(sketch, "E2533", {"start": v(218.76, 97.95) * mm, "end": v(218.55, 97.93) * mm});
            skLineSegment(sketch, "E2534", {"start": v(218.55, 97.93) * mm, "end": v(218.35, 97.9) * mm});
            skLineSegment(sketch, "E2535", {"start": v(218.35, 97.9) * mm, "end": v(218.14, 97.9) * mm});
            skLineSegment(sketch, "E2536", {"start": v(218.14, 97.9) * mm, "end": v(217.73, 97.9) * mm});
            skLineSegment(sketch, "E2537", {"start": v(217.73, 97.9) * mm, "end": v(217.33, 97.93) * mm});
            skLineSegment(sketch, "E2538", {"start": v(217.33, 97.93) * mm, "end": v(216.93, 98) * mm});
            skLineSegment(sketch, "E2539", {"start": v(216.93, 98) * mm, "end": v(216.54, 98.08) * mm});
            skLineSegment(sketch, "E2540", {"start": v(216.54, 98.08) * mm, "end": v(216.15, 98.18) * mm});
            skLineSegment(sketch, "E2541", {"start": v(216.15, 98.18) * mm, "end": v(215.76, 98.3) * mm});
            skLineSegment(sketch, "E2542", {"start": v(215.76, 98.3) * mm, "end": v(215.37, 98.45) * mm});
            skLineSegment(sketch, "E2543", {"start": v(215.37, 98.45) * mm, "end": v(214.99, 98.62) * mm});
            skLineSegment(sketch, "E2544", {"start": v(214.99, 98.62) * mm, "end": v(214.6, 98.8) * mm});
            skLineSegment(sketch, "E2545", {"start": v(214.6, 98.8) * mm, "end": v(214.22, 98.98) * mm});
            skLineSegment(sketch, "E2546", {"start": v(214.22, 98.98) * mm, "end": v(213.46, 99.39) * mm});
            skLineSegment(sketch, "E2547", {"start": v(213.46, 99.39) * mm, "end": v(212.7, 99.82) * mm});
            skLineSegment(sketch, "E2548", {"start": v(212.7, 99.82) * mm, "end": v(211.93, 100.26) * mm});
            skLineSegment(sketch, "E2549", {"start": v(211.93, 100.26) * mm, "end": v(211.15, 100.69) * mm});
            skLineSegment(sketch, "E2550", {"start": v(211.15, 100.69) * mm, "end": v(210.76, 100.9) * mm});
            skLineSegment(sketch, "E2551", {"start": v(210.76, 100.9) * mm, "end": v(210.37, 101.1) * mm});
            skLineSegment(sketch, "E2552", {"start": v(210.37, 101.1) * mm, "end": v(209.97, 101.28) * mm});
            skLineSegment(sketch, "E2553", {"start": v(209.97, 101.28) * mm, "end": v(209.57, 101.46) * mm});
            skLineSegment(sketch, "E2554", {"start": v(209.57, 101.46) * mm, "end": v(209.16, 101.62) * mm});
            skLineSegment(sketch, "E2555", {"start": v(209.16, 101.62) * mm, "end": v(208.75, 101.77) * mm});
            skLineSegment(sketch, "E2556", {"start": v(208.75, 101.77) * mm, "end": v(208.52, 101.85) * mm});
            skLineSegment(sketch, "E2557", {"start": v(208.52, 101.85) * mm, "end": v(208.31, 101.95) * mm});
            skLineSegment(sketch, "E2558", {"start": v(208.31, 101.95) * mm, "end": v(208.11, 102.05) * mm});
            skLineSegment(sketch, "E2559", {"start": v(208.11, 102.05) * mm, "end": v(207.93, 102.16) * mm});
            skLineSegment(sketch, "E2560", {"start": v(207.93, 102.16) * mm, "end": v(207.76, 102.29) * mm});
            skLineSegment(sketch, "E2561", {"start": v(207.76, 102.29) * mm, "end": v(207.6, 102.42) * mm});
            skLineSegment(sketch, "E2562", {"start": v(207.6, 102.42) * mm, "end": v(207.45, 102.56) * mm});
            skLineSegment(sketch, "E2563", {"start": v(207.45, 102.56) * mm, "end": v(207.32, 102.7) * mm});
            skLineSegment(sketch, "E2564", {"start": v(207.32, 102.7) * mm, "end": v(207.2, 102.86) * mm});
            skLineSegment(sketch, "E2565", {"start": v(207.2, 102.86) * mm, "end": v(207.1, 103.03) * mm});
            skLineSegment(sketch, "E2566", {"start": v(207.1, 103.03) * mm, "end": v(207, 103.2) * mm});
            skLineSegment(sketch, "E2567", {"start": v(207, 103.2) * mm, "end": v(206.92, 103.38) * mm});
            skLineSegment(sketch, "E2568", {"start": v(206.92, 103.38) * mm, "end": v(206.85, 103.57) * mm});
            skLineSegment(sketch, "E2569", {"start": v(206.85, 103.57) * mm, "end": v(206.79, 103.76) * mm});
            skLineSegment(sketch, "E2570", {"start": v(206.79, 103.76) * mm, "end": v(206.74, 103.96) * mm});
            skLineSegment(sketch, "E2571", {"start": v(206.74, 103.96) * mm, "end": v(206.7, 104.17) * mm});
            skLineSegment(sketch, "E2572", {"start": v(257.14, 32.38) * mm, "end": v(257.09, 32.5) * mm});
            skLineSegment(sketch, "E2573", {"start": v(257.09, 32.5) * mm, "end": v(257.02, 32.62) * mm});
            skLineSegment(sketch, "E2574", {"start": v(257.02, 32.62) * mm, "end": v(256.87, 32.85) * mm});
            skLineSegment(sketch, "E2575", {"start": v(256.87, 32.85) * mm, "end": v(256.7, 33.07) * mm});
            skLineSegment(sketch, "E2576", {"start": v(256.7, 33.07) * mm, "end": v(256.52, 33.27) * mm});
            skLineSegment(sketch, "E2577", {"start": v(256.52, 33.27) * mm, "end": v(256.14, 33.7) * mm});
            skLineSegment(sketch, "E2578", {"start": v(256.14, 33.7) * mm, "end": v(255.97, 33.9) * mm});
            skLineSegment(sketch, "E2579", {"start": v(255.97, 33.9) * mm, "end": v(255.81, 34.13) * mm});
            skLineSegment(sketch, "E2580", {"start": v(255.81, 34.13) * mm, "end": v(255.7, 34.3) * mm});
            skLineSegment(sketch, "E2581", {"start": v(255.7, 34.3) * mm, "end": v(255.6, 34.47) * mm});
            skLineSegment(sketch, "E2582", {"start": v(255.6, 34.47) * mm, "end": v(255.52, 34.65) * mm});
            skLineSegment(sketch, "E2583", {"start": v(255.52, 34.65) * mm, "end": v(255.49, 34.75) * mm});
            skLineSegment(sketch, "E2584", {"start": v(255.49, 34.75) * mm, "end": v(255.46, 34.84) * mm});
            skLineSegment(sketch, "E2585", {"start": v(255.46, 34.84) * mm, "end": v(255.36, 35.3) * mm});
            skLineSegment(sketch, "E2586", {"start": v(255.36, 35.3) * mm, "end": v(255.23, 35.8) * mm});
            skLineSegment(sketch, "E2587", {"start": v(255.23, 35.8) * mm, "end": v(255.12, 36.31) * mm});
            skLineSegment(sketch, "E2588", {"start": v(255.12, 36.31) * mm, "end": v(255.08, 36.57) * mm});
            skLineSegment(sketch, "E2589", {"start": v(255.08, 36.57) * mm, "end": v(255.05, 36.82) * mm});
            skLineSegment(sketch, "E2590", {"start": v(255.05, 36.82) * mm, "end": v(255.03, 37.07) * mm});
            skLineSegment(sketch, "E2591", {"start": v(255.03, 37.07) * mm, "end": v(255.03, 37.3) * mm});
            skLineSegment(sketch, "E2592", {"start": v(255.03, 37.3) * mm, "end": v(255.05, 37.54) * mm});
            skLineSegment(sketch, "E2593", {"start": v(255.05, 37.54) * mm, "end": v(255.1, 37.75) * mm});
            skLineSegment(sketch, "E2594", {"start": v(255.1, 37.75) * mm, "end": v(255.13, 37.85) * mm});
            skLineSegment(sketch, "E2595", {"start": v(255.13, 37.85) * mm, "end": v(255.17, 37.95) * mm});
            skLineSegment(sketch, "E2596", {"start": v(255.17, 37.95) * mm, "end": v(255.22, 38.04) * mm});
            skLineSegment(sketch, "E2597", {"start": v(255.22, 38.04) * mm, "end": v(255.27, 38.13) * mm});
            skLineSegment(sketch, "E2598", {"start": v(255.27, 38.13) * mm, "end": v(255.33, 38.2) * mm});
            skLineSegment(sketch, "E2599", {"start": v(255.33, 38.2) * mm, "end": v(255.4, 38.29) * mm});
            skLineSegment(sketch, "E2600", {"start": v(255.4, 38.29) * mm, "end": v(255.49, 38.36) * mm});
            skLineSegment(sketch, "E2601", {"start": v(255.49, 38.36) * mm, "end": v(255.57, 38.42) * mm});
            skLineSegment(sketch, "E2602", {"start": v(255.57, 38.42) * mm, "end": v(255.84, 38.58) * mm});
            skLineSegment(sketch, "E2603", {"start": v(255.84, 38.58) * mm, "end": v(256.12, 38.72) * mm});
            skLineSegment(sketch, "E2604", {"start": v(256.12, 38.72) * mm, "end": v(256.41, 38.85) * mm});
            skLineSegment(sketch, "E2605", {"start": v(256.41, 38.85) * mm, "end": v(256.72, 38.95) * mm});
            skLineSegment(sketch, "E2606", {"start": v(256.72, 38.95) * mm, "end": v(257.03, 39.05) * mm});
            skLineSegment(sketch, "E2607", {"start": v(257.03, 39.05) * mm, "end": v(257.35, 39.12) * mm});
            skLineSegment(sketch, "E2608", {"start": v(257.35, 39.12) * mm, "end": v(257.67, 39.18) * mm});
            skLineSegment(sketch, "E2609", {"start": v(257.67, 39.18) * mm, "end": v(258, 39.22) * mm});
            skLineSegment(sketch, "E2610", {"start": v(258, 39.22) * mm, "end": v(258.35, 39.24) * mm});
            skLineSegment(sketch, "E2611", {"start": v(258.35, 39.24) * mm, "end": v(258.7, 39.25) * mm});
            skLineSegment(sketch, "E2612", {"start": v(258.7, 39.25) * mm, "end": v(259.04, 39.25) * mm});
            skLineSegment(sketch, "E2613", {"start": v(259.04, 39.25) * mm, "end": v(259.4, 39.23) * mm});
            skLineSegment(sketch, "E2614", {"start": v(259.4, 39.23) * mm, "end": v(259.75, 39.2) * mm});
            skLineSegment(sketch, "E2615", {"start": v(259.75, 39.2) * mm, "end": v(260.1, 39.15) * mm});
            skLineSegment(sketch, "E2616", {"start": v(260.1, 39.15) * mm, "end": v(260.47, 39.09) * mm});
            skLineSegment(sketch, "E2617", {"start": v(260.47, 39.09) * mm, "end": v(260.83, 39.01) * mm});
            skLineSegment(sketch, "E2618", {"start": v(256.08, 32.38) * mm, "end": v(256, 32.78) * mm});
            skLineSegment(sketch, "E2619", {"start": v(256, 32.78) * mm, "end": v(255.93, 33.18) * mm});
            skLineSegment(sketch, "E2620", {"start": v(255.93, 33.18) * mm, "end": v(255.87, 33.58) * mm});
            skLineSegment(sketch, "E2621", {"start": v(255.87, 33.58) * mm, "end": v(255.84, 33.96) * mm});
            skLineSegment(sketch, "E2622", {"start": v(255.84, 33.96) * mm, "end": v(255.83, 34.32) * mm});
            skLineSegment(sketch, "E2623", {"start": v(255.83, 34.32) * mm, "end": v(255.85, 34.67) * mm});
            skLineSegment(sketch, "E2624", {"start": v(255.85, 34.67) * mm, "end": v(255.86, 34.83) * mm});
            skLineSegment(sketch, "E2625", {"start": v(255.86, 34.83) * mm, "end": v(255.89, 35) * mm});
            skLineSegment(sketch, "E2626", {"start": v(255.89, 35) * mm, "end": v(255.92, 35.14) * mm});
            skLineSegment(sketch, "E2627", {"start": v(255.92, 35.14) * mm, "end": v(255.96, 35.28) * mm});
            skLineSegment(sketch, "E2628", {"start": v(255.96, 35.28) * mm, "end": v(256, 35.42) * mm});
            skLineSegment(sketch, "E2629", {"start": v(256, 35.42) * mm, "end": v(256.06, 35.55) * mm});
            skLineSegment(sketch, "E2630", {"start": v(256.06, 35.55) * mm, "end": v(256.12, 35.67) * mm});
            skLineSegment(sketch, "E2631", {"start": v(256.12, 35.67) * mm, "end": v(256.2, 35.78) * mm});
            skLineSegment(sketch, "E2632", {"start": v(256.2, 35.78) * mm, "end": v(256.27, 35.88) * mm});
            skLineSegment(sketch, "E2633", {"start": v(256.27, 35.88) * mm, "end": v(256.37, 35.97) * mm});
            skLineSegment(sketch, "E2634", {"start": v(256.37, 35.97) * mm, "end": v(256.47, 36.05) * mm});
            skLineSegment(sketch, "E2635", {"start": v(256.47, 36.05) * mm, "end": v(256.58, 36.12) * mm});
            skLineSegment(sketch, "E2636", {"start": v(256.58, 36.12) * mm, "end": v(256.7, 36.18) * mm});
            skLineSegment(sketch, "E2637", {"start": v(256.7, 36.18) * mm, "end": v(256.83, 36.22) * mm});
            skLineSegment(sketch, "E2638", {"start": v(256.83, 36.22) * mm, "end": v(256.97, 36.26) * mm});
            skLineSegment(sketch, "E2639", {"start": v(256.97, 36.26) * mm, "end": v(257.12, 36.28) * mm});
            skLineSegment(sketch, "E2640", {"start": v(257.12, 36.28) * mm, "end": v(257.29, 36.28) * mm});
            skLineSegment(sketch, "E2641", {"start": v(257.29, 36.28) * mm, "end": v(257.46, 36.28) * mm});
            skLineSegment(sketch, "E2642", {"start": v(257.46, 36.28) * mm, "end": v(257.65, 36.26) * mm});
            skLineSegment(sketch, "E2643", {"start": v(257.65, 36.26) * mm, "end": v(257.85, 36.22) * mm});
            skLineSegment(sketch, "E2644", {"start": v(257.85, 36.22) * mm, "end": v(258.4, 36.1) * mm});
            skLineSegment(sketch, "E2645", {"start": v(258.4, 36.1) * mm, "end": v(259.1, 35.93) * mm});
            skLineSegment(sketch, "E2646", {"start": v(259.1, 35.93) * mm, "end": v(259.92, 35.7) * mm});
            skLineSegment(sketch, "E2647", {"start": v(259.92, 35.7) * mm, "end": v(260.83, 35.43) * mm});
            skLineSegment(sketch, "E2648", {"start": v(253.37, 32.38) * mm, "end": v(253.28, 32.51) * mm});
            skLineSegment(sketch, "E2649", {"start": v(253.28, 32.51) * mm, "end": v(253.22, 32.66) * mm});
            skLineSegment(sketch, "E2650", {"start": v(253.22, 32.66) * mm, "end": v(253.13, 32.97) * mm});
            skLineSegment(sketch, "E2651", {"start": v(253.13, 32.97) * mm, "end": v(253.01, 33.42) * mm});
            skLineSegment(sketch, "E2652", {"start": v(253.01, 33.42) * mm, "end": v(252.9, 33.99) * mm});
            skLineSegment(sketch, "E2653", {"start": v(252.9, 33.99) * mm, "end": v(252.83, 34.31) * mm});
            skLineSegment(sketch, "E2654", {"start": v(252.83, 34.31) * mm, "end": v(252.78, 34.66) * mm});
            skLineSegment(sketch, "E2655", {"start": v(252.78, 34.66) * mm, "end": v(252.74, 35.02) * mm});
            skLineSegment(sketch, "E2656", {"start": v(252.74, 35.02) * mm, "end": v(252.7, 35.4) * mm});
            skLineSegment(sketch, "E2657", {"start": v(252.7, 35.4) * mm, "end": v(252.68, 35.8) * mm});
            skLineSegment(sketch, "E2658", {"start": v(252.68, 35.8) * mm, "end": v(252.67, 36.2) * mm});
            skLineSegment(sketch, "E2659", {"start": v(252.67, 36.2) * mm, "end": v(252.67, 36.6) * mm});
            skLineSegment(sketch, "E2660", {"start": v(252.67, 36.6) * mm, "end": v(252.7, 37.03) * mm});
            skLineSegment(sketch, "E2661", {"start": v(252.7, 37.03) * mm, "end": v(252.73, 37.45) * mm});
            skLineSegment(sketch, "E2662", {"start": v(252.73, 37.45) * mm, "end": v(252.8, 37.86) * mm});
            skLineSegment(sketch, "E2663", {"start": v(252.8, 37.86) * mm, "end": v(252.88, 38.28) * mm});
            skLineSegment(sketch, "E2664", {"start": v(252.88, 38.28) * mm, "end": v(253, 38.69) * mm});
            skLineSegment(sketch, "E2665", {"start": v(253, 38.69) * mm, "end": v(253.06, 38.9) * mm});
            skLineSegment(sketch, "E2666", {"start": v(253.06, 38.9) * mm, "end": v(253.14, 39.1) * mm});
            skLineSegment(sketch, "E2667", {"start": v(253.14, 39.1) * mm, "end": v(253.22, 39.29) * mm});
            skLineSegment(sketch, "E2668", {"start": v(253.22, 39.29) * mm, "end": v(253.3, 39.48) * mm});
            skLineSegment(sketch, "E2669", {"start": v(253.3, 39.48) * mm, "end": v(253.4, 39.67) * mm});
            skLineSegment(sketch, "E2670", {"start": v(253.4, 39.67) * mm, "end": v(253.5, 39.85) * mm});
            skLineSegment(sketch, "E2671", {"start": v(253.5, 39.85) * mm, "end": v(253.62, 40.04) * mm});
            skLineSegment(sketch, "E2672", {"start": v(253.62, 40.04) * mm, "end": v(253.74, 40.21) * mm});
            skLineSegment(sketch, "E2673", {"start": v(253.74, 40.21) * mm, "end": v(253.87, 40.38) * mm});
            skLineSegment(sketch, "E2674", {"start": v(253.87, 40.38) * mm, "end": v(254.01, 40.55) * mm});
            skLineSegment(sketch, "E2675", {"start": v(254.01, 40.55) * mm, "end": v(254.16, 40.7) * mm});
            skLineSegment(sketch, "E2676", {"start": v(254.16, 40.7) * mm, "end": v(254.32, 40.86) * mm});
            skLineSegment(sketch, "E2677", {"start": v(254.32, 40.86) * mm, "end": v(254.49, 41.01) * mm});
            skLineSegment(sketch, "E2678", {"start": v(254.49, 41.01) * mm, "end": v(254.67, 41.15) * mm});
            skLineSegment(sketch, "E2679", {"start": v(254.67, 41.15) * mm, "end": v(254.86, 41.29) * mm});
            skLineSegment(sketch, "E2680", {"start": v(254.86, 41.29) * mm, "end": v(255.06, 41.42) * mm});
            skLineSegment(sketch, "E2681", {"start": v(255.06, 41.42) * mm, "end": v(255.27, 41.53) * mm});
            skLineSegment(sketch, "E2682", {"start": v(255.27, 41.53) * mm, "end": v(255.5, 41.65) * mm});
            skLineSegment(sketch, "E2683", {"start": v(255.5, 41.65) * mm, "end": v(255.73, 41.75) * mm});
            skLineSegment(sketch, "E2684", {"start": v(255.73, 41.75) * mm, "end": v(255.98, 41.84) * mm});
            skLineSegment(sketch, "E2685", {"start": v(255.98, 41.84) * mm, "end": v(256.23, 41.93) * mm});
            skLineSegment(sketch, "E2686", {"start": v(256.23, 41.93) * mm, "end": v(256.5, 42) * mm});
            skLineSegment(sketch, "E2687", {"start": v(256.5, 42) * mm, "end": v(256.79, 42.07) * mm});
            skLineSegment(sketch, "E2688", {"start": v(256.79, 42.07) * mm, "end": v(257.08, 42.12) * mm});
            skLineSegment(sketch, "E2689", {"start": v(257.08, 42.12) * mm, "end": v(257.21, 42.12) * mm});
            skLineSegment(sketch, "E2690", {"start": v(257.21, 42.12) * mm, "end": v(257.46, 42.1) * mm});
            skLineSegment(sketch, "E2691", {"start": v(257.46, 42.1) * mm, "end": v(257.82, 42.03) * mm});
            skLineSegment(sketch, "E2692", {"start": v(257.82, 42.03) * mm, "end": v(258.27, 41.95) * mm});
            skLineSegment(sketch, "E2693", {"start": v(258.27, 41.95) * mm, "end": v(258.8, 41.83) * mm});
            skLineSegment(sketch, "E2694", {"start": v(258.8, 41.83) * mm, "end": v(259.42, 41.69) * mm});
            skLineSegment(sketch, "E2695", {"start": v(259.42, 41.69) * mm, "end": v(260.1, 41.51) * mm});
            skLineSegment(sketch, "E2696", {"start": v(260.1, 41.51) * mm, "end": v(260.83, 41.3) * mm});
            skLineSegment(sketch, "E2697", {"start": v(141.72, 104.17) * mm, "end": v(141.41, 103.66) * mm});
            skLineSegment(sketch, "E2698", {"start": v(141.41, 103.66) * mm, "end": v(141.09, 103.16) * mm});
            skLineSegment(sketch, "E2699", {"start": v(141.09, 103.16) * mm, "end": v(140.74, 102.66) * mm});
            skLineSegment(sketch, "E2700", {"start": v(140.74, 102.66) * mm, "end": v(140.38, 102.15) * mm});
            skLineSegment(sketch, "E2701", {"start": v(140.38, 102.15) * mm, "end": v(140, 101.66) * mm});
            skLineSegment(sketch, "E2702", {"start": v(140, 101.66) * mm, "end": v(139.63, 101.16) * mm});
            skLineSegment(sketch, "E2703", {"start": v(139.63, 101.16) * mm, "end": v(139.23, 100.68) * mm});
            skLineSegment(sketch, "E2704", {"start": v(139.23, 100.68) * mm, "end": v(138.84, 100.2) * mm});
            skLineSegment(sketch, "E2705", {"start": v(138.84, 100.2) * mm, "end": v(138.43, 99.73) * mm});
            skLineSegment(sketch, "E2706", {"start": v(138.43, 99.73) * mm, "end": v(138.03, 99.28) * mm});
            skLineSegment(sketch, "E2707", {"start": v(138.03, 99.28) * mm, "end": v(137.23, 98.41) * mm});
            skLineSegment(sketch, "E2708", {"start": v(137.23, 98.41) * mm, "end": v(136.46, 97.6) * mm});
            skLineSegment(sketch, "E2709", {"start": v(136.46, 97.6) * mm, "end": v(135.73, 96.89) * mm});
            skLineSegment(sketch, "E2710", {"start": v(135.73, 96.89) * mm, "end": v(135.05, 96.2) * mm});
            skLineSegment(sketch, "E2711", {"start": v(135.05, 96.2) * mm, "end": v(134.28, 95.4) * mm});
            skLineSegment(sketch, "E2712", {"start": v(134.28, 95.4) * mm, "end": v(133.87, 94.98) * mm});
            skLineSegment(sketch, "E2713", {"start": v(133.87, 94.98) * mm, "end": v(133.47, 94.58) * mm});
            skLineSegment(sketch, "E2714", {"start": v(133.47, 94.58) * mm, "end": v(133.06, 94.2) * mm});
            skLineSegment(sketch, "E2715", {"start": v(133.06, 94.2) * mm, "end": v(132.66, 93.85) * mm});
            skLineSegment(sketch, "E2716", {"start": v(132.66, 93.85) * mm, "end": v(132.47, 93.7) * mm});
            skLineSegment(sketch, "E2717", {"start": v(132.47, 93.7) * mm, "end": v(132.28, 93.55) * mm});
            skLineSegment(sketch, "E2718", {"start": v(132.28, 93.55) * mm, "end": v(132.09, 93.42) * mm});
            skLineSegment(sketch, "E2719", {"start": v(132.09, 93.42) * mm, "end": v(131.9, 93.3) * mm});
            skLineSegment(sketch, "E2720", {"start": v(131.9, 93.3) * mm, "end": v(131.73, 93.2) * mm});
            skLineSegment(sketch, "E2721", {"start": v(131.73, 93.2) * mm, "end": v(131.56, 93.13) * mm});
            skLineSegment(sketch, "E2722", {"start": v(131.56, 93.13) * mm, "end": v(131.4, 93.07) * mm});
            skLineSegment(sketch, "E2723", {"start": v(131.4, 93.07) * mm, "end": v(131.25, 93.03) * mm});
            skLineSegment(sketch, "E2724", {"start": v(131.25, 93.03) * mm, "end": v(131.1, 93.02) * mm});
            skLineSegment(sketch, "E2725", {"start": v(131.1, 93.02) * mm, "end": v(130.97, 93.03) * mm});
            skLineSegment(sketch, "E2726", {"start": v(130.97, 93.03) * mm, "end": v(130.84, 93.07) * mm});
            skLineSegment(sketch, "E2727", {"start": v(130.84, 93.07) * mm, "end": v(130.78, 93.1) * mm});
            skLineSegment(sketch, "E2728", {"start": v(130.78, 93.1) * mm, "end": v(130.73, 93.14) * mm});
            skLineSegment(sketch, "E2729", {"start": v(130.73, 93.14) * mm, "end": v(130.68, 93.18) * mm});
            skLineSegment(sketch, "E2730", {"start": v(130.68, 93.18) * mm, "end": v(130.63, 93.23) * mm});
            skLineSegment(sketch, "E2731", {"start": v(130.63, 93.23) * mm, "end": v(130.54, 93.36) * mm});
            skLineSegment(sketch, "E2732", {"start": v(130.54, 93.36) * mm, "end": v(130.46, 93.52) * mm});
            skLineSegment(sketch, "E2733", {"start": v(130.46, 93.52) * mm, "end": v(130.4, 93.71) * mm});
            skLineSegment(sketch, "E2734", {"start": v(130.4, 93.71) * mm, "end": v(130.35, 93.85) * mm});
            skLineSegment(sketch, "E2735", {"start": v(130.35, 93.85) * mm, "end": v(130.3, 93.99) * mm});
            skLineSegment(sketch, "E2736", {"start": v(130.3, 93.99) * mm, "end": v(130.18, 94.26) * mm});
            skLineSegment(sketch, "E2737", {"start": v(130.18, 94.26) * mm, "end": v(130.01, 94.54) * mm});
            skLineSegment(sketch, "E2738", {"start": v(130.01, 94.54) * mm, "end": v(129.82, 94.82) * mm});
            skLineSegment(sketch, "E2739", {"start": v(129.82, 94.82) * mm, "end": v(129.6, 95.1) * mm});
            skLineSegment(sketch, "E2740", {"start": v(129.6, 95.1) * mm, "end": v(129.36, 95.38) * mm});
            skLineSegment(sketch, "E2741", {"start": v(129.36, 95.38) * mm, "end": v(129.1, 95.67) * mm});
            skLineSegment(sketch, "E2742", {"start": v(129.1, 95.67) * mm, "end": v(128.82, 95.96) * mm});
            skLineSegment(sketch, "E2743", {"start": v(128.82, 95.96) * mm, "end": v(128.22, 96.55) * mm});
            skLineSegment(sketch, "E2744", {"start": v(128.22, 96.55) * mm, "end": v(127.58, 97.15) * mm});
            skLineSegment(sketch, "E2745", {"start": v(127.58, 97.15) * mm, "end": v(126.93, 97.77) * mm});
            skLineSegment(sketch, "E2746", {"start": v(126.93, 97.77) * mm, "end": v(126.61, 98.09) * mm});
            skLineSegment(sketch, "E2747", {"start": v(126.61, 98.09) * mm, "end": v(126.3, 98.4) * mm});
            skLineSegment(sketch, "E2748", {"start": v(126.3, 98.4) * mm, "end": v(126, 98.73) * mm});
            skLineSegment(sketch, "E2749", {"start": v(126, 98.73) * mm, "end": v(125.7, 99.05) * mm});
            skLineSegment(sketch, "E2750", {"start": v(125.7, 99.05) * mm, "end": v(125.43, 99.39) * mm});
            skLineSegment(sketch, "E2751", {"start": v(125.43, 99.39) * mm, "end": v(125.17, 99.72) * mm});
            skLineSegment(sketch, "E2752", {"start": v(125.17, 99.72) * mm, "end": v(124.94, 100.06) * mm});
            skLineSegment(sketch, "E2753", {"start": v(124.94, 100.06) * mm, "end": v(124.73, 100.4) * mm});
            skLineSegment(sketch, "E2754", {"start": v(124.73, 100.4) * mm, "end": v(124.54, 100.76) * mm});
            skLineSegment(sketch, "E2755", {"start": v(124.54, 100.76) * mm, "end": v(124.46, 100.94) * mm});
            skLineSegment(sketch, "E2756", {"start": v(124.46, 100.94) * mm, "end": v(124.4, 101.12) * mm});
            skLineSegment(sketch, "E2757", {"start": v(124.4, 101.12) * mm, "end": v(124.33, 101.3) * mm});
            skLineSegment(sketch, "E2758", {"start": v(124.33, 101.3) * mm, "end": v(124.27, 101.48) * mm});
            skLineSegment(sketch, "E2759", {"start": v(124.27, 101.48) * mm, "end": v(124.23, 101.66) * mm});
            skLineSegment(sketch, "E2760", {"start": v(124.23, 101.66) * mm, "end": v(124.2, 101.84) * mm});
            skLineSegment(sketch, "E2761", {"start": v(124.2, 101.84) * mm, "end": v(124.17, 102.03) * mm});
            skLineSegment(sketch, "E2762", {"start": v(124.17, 102.03) * mm, "end": v(124.15, 102.22) * mm});
            skLineSegment(sketch, "E2763", {"start": v(124.15, 102.22) * mm, "end": v(124.15, 102.4) * mm});
            skLineSegment(sketch, "E2764", {"start": v(124.15, 102.4) * mm, "end": v(124.16, 102.6) * mm});
            skLineSegment(sketch, "E2765", {"start": v(124.16, 102.6) * mm, "end": v(124.17, 102.79) * mm});
            skLineSegment(sketch, "E2766", {"start": v(124.17, 102.79) * mm, "end": v(124.2, 102.98) * mm});
            skLineSegment(sketch, "E2767", {"start": v(124.2, 102.98) * mm, "end": v(124.25, 103.17) * mm});
            skLineSegment(sketch, "E2768", {"start": v(124.25, 103.17) * mm, "end": v(124.3, 103.37) * mm});
            skLineSegment(sketch, "E2769", {"start": v(124.3, 103.37) * mm, "end": v(124.37, 103.57) * mm});
            skLineSegment(sketch, "E2770", {"start": v(124.37, 103.57) * mm, "end": v(124.45, 103.77) * mm});
            skLineSegment(sketch, "E2771", {"start": v(124.45, 103.77) * mm, "end": v(124.55, 103.97) * mm});
            skLineSegment(sketch, "E2772", {"start": v(124.55, 103.97) * mm, "end": v(124.66, 104.17) * mm});
            skLineSegment(sketch, "E2773", {"start": v(142.53, 102.03) * mm, "end": v(142.4, 101.92) * mm});
            skLineSegment(sketch, "E2774", {"start": v(142.4, 101.92) * mm, "end": v(142.23, 101.8) * mm});
            skLineSegment(sketch, "E2775", {"start": v(142.23, 101.8) * mm, "end": v(142.01, 101.67) * mm});
            skLineSegment(sketch, "E2776", {"start": v(142.01, 101.67) * mm, "end": v(141.77, 101.54) * mm});
            skLineSegment(sketch, "E2777", {"start": v(141.77, 101.54) * mm, "end": v(141.48, 101.4) * mm});
            skLineSegment(sketch, "E2778", {"start": v(141.48, 101.4) * mm, "end": v(141.17, 101.26) * mm});
            skLineSegment(sketch, "E2779", {"start": v(141.17, 101.26) * mm, "end": v(140.46, 100.96) * mm});
            skLineSegment(sketch, "E2780", {"start": v(140.46, 100.96) * mm, "end": v(139.65, 100.64) * mm});
            skLineSegment(sketch, "E2781", {"start": v(139.65, 100.64) * mm, "end": v(138.78, 100.33) * mm});
            skLineSegment(sketch, "E2782", {"start": v(138.78, 100.33) * mm, "end": v(137.86, 100.02) * mm});
            skLineSegment(sketch, "E2783", {"start": v(137.86, 100.02) * mm, "end": v(136.9, 99.72) * mm});
            skLineSegment(sketch, "E2784", {"start": v(136.9, 99.72) * mm, "end": v(135.96, 99.44) * mm});
            skLineSegment(sketch, "E2785", {"start": v(135.96, 99.44) * mm, "end": v(135.02, 99.2) * mm});
            skLineSegment(sketch, "E2786", {"start": v(135.02, 99.2) * mm, "end": v(134.13, 98.98) * mm});
            skLineSegment(sketch, "E2787", {"start": v(134.13, 98.98) * mm, "end": v(133.7, 98.88) * mm});
            skLineSegment(sketch, "E2788", {"start": v(133.7, 98.88) * mm, "end": v(133.3, 98.8) * mm});
            skLineSegment(sketch, "E2789", {"start": v(133.3, 98.8) * mm, "end": v(132.91, 98.74) * mm});
            skLineSegment(sketch, "E2790", {"start": v(132.91, 98.74) * mm, "end": v(132.55, 98.68) * mm});
            skLineSegment(sketch, "E2791", {"start": v(132.55, 98.68) * mm, "end": v(132.22, 98.64) * mm});
            skLineSegment(sketch, "E2792", {"start": v(132.22, 98.64) * mm, "end": v(131.91, 98.62) * mm});
            skLineSegment(sketch, "E2793", {"start": v(131.91, 98.62) * mm, "end": v(131.64, 98.6) * mm});
            skLineSegment(sketch, "E2794", {"start": v(131.64, 98.6) * mm, "end": v(131.4, 98.61) * mm});
            skLineSegment(sketch, "E2795", {"start": v(131.4, 98.61) * mm, "end": v(131.2, 98.64) * mm});
            skLineSegment(sketch, "E2796", {"start": v(131.2, 98.64) * mm, "end": v(131.12, 98.66) * mm});
            skLineSegment(sketch, "E2797", {"start": v(131.12, 98.66) * mm, "end": v(131.04, 98.69) * mm});
            skLineSegment(sketch, "E2798", {"start": v(131.04, 98.69) * mm, "end": v(130.56, 98.86) * mm});
            skLineSegment(sketch, "E2799", {"start": v(130.56, 98.86) * mm, "end": v(129.97, 99.06) * mm});
            skLineSegment(sketch, "E2800", {"start": v(129.97, 99.06) * mm, "end": v(128.56, 99.51) * mm});
            skLineSegment(sketch, "E2801", {"start": v(128.56, 99.51) * mm, "end": v(127.77, 99.77) * mm});
            skLineSegment(sketch, "E2802", {"start": v(127.77, 99.77) * mm, "end": v(126.95, 100.05) * mm});
            skLineSegment(sketch, "E2803", {"start": v(126.95, 100.05) * mm, "end": v(126.1, 100.35) * mm});
            skLineSegment(sketch, "E2804", {"start": v(126.1, 100.35) * mm, "end": v(125.27, 100.68) * mm});
            skLineSegment(sketch, "E2805", {"start": v(125.27, 100.68) * mm, "end": v(124.86, 100.85) * mm});
            skLineSegment(sketch, "E2806", {"start": v(124.86, 100.85) * mm, "end": v(124.45, 101.03) * mm});
            skLineSegment(sketch, "E2807", {"start": v(124.45, 101.03) * mm, "end": v(124.06, 101.22) * mm});
            skLineSegment(sketch, "E2808", {"start": v(124.06, 101.22) * mm, "end": v(123.67, 101.4) * mm});
            skLineSegment(sketch, "E2809", {"start": v(123.67, 101.4) * mm, "end": v(123.3, 101.61) * mm});
            skLineSegment(sketch, "E2810", {"start": v(123.3, 101.61) * mm, "end": v(122.95, 101.82) * mm});
            skLineSegment(sketch, "E2811", {"start": v(122.95, 101.82) * mm, "end": v(122.61, 102.03) * mm});
            skLineSegment(sketch, "E2812", {"start": v(122.61, 102.03) * mm, "end": v(122.3, 102.26) * mm});
            skLineSegment(sketch, "E2813", {"start": v(122.3, 102.26) * mm, "end": v(122, 102.49) * mm});
            skLineSegment(sketch, "E2814", {"start": v(122, 102.49) * mm, "end": v(121.74, 102.72) * mm});
            skLineSegment(sketch, "E2815", {"start": v(121.74, 102.72) * mm, "end": v(121.5, 102.97) * mm});
            skLineSegment(sketch, "E2816", {"start": v(121.5, 102.97) * mm, "end": v(121.28, 103.22) * mm});
            skLineSegment(sketch, "E2817", {"start": v(121.28, 103.22) * mm, "end": v(121.2, 103.35) * mm});
            skLineSegment(sketch, "E2818", {"start": v(121.2, 103.35) * mm, "end": v(121.1, 103.49) * mm});
            skLineSegment(sketch, "E2819", {"start": v(121.1, 103.49) * mm, "end": v(121.03, 103.62) * mm});
            skLineSegment(sketch, "E2820", {"start": v(121.03, 103.62) * mm, "end": v(120.96, 103.76) * mm});
            skLineSegment(sketch, "E2821", {"start": v(120.96, 103.76) * mm, "end": v(120.9, 103.9) * mm});
            skLineSegment(sketch, "E2822", {"start": v(120.9, 103.9) * mm, "end": v(120.85, 104.04) * mm});
            skLineSegment(sketch, "E2823", {"start": v(120.85, 104.04) * mm, "end": v(120.8, 104.18) * mm});
            skLineSegment(sketch, "E2824", {"start": v(120.8, 104.18) * mm, "end": v(120.77, 104.32) * mm});
            skLineSegment(sketch, "E2825", {"start": v(173.76, 32.38) * mm, "end": v(174.26, 32.92) * mm});
            skLineSegment(sketch, "E2826", {"start": v(174.26, 32.92) * mm, "end": v(174.79, 33.43) * mm});
            skLineSegment(sketch, "E2827", {"start": v(174.79, 33.43) * mm, "end": v(175.05, 33.67) * mm});
            skLineSegment(sketch, "E2828", {"start": v(175.05, 33.67) * mm, "end": v(175.32, 33.91) * mm});
            skLineSegment(sketch, "E2829", {"start": v(175.32, 33.91) * mm, "end": v(175.6, 34.14) * mm});
            skLineSegment(sketch, "E2830", {"start": v(175.6, 34.14) * mm, "end": v(175.87, 34.36) * mm});
            skLineSegment(sketch, "E2831", {"start": v(175.87, 34.36) * mm, "end": v(176.14, 34.58) * mm});
            skLineSegment(sketch, "E2832", {"start": v(176.14, 34.58) * mm, "end": v(176.42, 34.78) * mm});
            skLineSegment(sketch, "E2833", {"start": v(176.42, 34.78) * mm, "end": v(176.7, 34.98) * mm});
            skLineSegment(sketch, "E2834", {"start": v(176.7, 34.98) * mm, "end": v(176.99, 35.17) * mm});
            skLineSegment(sketch, "E2835", {"start": v(176.99, 35.17) * mm, "end": v(177.27, 35.34) * mm});
            skLineSegment(sketch, "E2836", {"start": v(177.27, 35.34) * mm, "end": v(177.56, 35.51) * mm});
            skLineSegment(sketch, "E2837", {"start": v(177.56, 35.51) * mm, "end": v(177.85, 35.67) * mm});
            skLineSegment(sketch, "E2838", {"start": v(177.85, 35.67) * mm, "end": v(178.13, 35.82) * mm});
            skLineSegment(sketch, "E2839", {"start": v(178.13, 35.82) * mm, "end": v(178.43, 35.96) * mm});
            skLineSegment(sketch, "E2840", {"start": v(178.43, 35.96) * mm, "end": v(178.72, 36.08) * mm});
            skLineSegment(sketch, "E2841", {"start": v(178.72, 36.08) * mm, "end": v(179.01, 36.2) * mm});
            skLineSegment(sketch, "E2842", {"start": v(179.01, 36.2) * mm, "end": v(179.3, 36.3) * mm});
            skLineSegment(sketch, "E2843", {"start": v(179.3, 36.3) * mm, "end": v(179.6, 36.4) * mm});
            skLineSegment(sketch, "E2844", {"start": v(179.6, 36.4) * mm, "end": v(179.9, 36.48) * mm});
            skLineSegment(sketch, "E2845", {"start": v(179.9, 36.48) * mm, "end": v(180.2, 36.55) * mm});
            skLineSegment(sketch, "E2846", {"start": v(180.2, 36.55) * mm, "end": v(180.49, 36.6) * mm});
            skLineSegment(sketch, "E2847", {"start": v(180.49, 36.6) * mm, "end": v(180.78, 36.65) * mm});
            skLineSegment(sketch, "E2848", {"start": v(180.78, 36.65) * mm, "end": v(181.08, 36.68) * mm});
            skLineSegment(sketch, "E2849", {"start": v(181.08, 36.68) * mm, "end": v(181.38, 36.7) * mm});
            skLineSegment(sketch, "E2850", {"start": v(181.38, 36.7) * mm, "end": v(181.67, 36.71) * mm});
            skLineSegment(sketch, "E2851", {"start": v(181.67, 36.71) * mm, "end": v(181.97, 36.7) * mm});
            skLineSegment(sketch, "E2852", {"start": v(181.97, 36.7) * mm, "end": v(182.26, 36.68) * mm});
            skLineSegment(sketch, "E2853", {"start": v(182.26, 36.68) * mm, "end": v(182.55, 36.65) * mm});
            skLineSegment(sketch, "E2854", {"start": v(182.55, 36.65) * mm, "end": v(182.85, 36.6) * mm});
            skLineSegment(sketch, "E2855", {"start": v(182.85, 36.6) * mm, "end": v(183.1, 36.55) * mm});
            skLineSegment(sketch, "E2856", {"start": v(183.1, 36.55) * mm, "end": v(183.34, 36.49) * mm});
            skLineSegment(sketch, "E2857", {"start": v(183.34, 36.49) * mm, "end": v(183.58, 36.42) * mm});
            skLineSegment(sketch, "E2858", {"start": v(183.58, 36.42) * mm, "end": v(183.8, 36.35) * mm});
            skLineSegment(sketch, "E2859", {"start": v(183.8, 36.35) * mm, "end": v(184.02, 36.27) * mm});
            skLineSegment(sketch, "E2860", {"start": v(184.02, 36.27) * mm, "end": v(184.23, 36.19) * mm});
            skLineSegment(sketch, "E2861", {"start": v(184.23, 36.19) * mm, "end": v(184.43, 36.1) * mm});
            skLineSegment(sketch, "E2862", {"start": v(184.43, 36.1) * mm, "end": v(184.62, 36) * mm});
            skLineSegment(sketch, "E2863", {"start": v(184.62, 36) * mm, "end": v(184.8, 35.9) * mm});
            skLineSegment(sketch, "E2864", {"start": v(184.8, 35.9) * mm, "end": v(184.99, 35.8) * mm});
            skLineSegment(sketch, "E2865", {"start": v(184.99, 35.8) * mm, "end": v(185.15, 35.68) * mm});
            skLineSegment(sketch, "E2866", {"start": v(185.15, 35.68) * mm, "end": v(185.32, 35.57) * mm});
            skLineSegment(sketch, "E2867", {"start": v(185.32, 35.57) * mm, "end": v(185.47, 35.45) * mm});
            skLineSegment(sketch, "E2868", {"start": v(185.47, 35.45) * mm, "end": v(185.62, 35.32) * mm});
            skLineSegment(sketch, "E2869", {"start": v(185.62, 35.32) * mm, "end": v(185.76, 35.19) * mm});
            skLineSegment(sketch, "E2870", {"start": v(185.76, 35.19) * mm, "end": v(185.9, 35.05) * mm});
            skLineSegment(sketch, "E2871", {"start": v(185.9, 35.05) * mm, "end": v(186.14, 34.77) * mm});
            skLineSegment(sketch, "E2872", {"start": v(186.14, 34.77) * mm, "end": v(186.37, 34.47) * mm});
            skLineSegment(sketch, "E2873", {"start": v(186.37, 34.47) * mm, "end": v(186.58, 34.15) * mm});
            skLineSegment(sketch, "E2874", {"start": v(186.58, 34.15) * mm, "end": v(186.76, 33.82) * mm});
            skLineSegment(sketch, "E2875", {"start": v(186.76, 33.82) * mm, "end": v(186.93, 33.48) * mm});
            skLineSegment(sketch, "E2876", {"start": v(186.93, 33.48) * mm, "end": v(187.08, 33.12) * mm});
            skLineSegment(sketch, "E2877", {"start": v(187.08, 33.12) * mm, "end": v(187.21, 32.75) * mm});
            skLineSegment(sketch, "E2878", {"start": v(187.21, 32.75) * mm, "end": v(187.33, 32.38) * mm});
            skLineSegment(sketch, "E2879", {"start": v(76.1, 104.17) * mm, "end": v(76.15, 103.84) * mm});
            skLineSegment(sketch, "E2880", {"start": v(76.15, 103.84) * mm, "end": v(76.17, 103.52) * mm});
            skLineSegment(sketch, "E2881", {"start": v(76.17, 103.52) * mm, "end": v(76.17, 103.36) * mm});
            skLineSegment(sketch, "E2882", {"start": v(76.17, 103.36) * mm, "end": v(76.16, 103.2) * mm});
            skLineSegment(sketch, "E2883", {"start": v(76.16, 103.2) * mm, "end": v(76.14, 103.05) * mm});
            skLineSegment(sketch, "E2884", {"start": v(76.14, 103.05) * mm, "end": v(76.12, 102.9) * mm});
            skLineSegment(sketch, "E2885", {"start": v(76.12, 102.9) * mm, "end": v(76.08, 102.74) * mm});
            skLineSegment(sketch, "E2886", {"start": v(76.08, 102.74) * mm, "end": v(76.04, 102.6) * mm});
            skLineSegment(sketch, "E2887", {"start": v(76.04, 102.6) * mm, "end": v(75.99, 102.45) * mm});
            skLineSegment(sketch, "E2888", {"start": v(75.99, 102.45) * mm, "end": v(75.93, 102.3) * mm});
            skLineSegment(sketch, "E2889", {"start": v(75.93, 102.3) * mm, "end": v(75.86, 102.16) * mm});
            skLineSegment(sketch, "E2890", {"start": v(75.86, 102.16) * mm, "end": v(75.79, 102.02) * mm});
            skLineSegment(sketch, "E2891", {"start": v(75.79, 102.02) * mm, "end": v(75.7, 101.88) * mm});
            skLineSegment(sketch, "E2892", {"start": v(75.7, 101.88) * mm, "end": v(75.6, 101.75) * mm});
            skLineSegment(sketch, "E2893", {"start": v(75.6, 101.75) * mm, "end": v(75.5, 101.61) * mm});
            skLineSegment(sketch, "E2894", {"start": v(75.5, 101.61) * mm, "end": v(75.38, 101.48) * mm});
            skLineSegment(sketch, "E2895", {"start": v(75.38, 101.48) * mm, "end": v(75.26, 101.36) * mm});
            skLineSegment(sketch, "E2896", {"start": v(75.26, 101.36) * mm, "end": v(75.13, 101.24) * mm});
            skLineSegment(sketch, "E2897", {"start": v(75.13, 101.24) * mm, "end": v(74.98, 101.12) * mm});
            skLineSegment(sketch, "E2898", {"start": v(74.98, 101.12) * mm, "end": v(74.83, 101.01) * mm});
            skLineSegment(sketch, "E2899", {"start": v(74.83, 101.01) * mm, "end": v(74.68, 100.9) * mm});
            skLineSegment(sketch, "E2900", {"start": v(74.68, 100.9) * mm, "end": v(74.51, 100.8) * mm});
            skLineSegment(sketch, "E2901", {"start": v(74.51, 100.8) * mm, "end": v(74.16, 100.6) * mm});
            skLineSegment(sketch, "E2902", {"start": v(74.16, 100.6) * mm, "end": v(73.78, 100.43) * mm});
            skLineSegment(sketch, "E2903", {"start": v(73.78, 100.43) * mm, "end": v(73.38, 100.27) * mm});
            skLineSegment(sketch, "E2904", {"start": v(73.38, 100.27) * mm, "end": v(72.95, 100.12) * mm});
            skLineSegment(sketch, "E2905", {"start": v(72.95, 100.12) * mm, "end": v(72.5, 100) * mm});
            skLineSegment(sketch, "E2906", {"start": v(72.5, 100) * mm, "end": v(72.03, 99.87) * mm});
            skLineSegment(sketch, "E2907", {"start": v(72.03, 99.87) * mm, "end": v(71.55, 99.77) * mm});
            skLineSegment(sketch, "E2908", {"start": v(71.55, 99.77) * mm, "end": v(71.05, 99.68) * mm});
            skLineSegment(sketch, "E2909", {"start": v(71.05, 99.68) * mm, "end": v(70.54, 99.6) * mm});
            skLineSegment(sketch, "E2910", {"start": v(70.54, 99.6) * mm, "end": v(70.02, 99.54) * mm});
            skLineSegment(sketch, "E2911", {"start": v(70.02, 99.54) * mm, "end": v(69.49, 99.49) * mm});
            skLineSegment(sketch, "E2912", {"start": v(69.49, 99.49) * mm, "end": v(68.95, 99.44) * mm});
            skLineSegment(sketch, "E2913", {"start": v(68.95, 99.44) * mm, "end": v(68.4, 99.41) * mm});
            skLineSegment(sketch, "E2914", {"start": v(68.4, 99.41) * mm, "end": v(67.87, 99.4) * mm});
            skLineSegment(sketch, "E2915", {"start": v(67.87, 99.4) * mm, "end": v(67.33, 99.38) * mm});
            skLineSegment(sketch, "E2916", {"start": v(67.33, 99.38) * mm, "end": v(66.79, 99.38) * mm});
            skLineSegment(sketch, "E2917", {"start": v(66.79, 99.38) * mm, "end": v(66.25, 99.39) * mm});
            skLineSegment(sketch, "E2918", {"start": v(66.25, 99.39) * mm, "end": v(65.72, 99.4) * mm});
            skLineSegment(sketch, "E2919", {"start": v(65.72, 99.4) * mm, "end": v(65.2, 99.42) * mm});
            skLineSegment(sketch, "E2920", {"start": v(65.2, 99.42) * mm, "end": v(64.7, 99.45) * mm});
            skLineSegment(sketch, "E2921", {"start": v(64.7, 99.45) * mm, "end": v(63.72, 99.53) * mm});
            skLineSegment(sketch, "E2922", {"start": v(63.72, 99.53) * mm, "end": v(62.8, 99.64) * mm});
            skLineSegment(sketch, "E2923", {"start": v(62.8, 99.64) * mm, "end": v(62.38, 99.7) * mm});
            skLineSegment(sketch, "E2924", {"start": v(62.38, 99.7) * mm, "end": v(61.98, 99.76) * mm});
            skLineSegment(sketch, "E2925", {"start": v(61.98, 99.76) * mm, "end": v(61.6, 99.83) * mm});
            skLineSegment(sketch, "E2926", {"start": v(61.6, 99.83) * mm, "end": v(61.26, 99.9) * mm});
            skLineSegment(sketch, "E2927", {"start": v(61.26, 99.9) * mm, "end": v(61.1, 99.92) * mm});
            skLineSegment(sketch, "E2928", {"start": v(61.1, 99.92) * mm, "end": v(60.9, 99.94) * mm});
            skLineSegment(sketch, "E2929", {"start": v(60.9, 99.94) * mm, "end": v(60.66, 99.95) * mm});
            skLineSegment(sketch, "E2930", {"start": v(60.66, 99.95) * mm, "end": v(60.4, 99.96) * mm});
            skLineSegment(sketch, "E2931", {"start": v(60.4, 99.96) * mm, "end": v(59.78, 99.95) * mm});
            skLineSegment(sketch, "E2932", {"start": v(59.78, 99.95) * mm, "end": v(59.06, 99.91) * mm});
            skLineSegment(sketch, "E2933", {"start": v(59.06, 99.91) * mm, "end": v(57.42, 99.8) * mm});
            skLineSegment(sketch, "E2934", {"start": v(57.42, 99.8) * mm, "end": v(55.63, 99.66) * mm});
            skLineSegment(sketch, "E2935", {"start": v(55.63, 99.66) * mm, "end": v(54.72, 99.6) * mm});
            skLineSegment(sketch, "E2936", {"start": v(54.72, 99.6) * mm, "end": v(53.84, 99.54) * mm});
            skLineSegment(sketch, "E2937", {"start": v(53.84, 99.54) * mm, "end": v(53, 99.49) * mm});
            skLineSegment(sketch, "E2938", {"start": v(53, 99.49) * mm, "end": v(52.2, 99.46) * mm});
            skLineSegment(sketch, "E2939", {"start": v(52.2, 99.46) * mm, "end": v(51.5, 99.46) * mm});
            skLineSegment(sketch, "E2940", {"start": v(51.5, 99.46) * mm, "end": v(51.19, 99.46) * mm});
            skLineSegment(sketch, "E2941", {"start": v(51.19, 99.46) * mm, "end": v(50.9, 99.48) * mm});
            skLineSegment(sketch, "E2942", {"start": v(50.9, 99.48) * mm, "end": v(50.64, 99.5) * mm});
            skLineSegment(sketch, "E2943", {"start": v(50.64, 99.5) * mm, "end": v(50.4, 99.53) * mm});
            skLineSegment(sketch, "E2944", {"start": v(50.4, 99.53) * mm, "end": v(50.21, 99.57) * mm});
            skLineSegment(sketch, "E2945", {"start": v(50.21, 99.57) * mm, "end": v(50.06, 99.62) * mm});
            skLineSegment(sketch, "E2946", {"start": v(50.06, 99.62) * mm, "end": v(49.77, 99.74) * mm});
            skLineSegment(sketch, "E2947", {"start": v(49.77, 99.74) * mm, "end": v(49.5, 99.87) * mm});
            skLineSegment(sketch, "E2948", {"start": v(49.5, 99.87) * mm, "end": v(49.25, 100) * mm});
            skLineSegment(sketch, "E2949", {"start": v(49.25, 100) * mm, "end": v(49.02, 100.12) * mm});
            skLineSegment(sketch, "E2950", {"start": v(49.02, 100.12) * mm, "end": v(48.8, 100.25) * mm});
            skLineSegment(sketch, "E2951", {"start": v(48.8, 100.25) * mm, "end": v(48.6, 100.38) * mm});
            skLineSegment(sketch, "E2952", {"start": v(48.6, 100.38) * mm, "end": v(48.42, 100.5) * mm});
            skLineSegment(sketch, "E2953", {"start": v(48.42, 100.5) * mm, "end": v(48.25, 100.64) * mm});
            skLineSegment(sketch, "E2954", {"start": v(48.25, 100.64) * mm, "end": v(48.1, 100.78) * mm});
            skLineSegment(sketch, "E2955", {"start": v(48.1, 100.78) * mm, "end": v(47.96, 100.91) * mm});
            skLineSegment(sketch, "E2956", {"start": v(47.96, 100.91) * mm, "end": v(47.84, 101.05) * mm});
            skLineSegment(sketch, "E2957", {"start": v(47.84, 101.05) * mm, "end": v(47.73, 101.19) * mm});
            skLineSegment(sketch, "E2958", {"start": v(47.73, 101.19) * mm, "end": v(47.64, 101.33) * mm});
            skLineSegment(sketch, "E2959", {"start": v(47.64, 101.33) * mm, "end": v(47.56, 101.47) * mm});
            skLineSegment(sketch, "E2960", {"start": v(47.56, 101.47) * mm, "end": v(47.5, 101.62) * mm});
            skLineSegment(sketch, "E2961", {"start": v(47.5, 101.62) * mm, "end": v(47.44, 101.76) * mm});
            skLineSegment(sketch, "E2962", {"start": v(47.44, 101.76) * mm, "end": v(47.4, 101.9) * mm});
            skLineSegment(sketch, "E2963", {"start": v(47.4, 101.9) * mm, "end": v(47.38, 102.05) * mm});
            skLineSegment(sketch, "E2964", {"start": v(47.38, 102.05) * mm, "end": v(47.37, 102.2) * mm});
            skLineSegment(sketch, "E2965", {"start": v(47.37, 102.2) * mm, "end": v(47.37, 102.35) * mm});
            skLineSegment(sketch, "E2966", {"start": v(47.37, 102.35) * mm, "end": v(47.39, 102.5) * mm});
            skLineSegment(sketch, "E2967", {"start": v(47.39, 102.5) * mm, "end": v(47.42, 102.65) * mm});
            skLineSegment(sketch, "E2968", {"start": v(47.42, 102.65) * mm, "end": v(47.46, 102.8) * mm});
            skLineSegment(sketch, "E2969", {"start": v(47.46, 102.8) * mm, "end": v(47.5, 102.95) * mm});
            skLineSegment(sketch, "E2970", {"start": v(47.5, 102.95) * mm, "end": v(47.57, 103.1) * mm});
            skLineSegment(sketch, "E2971", {"start": v(47.57, 103.1) * mm, "end": v(47.64, 103.25) * mm});
            skLineSegment(sketch, "E2972", {"start": v(47.64, 103.25) * mm, "end": v(47.73, 103.4) * mm});
            skLineSegment(sketch, "E2973", {"start": v(47.73, 103.4) * mm, "end": v(47.83, 103.56) * mm});
            skLineSegment(sketch, "E2974", {"start": v(47.83, 103.56) * mm, "end": v(47.94, 103.7) * mm});
            skLineSegment(sketch, "E2975", {"start": v(47.94, 103.7) * mm, "end": v(48.05, 103.86) * mm});
            skLineSegment(sketch, "E2976", {"start": v(48.05, 103.86) * mm, "end": v(48.32, 104.17) * mm});
            skLineSegment(sketch, "E2977", {"start": v(5.1, 104.17) * mm, "end": v(4.96, 103.17) * mm});
            skLineSegment(sketch, "E2978", {"start": v(4.96, 103.17) * mm, "end": v(4.82, 102.36) * mm});
            skLineSegment(sketch, "E2979", {"start": v(4.82, 102.36) * mm, "end": v(4.72, 101.8) * mm});
            skLineSegment(sketch, "E2980", {"start": v(4.72, 101.8) * mm, "end": v(4.67, 101.57) * mm});
            skLineSegment(sketch, "E2981", {"start": v(4.67, 101.57) * mm, "end": v(4.6, 101.3) * mm});
            skLineSegment(sketch, "E2982", {"start": v(4.6, 101.3) * mm, "end": v(4.5, 101.03) * mm});
            skLineSegment(sketch, "E2983", {"start": v(4.5, 101.03) * mm, "end": v(4.38, 100.78) * mm});
            skLineSegment(sketch, "E2984", {"start": v(4.38, 100.78) * mm, "end": v(4.24, 100.54) * mm});
            skLineSegment(sketch, "E2985", {"start": v(4.24, 100.54) * mm, "end": v(4.08, 100.31) * mm});
            skLineSegment(sketch, "E2986", {"start": v(4.08, 100.31) * mm, "end": v(3.9, 100.1) * mm});
            skLineSegment(sketch, "E2987", {"start": v(3.9, 100.1) * mm, "end": v(3.7, 99.89) * mm});
            skLineSegment(sketch, "E2988", {"start": v(3.7, 99.89) * mm, "end": v(3.5, 99.7) * mm});
            skLineSegment(sketch, "E2989", {"start": v(3.5, 99.7) * mm, "end": v(3.27, 99.5) * mm});
            skLineSegment(sketch, "E2990", {"start": v(3.27, 99.5) * mm, "end": v(3.02, 99.33) * mm});
            skLineSegment(sketch, "E2991", {"start": v(3.02, 99.33) * mm, "end": v(2.76, 99.17) * mm});
            skLineSegment(sketch, "E2992", {"start": v(2.76, 99.17) * mm, "end": v(2.5, 99.02) * mm});
            skLineSegment(sketch, "E2993", {"start": v(2.5, 99.02) * mm, "end": v(2.2, 98.88) * mm});
            skLineSegment(sketch, "E2994", {"start": v(2.2, 98.88) * mm, "end": v(1.92, 98.75) * mm});
            skLineSegment(sketch, "E2995", {"start": v(1.92, 98.75) * mm, "end": v(1.6, 98.64) * mm});
            skLineSegment(sketch, "E2996", {"start": v(1.6, 98.64) * mm, "end": v(1.3, 98.53) * mm});
            skLineSegment(sketch, "E2997", {"start": v(7.04, 104.17) * mm, "end": v(7.13, 103.84) * mm});
            skLineSegment(sketch, "E2998", {"start": v(7.13, 103.84) * mm, "end": v(7.2, 103.5) * mm});
            skLineSegment(sketch, "E2999", {"start": v(7.2, 103.5) * mm, "end": v(7.22, 103.33) * mm});
            skLineSegment(sketch, "E3000", {"start": v(7.22, 103.33) * mm, "end": v(7.24, 103.17) * mm});
            skLineSegment(sketch, "E3001", {"start": v(7.24, 103.17) * mm, "end": v(7.25, 103) * mm});
            skLineSegment(sketch, "E3002", {"start": v(7.25, 103) * mm, "end": v(7.25, 102.83) * mm});
            skLineSegment(sketch, "E3003", {"start": v(7.25, 102.83) * mm, "end": v(7.22, 102.5) * mm});
            skLineSegment(sketch, "E3004", {"start": v(7.22, 102.5) * mm, "end": v(7.18, 102.18) * mm});
            skLineSegment(sketch, "E3005", {"start": v(7.18, 102.18) * mm, "end": v(7.11, 101.87) * mm});
            skLineSegment(sketch, "E3006", {"start": v(7.11, 101.87) * mm, "end": v(7.03, 101.55) * mm});
            skLineSegment(sketch, "E3007", {"start": v(7.03, 101.55) * mm, "end": v(6.94, 101.24) * mm});
            skLineSegment(sketch, "E3008", {"start": v(6.94, 101.24) * mm, "end": v(6.83, 100.93) * mm});
            skLineSegment(sketch, "E3009", {"start": v(6.83, 100.93) * mm, "end": v(6.7, 100.63) * mm});
            skLineSegment(sketch, "E3010", {"start": v(6.7, 100.63) * mm, "end": v(6.58, 100.33) * mm});
            skLineSegment(sketch, "E3011", {"start": v(6.58, 100.33) * mm, "end": v(6.5, 100.2) * mm});
            skLineSegment(sketch, "E3012", {"start": v(6.5, 100.2) * mm, "end": v(6.43, 100.06) * mm});
            skLineSegment(sketch, "E3013", {"start": v(6.43, 100.06) * mm, "end": v(6.26, 99.8) * mm});
            skLineSegment(sketch, "E3014", {"start": v(6.26, 99.8) * mm, "end": v(6.07, 99.55) * mm});
            skLineSegment(sketch, "E3015", {"start": v(6.07, 99.55) * mm, "end": v(5.86, 99.32) * mm});
            skLineSegment(sketch, "E3016", {"start": v(5.86, 99.32) * mm, "end": v(5.55, 98.95) * mm});
            skLineSegment(sketch, "E3017", {"start": v(5.55, 98.95) * mm, "end": v(5.24, 98.56) * mm});
            skLineSegment(sketch, "E3018", {"start": v(5.24, 98.56) * mm, "end": v(4.92, 98.16) * mm});
            skLineSegment(sketch, "E3019", {"start": v(4.92, 98.16) * mm, "end": v(4.75, 97.97) * mm});
            skLineSegment(sketch, "E3020", {"start": v(4.75, 97.97) * mm, "end": v(4.58, 97.78) * mm});
            skLineSegment(sketch, "E3021", {"start": v(4.58, 97.78) * mm, "end": v(4.41, 97.6) * mm});
            skLineSegment(sketch, "E3022", {"start": v(4.41, 97.6) * mm, "end": v(4.23, 97.45) * mm});
            skLineSegment(sketch, "E3023", {"start": v(4.23, 97.45) * mm, "end": v(4.05, 97.3) * mm});
            skLineSegment(sketch, "E3024", {"start": v(4.05, 97.3) * mm, "end": v(3.86, 97.18) * mm});
            skLineSegment(sketch, "E3025", {"start": v(3.86, 97.18) * mm, "end": v(3.66, 97.08) * mm});
            skLineSegment(sketch, "E3026", {"start": v(3.66, 97.08) * mm, "end": v(3.45, 97) * mm});
            skLineSegment(sketch, "E3027", {"start": v(3.45, 97) * mm, "end": v(3.34, 96.97) * mm});
            skLineSegment(sketch, "E3028", {"start": v(3.34, 96.97) * mm, "end": v(3.23, 96.95) * mm});
            skLineSegment(sketch, "E3029", {"start": v(3.23, 96.95) * mm, "end": v(3.12, 96.94) * mm});
            skLineSegment(sketch, "E3030", {"start": v(3.12, 96.94) * mm, "end": v(3, 96.93) * mm});
            skLineSegment(sketch, "E3031", {"start": v(3, 96.93) * mm, "end": v(2.59, 96.94) * mm});
            skLineSegment(sketch, "E3032", {"start": v(2.59, 96.94) * mm, "end": v(2.16, 96.98) * mm});
            skLineSegment(sketch, "E3033", {"start": v(2.16, 96.98) * mm, "end": v(1.73, 97.04) * mm});
            skLineSegment(sketch, "E3034", {"start": v(1.73, 97.04) * mm, "end": v(1.3, 97.12) * mm});
            skLineSegment(sketch, "E3035", {"start": v(9.9, 104.17) * mm, "end": v(9.9, 103.57) * mm});
            skLineSegment(sketch, "E3036", {"start": v(9.9, 103.57) * mm, "end": v(9.91, 103.01) * mm});
            skLineSegment(sketch, "E3037", {"start": v(9.91, 103.01) * mm, "end": v(9.97, 102) * mm});
            skLineSegment(sketch, "E3038", {"start": v(9.97, 102) * mm, "end": v(10, 101.55) * mm});
            skLineSegment(sketch, "E3039", {"start": v(10, 101.55) * mm, "end": v(10, 101.14) * mm});
            skLineSegment(sketch, "E3040", {"start": v(10, 101.14) * mm, "end": v(9.99, 100.95) * mm});
            skLineSegment(sketch, "E3041", {"start": v(9.99, 100.95) * mm, "end": v(9.97, 100.78) * mm});
            skLineSegment(sketch, "E3042", {"start": v(9.97, 100.78) * mm, "end": v(9.95, 100.61) * mm});
            skLineSegment(sketch, "E3043", {"start": v(9.95, 100.61) * mm, "end": v(9.91, 100.46) * mm});
            skLineSegment(sketch, "E3044", {"start": v(9.91, 100.46) * mm, "end": v(9.77, 100) * mm});
            skLineSegment(sketch, "E3045", {"start": v(9.77, 100) * mm, "end": v(9.6, 99.53) * mm});
            skLineSegment(sketch, "E3046", {"start": v(9.6, 99.53) * mm, "end": v(9.4, 98.97) * mm});
            skLineSegment(sketch, "E3047", {"start": v(9.4, 98.97) * mm, "end": v(9.18, 98.44) * mm});
            skLineSegment(sketch, "E3048", {"start": v(9.18, 98.44) * mm, "end": v(8.96, 97.94) * mm});
            skLineSegment(sketch, "E3049", {"start": v(8.96, 97.94) * mm, "end": v(8.75, 97.48) * mm});
            skLineSegment(sketch, "E3050", {"start": v(8.75, 97.48) * mm, "end": v(8.53, 97.05) * mm});
            skLineSegment(sketch, "E3051", {"start": v(8.53, 97.05) * mm, "end": v(8.32, 96.64) * mm});
            skLineSegment(sketch, "E3052", {"start": v(8.32, 96.64) * mm, "end": v(8.1, 96.27) * mm});
            skLineSegment(sketch, "E3053", {"start": v(8.1, 96.27) * mm, "end": v(7.88, 95.92) * mm});
            skLineSegment(sketch, "E3054", {"start": v(7.88, 95.92) * mm, "end": v(7.67, 95.6) * mm});
            skLineSegment(sketch, "E3055", {"start": v(7.67, 95.6) * mm, "end": v(7.44, 95.3) * mm});
            skLineSegment(sketch, "E3056", {"start": v(7.44, 95.3) * mm, "end": v(7.22, 95.04) * mm});
            skLineSegment(sketch, "E3057", {"start": v(7.22, 95.04) * mm, "end": v(7, 94.8) * mm});
            skLineSegment(sketch, "E3058", {"start": v(7, 94.8) * mm, "end": v(6.76, 94.58) * mm});
            skLineSegment(sketch, "E3059", {"start": v(6.76, 94.58) * mm, "end": v(6.53, 94.38) * mm});
            skLineSegment(sketch, "E3060", {"start": v(6.53, 94.38) * mm, "end": v(6.3, 94.2) * mm});
            skLineSegment(sketch, "E3061", {"start": v(6.3, 94.2) * mm, "end": v(6.05, 94.05) * mm});
            skLineSegment(sketch, "E3062", {"start": v(6.05, 94.05) * mm, "end": v(5.8, 93.92) * mm});
            skLineSegment(sketch, "E3063", {"start": v(5.8, 93.92) * mm, "end": v(5.55, 93.8) * mm});
            skLineSegment(sketch, "E3064", {"start": v(5.55, 93.8) * mm, "end": v(5.3, 93.71) * mm});
            skLineSegment(sketch, "E3065", {"start": v(5.3, 93.71) * mm, "end": v(5.03, 93.64) * mm});
            skLineSegment(sketch, "E3066", {"start": v(5.03, 93.64) * mm, "end": v(4.76, 93.58) * mm});
            skLineSegment(sketch, "E3067", {"start": v(4.76, 93.58) * mm, "end": v(4.49, 93.53) * mm});
            skLineSegment(sketch, "E3068", {"start": v(4.49, 93.53) * mm, "end": v(4.2, 93.5) * mm});
            skLineSegment(sketch, "E3069", {"start": v(4.2, 93.5) * mm, "end": v(3.92, 93.5) * mm});
            skLineSegment(sketch, "E3070", {"start": v(3.92, 93.5) * mm, "end": v(3.62, 93.5) * mm});
            skLineSegment(sketch, "E3071", {"start": v(3.62, 93.5) * mm, "end": v(3.31, 93.5) * mm});
            skLineSegment(sketch, "E3072", {"start": v(3.31, 93.5) * mm, "end": v(3, 93.53) * mm});
            skLineSegment(sketch, "E3073", {"start": v(3, 93.53) * mm, "end": v(2.68, 93.57) * mm});
            skLineSegment(sketch, "E3074", {"start": v(2.68, 93.57) * mm, "end": v(2.35, 93.62) * mm});
            skLineSegment(sketch, "E3075", {"start": v(2.35, 93.62) * mm, "end": v(2, 93.68) * mm});
            skLineSegment(sketch, "E3076", {"start": v(2, 93.68) * mm, "end": v(1.3, 93.82) * mm});
            skLineSegment(sketch, "E3077", {"start": v(57.95, 32.38) * mm, "end": v(58.76, 33.05) * mm});
            skLineSegment(sketch, "E3078", {"start": v(58.76, 33.05) * mm, "end": v(59.18, 33.4) * mm});
            skLineSegment(sketch, "E3079", {"start": v(59.18, 33.4) * mm, "end": v(59.59, 33.74) * mm});
            skLineSegment(sketch, "E3080", {"start": v(59.59, 33.74) * mm, "end": v(59.98, 34.1) * mm});
            skLineSegment(sketch, "E3081", {"start": v(59.98, 34.1) * mm, "end": v(60.36, 34.46) * mm});
            skLineSegment(sketch, "E3082", {"start": v(60.36, 34.46) * mm, "end": v(60.53, 34.65) * mm});
            skLineSegment(sketch, "E3083", {"start": v(60.53, 34.65) * mm, "end": v(60.7, 34.84) * mm});
            skLineSegment(sketch, "E3084", {"start": v(60.7, 34.84) * mm, "end": v(60.86, 35.04) * mm});
            skLineSegment(sketch, "E3085", {"start": v(60.86, 35.04) * mm, "end": v(61.01, 35.25) * mm});
            skLineSegment(sketch, "E3086", {"start": v(61.01, 35.25) * mm, "end": v(61.17, 35.45) * mm});
            skLineSegment(sketch, "E3087", {"start": v(61.17, 35.45) * mm, "end": v(61.34, 35.63) * mm});
            skLineSegment(sketch, "E3088", {"start": v(61.34, 35.63) * mm, "end": v(61.5, 35.77) * mm});
            skLineSegment(sketch, "E3089", {"start": v(61.5, 35.77) * mm, "end": v(61.7, 35.9) * mm});
            skLineSegment(sketch, "E3090", {"start": v(61.7, 35.9) * mm, "end": v(61.88, 36) * mm});
            skLineSegment(sketch, "E3091", {"start": v(61.88, 36) * mm, "end": v(62.08, 36.07) * mm});
            skLineSegment(sketch, "E3092", {"start": v(62.08, 36.07) * mm, "end": v(62.28, 36.11) * mm});
            skLineSegment(sketch, "E3093", {"start": v(62.28, 36.11) * mm, "end": v(62.49, 36.14) * mm});
            skLineSegment(sketch, "E3094", {"start": v(62.49, 36.14) * mm, "end": v(62.7, 36.15) * mm});
            skLineSegment(sketch, "E3095", {"start": v(62.7, 36.15) * mm, "end": v(62.93, 36.13) * mm});
            skLineSegment(sketch, "E3096", {"start": v(62.93, 36.13) * mm, "end": v(63.15, 36.1) * mm});
            skLineSegment(sketch, "E3097", {"start": v(63.15, 36.1) * mm, "end": v(63.38, 36.04) * mm});
            skLineSegment(sketch, "E3098", {"start": v(63.38, 36.04) * mm, "end": v(63.62, 35.97) * mm});
            skLineSegment(sketch, "E3099", {"start": v(63.62, 35.97) * mm, "end": v(63.86, 35.88) * mm});
            skLineSegment(sketch, "E3100", {"start": v(63.86, 35.88) * mm, "end": v(64.1, 35.78) * mm});
            skLineSegment(sketch, "E3101", {"start": v(64.1, 35.78) * mm, "end": v(64.34, 35.66) * mm});
            skLineSegment(sketch, "E3102", {"start": v(64.34, 35.66) * mm, "end": v(64.6, 35.52) * mm});
            skLineSegment(sketch, "E3103", {"start": v(64.6, 35.52) * mm, "end": v(64.84, 35.38) * mm});
            skLineSegment(sketch, "E3104", {"start": v(64.84, 35.38) * mm, "end": v(65.09, 35.22) * mm});
            skLineSegment(sketch, "E3105", {"start": v(65.09, 35.22) * mm, "end": v(65.34, 35.04) * mm});
            skLineSegment(sketch, "E3106", {"start": v(65.34, 35.04) * mm, "end": v(65.6, 34.86) * mm});
            skLineSegment(sketch, "E3107", {"start": v(65.6, 34.86) * mm, "end": v(65.84, 34.67) * mm});
            skLineSegment(sketch, "E3108", {"start": v(65.84, 34.67) * mm, "end": v(66.35, 34.25) * mm});
            skLineSegment(sketch, "E3109", {"start": v(66.35, 34.25) * mm, "end": v(66.84, 33.81) * mm});
            skLineSegment(sketch, "E3110", {"start": v(66.84, 33.81) * mm, "end": v(67.33, 33.35) * mm});
            skLineSegment(sketch, "E3111", {"start": v(67.33, 33.35) * mm, "end": v(67.8, 32.87) * mm});
            skLineSegment(sketch, "E3112", {"start": v(67.8, 32.87) * mm, "end": v(68.27, 32.38) * mm});
            skLineSegment(sketch, "E3113", {"start": v(55.8, 32.38) * mm, "end": v(56.11, 32.67) * mm});
            skLineSegment(sketch, "E3114", {"start": v(56.11, 32.67) * mm, "end": v(56.44, 32.96) * mm});
            skLineSegment(sketch, "E3115", {"start": v(56.44, 32.96) * mm, "end": v(57.12, 33.52) * mm});
            skLineSegment(sketch, "E3116", {"start": v(57.12, 33.52) * mm, "end": v(57.8, 34.09) * mm});
            skLineSegment(sketch, "E3117", {"start": v(57.8, 34.09) * mm, "end": v(58.5, 34.66) * mm});
            skLineSegment(sketch, "E3118", {"start": v(58.5, 34.66) * mm, "end": v(58.84, 34.95) * mm});
            skLineSegment(sketch, "E3119", {"start": v(58.84, 34.95) * mm, "end": v(59.17, 35.24) * mm});
            skLineSegment(sketch, "E3120", {"start": v(59.17, 35.24) * mm, "end": v(59.5, 35.54) * mm});
            skLineSegment(sketch, "E3121", {"start": v(59.5, 35.54) * mm, "end": v(59.8, 35.85) * mm});
            skLineSegment(sketch, "E3122", {"start": v(59.8, 35.85) * mm, "end": v(60.11, 36.16) * mm});
            skLineSegment(sketch, "E3123", {"start": v(60.11, 36.16) * mm, "end": v(60.4, 36.49) * mm});
            skLineSegment(sketch, "E3124", {"start": v(60.4, 36.49) * mm, "end": v(60.67, 36.82) * mm});
            skLineSegment(sketch, "E3125", {"start": v(60.67, 36.82) * mm, "end": v(60.93, 37.16) * mm});
            skLineSegment(sketch, "E3126", {"start": v(60.93, 37.16) * mm, "end": v(61.04, 37.32) * mm});
            skLineSegment(sketch, "E3127", {"start": v(61.04, 37.32) * mm, "end": v(61.17, 37.47) * mm});
            skLineSegment(sketch, "E3128", {"start": v(61.17, 37.47) * mm, "end": v(61.3, 37.61) * mm});
            skLineSegment(sketch, "E3129", {"start": v(61.3, 37.61) * mm, "end": v(61.42, 37.74) * mm});
            skLineSegment(sketch, "E3130", {"start": v(61.42, 37.74) * mm, "end": v(61.55, 37.86) * mm});
            skLineSegment(sketch, "E3131", {"start": v(61.55, 37.86) * mm, "end": v(61.69, 37.96) * mm});
            skLineSegment(sketch, "E3132", {"start": v(61.69, 37.96) * mm, "end": v(61.83, 38.06) * mm});
            skLineSegment(sketch, "E3133", {"start": v(61.83, 38.06) * mm, "end": v(61.97, 38.14) * mm});
            skLineSegment(sketch, "E3134", {"start": v(61.97, 38.14) * mm, "end": v(62.12, 38.22) * mm});
            skLineSegment(sketch, "E3135", {"start": v(62.12, 38.22) * mm, "end": v(62.27, 38.28) * mm});
            skLineSegment(sketch, "E3136", {"start": v(62.27, 38.28) * mm, "end": v(62.42, 38.34) * mm});
            skLineSegment(sketch, "E3137", {"start": v(62.42, 38.34) * mm, "end": v(62.57, 38.39) * mm});
            skLineSegment(sketch, "E3138", {"start": v(62.57, 38.39) * mm, "end": v(62.73, 38.42) * mm});
            skLineSegment(sketch, "E3139", {"start": v(62.73, 38.42) * mm, "end": v(62.89, 38.45) * mm});
            skLineSegment(sketch, "E3140", {"start": v(62.89, 38.45) * mm, "end": v(63.05, 38.47) * mm});
            skLineSegment(sketch, "E3141", {"start": v(63.05, 38.47) * mm, "end": v(63.21, 38.48) * mm});
            skLineSegment(sketch, "E3142", {"start": v(63.21, 38.48) * mm, "end": v(63.38, 38.48) * mm});
            skLineSegment(sketch, "E3143", {"start": v(63.38, 38.48) * mm, "end": v(63.55, 38.47) * mm});
            skLineSegment(sketch, "E3144", {"start": v(63.55, 38.47) * mm, "end": v(63.72, 38.46) * mm});
            skLineSegment(sketch, "E3145", {"start": v(63.72, 38.46) * mm, "end": v(63.9, 38.44) * mm});
            skLineSegment(sketch, "E3146", {"start": v(63.9, 38.44) * mm, "end": v(64.25, 38.37) * mm});
            skLineSegment(sketch, "E3147", {"start": v(64.25, 38.37) * mm, "end": v(64.6, 38.27) * mm});
            skLineSegment(sketch, "E3148", {"start": v(64.6, 38.27) * mm, "end": v(64.97, 38.14) * mm});
            skLineSegment(sketch, "E3149", {"start": v(64.97, 38.14) * mm, "end": v(65.34, 37.99) * mm});
            skLineSegment(sketch, "E3150", {"start": v(65.34, 37.99) * mm, "end": v(65.72, 37.81) * mm});
            skLineSegment(sketch, "E3151", {"start": v(65.72, 37.81) * mm, "end": v(66.1, 37.6) * mm});
            skLineSegment(sketch, "E3152", {"start": v(66.1, 37.6) * mm, "end": v(66.48, 37.38) * mm});
            skLineSegment(sketch, "E3153", {"start": v(66.48, 37.38) * mm, "end": v(66.87, 37.14) * mm});
            skLineSegment(sketch, "E3154", {"start": v(66.87, 37.14) * mm, "end": v(67.26, 36.87) * mm});
            skLineSegment(sketch, "E3155", {"start": v(67.26, 36.87) * mm, "end": v(67.64, 36.6) * mm});
            skLineSegment(sketch, "E3156", {"start": v(67.64, 36.6) * mm, "end": v(68.03, 36.3) * mm});
            skLineSegment(sketch, "E3157", {"start": v(68.03, 36.3) * mm, "end": v(68.42, 35.98) * mm});
            skLineSegment(sketch, "E3158", {"start": v(68.42, 35.98) * mm, "end": v(68.8, 35.66) * mm});
            skLineSegment(sketch, "E3159", {"start": v(68.8, 35.66) * mm, "end": v(69.19, 35.32) * mm});
            skLineSegment(sketch, "E3160", {"start": v(69.19, 35.32) * mm, "end": v(69.57, 34.97) * mm});
            skLineSegment(sketch, "E3161", {"start": v(69.57, 34.97) * mm, "end": v(69.95, 34.61) * mm});
            skLineSegment(sketch, "E3162", {"start": v(69.95, 34.61) * mm, "end": v(70.32, 34.25) * mm});
            skLineSegment(sketch, "E3163", {"start": v(70.32, 34.25) * mm, "end": v(70.69, 33.88) * mm});
            skLineSegment(sketch, "E3164", {"start": v(70.69, 33.88) * mm, "end": v(71.4, 33.13) * mm});
            skLineSegment(sketch, "E3165", {"start": v(71.4, 33.13) * mm, "end": v(72.1, 32.38) * mm});
            skLineSegment(sketch, "E3166", {"start": v(1.3, 46.04) * mm, "end": v(1.6, 46.05) * mm});
            skLineSegment(sketch, "E3167", {"start": v(1.6, 46.05) * mm, "end": v(1.91, 46.04) * mm});
            skLineSegment(sketch, "E3168", {"start": v(1.91, 46.04) * mm, "end": v(2.22, 46.01) * mm});
            skLineSegment(sketch, "E3169", {"start": v(2.22, 46.01) * mm, "end": v(2.52, 45.97) * mm});
            skLineSegment(sketch, "E3170", {"start": v(2.52, 45.97) * mm, "end": v(2.82, 45.9) * mm});
            skLineSegment(sketch, "E3171", {"start": v(2.82, 45.9) * mm, "end": v(3.12, 45.83) * mm});
            skLineSegment(sketch, "E3172", {"start": v(3.12, 45.83) * mm, "end": v(3.42, 45.75) * mm});
            skLineSegment(sketch, "E3173", {"start": v(3.42, 45.75) * mm, "end": v(3.7, 45.65) * mm});
            skLineSegment(sketch, "E3174", {"start": v(3.7, 45.65) * mm, "end": v(4, 45.53) * mm});
            skLineSegment(sketch, "E3175", {"start": v(4, 45.53) * mm, "end": v(4.28, 45.41) * mm});
            skLineSegment(sketch, "E3176", {"start": v(4.28, 45.41) * mm, "end": v(4.55, 45.29) * mm});
            skLineSegment(sketch, "E3177", {"start": v(4.55, 45.29) * mm, "end": v(4.82, 45.15) * mm});
            skLineSegment(sketch, "E3178", {"start": v(4.82, 45.15) * mm, "end": v(5.08, 45) * mm});
            skLineSegment(sketch, "E3179", {"start": v(5.08, 45) * mm, "end": v(5.33, 44.86) * mm});
            skLineSegment(sketch, "E3180", {"start": v(5.33, 44.86) * mm, "end": v(5.82, 44.56) * mm});
            skLineSegment(sketch, "E3181", {"start": v(5.82, 44.56) * mm, "end": v(6.26, 44.25) * mm});
            skLineSegment(sketch, "E3182", {"start": v(6.26, 44.25) * mm, "end": v(6.66, 43.95) * mm});
            skLineSegment(sketch, "E3183", {"start": v(6.66, 43.95) * mm, "end": v(7.02, 43.66) * mm});
            skLineSegment(sketch, "E3184", {"start": v(7.02, 43.66) * mm, "end": v(7.33, 43.4) * mm});
            skLineSegment(sketch, "E3185", {"start": v(7.33, 43.4) * mm, "end": v(7.58, 43.16) * mm});
            skLineSegment(sketch, "E3186", {"start": v(7.58, 43.16) * mm, "end": v(7.77, 42.97) * mm});
            skLineSegment(sketch, "E3187", {"start": v(7.77, 42.97) * mm, "end": v(7.9, 42.83) * mm});
            skLineSegment(sketch, "E3188", {"start": v(7.9, 42.83) * mm, "end": v(7.95, 42.76) * mm});
            skLineSegment(sketch, "E3189", {"start": v(7.95, 42.76) * mm, "end": v(8.08, 42.53) * mm});
            skLineSegment(sketch, "E3190", {"start": v(8.08, 42.53) * mm, "end": v(8.22, 42.32) * mm});
            skLineSegment(sketch, "E3191", {"start": v(8.22, 42.32) * mm, "end": v(8.5, 41.92) * mm});
            skLineSegment(sketch, "E3192", {"start": v(8.5, 41.92) * mm, "end": v(8.78, 41.55) * mm});
            skLineSegment(sketch, "E3193", {"start": v(8.78, 41.55) * mm, "end": v(9.08, 41.21) * mm});
            skLineSegment(sketch, "E3194", {"start": v(9.08, 41.21) * mm, "end": v(9.38, 40.9) * mm});
            skLineSegment(sketch, "E3195", {"start": v(9.38, 40.9) * mm, "end": v(9.68, 40.62) * mm});
            skLineSegment(sketch, "E3196", {"start": v(9.68, 40.62) * mm, "end": v(9.98, 40.36) * mm});
            skLineSegment(sketch, "E3197", {"start": v(9.98, 40.36) * mm, "end": v(10.28, 40.12) * mm});
            skLineSegment(sketch, "E3198", {"start": v(10.28, 40.12) * mm, "end": v(10.84, 39.7) * mm});
            skLineSegment(sketch, "E3199", {"start": v(10.84, 39.7) * mm, "end": v(11.33, 39.33) * mm});
            skLineSegment(sketch, "E3200", {"start": v(11.33, 39.33) * mm, "end": v(11.55, 39.16) * mm});
            skLineSegment(sketch, "E3201", {"start": v(11.55, 39.16) * mm, "end": v(11.74, 39) * mm});
            skLineSegment(sketch, "E3202", {"start": v(11.74, 39) * mm, "end": v(11.9, 38.83) * mm});
            skLineSegment(sketch, "E3203", {"start": v(11.9, 38.83) * mm, "end": v(12.04, 38.67) * mm});
            skLineSegment(sketch, "E3204", {"start": v(12.04, 38.67) * mm, "end": v(12.25, 38.33) * mm});
            skLineSegment(sketch, "E3205", {"start": v(12.25, 38.33) * mm, "end": v(12.46, 38) * mm});
            skLineSegment(sketch, "E3206", {"start": v(12.46, 38) * mm, "end": v(12.68, 37.59) * mm});
            skLineSegment(sketch, "E3207", {"start": v(12.68, 37.59) * mm, "end": v(12.86, 37.19) * mm});
            skLineSegment(sketch, "E3208", {"start": v(12.86, 37.19) * mm, "end": v(13.03, 36.8) * mm});
            skLineSegment(sketch, "E3209", {"start": v(13.03, 36.8) * mm, "end": v(13.16, 36.41) * mm});
            skLineSegment(sketch, "E3210", {"start": v(13.16, 36.41) * mm, "end": v(13.27, 36.04) * mm});
            skLineSegment(sketch, "E3211", {"start": v(13.27, 36.04) * mm, "end": v(13.35, 35.67) * mm});
            skLineSegment(sketch, "E3212", {"start": v(13.35, 35.67) * mm, "end": v(13.41, 35.3) * mm});
            skLineSegment(sketch, "E3213", {"start": v(13.41, 35.3) * mm, "end": v(13.45, 34.95) * mm});
            skLineSegment(sketch, "E3214", {"start": v(13.45, 34.95) * mm, "end": v(13.46, 34.6) * mm});
            skLineSegment(sketch, "E3215", {"start": v(13.46, 34.6) * mm, "end": v(13.45, 34.26) * mm});
            skLineSegment(sketch, "E3216", {"start": v(13.45, 34.26) * mm, "end": v(13.42, 33.93) * mm});
            skLineSegment(sketch, "E3217", {"start": v(13.42, 33.93) * mm, "end": v(13.37, 33.6) * mm});
            skLineSegment(sketch, "E3218", {"start": v(13.37, 33.6) * mm, "end": v(13.3, 33.29) * mm});
            skLineSegment(sketch, "E3219", {"start": v(13.3, 33.29) * mm, "end": v(13.2, 32.97) * mm});
            skLineSegment(sketch, "E3220", {"start": v(13.2, 32.97) * mm, "end": v(13.1, 32.67) * mm});
            skLineSegment(sketch, "E3221", {"start": v(13.1, 32.67) * mm, "end": v(12.98, 32.37) * mm});
            skLineSegment(sketch, "E3222", {"start": v(1.3, 43.32) * mm, "end": v(1.48, 43.44) * mm});
            skLineSegment(sketch, "E3223", {"start": v(1.48, 43.44) * mm, "end": v(1.67, 43.55) * mm});
            skLineSegment(sketch, "E3224", {"start": v(1.67, 43.55) * mm, "end": v(1.77, 43.6) * mm});
            skLineSegment(sketch, "E3225", {"start": v(1.77, 43.6) * mm, "end": v(1.87, 43.63) * mm});
            skLineSegment(sketch, "E3226", {"start": v(1.87, 43.63) * mm, "end": v(1.97, 43.66) * mm});
            skLineSegment(sketch, "E3227", {"start": v(1.97, 43.66) * mm, "end": v(2.07, 43.67) * mm});
            skLineSegment(sketch, "E3228", {"start": v(2.07, 43.67) * mm, "end": v(2.17, 43.68) * mm});
            skLineSegment(sketch, "E3229", {"start": v(2.17, 43.68) * mm, "end": v(2.27, 43.68) * mm});
            skLineSegment(sketch, "E3230", {"start": v(2.27, 43.68) * mm, "end": v(2.38, 43.67) * mm});
            skLineSegment(sketch, "E3231", {"start": v(2.38, 43.67) * mm, "end": v(2.48, 43.65) * mm});
            skLineSegment(sketch, "E3232", {"start": v(2.48, 43.65) * mm, "end": v(2.7, 43.59) * mm});
            skLineSegment(sketch, "E3233", {"start": v(2.7, 43.59) * mm, "end": v(2.9, 43.5) * mm});
            skLineSegment(sketch, "E3234", {"start": v(2.9, 43.5) * mm, "end": v(3.11, 43.38) * mm});
            skLineSegment(sketch, "E3235", {"start": v(3.11, 43.38) * mm, "end": v(3.32, 43.25) * mm});
            skLineSegment(sketch, "E3236", {"start": v(3.32, 43.25) * mm, "end": v(3.53, 43.1) * mm});
            skLineSegment(sketch, "E3237", {"start": v(3.53, 43.1) * mm, "end": v(3.73, 42.94) * mm});
            skLineSegment(sketch, "E3238", {"start": v(3.73, 42.94) * mm, "end": v(4.13, 42.6) * mm});
            skLineSegment(sketch, "E3239", {"start": v(4.13, 42.6) * mm, "end": v(4.52, 42.26) * mm});
            skLineSegment(sketch, "E3240", {"start": v(4.52, 42.26) * mm, "end": v(4.87, 41.94) * mm});
            skLineSegment(sketch, "E3241", {"start": v(4.87, 41.94) * mm, "end": v(4.94, 41.88) * mm});
            skLineSegment(sketch, "E3242", {"start": v(4.94, 41.88) * mm, "end": v(5, 41.8) * mm});
            skLineSegment(sketch, "E3243", {"start": v(5, 41.8) * mm, "end": v(5.12, 41.65) * mm});
            skLineSegment(sketch, "E3244", {"start": v(5.12, 41.65) * mm, "end": v(5.33, 41.3) * mm});
            skLineSegment(sketch, "E3245", {"start": v(5.33, 41.3) * mm, "end": v(5.46, 41.05) * mm});
            skLineSegment(sketch, "E3246", {"start": v(5.46, 41.05) * mm, "end": v(5.57, 40.79) * mm});
            skLineSegment(sketch, "E3247", {"start": v(5.57, 40.79) * mm, "end": v(5.76, 40.24) * mm});
            skLineSegment(sketch, "E3248", {"start": v(5.76, 40.24) * mm, "end": v(5.86, 39.97) * mm});
            skLineSegment(sketch, "E3249", {"start": v(5.86, 39.97) * mm, "end": v(5.98, 39.71) * mm});
            skLineSegment(sketch, "E3250", {"start": v(5.98, 39.71) * mm, "end": v(6.04, 39.59) * mm});
            skLineSegment(sketch, "E3251", {"start": v(6.04, 39.59) * mm, "end": v(6.12, 39.47) * mm});
            skLineSegment(sketch, "E3252", {"start": v(6.12, 39.47) * mm, "end": v(6.2, 39.35) * mm});
            skLineSegment(sketch, "E3253", {"start": v(6.2, 39.35) * mm, "end": v(6.29, 39.25) * mm});
            skLineSegment(sketch, "E3254", {"start": v(6.29, 39.25) * mm, "end": v(6.42, 39.11) * mm});
            skLineSegment(sketch, "E3255", {"start": v(6.42, 39.11) * mm, "end": v(6.56, 39) * mm});
            skLineSegment(sketch, "E3256", {"start": v(6.56, 39) * mm, "end": v(6.72, 38.9) * mm});
            skLineSegment(sketch, "E3257", {"start": v(6.72, 38.9) * mm, "end": v(6.88, 38.8) * mm});
            skLineSegment(sketch, "E3258", {"start": v(6.88, 38.8) * mm, "end": v(7.21, 38.62) * mm});
            skLineSegment(sketch, "E3259", {"start": v(7.21, 38.62) * mm, "end": v(7.56, 38.47) * mm});
            skLineSegment(sketch, "E3260", {"start": v(7.56, 38.47) * mm, "end": v(7.92, 38.32) * mm});
            skLineSegment(sketch, "E3261", {"start": v(7.92, 38.32) * mm, "end": v(8.26, 38.16) * mm});
            skLineSegment(sketch, "E3262", {"start": v(8.26, 38.16) * mm, "end": v(8.43, 38.07) * mm});
            skLineSegment(sketch, "E3263", {"start": v(8.43, 38.07) * mm, "end": v(8.6, 37.97) * mm});
            skLineSegment(sketch, "E3264", {"start": v(8.6, 37.97) * mm, "end": v(8.74, 37.87) * mm});
            skLineSegment(sketch, "E3265", {"start": v(8.74, 37.87) * mm, "end": v(8.89, 37.75) * mm});
            skLineSegment(sketch, "E3266", {"start": v(8.89, 37.75) * mm, "end": v(9.07, 37.56) * mm});
            skLineSegment(sketch, "E3267", {"start": v(9.07, 37.56) * mm, "end": v(9.25, 37.37) * mm});
            skLineSegment(sketch, "E3268", {"start": v(9.25, 37.37) * mm, "end": v(9.41, 37.17) * mm});
            skLineSegment(sketch, "E3269", {"start": v(9.41, 37.17) * mm, "end": v(9.57, 36.95) * mm});
            skLineSegment(sketch, "E3270", {"start": v(9.57, 36.95) * mm, "end": v(9.71, 36.73) * mm});
            skLineSegment(sketch, "E3271", {"start": v(9.71, 36.73) * mm, "end": v(9.85, 36.5) * mm});
            skLineSegment(sketch, "E3272", {"start": v(9.85, 36.5) * mm, "end": v(9.97, 36.28) * mm});
            skLineSegment(sketch, "E3273", {"start": v(9.97, 36.28) * mm, "end": v(10.09, 36.04) * mm});
            skLineSegment(sketch, "E3274", {"start": v(10.09, 36.04) * mm, "end": v(10.18, 35.81) * mm});
            skLineSegment(sketch, "E3275", {"start": v(10.18, 35.81) * mm, "end": v(10.25, 35.57) * mm});
            skLineSegment(sketch, "E3276", {"start": v(10.25, 35.57) * mm, "end": v(10.3, 35.32) * mm});
            skLineSegment(sketch, "E3277", {"start": v(10.3, 35.32) * mm, "end": v(10.34, 35.08) * mm});
            skLineSegment(sketch, "E3278", {"start": v(10.34, 35.08) * mm, "end": v(10.4, 34.74) * mm});
            skLineSegment(sketch, "E3279", {"start": v(10.4, 34.74) * mm, "end": v(10.47, 34.4) * mm});
            skLineSegment(sketch, "E3280", {"start": v(10.47, 34.4) * mm, "end": v(10.54, 34.04) * mm});
            skLineSegment(sketch, "E3281", {"start": v(10.54, 34.04) * mm, "end": v(10.6, 33.69) * mm});
            skLineSegment(sketch, "E3282", {"start": v(10.6, 33.69) * mm, "end": v(10.65, 33.34) * mm});
            skLineSegment(sketch, "E3283", {"start": v(10.65, 33.34) * mm, "end": v(10.66, 33.17) * mm});
            skLineSegment(sketch, "E3284", {"start": v(10.66, 33.17) * mm, "end": v(10.66, 33) * mm});
            skLineSegment(sketch, "E3285", {"start": v(10.66, 33) * mm, "end": v(10.65, 32.83) * mm});
            skLineSegment(sketch, "E3286", {"start": v(10.65, 32.83) * mm, "end": v(10.62, 32.68) * mm});
            skLineSegment(sketch, "E3287", {"start": v(10.62, 32.68) * mm, "end": v(10.58, 32.52) * mm});
            skLineSegment(sketch, "E3288", {"start": v(10.58, 32.52) * mm, "end": v(10.53, 32.38) * mm});
            skLineSegment(sketch, "E3289", {"start": v(1.3, 39.38) * mm, "end": v(1.5, 39.37) * mm});
            skLineSegment(sketch, "E3290", {"start": v(1.5, 39.37) * mm, "end": v(1.72, 39.32) * mm});
            skLineSegment(sketch, "E3291", {"start": v(1.72, 39.32) * mm, "end": v(1.94, 39.26) * mm});
            skLineSegment(sketch, "E3292", {"start": v(1.94, 39.26) * mm, "end": v(2.17, 39.17) * mm});
            skLineSegment(sketch, "E3293", {"start": v(2.17, 39.17) * mm, "end": v(2.4, 39.06) * mm});
            skLineSegment(sketch, "E3294", {"start": v(2.4, 39.06) * mm, "end": v(2.64, 38.94) * mm});
            skLineSegment(sketch, "E3295", {"start": v(2.64, 38.94) * mm, "end": v(2.87, 38.8) * mm});
            skLineSegment(sketch, "E3296", {"start": v(2.87, 38.8) * mm, "end": v(3.12, 38.64) * mm});
            skLineSegment(sketch, "E3297", {"start": v(3.12, 38.64) * mm, "end": v(3.36, 38.47) * mm});
            skLineSegment(sketch, "E3298", {"start": v(3.36, 38.47) * mm, "end": v(3.6, 38.29) * mm});
            skLineSegment(sketch, "E3299", {"start": v(3.6, 38.29) * mm, "end": v(4.08, 37.9) * mm});
            skLineSegment(sketch, "E3300", {"start": v(4.08, 37.9) * mm, "end": v(4.55, 37.47) * mm});
            skLineSegment(sketch, "E3301", {"start": v(4.55, 37.47) * mm, "end": v(5, 37.03) * mm});
            skLineSegment(sketch, "E3302", {"start": v(5, 37.03) * mm, "end": v(5.44, 36.6) * mm});
            skLineSegment(sketch, "E3303", {"start": v(5.44, 36.6) * mm, "end": v(5.84, 36.17) * mm});
            skLineSegment(sketch, "E3304", {"start": v(5.84, 36.17) * mm, "end": v(6.2, 35.77) * mm});
            skLineSegment(sketch, "E3305", {"start": v(6.2, 35.77) * mm, "end": v(6.51, 35.41) * mm});
            skLineSegment(sketch, "E3306", {"start": v(6.51, 35.41) * mm, "end": v(6.98, 34.86) * mm});
            skLineSegment(sketch, "E3307", {"start": v(6.98, 34.86) * mm, "end": v(7.17, 34.61) * mm});
            skLineSegment(sketch, "E3308", {"start": v(7.17, 34.61) * mm, "end": v(7.26, 34.5) * mm});
            skLineSegment(sketch, "E3309", {"start": v(7.26, 34.5) * mm, "end": v(7.34, 34.37) * mm});
            skLineSegment(sketch, "E3310", {"start": v(7.34, 34.37) * mm, "end": v(7.4, 34.25) * mm});
            skLineSegment(sketch, "E3311", {"start": v(7.4, 34.25) * mm, "end": v(7.47, 34.12) * mm});
            skLineSegment(sketch, "E3312", {"start": v(7.47, 34.12) * mm, "end": v(7.53, 33.98) * mm});
            skLineSegment(sketch, "E3313", {"start": v(7.53, 33.98) * mm, "end": v(7.58, 33.85) * mm});
            skLineSegment(sketch, "E3314", {"start": v(7.58, 33.85) * mm, "end": v(7.65, 33.57) * mm});
            skLineSegment(sketch, "E3315", {"start": v(7.65, 33.57) * mm, "end": v(7.7, 33.28) * mm});
            skLineSegment(sketch, "E3316", {"start": v(7.7, 33.28) * mm, "end": v(7.72, 32.99) * mm});
            skLineSegment(sketch, "E3317", {"start": v(7.72, 32.99) * mm, "end": v(7.72, 32.68) * mm});
            skLineSegment(sketch, "E3318", {"start": v(7.72, 32.68) * mm, "end": v(7.7, 32.38) * mm});
            skLineSegment(sketch, "E3319", {"start": v(170.69, 104.2) * mm, "end": v(170.75, 104.03) * mm});
            skLineSegment(sketch, "E3320", {"start": v(170.75, 104.03) * mm, "end": v(170.8, 103.86) * mm});
            skLineSegment(sketch, "E3321", {"start": v(170.8, 103.86) * mm, "end": v(170.83, 103.7) * mm});
            skLineSegment(sketch, "E3322", {"start": v(170.83, 103.7) * mm, "end": v(170.84, 103.54) * mm});
            skLineSegment(sketch, "E3323", {"start": v(170.84, 103.54) * mm, "end": v(170.84, 103.38) * mm});
            skLineSegment(sketch, "E3324", {"start": v(170.84, 103.38) * mm, "end": v(170.82, 103.23) * mm});
            skLineSegment(sketch, "E3325", {"start": v(170.82, 103.23) * mm, "end": v(170.78, 103.07) * mm});
            skLineSegment(sketch, "E3326", {"start": v(170.78, 103.07) * mm, "end": v(170.72, 102.92) * mm});
            skLineSegment(sketch, "E3327", {"start": v(170.72, 102.92) * mm, "end": v(170.64, 102.77) * mm});
            skLineSegment(sketch, "E3328", {"start": v(170.64, 102.77) * mm, "end": v(170.55, 102.62) * mm});
            skLineSegment(sketch, "E3329", {"start": v(170.55, 102.62) * mm, "end": v(170.43, 102.47) * mm});
            skLineSegment(sketch, "E3330", {"start": v(170.43, 102.47) * mm, "end": v(170.3, 102.32) * mm});
            skLineSegment(sketch, "E3331", {"start": v(170.3, 102.32) * mm, "end": v(170.14, 102.18) * mm});
            skLineSegment(sketch, "E3332", {"start": v(170.14, 102.18) * mm, "end": v(169.97, 102.04) * mm});
            skLineSegment(sketch, "E3333", {"start": v(169.97, 102.04) * mm, "end": v(169.77, 101.9) * mm});
            skLineSegment(sketch, "E3334", {"start": v(169.77, 101.9) * mm, "end": v(169.55, 101.77) * mm});
            skLineSegment(sketch, "E3335", {"start": v(169.55, 101.77) * mm, "end": v(169.3, 101.63) * mm});
            skLineSegment(sketch, "E3336", {"start": v(169.3, 101.63) * mm, "end": v(169.04, 101.5) * mm});
            skLineSegment(sketch, "E3337", {"start": v(169.04, 101.5) * mm, "end": v(168.76, 101.38) * mm});
            skLineSegment(sketch, "E3338", {"start": v(168.76, 101.38) * mm, "end": v(168.45, 101.26) * mm});
            skLineSegment(sketch, "E3339", {"start": v(168.45, 101.26) * mm, "end": v(168.13, 101.14) * mm});
            skLineSegment(sketch, "E3340", {"start": v(168.13, 101.14) * mm, "end": v(167.78, 101.03) * mm});
            skLineSegment(sketch, "E3341", {"start": v(167.78, 101.03) * mm, "end": v(167.42, 100.93) * mm});
            skLineSegment(sketch, "E3342", {"start": v(167.42, 100.93) * mm, "end": v(167.04, 100.82) * mm});
            skLineSegment(sketch, "E3343", {"start": v(167.04, 100.82) * mm, "end": v(166.65, 100.72) * mm});
            skLineSegment(sketch, "E3344", {"start": v(166.65, 100.72) * mm, "end": v(166.23, 100.63) * mm});
            skLineSegment(sketch, "E3345", {"start": v(166.23, 100.63) * mm, "end": v(165.36, 100.45) * mm});
            skLineSegment(sketch, "E3346", {"start": v(165.36, 100.45) * mm, "end": v(164.43, 100.3) * mm});
            skLineSegment(sketch, "E3347", {"start": v(164.43, 100.3) * mm, "end": v(163.45, 100.15) * mm});
            skLineSegment(sketch, "E3348", {"start": v(163.45, 100.15) * mm, "end": v(162.42, 100.01) * mm});
            skLineSegment(sketch, "E3349", {"start": v(162.42, 100.01) * mm, "end": v(161.35, 99.9) * mm});
            skLineSegment(sketch, "E3350", {"start": v(161.35, 99.9) * mm, "end": v(160.24, 99.8) * mm});
            skLineSegment(sketch, "E3351", {"start": v(160.24, 99.8) * mm, "end": v(159.1, 99.7) * mm});
            skLineSegment(sketch, "E3352", {"start": v(159.1, 99.7) * mm, "end": v(157.92, 99.63) * mm});
            skLineSegment(sketch, "E3353", {"start": v(157.92, 99.63) * mm, "end": v(156.72, 99.56) * mm});
            skLineSegment(sketch, "E3354", {"start": v(156.72, 99.56) * mm, "end": v(155.5, 99.5) * mm});
            skLineSegment(sketch, "E3355", {"start": v(155.5, 99.5) * mm, "end": v(154.28, 99.47) * mm});
            skLineSegment(sketch, "E3356", {"start": v(154.28, 99.47) * mm, "end": v(153.04, 99.44) * mm});
            skLineSegment(sketch, "E3357", {"start": v(153.04, 99.44) * mm, "end": v(151.8, 99.42) * mm});
            skLineSegment(sketch, "E3358", {"start": v(151.8, 99.42) * mm, "end": v(150.55, 99.4) * mm});
            skLineSegment(sketch, "E3359", {"start": v(150.55, 99.4) * mm, "end": v(149.31, 99.4) * mm});
            skLineSegment(sketch, "E3360", {"start": v(149.31, 99.4) * mm, "end": v(148.09, 99.4) * mm});
            skLineSegment(sketch, "E3361", {"start": v(148.09, 99.4) * mm, "end": v(146.87, 99.42) * mm});
            skLineSegment(sketch, "E3362", {"start": v(146.87, 99.42) * mm, "end": v(145.68, 99.45) * mm});
            skLineSegment(sketch, "E3363", {"start": v(145.68, 99.45) * mm, "end": v(144.51, 99.48) * mm});
            skLineSegment(sketch, "E3364", {"start": v(144.51, 99.48) * mm, "end": v(142.27, 99.56) * mm});
            skLineSegment(sketch, "E3365", {"start": v(142.27, 99.56) * mm, "end": v(140.18, 99.66) * mm});
            skLineSegment(sketch, "E3366", {"start": v(140.18, 99.66) * mm, "end": v(139.21, 99.72) * mm});
            skLineSegment(sketch, "E3367", {"start": v(139.21, 99.72) * mm, "end": v(138.3, 99.78) * mm});
            skLineSegment(sketch, "E3368", {"start": v(138.3, 99.78) * mm, "end": v(137.43, 99.85) * mm});
            skLineSegment(sketch, "E3369", {"start": v(137.43, 99.85) * mm, "end": v(136.64, 99.92) * mm});
            skLineSegment(sketch, "E3370", {"start": v(136.64, 99.92) * mm, "end": v(136.26, 99.95) * mm});
            skLineSegment(sketch, "E3371", {"start": v(136.26, 99.95) * mm, "end": v(135.8, 99.97) * mm});
            skLineSegment(sketch, "E3372", {"start": v(135.8, 99.97) * mm, "end": v(135.26, 99.98) * mm});
            skLineSegment(sketch, "E3373", {"start": v(135.26, 99.98) * mm, "end": v(134.65, 99.98) * mm});
            skLineSegment(sketch, "E3374", {"start": v(134.65, 99.98) * mm, "end": v(133.23, 99.97) * mm});
            skLineSegment(sketch, "E3375", {"start": v(133.23, 99.97) * mm, "end": v(131.6, 99.93) * mm});
            skLineSegment(sketch, "E3376", {"start": v(131.6, 99.93) * mm, "end": v(127.83, 99.82) * mm});
            skLineSegment(sketch, "E3377", {"start": v(127.83, 99.82) * mm, "end": v(123.71, 99.68) * mm});
            skLineSegment(sketch, "E3378", {"start": v(123.71, 99.68) * mm, "end": v(121.64, 99.62) * mm});
            skLineSegment(sketch, "E3379", {"start": v(121.64, 99.62) * mm, "end": v(119.6, 99.56) * mm});
            skLineSegment(sketch, "E3380", {"start": v(119.6, 99.56) * mm, "end": v(117.67, 99.51) * mm});
            skLineSegment(sketch, "E3381", {"start": v(117.67, 99.51) * mm, "end": v(115.87, 99.48) * mm});
            skLineSegment(sketch, "E3382", {"start": v(115.87, 99.48) * mm, "end": v(114.25, 99.48) * mm});
            skLineSegment(sketch, "E3383", {"start": v(114.25, 99.48) * mm, "end": v(113.52, 99.49) * mm});
            skLineSegment(sketch, "E3384", {"start": v(113.52, 99.49) * mm, "end": v(112.85, 99.5) * mm});
            skLineSegment(sketch, "E3385", {"start": v(112.85, 99.5) * mm, "end": v(112.26, 99.52) * mm});
            skLineSegment(sketch, "E3386", {"start": v(112.26, 99.52) * mm, "end": v(111.73, 99.55) * mm});
            skLineSegment(sketch, "E3387", {"start": v(111.73, 99.55) * mm, "end": v(111.29, 99.6) * mm});
            skLineSegment(sketch, "E3388", {"start": v(111.29, 99.6) * mm, "end": v(110.93, 99.65) * mm});
            skLineSegment(sketch, "E3389", {"start": v(110.93, 99.65) * mm, "end": v(110.27, 99.77) * mm});
            skLineSegment(sketch, "E3390", {"start": v(110.27, 99.77) * mm, "end": v(109.66, 99.89) * mm});
            skLineSegment(sketch, "E3391", {"start": v(109.66, 99.89) * mm, "end": v(109.09, 100.01) * mm});
            skLineSegment(sketch, "E3392", {"start": v(109.09, 100.01) * mm, "end": v(108.55, 100.14) * mm});
            skLineSegment(sketch, "E3393", {"start": v(108.55, 100.14) * mm, "end": v(108.06, 100.27) * mm});
            skLineSegment(sketch, "E3394", {"start": v(108.06, 100.27) * mm, "end": v(107.6, 100.4) * mm});
            skLineSegment(sketch, "E3395", {"start": v(107.6, 100.4) * mm, "end": v(107.17, 100.53) * mm});
            skLineSegment(sketch, "E3396", {"start": v(107.17, 100.53) * mm, "end": v(106.79, 100.66) * mm});
            skLineSegment(sketch, "E3397", {"start": v(106.79, 100.66) * mm, "end": v(106.43, 100.8) * mm});
            skLineSegment(sketch, "E3398", {"start": v(106.43, 100.8) * mm, "end": v(106.12, 100.93) * mm});
            skLineSegment(sketch, "E3399", {"start": v(106.12, 100.93) * mm, "end": v(105.84, 101.07) * mm});
            skLineSegment(sketch, "E3400", {"start": v(105.84, 101.07) * mm, "end": v(105.6, 101.21) * mm});
            skLineSegment(sketch, "E3401", {"start": v(105.6, 101.21) * mm, "end": v(105.38, 101.35) * mm});
            skLineSegment(sketch, "E3402", {"start": v(105.38, 101.35) * mm, "end": v(105.2, 101.5) * mm});
            skLineSegment(sketch, "E3403", {"start": v(105.2, 101.5) * mm, "end": v(105.05, 101.64) * mm});
            skLineSegment(sketch, "E3404", {"start": v(105.05, 101.64) * mm, "end": v(104.93, 101.78) * mm});
            skLineSegment(sketch, "E3405", {"start": v(104.93, 101.78) * mm, "end": v(104.85, 101.93) * mm});
            skLineSegment(sketch, "E3406", {"start": v(104.85, 101.93) * mm, "end": v(104.8, 102.07) * mm});
            skLineSegment(sketch, "E3407", {"start": v(104.8, 102.07) * mm, "end": v(104.77, 102.22) * mm});
            skLineSegment(sketch, "E3408", {"start": v(104.77, 102.22) * mm, "end": v(104.77, 102.37) * mm});
            skLineSegment(sketch, "E3409", {"start": v(104.77, 102.37) * mm, "end": v(104.8, 102.52) * mm});
            skLineSegment(sketch, "E3410", {"start": v(104.8, 102.52) * mm, "end": v(104.87, 102.67) * mm});
            skLineSegment(sketch, "E3411", {"start": v(104.87, 102.67) * mm, "end": v(104.96, 102.82) * mm});
            skLineSegment(sketch, "E3412", {"start": v(104.96, 102.82) * mm, "end": v(105.08, 102.97) * mm});
            skLineSegment(sketch, "E3413", {"start": v(105.08, 102.97) * mm, "end": v(105.22, 103.12) * mm});
            skLineSegment(sketch, "E3414", {"start": v(105.22, 103.12) * mm, "end": v(105.4, 103.27) * mm});
            skLineSegment(sketch, "E3415", {"start": v(105.4, 103.27) * mm, "end": v(105.6, 103.43) * mm});
            skLineSegment(sketch, "E3416", {"start": v(105.6, 103.43) * mm, "end": v(105.81, 103.58) * mm});
            skLineSegment(sketch, "E3417", {"start": v(105.81, 103.58) * mm, "end": v(106.06, 103.73) * mm});
            skLineSegment(sketch, "E3418", {"start": v(106.06, 103.73) * mm, "end": v(106.33, 103.89) * mm});
            skLineSegment(sketch, "E3419", {"start": v(106.33, 103.89) * mm, "end": v(106.63, 104.04) * mm});
            skLineSegment(sketch, "E3420", {"start": v(106.63, 104.04) * mm, "end": v(106.95, 104.2) * mm});
            skLineSegment(sketch, "E3421", {"start": v(138.39, 32.19) * mm, "end": v(138.33, 32.35) * mm});
            skLineSegment(sketch, "E3422", {"start": v(138.33, 32.35) * mm, "end": v(138.29, 32.52) * mm});
            skLineSegment(sketch, "E3423", {"start": v(138.29, 32.52) * mm, "end": v(138.26, 32.68) * mm});
            skLineSegment(sketch, "E3424", {"start": v(138.26, 32.68) * mm, "end": v(138.26, 32.84) * mm});
            skLineSegment(sketch, "E3425", {"start": v(138.26, 32.84) * mm, "end": v(138.27, 33) * mm});
            skLineSegment(sketch, "E3426", {"start": v(138.27, 33) * mm, "end": v(138.3, 33.16) * mm});
            skLineSegment(sketch, "E3427", {"start": v(138.3, 33.16) * mm, "end": v(138.34, 33.31) * mm});
            skLineSegment(sketch, "E3428", {"start": v(138.34, 33.31) * mm, "end": v(138.4, 33.46) * mm});
            skLineSegment(sketch, "E3429", {"start": v(138.4, 33.46) * mm, "end": v(138.48, 33.61) * mm});
            skLineSegment(sketch, "E3430", {"start": v(138.48, 33.61) * mm, "end": v(138.59, 33.76) * mm});
            skLineSegment(sketch, "E3431", {"start": v(138.59, 33.76) * mm, "end": v(138.7, 33.9) * mm});
            skLineSegment(sketch, "E3432", {"start": v(138.7, 33.9) * mm, "end": v(138.85, 34.04) * mm});
            skLineSegment(sketch, "E3433", {"start": v(138.85, 34.04) * mm, "end": v(139, 34.18) * mm});
            skLineSegment(sketch, "E3434", {"start": v(139, 34.18) * mm, "end": v(139.19, 34.31) * mm});
            skLineSegment(sketch, "E3435", {"start": v(139.19, 34.31) * mm, "end": v(139.39, 34.44) * mm});
            skLineSegment(sketch, "E3436", {"start": v(139.39, 34.44) * mm, "end": v(139.61, 34.57) * mm});
            skLineSegment(sketch, "E3437", {"start": v(139.61, 34.57) * mm, "end": v(139.86, 34.7) * mm});
            skLineSegment(sketch, "E3438", {"start": v(139.86, 34.7) * mm, "end": v(140.13, 34.81) * mm});
            skLineSegment(sketch, "E3439", {"start": v(140.13, 34.81) * mm, "end": v(140.42, 34.93) * mm});
            skLineSegment(sketch, "E3440", {"start": v(140.42, 34.93) * mm, "end": v(140.73, 35.04) * mm});
            skLineSegment(sketch, "E3441", {"start": v(140.73, 35.04) * mm, "end": v(141.06, 35.14) * mm});
            skLineSegment(sketch, "E3442", {"start": v(141.06, 35.14) * mm, "end": v(141.4, 35.24) * mm});
            skLineSegment(sketch, "E3443", {"start": v(141.4, 35.24) * mm, "end": v(141.77, 35.33) * mm});
            skLineSegment(sketch, "E3444", {"start": v(141.77, 35.33) * mm, "end": v(142.15, 35.42) * mm});
            skLineSegment(sketch, "E3445", {"start": v(142.15, 35.42) * mm, "end": v(142.55, 35.5) * mm});
            skLineSegment(sketch, "E3446", {"start": v(142.55, 35.5) * mm, "end": v(142.97, 35.58) * mm});
            skLineSegment(sketch, "E3447", {"start": v(142.97, 35.58) * mm, "end": v(143.85, 35.73) * mm});
            skLineSegment(sketch, "E3448", {"start": v(143.85, 35.73) * mm, "end": v(144.78, 35.86) * mm});
            skLineSegment(sketch, "E3449", {"start": v(144.78, 35.86) * mm, "end": v(145.77, 35.97) * mm});
            skLineSegment(sketch, "E3450", {"start": v(145.77, 35.97) * mm, "end": v(146.8, 36.06) * mm});
            skLineSegment(sketch, "E3451", {"start": v(146.8, 36.06) * mm, "end": v(147.88, 36.14) * mm});
            skLineSegment(sketch, "E3452", {"start": v(147.88, 36.14) * mm, "end": v(148.99, 36.2) * mm});
            skLineSegment(sketch, "E3453", {"start": v(148.99, 36.2) * mm, "end": v(150.14, 36.25) * mm});
            skLineSegment(sketch, "E3454", {"start": v(150.14, 36.25) * mm, "end": v(151.31, 36.28) * mm});
            skLineSegment(sketch, "E3455", {"start": v(151.31, 36.28) * mm, "end": v(152.51, 36.3) * mm});
            skLineSegment(sketch, "E3456", {"start": v(152.51, 36.3) * mm, "end": v(153.73, 36.3) * mm});
            skLineSegment(sketch, "E3457", {"start": v(153.73, 36.3) * mm, "end": v(154.96, 36.3) * mm});
            skLineSegment(sketch, "E3458", {"start": v(154.96, 36.3) * mm, "end": v(156.2, 36.3) * mm});
            skLineSegment(sketch, "E3459", {"start": v(156.2, 36.3) * mm, "end": v(157.44, 36.27) * mm});
            skLineSegment(sketch, "E3460", {"start": v(157.44, 36.27) * mm, "end": v(158.68, 36.23) * mm});
            skLineSegment(sketch, "E3461", {"start": v(158.68, 36.23) * mm, "end": v(159.92, 36.19) * mm});
            skLineSegment(sketch, "E3462", {"start": v(159.92, 36.19) * mm, "end": v(161.15, 36.14) * mm});
            skLineSegment(sketch, "E3463", {"start": v(161.15, 36.14) * mm, "end": v(162.36, 36.08) * mm});
            skLineSegment(sketch, "E3464", {"start": v(162.36, 36.08) * mm, "end": v(163.55, 36) * mm});
            skLineSegment(sketch, "E3465", {"start": v(163.55, 36) * mm, "end": v(164.72, 35.94) * mm});
            skLineSegment(sketch, "E3466", {"start": v(164.72, 35.94) * mm, "end": v(166.96, 35.77) * mm});
            skLineSegment(sketch, "E3467", {"start": v(166.96, 35.77) * mm, "end": v(169.04, 35.6) * mm});
            skLineSegment(sketch, "E3468", {"start": v(169.04, 35.6) * mm, "end": v(170, 35.5) * mm});
            skLineSegment(sketch, "E3469", {"start": v(170, 35.5) * mm, "end": v(170.92, 35.4) * mm});
            skLineSegment(sketch, "E3470", {"start": v(170.92, 35.4) * mm, "end": v(171.78, 35.3) * mm});
            skLineSegment(sketch, "E3471", {"start": v(171.78, 35.3) * mm, "end": v(172.57, 35.2) * mm});
            skLineSegment(sketch, "E3472", {"start": v(172.57, 35.2) * mm, "end": v(172.95, 35.16) * mm});
            skLineSegment(sketch, "E3473", {"start": v(172.95, 35.16) * mm, "end": v(173.4, 35.13) * mm});
            skLineSegment(sketch, "E3474", {"start": v(173.4, 35.13) * mm, "end": v(173.95, 35.1) * mm});
            skLineSegment(sketch, "E3475", {"start": v(173.95, 35.1) * mm, "end": v(174.56, 35.07) * mm});
            skLineSegment(sketch, "E3476", {"start": v(174.56, 35.07) * mm, "end": v(175.97, 35.03) * mm});
            skLineSegment(sketch, "E3477", {"start": v(175.97, 35.03) * mm, "end": v(177.61, 35) * mm});
            skLineSegment(sketch, "E3478", {"start": v(177.61, 35) * mm, "end": v(181.38, 34.97) * mm});
            skLineSegment(sketch, "E3479", {"start": v(181.38, 34.97) * mm, "end": v(185.5, 34.96) * mm});
            skLineSegment(sketch, "E3480", {"start": v(185.5, 34.96) * mm, "end": v(187.57, 34.95) * mm});
            skLineSegment(sketch, "E3481", {"start": v(187.57, 34.95) * mm, "end": v(189.6, 34.94) * mm});
            skLineSegment(sketch, "E3482", {"start": v(189.6, 34.94) * mm, "end": v(191.54, 34.91) * mm});
            skLineSegment(sketch, "E3483", {"start": v(191.54, 34.91) * mm, "end": v(193.34, 34.87) * mm});
            skLineSegment(sketch, "E3484", {"start": v(193.34, 34.87) * mm, "end": v(194.96, 34.82) * mm});
            skLineSegment(sketch, "E3485", {"start": v(194.96, 34.82) * mm, "end": v(195.69, 34.78) * mm});
            skLineSegment(sketch, "E3486", {"start": v(195.69, 34.78) * mm, "end": v(196.35, 34.75) * mm});
            skLineSegment(sketch, "E3487", {"start": v(196.35, 34.75) * mm, "end": v(196.95, 34.7) * mm});
            skLineSegment(sketch, "E3488", {"start": v(196.95, 34.7) * mm, "end": v(197.47, 34.65) * mm});
            skLineSegment(sketch, "E3489", {"start": v(197.47, 34.65) * mm, "end": v(197.92, 34.6) * mm});
            skLineSegment(sketch, "E3490", {"start": v(197.92, 34.6) * mm, "end": v(198.27, 34.53) * mm});
            skLineSegment(sketch, "E3491", {"start": v(198.27, 34.53) * mm, "end": v(198.92, 34.38) * mm});
            skLineSegment(sketch, "E3492", {"start": v(198.92, 34.38) * mm, "end": v(199.53, 34.24) * mm});
            skLineSegment(sketch, "E3493", {"start": v(199.53, 34.24) * mm, "end": v(200.1, 34.1) * mm});
            skLineSegment(sketch, "E3494", {"start": v(200.1, 34.1) * mm, "end": v(200.63, 33.95) * mm});
            skLineSegment(sketch, "E3495", {"start": v(200.63, 33.95) * mm, "end": v(201.12, 33.8) * mm});
            skLineSegment(sketch, "E3496", {"start": v(201.12, 33.8) * mm, "end": v(201.57, 33.65) * mm});
            skLineSegment(sketch, "E3497", {"start": v(201.57, 33.65) * mm, "end": v(202, 33.5) * mm});
            skLineSegment(sketch, "E3498", {"start": v(202, 33.5) * mm, "end": v(202.37, 33.36) * mm});
            skLineSegment(sketch, "E3499", {"start": v(202.37, 33.36) * mm, "end": v(202.72, 33.21) * mm});
            skLineSegment(sketch, "E3500", {"start": v(202.72, 33.21) * mm, "end": v(203.03, 33.06) * mm});
            skLineSegment(sketch, "E3501", {"start": v(203.03, 33.06) * mm, "end": v(203.3, 32.92) * mm});
            skLineSegment(sketch, "E3502", {"start": v(203.3, 32.92) * mm, "end": v(203.55, 32.77) * mm});
            skLineSegment(sketch, "E3503", {"start": v(203.55, 32.77) * mm, "end": v(203.76, 32.62) * mm});
            skLineSegment(sketch, "E3504", {"start": v(203.76, 32.62) * mm, "end": v(203.93, 32.47) * mm});
            skLineSegment(sketch, "E3505", {"start": v(203.93, 32.47) * mm, "end": v(204.08, 32.32) * mm});
            skLineSegment(sketch, "E3506", {"start": v(204.08, 32.32) * mm, "end": v(204.19, 32.17) * mm});
            skLineSegment(sketch, "E3507", {"start": v(204.19, 32.17) * mm, "end": v(204.27, 32.02) * mm});
            skLineSegment(sketch, "E3508", {"start": v(204.27, 32.02) * mm, "end": v(204.32, 31.88) * mm});
            skLineSegment(sketch, "E3509", {"start": v(204.32, 31.88) * mm, "end": v(204.33, 31.73) * mm});
            skLineSegment(sketch, "E3510", {"start": v(204.33, 31.73) * mm, "end": v(204.32, 31.58) * mm});
            skLineSegment(sketch, "E3511", {"start": v(204.32, 31.58) * mm, "end": v(204.28, 31.43) * mm});
            skLineSegment(sketch, "E3512", {"start": v(204.28, 31.43) * mm, "end": v(204.22, 31.28) * mm});
            skLineSegment(sketch, "E3513", {"start": v(204.22, 31.28) * mm, "end": v(204.12, 31.14) * mm});
            skLineSegment(sketch, "E3514", {"start": v(204.12, 31.14) * mm, "end": v(204, 31) * mm});
            skLineSegment(sketch, "E3515", {"start": v(204, 31) * mm, "end": v(203.85, 30.85) * mm});
            skLineSegment(sketch, "E3516", {"start": v(203.85, 30.85) * mm, "end": v(203.67, 30.7) * mm});
            skLineSegment(sketch, "E3517", {"start": v(203.67, 30.7) * mm, "end": v(203.47, 30.55) * mm});
            skLineSegment(sketch, "E3518", {"start": v(203.47, 30.55) * mm, "end": v(203.24, 30.41) * mm});
            skLineSegment(sketch, "E3519", {"start": v(203.24, 30.41) * mm, "end": v(202.99, 30.27) * mm});
            skLineSegment(sketch, "E3520", {"start": v(202.99, 30.27) * mm, "end": v(202.7, 30.12) * mm});
            skLineSegment(sketch, "E3521", {"start": v(202.7, 30.12) * mm, "end": v(202.4, 29.98) * mm});
            skLineSegment(sketch, "E3522", {"start": v(202.4, 29.98) * mm, "end": v(202.09, 29.84) * mm});
            skLineSegment(sketch, "E3523", {"start": v(-0.2, 85.94) * mm, "end": v(-0.04, 85.97) * mm});
            skLineSegment(sketch, "E3524", {"start": v(-0.04, 85.97) * mm, "end": v(0.13, 86.02) * mm});
            skLineSegment(sketch, "E3525", {"start": v(0.13, 86.02) * mm, "end": v(0.45, 86.13) * mm});
            skLineSegment(sketch, "E3526", {"start": v(0.45, 86.13) * mm, "end": v(0.77, 86.26) * mm});
            skLineSegment(sketch, "E3527", {"start": v(0.77, 86.26) * mm, "end": v(1.08, 86.4) * mm});
            skLineSegment(sketch, "E3528", {"start": v(1.08, 86.4) * mm, "end": v(1.68, 86.71) * mm});
            skLineSegment(sketch, "E3529", {"start": v(1.68, 86.71) * mm, "end": v(2.22, 87) * mm});
            skLineSegment(sketch, "E3530", {"start": v(2.22, 87) * mm, "end": v(2.47, 87.12) * mm});
            skLineSegment(sketch, "E3531", {"start": v(2.47, 87.12) * mm, "end": v(2.7, 87.21) * mm});
            skLineSegment(sketch, "E3532", {"start": v(2.7, 87.21) * mm, "end": v(2.9, 87.27) * mm});
            skLineSegment(sketch, "E3533", {"start": v(2.9, 87.27) * mm, "end": v(2.98, 87.28) * mm});
            skLineSegment(sketch, "E3534", {"start": v(2.98, 87.28) * mm, "end": v(3.07, 87.29) * mm});
            skLineSegment(sketch, "E3535", {"start": v(3.07, 87.29) * mm, "end": v(3.14, 87.28) * mm});
            skLineSegment(sketch, "E3536", {"start": v(3.14, 87.28) * mm, "end": v(3.21, 87.26) * mm});
            skLineSegment(sketch, "E3537", {"start": v(3.21, 87.26) * mm, "end": v(3.28, 87.22) * mm});
            skLineSegment(sketch, "E3538", {"start": v(3.28, 87.22) * mm, "end": v(3.33, 87.17) * mm});
            skLineSegment(sketch, "E3539", {"start": v(3.33, 87.17) * mm, "end": v(3.37, 87.1) * mm});
            skLineSegment(sketch, "E3540", {"start": v(3.37, 87.1) * mm, "end": v(3.41, 87.03) * mm});
            skLineSegment(sketch, "E3541", {"start": v(3.41, 87.03) * mm, "end": v(3.44, 86.93) * mm});
            skLineSegment(sketch, "E3542", {"start": v(3.44, 86.93) * mm, "end": v(3.46, 86.82) * mm});
            skLineSegment(sketch, "E3543", {"start": v(3.46, 86.82) * mm, "end": v(3.6, 85.5) * mm});
            skLineSegment(sketch, "E3544", {"start": v(3.6, 85.5) * mm, "end": v(3.75, 83.81) * mm});
            skLineSegment(sketch, "E3545", {"start": v(3.75, 83.81) * mm, "end": v(3.92, 81.87) * mm});
            skLineSegment(sketch, "E3546", {"start": v(3.92, 81.87) * mm, "end": v(4.09, 79.76) * mm});
            skLineSegment(sketch, "E3547", {"start": v(4.09, 79.76) * mm, "end": v(4.25, 77.58) * mm});
            skLineSegment(sketch, "E3548", {"start": v(4.25, 77.58) * mm, "end": v(4.39, 75.43) * mm});
            skLineSegment(sketch, "E3549", {"start": v(4.39, 75.43) * mm, "end": v(4.5, 73.4) * mm});
            skLineSegment(sketch, "E3550", {"start": v(4.5, 73.4) * mm, "end": v(4.58, 71.6) * mm});
            skLineSegment(sketch, "E3551", {"start": v(4.58, 71.6) * mm, "end": v(4.61, 70.48) * mm});
            skLineSegment(sketch, "E3552", {"start": v(4.61, 70.48) * mm, "end": v(4.62, 69.35) * mm});
            skLineSegment(sketch, "E3553", {"start": v(4.62, 69.35) * mm, "end": v(4.62, 67.1) * mm});
            skLineSegment(sketch, "E3554", {"start": v(4.62, 67.1) * mm, "end": v(4.6, 64.85) * mm});
            skLineSegment(sketch, "E3555", {"start": v(4.6, 64.85) * mm, "end": v(4.58, 62.6) * mm});
            skLineSegment(sketch, "E3556", {"start": v(4.58, 62.6) * mm, "end": v(4.58, 62.05) * mm});
            skLineSegment(sketch, "E3557", {"start": v(4.58, 62.05) * mm, "end": v(4.57, 61.52) * mm});
            skLineSegment(sketch, "E3558", {"start": v(4.57, 61.52) * mm, "end": v(4.55, 61.01) * mm});
            skLineSegment(sketch, "E3559", {"start": v(4.55, 61.01) * mm, "end": v(4.52, 60.52) * mm});
            skLineSegment(sketch, "E3560", {"start": v(4.52, 60.52) * mm, "end": v(4.47, 60.05) * mm});
            skLineSegment(sketch, "E3561", {"start": v(4.47, 60.05) * mm, "end": v(4.4, 59.59) * mm});
            skLineSegment(sketch, "E3562", {"start": v(4.4, 59.59) * mm, "end": v(4.32, 59.15) * mm});
            skLineSegment(sketch, "E3563", {"start": v(4.32, 59.15) * mm, "end": v(4.21, 58.72) * mm});
            skLineSegment(sketch, "E3564", {"start": v(4.21, 58.72) * mm, "end": v(4.15, 58.5) * mm});
            skLineSegment(sketch, "E3565", {"start": v(4.15, 58.5) * mm, "end": v(4.07, 58.3) * mm});
            skLineSegment(sketch, "E3566", {"start": v(4.07, 58.3) * mm, "end": v(4, 58.1) * mm});
            skLineSegment(sketch, "E3567", {"start": v(4, 58.1) * mm, "end": v(3.9, 57.9) * mm});
            skLineSegment(sketch, "E3568", {"start": v(3.9, 57.9) * mm, "end": v(3.8, 57.7) * mm});
            skLineSegment(sketch, "E3569", {"start": v(3.8, 57.7) * mm, "end": v(3.7, 57.51) * mm});
            skLineSegment(sketch, "E3570", {"start": v(3.7, 57.51) * mm, "end": v(3.59, 57.32) * mm});
            skLineSegment(sketch, "E3571", {"start": v(3.59, 57.32) * mm, "end": v(3.46, 57.13) * mm});
            skLineSegment(sketch, "E3572", {"start": v(3.46, 57.13) * mm, "end": v(3.33, 56.94) * mm});
            skLineSegment(sketch, "E3573", {"start": v(3.33, 56.94) * mm, "end": v(3.18, 56.76) * mm});
            skLineSegment(sketch, "E3574", {"start": v(3.18, 56.76) * mm, "end": v(3.03, 56.57) * mm});
            skLineSegment(sketch, "E3575", {"start": v(3.03, 56.57) * mm, "end": v(2.86, 56.4) * mm});
            skLineSegment(sketch, "E3576", {"start": v(2.86, 56.4) * mm, "end": v(2.69, 56.21) * mm});
            skLineSegment(sketch, "E3577", {"start": v(2.69, 56.21) * mm, "end": v(2.5, 56.04) * mm});
            skLineSegment(sketch, "E3578", {"start": v(2.5, 56.04) * mm, "end": v(2.3, 55.86) * mm});
            skLineSegment(sketch, "E3579", {"start": v(2.3, 55.86) * mm, "end": v(2.08, 55.68) * mm});
            skLineSegment(sketch, "E3580", {"start": v(2.08, 55.68) * mm, "end": v(1.97, 55.59) * mm});
            skLineSegment(sketch, "E3581", {"start": v(1.97, 55.59) * mm, "end": v(1.86, 55.48) * mm});
            skLineSegment(sketch, "E3582", {"start": v(1.86, 55.48) * mm, "end": v(1.77, 55.38) * mm});
            skLineSegment(sketch, "E3583", {"start": v(1.77, 55.38) * mm, "end": v(1.68, 55.26) * mm});
            skLineSegment(sketch, "E3584", {"start": v(1.68, 55.26) * mm, "end": v(1.53, 55.03) * mm});
            skLineSegment(sketch, "E3585", {"start": v(1.53, 55.03) * mm, "end": v(1.4, 54.8) * mm});
            skLineSegment(sketch, "E3586", {"start": v(1.4, 54.8) * mm, "end": v(1.3, 54.55) * mm});
            skLineSegment(sketch, "E3587", {"start": v(1.3, 54.55) * mm, "end": v(1.21, 54.3) * mm});
            skLineSegment(sketch, "E3588", {"start": v(1.21, 54.3) * mm, "end": v(1.05, 53.85) * mm});
            skLineSegment(sketch, "E3589", {"start": v(1.05, 53.85) * mm, "end": v(0.97, 53.64) * mm});
            skLineSegment(sketch, "E3590", {"start": v(0.97, 53.64) * mm, "end": v(0.88, 53.45) * mm});
            skLineSegment(sketch, "E3591", {"start": v(0.88, 53.45) * mm, "end": v(0.82, 53.37) * mm});
            skLineSegment(sketch, "E3592", {"start": v(0.82, 53.37) * mm, "end": v(0.77, 53.3) * mm});
            skLineSegment(sketch, "E3593", {"start": v(0.77, 53.3) * mm, "end": v(0.7, 53.23) * mm});
            skLineSegment(sketch, "E3594", {"start": v(0.7, 53.23) * mm, "end": v(0.64, 53.16) * mm});
            skLineSegment(sketch, "E3595", {"start": v(0.64, 53.16) * mm, "end": v(0.56, 53.11) * mm});
            skLineSegment(sketch, "E3596", {"start": v(0.56, 53.11) * mm, "end": v(0.48, 53.07) * mm});
            skLineSegment(sketch, "E3597", {"start": v(0.48, 53.07) * mm, "end": v(0.4, 53.04) * mm});
            skLineSegment(sketch, "E3598", {"start": v(0.4, 53.04) * mm, "end": v(0.3, 53.02) * mm});
            skLineSegment(sketch, "E3599", {"start": v(0.3, 53.02) * mm, "end": v(0.18, 53) * mm});
            skLineSegment(sketch, "E3600", {"start": v(0.18, 53) * mm, "end": v(0.06, 53.01) * mm});
            skLineSegment(sketch, "E3601", {"start": v(0.06, 53.01) * mm, "end": v(-0.07, 53.03) * mm});
            skLineSegment(sketch, "E3602", {"start": v(-0.07, 53.03) * mm, "end": v(-0.21, 53.05) * mm});
            skLineSegment(sketch, "E3603", {"start": v(257.33, 41.39) * mm, "end": v(257.42, 41.63) * mm});
            skLineSegment(sketch, "E3604", {"start": v(257.42, 41.63) * mm, "end": v(257.5, 41.9) * mm});
            skLineSegment(sketch, "E3605", {"start": v(257.5, 41.9) * mm, "end": v(257.56, 42.18) * mm});
            skLineSegment(sketch, "E3606", {"start": v(257.56, 42.18) * mm, "end": v(257.6, 42.48) * mm});
            skLineSegment(sketch, "E3607", {"start": v(257.6, 42.48) * mm, "end": v(257.63, 42.8) * mm});
            skLineSegment(sketch, "E3608", {"start": v(257.63, 42.8) * mm, "end": v(257.65, 43.14) * mm});
            skLineSegment(sketch, "E3609", {"start": v(257.65, 43.14) * mm, "end": v(257.66, 43.5) * mm});
            skLineSegment(sketch, "E3610", {"start": v(257.66, 43.5) * mm, "end": v(257.66, 43.86) * mm});
            skLineSegment(sketch, "E3611", {"start": v(257.66, 43.86) * mm, "end": v(257.62, 44.64) * mm});
            skLineSegment(sketch, "E3612", {"start": v(257.62, 44.64) * mm, "end": v(257.56, 45.47) * mm});
            skLineSegment(sketch, "E3613", {"start": v(257.56, 45.47) * mm, "end": v(257.39, 47.22) * mm});
            skLineSegment(sketch, "E3614", {"start": v(257.39, 47.22) * mm, "end": v(257.3, 48.14) * mm});
            skLineSegment(sketch, "E3615", {"start": v(257.3, 48.14) * mm, "end": v(257.21, 49.06) * mm});
            skLineSegment(sketch, "E3616", {"start": v(257.21, 49.06) * mm, "end": v(257.14, 50) * mm});
            skLineSegment(sketch, "E3617", {"start": v(257.14, 50) * mm, "end": v(257.1, 50.92) * mm});
            skLineSegment(sketch, "E3618", {"start": v(257.1, 50.92) * mm, "end": v(257.08, 51.37) * mm});
            skLineSegment(sketch, "E3619", {"start": v(257.08, 51.37) * mm, "end": v(257.08, 51.83) * mm});
            skLineSegment(sketch, "E3620", {"start": v(257.08, 51.83) * mm, "end": v(257.1, 52.27) * mm});
            skLineSegment(sketch, "E3621", {"start": v(257.1, 52.27) * mm, "end": v(257.11, 52.71) * mm});
            skLineSegment(sketch, "E3622", {"start": v(257.11, 52.71) * mm, "end": v(257.14, 53.15) * mm});
            skLineSegment(sketch, "E3623", {"start": v(257.14, 53.15) * mm, "end": v(257.2, 53.57) * mm});
            skLineSegment(sketch, "E3624", {"start": v(257.2, 53.57) * mm, "end": v(257.25, 53.98) * mm});
            skLineSegment(sketch, "E3625", {"start": v(257.25, 53.98) * mm, "end": v(257.33, 54.39) * mm});
            skLineSegment(sketch, "E3626", {"start": v(257.33, 54.39) * mm, "end": v(257.42, 54.79) * mm});
            skLineSegment(sketch, "E3627", {"start": v(257.42, 54.79) * mm, "end": v(257.53, 55.19) * mm});
            skLineSegment(sketch, "E3628", {"start": v(257.53, 55.19) * mm, "end": v(257.64, 55.59) * mm});
            skLineSegment(sketch, "E3629", {"start": v(257.64, 55.59) * mm, "end": v(257.76, 55.98) * mm});
            skLineSegment(sketch, "E3630", {"start": v(257.76, 55.98) * mm, "end": v(257.9, 56.37) * mm});
            skLineSegment(sketch, "E3631", {"start": v(257.9, 56.37) * mm, "end": v(258.03, 56.76) * mm});
            skLineSegment(sketch, "E3632", {"start": v(258.03, 56.76) * mm, "end": v(258.33, 57.53) * mm});
            skLineSegment(sketch, "E3633", {"start": v(258.33, 57.53) * mm, "end": v(258.65, 58.29) * mm});
            skLineSegment(sketch, "E3634", {"start": v(258.65, 58.29) * mm, "end": v(259, 59.04) * mm});
            skLineSegment(sketch, "E3635", {"start": v(259, 59.04) * mm, "end": v(259.37, 59.79) * mm});
            skLineSegment(sketch, "E3636", {"start": v(259.37, 59.79) * mm, "end": v(259.75, 60.53) * mm});
            skLineSegment(sketch, "E3637", {"start": v(259.75, 60.53) * mm, "end": v(260.53, 62) * mm});
            skLineSegment(sketch, "E3638", {"start": v(260.53, 62) * mm, "end": v(261.33, 63.48) * mm});
            skLineSegment(sketch, "E3639", {"start": v(261.33, 63.48) * mm, "end": v(261.73, 64.22) * mm});
            skLineSegment(sketch, "E3640", {"start": v(261.73, 64.22) * mm, "end": v(262.1, 64.96) * mm});
            skLineSegment(sketch, "E3641", {"start": v(262.1, 64.96) * mm, "end": v(262.48, 65.71) * mm});
            skLineSegment(sketch, "E3642", {"start": v(262.48, 65.71) * mm, "end": v(262.84, 66.46) * mm});
            skLineSegment(sketch, "E3643", {"start": v(-21.42, 108.97) * mm, "end": v(-21.42, 108.97) * mm});
            skLineSegment(sketch, "E3644", {"start": v(99.65, 62.97) * mm, "end": v(99.65, 62.97) * mm});
            skLineSegment(sketch, "E3645", {"start": v(95.44, 66.93) * mm, "end": v(95.44, 66.93) * mm});
            skLineSegment(sketch, "E3646", {"start": v(198.27, 75.67) * mm, "end": v(198.27, 75.67) * mm});
            skArc(sketch, "E3647", {"start": v(73.58, 74.15) * mm, "mid": v(73, 73.57) * mm, "end": v(73.35, 72.82) * mm});
            skArc(sketch, "E3648", {"start": v(73.35, 72.82) * mm, "mid": v(74.58, 72.49) * mm, "end": v(75.81, 72.84) * mm});
            skArc(sketch, "E3649", {"start": v(75.81, 72.84) * mm, "mid": v(76.08, 73.3) * mm, "end": v(75.8, 73.77) * mm});
            skArc(sketch, "E3650", {"start": v(75.8, 73.77) * mm, "mid": v(74.73, 74.16) * mm, "end": v(73.58, 74.15) * mm});
            skArc(sketch, "E3651", {"start": v(76.67, 71.83) * mm, "mid": v(76.28, 71.03) * mm, "end": v(77.07, 70.62) * mm});
            skArc(sketch, "E3652", {"start": v(77.07, 70.62) * mm, "mid": v(77.5, 71.4) * mm, "end": v(76.75, 71.86) * mm});
            skArc(sketch, "E3653", {"start": v(76.75, 71.86) * mm, "mid": v(76.74, 71.86) * mm, "end": v(76.73, 71.85) * mm});
            skArc(sketch, "E3654", {"start": v(76.73, 71.85) * mm, "mid": v(76.7, 71.84) * mm, "end": v(76.67, 71.83) * mm});
            skArc(sketch, "E3655", {"start": v(64.14, 78.44) * mm, "mid": v(64.05, 77.46) * mm, "end": v(64.96, 77.1) * mm});
            skArc(sketch, "E3656", {"start": v(64.96, 77.1) * mm, "mid": v(65.5, 77.97) * mm, "end": v(64.7, 78.6) * mm});
            skArc(sketch, "E3657", {"start": v(64.7, 78.6) * mm, "mid": v(64.49, 78.57) * mm, "end": v(64.28, 78.52) * mm});
            skArc(sketch, "E3658", {"start": v(64.28, 78.52) * mm, "mid": v(64.2, 78.49) * mm, "end": v(64.14, 78.44) * mm});
            skArc(sketch, "E3659", {"start": v(72.3, 83.86) * mm, "mid": v(72.2, 83.34) * mm, "end": v(72.63, 83.02) * mm});
            skArc(sketch, "E3660", {"start": v(72.63, 83.02) * mm, "mid": v(73.1, 83.26) * mm, "end": v(73.07, 83.8) * mm});
            skArc(sketch, "E3661", {"start": v(73.07, 83.8) * mm, "mid": v(72.9, 83.94) * mm, "end": v(72.69, 84) * mm});
            skArc(sketch, "E3662", {"start": v(72.69, 84) * mm, "mid": v(72.48, 83.98) * mm, "end": v(72.3, 83.86) * mm});
            skArc(sketch, "E3663", {"start": v(69.91, 82.72) * mm, "mid": v(69.37, 81.8) * mm, "end": v(70.26, 81.22) * mm});
            skArc(sketch, "E3664", {"start": v(70.26, 81.22) * mm, "mid": v(70.89, 82.07) * mm, "end": v(70.07, 82.75) * mm});
            skArc(sketch, "E3665", {"start": v(70.07, 82.75) * mm, "mid": v(70.04, 82.75) * mm, "end": v(70, 82.74) * mm});
            skArc(sketch, "E3666", {"start": v(70, 82.74) * mm, "mid": v(69.96, 82.73) * mm, "end": v(69.91, 82.72) * mm});
            skArc(sketch, "E3667", {"start": v(51.48, 76.08) * mm, "mid": v(52, 75.47) * mm, "end": v(52.64, 75.94) * mm});
            skArc(sketch, "E3668", {"start": v(52.64, 75.94) * mm, "mid": v(52.2, 76.61) * mm, "end": v(51.5, 76.2) * mm});
            skArc(sketch, "E3669", {"start": v(51.5, 76.2) * mm, "mid": v(51.5, 76.16) * mm, "end": v(51.49, 76.12) * mm});
            skArc(sketch, "E3670", {"start": v(51.49, 76.12) * mm, "mid": v(51.48, 76.1) * mm, "end": v(51.48, 76.08) * mm});
            skArc(sketch, "E3671", {"start": v(46.34, 85.7) * mm, "mid": v(46.62, 85.96) * mm, "end": v(46.42, 86.27) * mm});
            skArc(sketch, "E3672", {"start": v(46.42, 86.27) * mm, "mid": v(46.03, 86.2) * mm, "end": v(45.86, 85.84) * mm});
            skArc(sketch, "E3673", {"start": v(45.86, 85.84) * mm, "mid": v(45.88, 85.8) * mm, "end": v(45.92, 85.77) * mm});
            skArc(sketch, "E3674", {"start": v(45.92, 85.77) * mm, "mid": v(46.13, 85.72) * mm, "end": v(46.34, 85.7) * mm});
            skArc(sketch, "E3675", {"start": v(46.06, 87.6) * mm, "mid": v(46.25, 87.9) * mm, "end": v(46, 88.18) * mm});
            skArc(sketch, "E3676", {"start": v(46, 88.18) * mm, "mid": v(45.62, 88.09) * mm, "end": v(45.44, 87.73) * mm});
            skArc(sketch, "E3677", {"start": v(45.44, 87.73) * mm, "mid": v(45.48, 87.6) * mm, "end": v(45.59, 87.54) * mm});
            skArc(sketch, "E3678", {"start": v(45.59, 87.54) * mm, "mid": v(45.83, 87.53) * mm, "end": v(46.06, 87.6) * mm});
            skArc(sketch, "E3679", {"start": v(56.22, 98.3) * mm, "mid": v(56.95, 98.3) * mm, "end": v(57.21, 98.97) * mm});
            skArc(sketch, "E3680", {"start": v(57.21, 98.97) * mm, "mid": v(56.72, 99.54) * mm, "end": v(55.97, 99.44) * mm});
            skArc(sketch, "E3681", {"start": v(55.97, 99.44) * mm, "mid": v(55.8, 99.22) * mm, "end": v(55.79, 98.95) * mm});
            skArc(sketch, "E3682", {"start": v(55.79, 98.95) * mm, "mid": v(55.94, 98.58) * mm, "end": v(56.22, 98.3) * mm});
            skArc(sketch, "E3683", {"start": v(63.32, 95.82) * mm, "mid": v(63.72, 95.96) * mm, "end": v(63.76, 96.39) * mm});
            skArc(sketch, "E3684", {"start": v(63.76, 96.39) * mm, "mid": v(63.38, 96.57) * mm, "end": v(63.08, 96.26) * mm});
            skArc(sketch, "E3685", {"start": v(63.08, 96.26) * mm, "mid": v(63.09, 96.1) * mm, "end": v(63.14, 95.96) * mm});
            skArc(sketch, "E3686", {"start": v(63.14, 95.96) * mm, "mid": v(63.21, 95.87) * mm, "end": v(63.32, 95.82) * mm});
            skArc(sketch, "E3687", {"start": v(62.95, 97.45) * mm, "mid": v(63.68, 97.41) * mm, "end": v(63.78, 98.13) * mm});
            skArc(sketch, "E3688", {"start": v(63.78, 98.13) * mm, "mid": v(63.09, 98.3) * mm, "end": v(62.83, 97.64) * mm});
            skArc(sketch, "E3689", {"start": v(62.83, 97.64) * mm, "mid": v(62.84, 97.6) * mm, "end": v(62.87, 97.56) * mm});
            skArc(sketch, "E3690", {"start": v(62.87, 97.56) * mm, "mid": v(62.9, 97.5) * mm, "end": v(62.95, 97.45) * mm});
            skArc(sketch, "E3691", {"start": v(46.18, 77.98) * mm, "mid": v(46.92, 78.15) * mm, "end": v(47.29, 78.82) * mm});
            skArc(sketch, "E3692", {"start": v(47.29, 78.82) * mm, "mid": v(47.9, 79.47) * mm, "end": v(48.66, 79) * mm});
            skArc(sketch, "E3693", {"start": v(48.66, 79) * mm, "mid": v(48.98, 77.7) * mm, "end": v(49.1, 76.38) * mm});
            skArc(sketch, "E3694", {"start": v(49.1, 76.38) * mm, "mid": v(49.21, 76.1) * mm, "end": v(49.5, 75.98) * mm});
            skArc(sketch, "E3695", {"start": v(49.5, 75.98) * mm, "mid": v(49.8, 76.1) * mm, "end": v(49.9, 76.4) * mm});
            skArc(sketch, "E3696", {"start": v(49.9, 76.4) * mm, "mid": v(50.15, 78.01) * mm, "end": v(50.88, 79.48) * mm});
            skArc(sketch, "E3697", {"start": v(50.88, 79.48) * mm, "mid": v(51.33, 79.72) * mm, "end": v(51.8, 79.54) * mm});
            skArc(sketch, "E3698", {"start": v(51.8, 79.54) * mm, "mid": v(51.87, 79.45) * mm, "end": v(51.9, 79.34) * mm});
            skArc(sketch, "E3699", {"start": v(51.9, 79.34) * mm, "mid": v(52.07, 78.92) * mm, "end": v(52.37, 78.58) * mm});
            skArc(sketch, "E3700", {"start": v(52.37, 78.58) * mm, "mid": v(53.08, 78.27) * mm, "end": v(53.84, 78.34) * mm});
            skArc(sketch, "E3701", {"start": v(53.84, 78.34) * mm, "mid": v(54.03, 78.32) * mm, "end": v(54.14, 78.16) * mm});
            skArc(sketch, "E3702", {"start": v(54.14, 78.16) * mm, "mid": v(54.09, 77.98) * mm, "end": v(53.91, 77.9) * mm});
            skArc(sketch, "E3703", {"start": v(53.91, 77.9) * mm, "mid": v(53.7, 77.79) * mm, "end": v(53.7, 77.55) * mm});
            skArc(sketch, "E3704", {"start": v(53.7, 77.55) * mm, "mid": v(53.9, 77.42) * mm, "end": v(54.11, 77.54) * mm});
            skArc(sketch, "E3705", {"start": v(54.11, 77.54) * mm, "mid": v(54.46, 77.75) * mm, "end": v(54.84, 77.61) * mm});
            skArc(sketch, "E3706", {"start": v(54.84, 77.61) * mm, "mid": v(55.1, 76.7) * mm, "end": v(54.51, 75.96) * mm});
            skArc(sketch, "E3707", {"start": v(54.51, 75.96) * mm, "mid": v(53.23, 75.06) * mm, "end": v(52.4, 73.74) * mm});
            skArc(sketch, "E3708", {"start": v(52.4, 73.74) * mm, "mid": v(52.42, 73.36) * mm, "end": v(52.7, 73.11) * mm});
            skArc(sketch, "E3709", {"start": v(52.7, 73.11) * mm, "mid": v(53.08, 73.14) * mm, "end": v(53.32, 73.43) * mm});
            skArc(sketch, "E3710", {"start": v(53.32, 73.43) * mm, "mid": v(54.18, 74.92) * mm, "end": v(55.62, 75.88) * mm});
            skArc(sketch, "E3711", {"start": v(55.62, 75.88) * mm, "mid": v(55.87, 75.89) * mm, "end": v(56.08, 75.75) * mm});
            skArc(sketch, "E3712", {"start": v(56.08, 75.75) * mm, "mid": v(56.55, 75.55) * mm, "end": v(56.97, 75.84) * mm});
            skArc(sketch, "E3713", {"start": v(56.97, 75.84) * mm, "mid": v(57.41, 76.08) * mm, "end": v(57.8, 75.75) * mm});
            skArc(sketch, "E3714", {"start": v(57.8, 75.75) * mm, "mid": v(58.21, 75.43) * mm, "end": v(58.64, 75.74) * mm});
            skArc(sketch, "E3715", {"start": v(58.64, 75.74) * mm, "mid": v(58.62, 75.87) * mm, "end": v(58.52, 75.94) * mm});
            skArc(sketch, "E3716", {"start": v(58.52, 75.94) * mm, "mid": v(58.38, 76.05) * mm, "end": v(58.36, 76.22) * mm});
            skArc(sketch, "E3717", {"start": v(58.36, 76.22) * mm, "mid": v(58.47, 76.35) * mm, "end": v(58.65, 76.35) * mm});
            skArc(sketch, "E3718", {"start": v(58.65, 76.35) * mm, "mid": v(61.51, 76.49) * mm, "end": v(63.35, 78.69) * mm});
            skArc(sketch, "E3719", {"start": v(63.35, 78.69) * mm, "mid": v(63.7, 79.28) * mm, "end": v(64.27, 79.64) * mm});
            skArc(sketch, "E3720", {"start": v(64.27, 79.64) * mm, "mid": v(64.91, 79.73) * mm, "end": v(65.53, 79.57) * mm});
            skArc(sketch, "E3721", {"start": v(65.53, 79.57) * mm, "mid": v(68.28, 77.99) * mm, "end": v(70.75, 75.99) * mm});
            skArc(sketch, "E3722", {"start": v(70.75, 75.99) * mm, "mid": v(70.99, 75.6) * mm, "end": v(71, 75.14) * mm});
            skArc(sketch, "E3723", {"start": v(71, 75.14) * mm, "mid": v(71.13, 74.52) * mm, "end": v(71.67, 74.2) * mm});
            skArc(sketch, "E3724", {"start": v(71.67, 74.2) * mm, "mid": v(72.27, 74.4) * mm, "end": v(72.53, 74.96) * mm});
            skArc(sketch, "E3725", {"start": v(72.53, 74.96) * mm, "mid": v(72.43, 75.45) * mm, "end": v(72.14, 75.85) * mm});
            skArc(sketch, "E3726", {"start": v(72.14, 75.85) * mm, "mid": v(69.72, 77.93) * mm, "end": v(67.17, 79.85) * mm});
            skArc(sketch, "E3727", {"start": v(67.17, 79.85) * mm, "mid": v(66.62, 80.12) * mm, "end": v(66, 80.2) * mm});
            skArc(sketch, "E3728", {"start": v(66, 80.2) * mm, "mid": v(65.37, 80.6) * mm, "end": v(65.57, 81.33) * mm});
            skArc(sketch, "E3729", {"start": v(65.57, 81.33) * mm, "mid": v(66.39, 81.76) * mm, "end": v(67.31, 81.84) * mm});
            skArc(sketch, "E3730", {"start": v(67.31, 81.84) * mm, "mid": v(68.29, 82.42) * mm, "end": v(68, 83.52) * mm});
            skArc(sketch, "E3731", {"start": v(68, 83.52) * mm, "mid": v(67.52, 84.06) * mm, "end": v(67.27, 84.74) * mm});
            skArc(sketch, "E3732", {"start": v(67.27, 84.74) * mm, "mid": v(67.4, 85.06) * mm, "end": v(67.73, 85.1) * mm});
            skArc(sketch, "E3733", {"start": v(67.73, 85.1) * mm, "mid": v(70.05, 84.4) * mm, "end": v(72.46, 84.36) * mm});
            skArc(sketch, "E3734", {"start": v(72.46, 84.36) * mm, "mid": v(73.1, 84.97) * mm, "end": v(72.7, 85.75) * mm});
            skArc(sketch, "E3735", {"start": v(72.7, 85.75) * mm, "mid": v(71.29, 86.15) * mm, "end": v(69.83, 85.96) * mm});
            skArc(sketch, "E3736", {"start": v(69.83, 85.96) * mm, "mid": v(68.22, 86.23) * mm, "end": v(67.53, 87.7) * mm});
            skArc(sketch, "E3737", {"start": v(67.53, 87.7) * mm, "mid": v(67.67, 88.78) * mm, "end": v(67.97, 89.82) * mm});
            skArc(sketch, "E3738", {"start": v(67.97, 89.82) * mm, "mid": v(68.25, 90.35) * mm, "end": v(68.66, 90.79) * mm});
            skArc(sketch, "E3739", {"start": v(68.66, 90.79) * mm, "mid": v(68.94, 91.3) * mm, "end": v(68.77, 91.84) * mm});
            skArc(sketch, "E3740", {"start": v(68.77, 91.84) * mm, "mid": v(68.23, 92.65) * mm, "end": v(67.85, 93.54) * mm});
            skArc(sketch, "E3741", {"start": v(67.85, 93.54) * mm, "mid": v(67.62, 93.84) * mm, "end": v(67.25, 93.9) * mm});
            skArc(sketch, "E3742", {"start": v(67.25, 93.9) * mm, "mid": v(66.87, 94.08) * mm, "end": v(66.9, 94.5) * mm});
            skArc(sketch, "E3743", {"start": v(66.9, 94.5) * mm, "mid": v(67.73, 95.64) * mm, "end": v(68.52, 96.82) * mm});
            skArc(sketch, "E3744", {"start": v(68.52, 96.82) * mm, "mid": v(68.41, 97.67) * mm, "end": v(67.55, 97.71) * mm});
            skArc(sketch, "E3745", {"start": v(67.55, 97.71) * mm, "mid": v(66.57, 96.62) * mm, "end": v(66.07, 95.24) * mm});
            skArc(sketch, "E3746", {"start": v(66.07, 95.24) * mm, "mid": v(65.6, 94.51) * mm, "end": v(64.76, 94.37) * mm});
            skArc(sketch, "E3747", {"start": v(64.76, 94.37) * mm, "mid": v(64.33, 94.6) * mm, "end": v(64.04, 94.98) * mm});
            skArc(sketch, "E3748", {"start": v(64.04, 94.98) * mm, "mid": v(63.69, 95.35) * mm, "end": v(63.18, 95.4) * mm});
            skArc(sketch, "E3749", {"start": v(63.18, 95.4) * mm, "mid": v(62.64, 95.56) * mm, "end": v(62.52, 96.11) * mm});
            skArc(sketch, "E3750", {"start": v(62.52, 96.11) * mm, "mid": v(62.48, 97.08) * mm, "end": v(61.78, 97.75) * mm});
            skArc(sketch, "E3751", {"start": v(61.78, 97.75) * mm, "mid": v(61.58, 97.94) * mm, "end": v(61.56, 98.22) * mm});
            skArc(sketch, "E3752", {"start": v(61.56, 98.22) * mm, "mid": v(61.39, 98.53) * mm, "end": v(61.07, 98.37) * mm});
            skArc(sketch, "E3753", {"start": v(61.07, 98.37) * mm, "mid": v(60.77, 97.72) * mm, "end": v(60.37, 97.14) * mm});
            skArc(sketch, "E3754", {"start": v(60.37, 97.14) * mm, "mid": v(59.9, 96.9) * mm, "end": v(59.4, 97.07) * mm});
            skArc(sketch, "E3755", {"start": v(59.4, 97.07) * mm, "mid": v(58.86, 97.13) * mm, "end": v(58.64, 96.63) * mm});
            skArc(sketch, "E3756", {"start": v(58.64, 96.63) * mm, "mid": v(58.55, 96.25) * mm, "end": v(58.2, 96.08) * mm});
            skArc(sketch, "E3757", {"start": v(58.2, 96.08) * mm, "mid": v(57.84, 96.25) * mm, "end": v(57.76, 96.64) * mm});
            skArc(sketch, "E3758", {"start": v(57.76, 96.64) * mm, "mid": v(57.88, 97.09) * mm, "end": v(58.02, 97.53) * mm});
            skArc(sketch, "E3759", {"start": v(58.02, 97.53) * mm, "mid": v(57.92, 97.95) * mm, "end": v(57.5, 98.07) * mm});
            skArc(sketch, "E3760", {"start": v(57.5, 98.07) * mm, "mid": v(57.16, 98) * mm, "end": v(56.8, 97.92) * mm});
            skArc(sketch, "E3761", {"start": v(56.8, 97.92) * mm, "mid": v(56.55, 97.73) * mm, "end": v(56.55, 97.42) * mm});
            skArc(sketch, "E3762", {"start": v(56.55, 97.42) * mm, "mid": v(56.44, 97.05) * mm, "end": v(56.06, 97.11) * mm});
            skArc(sketch, "E3763", {"start": v(56.06, 97.11) * mm, "mid": v(55.94, 97.53) * mm, "end": v(56.15, 97.92) * mm});
            skArc(sketch, "E3764", {"start": v(56.15, 97.92) * mm, "mid": v(56.28, 98.2) * mm, "end": v(56.13, 98.48) * mm});
            skArc(sketch, "E3765", {"start": v(56.13, 98.48) * mm, "mid": v(55.8, 98.55) * mm, "end": v(55.53, 98.35) * mm});
            skArc(sketch, "E3766", {"start": v(55.53, 98.35) * mm, "mid": v(54.7, 97.1) * mm, "end": v(53.69, 95.95) * mm});
            skArc(sketch, "E3767", {"start": v(53.69, 95.95) * mm, "mid": v(53.4, 95.86) * mm, "end": v(53.16, 96.02) * mm});
            skArc(sketch, "E3768", {"start": v(53.16, 96.02) * mm, "mid": v(53, 96.52) * mm, "end": v(53.08, 97.03) * mm});
            skArc(sketch, "E3769", {"start": v(53.08, 97.03) * mm, "mid": v(53.04, 97.51) * mm, "end": v(52.63, 97.76) * mm});
            skArc(sketch, "E3770", {"start": v(52.63, 97.76) * mm, "mid": v(52.18, 97.58) * mm, "end": v(52.07, 97.12) * mm});
            skArc(sketch, "E3771", {"start": v(52.07, 97.12) * mm, "mid": v(52.5, 96.15) * mm, "end": v(53.28, 95.44) * mm});
            skArc(sketch, "E3772", {"start": v(53.28, 95.44) * mm, "mid": v(53.6, 94.94) * mm, "end": v(53.39, 94.38) * mm});
            skArc(sketch, "E3773", {"start": v(53.39, 94.38) * mm, "mid": v(52.8, 94.23) * mm, "end": v(52.35, 94.62) * mm});
            skArc(sketch, "E3774", {"start": v(52.35, 94.62) * mm, "mid": v(52.31, 94.76) * mm, "end": v(52.34, 94.9) * mm});
            skArc(sketch, "E3775", {"start": v(52.34, 94.9) * mm, "mid": v(52.26, 95.09) * mm, "end": v(52.07, 95.01) * mm});
            skArc(sketch, "E3776", {"start": v(52.07, 95.01) * mm, "mid": v(51.97, 94.87) * mm, "end": v(51.82, 94.78) * mm});
            skArc(sketch, "E3777", {"start": v(51.82, 94.78) * mm, "mid": v(51.71, 94.77) * mm, "end": v(51.63, 94.84) * mm});
            skArc(sketch, "E3778", {"start": v(51.63, 94.84) * mm, "mid": v(51.5, 94.96) * mm, "end": v(51.34, 95) * mm});
            skArc(sketch, "E3779", {"start": v(51.34, 95) * mm, "mid": v(51.24, 94.96) * mm, "end": v(51.22, 94.85) * mm});
            skArc(sketch, "E3780", {"start": v(51.22, 94.85) * mm, "mid": v(51.37, 94.55) * mm, "end": v(51.57, 94.29) * mm});
            skArc(sketch, "E3781", {"start": v(51.57, 94.29) * mm, "mid": v(51.62, 94.14) * mm, "end": v(51.54, 94) * mm});
            skArc(sketch, "E3782", {"start": v(51.54, 94) * mm, "mid": v(51.39, 93.96) * mm, "end": v(51.25, 94.04) * mm});
            skArc(sketch, "E3783", {"start": v(51.25, 94.04) * mm, "mid": v(50.24, 95.84) * mm, "end": v(49.45, 97.74) * mm});
            skArc(sketch, "E3784", {"start": v(49.45, 97.74) * mm, "mid": v(49.1, 98.19) * mm, "end": v(48.54, 98.3) * mm});
            skArc(sketch, "E3785", {"start": v(48.54, 98.3) * mm, "mid": v(48.09, 97.9) * mm, "end": v(48.28, 97.34) * mm});
            skArc(sketch, "E3786", {"start": v(48.28, 97.34) * mm, "mid": v(49.58, 96) * mm, "end": v(50.43, 94.35) * mm});
            skArc(sketch, "E3787", {"start": v(50.43, 94.35) * mm, "mid": v(50.42, 94.23) * mm, "end": v(50.33, 94.16) * mm});
            skArc(sketch, "E3788", {"start": v(50.33, 94.16) * mm, "mid": v(49.96, 93.8) * mm, "end": v(50.16, 93.31) * mm});
            skArc(sketch, "E3789", {"start": v(50.16, 93.31) * mm, "mid": v(50.26, 93.17) * mm, "end": v(50.22, 93) * mm});
            skArc(sketch, "E3790", {"start": v(50.22, 93) * mm, "mid": v(49.99, 92.81) * mm, "end": v(49.7, 92.73) * mm});
            skArc(sketch, "E3791", {"start": v(49.7, 92.73) * mm, "mid": v(48.9, 92.67) * mm, "end": v(48.1, 92.57) * mm});
            skArc(sketch, "E3792", {"start": v(48.1, 92.57) * mm, "mid": v(47.79, 92.32) * mm, "end": v(47.83, 91.92) * mm});
            skArc(sketch, "E3793", {"start": v(47.83, 91.92) * mm, "mid": v(47.84, 91.53) * mm, "end": v(47.48, 91.4) * mm});
            skArc(sketch, "E3794", {"start": v(47.48, 91.4) * mm, "mid": v(46.8, 91.13) * mm, "end": v(46.85, 90.4) * mm});
            skArc(sketch, "E3795", {"start": v(46.85, 90.4) * mm, "mid": v(47.27, 90.02) * mm, "end": v(47.77, 89.76) * mm});
            skArc(sketch, "E3796", {"start": v(47.77, 89.76) * mm, "mid": v(48.22, 89.38) * mm, "end": v(48.32, 88.8) * mm});
            skArc(sketch, "E3797", {"start": v(48.32, 88.8) * mm, "mid": v(48.2, 88.39) * mm, "end": v(48, 88) * mm});
            skArc(sketch, "E3798", {"start": v(48, 88) * mm, "mid": v(47.74, 87.84) * mm, "end": v(47.44, 87.95) * mm});
            skArc(sketch, "E3799", {"start": v(47.44, 87.95) * mm, "mid": v(47.24, 88.1) * mm, "end": v(47, 88.18) * mm});
            skArc(sketch, "E3800", {"start": v(47, 88.18) * mm, "mid": v(46.9, 88.14) * mm, "end": v(46.88, 88.04) * mm});
            skArc(sketch, "E3801", {"start": v(46.88, 88.04) * mm, "mid": v(46.93, 87.93) * mm, "end": v(47, 87.83) * mm});
            skArc(sketch, "E3802", {"start": v(47, 87.83) * mm, "mid": v(47.04, 87.69) * mm, "end": v(46.91, 87.6) * mm});
            skArc(sketch, "E3803", {"start": v(46.91, 87.6) * mm, "mid": v(46.25, 87.1) * mm, "end": v(46.67, 86.37) * mm});
            skArc(sketch, "E3804", {"start": v(46.67, 86.37) * mm, "mid": v(46.92, 86.06) * mm, "end": v(46.76, 85.7) * mm});
            skArc(sketch, "E3805", {"start": v(46.76, 85.7) * mm, "mid": v(46.5, 85.36) * mm, "end": v(46.5, 84.93) * mm});
            skArc(sketch, "E3806", {"start": v(46.5, 84.93) * mm, "mid": v(46.88, 84.36) * mm, "end": v(47.52, 84.09) * mm});
            skArc(sketch, "E3807", {"start": v(47.52, 84.09) * mm, "mid": v(47.56, 84.08) * mm, "end": v(47.6, 84.07) * mm});
            skArc(sketch, "E3808", {"start": v(47.6, 84.07) * mm, "mid": v(47.6, 84.06) * mm, "end": v(47.6, 84.06) * mm});
            skLineSegment(sketch, "E3809", {"start": v(47.6, 84.06) * mm, "end": v(47.7, 84.04) * mm});
            skArc(sketch, "E3810", {"start": v(47.7, 84.04) * mm, "mid": v(47.6, 83.7) * mm, "end": v(47.41, 83.39) * mm});
            skArc(sketch, "E3811", {"start": v(47.41, 83.39) * mm, "mid": v(47.28, 83.3) * mm, "end": v(47.12, 83.32) * mm});
            skArc(sketch, "E3812", {"start": v(47.12, 83.32) * mm, "mid": v(46.33, 83.47) * mm, "end": v(45.55, 83.28) * mm});
            skArc(sketch, "E3813", {"start": v(45.55, 83.28) * mm, "mid": v(45.34, 82.9) * mm, "end": v(45.6, 82.56) * mm});
            skArc(sketch, "E3814", {"start": v(45.6, 82.56) * mm, "mid": v(45.74, 82.55) * mm, "end": v(45.87, 82.61) * mm});
            skArc(sketch, "E3815", {"start": v(45.87, 82.61) * mm, "mid": v(46.56, 82.6) * mm, "end": v(46.6, 81.9) * mm});
            skArc(sketch, "E3816", {"start": v(46.6, 81.9) * mm, "mid": v(45.78, 80.57) * mm, "end": v(45.39, 79.06) * mm});
            skArc(sketch, "E3817", {"start": v(45.39, 79.06) * mm, "mid": v(45.58, 78.37) * mm, "end": v(46.18, 77.98) * mm});
            skArc(sketch, "E3818", {"start": v(213.5, 75.95) * mm, "mid": v(213.58, 75.97) * mm, "end": v(213.66, 75.93) * mm});
            skArc(sketch, "E3819", {"start": v(213.66, 75.93) * mm, "mid": v(213.77, 75.79) * mm, "end": v(213.83, 75.62) * mm});
            skArc(sketch, "E3820", {"start": v(213.83, 75.62) * mm, "mid": v(213.7, 75.33) * mm, "end": v(213.4, 75.37) * mm});
            skArc(sketch, "E3821", {"start": v(213.4, 75.37) * mm, "mid": v(213.3, 75.69) * mm, "end": v(213.5, 75.95) * mm});
            skArc(sketch, "E3822", {"start": v(219.62, 74.8) * mm, "mid": v(219.74, 74.81) * mm, "end": v(219.84, 74.74) * mm});
            skArc(sketch, "E3823", {"start": v(219.84, 74.74) * mm, "mid": v(219.88, 74.62) * mm, "end": v(219.84, 74.5) * mm});
            skArc(sketch, "E3824", {"start": v(219.84, 74.5) * mm, "mid": v(219.68, 74.42) * mm, "end": v(219.53, 74.5) * mm});
            skArc(sketch, "E3825", {"start": v(219.53, 74.5) * mm, "mid": v(219.5, 74.68) * mm, "end": v(219.62, 74.8) * mm});
            skArc(sketch, "E3826", {"start": v(221.36, 74.6) * mm, "mid": v(221.44, 74.63) * mm, "end": v(221.53, 74.62) * mm});
            skArc(sketch, "E3827", {"start": v(221.53, 74.62) * mm, "mid": v(221.59, 74.59) * mm, "end": v(221.63, 74.53) * mm});
            skArc(sketch, "E3828", {"start": v(221.63, 74.53) * mm, "mid": v(221.6, 74.33) * mm, "end": v(221.4, 74.27) * mm});
            skArc(sketch, "E3829", {"start": v(221.4, 74.27) * mm, "mid": v(221.26, 74.42) * mm, "end": v(221.36, 74.6) * mm});
            skArc(sketch, "E3830", {"start": v(216.66, 76.04) * mm, "mid": v(216.9, 76.2) * mm, "end": v(217.14, 76.07) * mm});
            skArc(sketch, "E3831", {"start": v(217.14, 76.07) * mm, "mid": v(217.3, 75.22) * mm, "end": v(216.92, 74.45) * mm});
            skArc(sketch, "E3832", {"start": v(216.92, 74.45) * mm, "mid": v(216.72, 74.03) * mm, "end": v(216.8, 73.58) * mm});
            skArc(sketch, "E3833", {"start": v(216.8, 73.58) * mm, "mid": v(216.95, 73.53) * mm, "end": v(217.02, 73.66) * mm});
            skArc(sketch, "E3834", {"start": v(217.02, 73.66) * mm, "mid": v(217.08, 73.79) * mm, "end": v(217.22, 73.77) * mm});
            skArc(sketch, "E3835", {"start": v(217.22, 73.77) * mm, "mid": v(217.39, 73.75) * mm, "end": v(217.46, 73.9) * mm});
            skArc(sketch, "E3836", {"start": v(217.46, 73.9) * mm, "mid": v(217.5, 74.04) * mm, "end": v(217.65, 74.08) * mm});
            skArc(sketch, "E3837", {"start": v(217.65, 74.08) * mm, "mid": v(218.3, 74.07) * mm, "end": v(218.9, 74.32) * mm});
            skArc(sketch, "E3838", {"start": v(218.9, 74.32) * mm, "mid": v(219.1, 74.3) * mm, "end": v(219.16, 74.1) * mm});
            skArc(sketch, "E3839", {"start": v(219.16, 74.1) * mm, "mid": v(219.28, 73.76) * mm, "end": v(219.64, 73.8) * mm});
            skArc(sketch, "E3840", {"start": v(219.64, 73.8) * mm, "mid": v(219.89, 74.04) * mm, "end": v(220.15, 74.27) * mm});
            skArc(sketch, "E3841", {"start": v(220.15, 74.27) * mm, "mid": v(220.24, 74.3) * mm, "end": v(220.31, 74.24) * mm});
            skArc(sketch, "E3842", {"start": v(220.31, 74.24) * mm, "mid": v(220.38, 74.1) * mm, "end": v(220.43, 73.95) * mm});
            skArc(sketch, "E3843", {"start": v(220.43, 73.95) * mm, "mid": v(220.5, 73.8) * mm, "end": v(220.57, 73.67) * mm});
            skArc(sketch, "E3844", {"start": v(220.57, 73.67) * mm, "mid": v(220.57, 73.6) * mm, "end": v(220.5, 73.61) * mm});
            skArc(sketch, "E3845", {"start": v(220.5, 73.61) * mm, "mid": v(220.4, 73.74) * mm, "end": v(220.33, 73.88) * mm});
            skArc(sketch, "E3846", {"start": v(220.33, 73.88) * mm, "mid": v(220.27, 73.95) * mm, "end": v(220.18, 73.97) * mm});
            skArc(sketch, "E3847", {"start": v(220.18, 73.97) * mm, "mid": v(220.1, 73.91) * mm, "end": v(220.1, 73.8) * mm});
            skArc(sketch, "E3848", {"start": v(220.1, 73.8) * mm, "mid": v(220.38, 73.5) * mm, "end": v(220.76, 73.33) * mm});
            skArc(sketch, "E3849", {"start": v(220.76, 73.33) * mm, "mid": v(220.85, 73.35) * mm, "end": v(220.9, 73.43) * mm});
            skArc(sketch, "E3850", {"start": v(220.9, 73.43) * mm, "mid": v(220.86, 73.52) * mm, "end": v(220.77, 73.54) * mm});
            skArc(sketch, "E3851", {"start": v(220.77, 73.54) * mm, "mid": v(220.7, 73.56) * mm, "end": v(220.68, 73.62) * mm});
            skArc(sketch, "E3852", {"start": v(220.68, 73.62) * mm, "mid": v(220.77, 73.8) * mm, "end": v(220.96, 73.8) * mm});
            skArc(sketch, "E3853", {"start": v(220.96, 73.8) * mm, "mid": v(221.11, 73.64) * mm, "end": v(221.1, 73.41) * mm});
            skArc(sketch, "E3854", {"start": v(221.1, 73.41) * mm, "mid": v(221.13, 73.29) * mm, "end": v(221.25, 73.26) * mm});
            skArc(sketch, "E3855", {"start": v(221.25, 73.26) * mm, "mid": v(221.36, 73.28) * mm, "end": v(221.46, 73.25) * mm});
            skArc(sketch, "E3856", {"start": v(221.46, 73.25) * mm, "mid": v(221.48, 73.21) * mm, "end": v(221.47, 73.18) * mm});
            skArc(sketch, "E3857", {"start": v(221.47, 73.18) * mm, "mid": v(221.31, 73.06) * mm, "end": v(221.14, 72.97) * mm});
            skArc(sketch, "E3858", {"start": v(221.14, 72.97) * mm, "mid": v(220.86, 72.6) * mm, "end": v(221.06, 72.18) * mm});
            skArc(sketch, "E3859", {"start": v(221.06, 72.18) * mm, "mid": v(221.4, 71.95) * mm, "end": v(221.77, 71.74) * mm});
            skArc(sketch, "E3860", {"start": v(221.77, 71.74) * mm, "mid": v(222.8, 71.68) * mm, "end": v(223.54, 72.4) * mm});
            skArc(sketch, "E3861", {"start": v(223.54, 72.4) * mm, "mid": v(223.7, 72.6) * mm, "end": v(223.96, 72.63) * mm});
            skArc(sketch, "E3862", {"start": v(223.96, 72.63) * mm, "mid": v(224.05, 72.64) * mm, "end": v(224.1, 72.72) * mm});
            skArc(sketch, "E3863", {"start": v(224.1, 72.72) * mm, "mid": v(224.17, 72.8) * mm, "end": v(224.27, 72.78) * mm});
            skArc(sketch, "E3864", {"start": v(224.27, 72.78) * mm, "mid": v(224.5, 72.38) * mm, "end": v(224.4, 71.93) * mm});
            skArc(sketch, "E3865", {"start": v(224.4, 71.93) * mm, "mid": v(224.47, 71.37) * mm, "end": v(225.04, 71.36) * mm});
            skArc(sketch, "E3866", {"start": v(225.04, 71.36) * mm, "mid": v(225.3, 71.4) * mm, "end": v(225.47, 71.2) * mm});
            skArc(sketch, "E3867", {"start": v(225.47, 71.2) * mm, "mid": v(225.44, 70.68) * mm, "end": v(225.21, 70.22) * mm});
            skArc(sketch, "E3868", {"start": v(225.21, 70.22) * mm, "mid": v(225.08, 69.87) * mm, "end": v(225.15, 69.5) * mm});
            skArc(sketch, "E3869", {"start": v(225.15, 69.5) * mm, "mid": v(225.2, 69.31) * mm, "end": v(225.12, 69.12) * mm});
            skArc(sketch, "E3870", {"start": v(225.12, 69.12) * mm, "mid": v(225.06, 68.9) * mm, "end": v(225.18, 68.7) * mm});
            skArc(sketch, "E3871", {"start": v(225.18, 68.7) * mm, "mid": v(225.4, 68.67) * mm, "end": v(225.6, 68.8) * mm});
            skArc(sketch, "E3872", {"start": v(225.6, 68.8) * mm, "mid": v(225.97, 68.92) * mm, "end": v(226.1, 68.56) * mm});
            skArc(sketch, "E3873", {"start": v(226.1, 68.56) * mm, "mid": v(226.2, 68.15) * mm, "end": v(226.61, 68.08) * mm});
            skArc(sketch, "E3874", {"start": v(226.61, 68.08) * mm, "mid": v(227.8, 68.5) * mm, "end": v(229.02, 68.73) * mm});
            skArc(sketch, "E3875", {"start": v(229.02, 68.73) * mm, "mid": v(229.77, 68.87) * mm, "end": v(230.47, 69.14) * mm});
            skArc(sketch, "E3876", {"start": v(230.47, 69.14) * mm, "mid": v(230.76, 69.07) * mm, "end": v(230.72, 68.78) * mm});
            skArc(sketch, "E3877", {"start": v(230.72, 68.78) * mm, "mid": v(230.3, 68.5) * mm, "end": v(229.82, 68.35) * mm});
            skArc(sketch, "E3878", {"start": v(229.82, 68.35) * mm, "mid": v(227.86, 67.95) * mm, "end": v(225.94, 67.4) * mm});
            skArc(sketch, "E3879", {"start": v(225.94, 67.4) * mm, "mid": v(225.8, 67.27) * mm, "end": v(225.8, 67.09) * mm});
            skArc(sketch, "E3880", {"start": v(225.8, 67.09) * mm, "mid": v(225.94, 66.97) * mm, "end": v(226.13, 67) * mm});
            skArc(sketch, "E3881", {"start": v(226.13, 67) * mm, "mid": v(226.48, 67.13) * mm, "end": v(226.87, 67.14) * mm});
            skArc(sketch, "E3882", {"start": v(226.87, 67.14) * mm, "mid": v(226.94, 67.08) * mm, "end": v(226.92, 66.99) * mm});
            skArc(sketch, "E3883", {"start": v(226.92, 66.99) * mm, "mid": v(226.72, 66.85) * mm, "end": v(226.5, 66.79) * mm});
            skArc(sketch, "E3884", {"start": v(226.5, 66.79) * mm, "mid": v(226.33, 66.62) * mm, "end": v(226.43, 66.41) * mm});
            skArc(sketch, "E3885", {"start": v(226.43, 66.41) * mm, "mid": v(226.58, 66.3) * mm, "end": v(226.7, 66.14) * mm});
            skArc(sketch, "E3886", {"start": v(226.7, 66.14) * mm, "mid": v(226.7, 66) * mm, "end": v(226.59, 65.91) * mm});
            skArc(sketch, "E3887", {"start": v(226.59, 65.91) * mm, "mid": v(226.45, 65.96) * mm, "end": v(226.41, 66.1) * mm});
            skArc(sketch, "E3888", {"start": v(226.41, 66.1) * mm, "mid": v(226.34, 66.26) * mm, "end": v(226.16, 66.25) * mm});
            skArc(sketch, "E3889", {"start": v(226.16, 66.25) * mm, "mid": v(225.87, 65.9) * mm, "end": v(225.71, 65.48) * mm});
            skArc(sketch, "E3890", {"start": v(225.71, 65.48) * mm, "mid": v(225.76, 65.21) * mm, "end": v(225.97, 65.05) * mm});
            skArc(sketch, "E3891", {"start": v(225.97, 65.05) * mm, "mid": v(226.46, 65) * mm, "end": v(226.9, 65.18) * mm});
            skArc(sketch, "E3892", {"start": v(226.9, 65.18) * mm, "mid": v(227.73, 65.56) * mm, "end": v(228.62, 65.6) * mm});
            skArc(sketch, "E3893", {"start": v(228.62, 65.6) * mm, "mid": v(228.8, 65.47) * mm, "end": v(228.85, 65.26) * mm});
            skArc(sketch, "E3894", {"start": v(228.85, 65.26) * mm, "mid": v(228.71, 65.09) * mm, "end": v(228.5, 65.07) * mm});
            skArc(sketch, "E3895", {"start": v(228.5, 65.07) * mm, "mid": v(227.56, 65.17) * mm, "end": v(226.66, 64.88) * mm});
            skArc(sketch, "E3896", {"start": v(226.66, 64.88) * mm, "mid": v(226.6, 64.69) * mm, "end": v(226.78, 64.6) * mm});
            skArc(sketch, "E3897", {"start": v(226.78, 64.6) * mm, "mid": v(226.96, 64.54) * mm, "end": v(226.95, 64.35) * mm});
            skArc(sketch, "E3898", {"start": v(226.95, 64.35) * mm, "mid": v(226.94, 64.16) * mm, "end": v(227.12, 64.13) * mm});
            skArc(sketch, "E3899", {"start": v(227.12, 64.13) * mm, "mid": v(227.29, 64.14) * mm, "end": v(227.38, 64) * mm});
            skArc(sketch, "E3900", {"start": v(227.38, 64) * mm, "mid": v(227.5, 63.44) * mm, "end": v(227.76, 62.92) * mm});
            skArc(sketch, "E3901", {"start": v(227.76, 62.92) * mm, "mid": v(228.17, 62.4) * mm, "end": v(228.64, 61.9) * mm});
            skArc(sketch, "E3902", {"start": v(228.64, 61.9) * mm, "mid": v(228.73, 61.63) * mm, "end": v(228.55, 61.42) * mm});
            skArc(sketch, "E3903", {"start": v(228.55, 61.42) * mm, "mid": v(228.27, 61.45) * mm, "end": v(228.15, 61.7) * mm});
            skArc(sketch, "E3904", {"start": v(228.15, 61.7) * mm, "mid": v(227.92, 62.18) * mm, "end": v(227.4, 62.27) * mm});
            skArc(sketch, "E3905", {"start": v(227.4, 62.27) * mm, "mid": v(227.08, 61.98) * mm, "end": v(227.1, 61.55) * mm});
            skArc(sketch, "E3906", {"start": v(227.1, 61.55) * mm, "mid": v(227.42, 61.28) * mm, "end": v(227.84, 61.35) * mm});
            skArc(sketch, "E3907", {"start": v(227.84, 61.35) * mm, "mid": v(228.21, 61.29) * mm, "end": v(228.16, 60.91) * mm});
            skArc(sketch, "E3908", {"start": v(228.16, 60.91) * mm, "mid": v(228, 60.73) * mm, "end": v(227.9, 60.5) * mm});
            skArc(sketch, "E3909", {"start": v(227.9, 60.5) * mm, "mid": v(227.87, 60.14) * mm, "end": v(227.93, 59.78) * mm});
            skArc(sketch, "E3910", {"start": v(227.93, 59.78) * mm, "mid": v(227.84, 59.55) * mm, "end": v(227.6, 59.56) * mm});
            skArc(sketch, "E3911", {"start": v(227.6, 59.56) * mm, "mid": v(227.05, 59.97) * mm, "end": v(226.46, 60.32) * mm});
            skArc(sketch, "E3912", {"start": v(226.46, 60.32) * mm, "mid": v(226.02, 60.32) * mm, "end": v(225.8, 59.94) * mm});
            skArc(sketch, "E3913", {"start": v(225.8, 59.94) * mm, "mid": v(226, 59.56) * mm, "end": v(226.44, 59.53) * mm});
            skArc(sketch, "E3914", {"start": v(226.44, 59.53) * mm, "mid": v(226.7, 59.52) * mm, "end": v(226.82, 59.3) * mm});
            skArc(sketch, "E3915", {"start": v(226.82, 59.3) * mm, "mid": v(226.78, 59.04) * mm, "end": v(226.67, 58.81) * mm});
            skArc(sketch, "E3916", {"start": v(226.67, 58.81) * mm, "mid": v(226.58, 58.74) * mm, "end": v(226.46, 58.73) * mm});
            skArc(sketch, "E3917", {"start": v(226.46, 58.73) * mm, "mid": v(226.25, 58.68) * mm, "end": v(226.16, 58.48) * mm});
            skArc(sketch, "E3918", {"start": v(226.16, 58.48) * mm, "mid": v(226.14, 58.3) * mm, "end": v(226.05, 58.12) * mm});
            skArc(sketch, "E3919", {"start": v(226.05, 58.12) * mm, "mid": v(225.97, 57.99) * mm, "end": v(225.92, 57.84) * mm});
            skArc(sketch, "E3920", {"start": v(225.92, 57.84) * mm, "mid": v(225.95, 57.87) * mm, "end": v(225.99, 57.9) * mm});
            skArc(sketch, "E3921", {"start": v(225.99, 57.9) * mm, "mid": v(226.01, 57.9) * mm, "end": v(226.03, 57.92) * mm});
            skArc(sketch, "E3922", {"start": v(226.03, 57.92) * mm, "mid": v(226.06, 57.92) * mm, "end": v(226.09, 57.93) * mm});
            skArc(sketch, "E3923", {"start": v(226.09, 57.93) * mm, "mid": v(226.5, 57.68) * mm, "end": v(226.27, 57.25) * mm});
            skArc(sketch, "E3924", {"start": v(226.27, 57.25) * mm, "mid": v(226.17, 57.23) * mm, "end": v(226.06, 57.25) * mm});
            skArc(sketch, "E3925", {"start": v(226.06, 57.25) * mm, "mid": v(226.2, 57.12) * mm, "end": v(226.37, 57.04) * mm});
            skArc(sketch, "E3926", {"start": v(226.37, 57.04) * mm, "mid": v(226.88, 56.8) * mm, "end": v(227.32, 56.43) * mm});
            skArc(sketch, "E3927", {"start": v(227.32, 56.43) * mm, "mid": v(227.33, 56.25) * mm, "end": v(227.16, 56.2) * mm});
            skArc(sketch, "E3928", {"start": v(227.16, 56.2) * mm, "mid": v(226.89, 56.33) * mm, "end": v(226.63, 56.48) * mm});
            skArc(sketch, "E3929", {"start": v(226.63, 56.48) * mm, "mid": v(226.44, 56.47) * mm, "end": v(226.37, 56.3) * mm});
            skArc(sketch, "E3930", {"start": v(226.37, 56.3) * mm, "mid": v(226.36, 56.2) * mm, "end": v(226.3, 56.14) * mm});
            skArc(sketch, "E3931", {"start": v(226.3, 56.14) * mm, "mid": v(225.29, 55.8) * mm, "end": v(224.22, 55.85) * mm});
            skArc(sketch, "E3932", {"start": v(224.22, 55.85) * mm, "mid": v(223.9, 55.73) * mm, "end": v(223.9, 55.4) * mm});
            skArc(sketch, "E3933", {"start": v(223.9, 55.4) * mm, "mid": v(223.8, 54.94) * mm, "end": v(223.34, 55.02) * mm});
            skArc(sketch, "E3934", {"start": v(223.34, 55.02) * mm, "mid": v(223.17, 55.13) * mm, "end": v(222.97, 55.09) * mm});
            skArc(sketch, "E3935", {"start": v(222.97, 55.09) * mm, "mid": v(222.21, 54.22) * mm, "end": v(221.97, 53.1) * mm});
            skArc(sketch, "E3936", {"start": v(221.97, 53.1) * mm, "mid": v(221.44, 51.96) * mm, "end": v(220.2, 51.73) * mm});
            skArc(sketch, "E3937", {"start": v(220.2, 51.73) * mm, "mid": v(219.13, 52.13) * mm, "end": v(218.1, 52.63) * mm});
            skLineSegment(sketch, "E3938", {"start": v(218.1, 52.63) * mm, "end": v(217.86, 52.75) * mm});
            skLineSegment(sketch, "E3939", {"start": v(217.86, 52.75) * mm, "end": v(217.63, 52.86) * mm});
            skLineSegment(sketch, "E3940", {"start": v(217.63, 52.86) * mm, "end": v(217.39, 52.96) * mm});
            skLineSegment(sketch, "E3941", {"start": v(217.39, 52.96) * mm, "end": v(217.14, 53.05) * mm});
            skLineSegment(sketch, "E3942", {"start": v(217.14, 53.05) * mm, "end": v(216.64, 53.21) * mm});
            skLineSegment(sketch, "E3943", {"start": v(216.64, 53.21) * mm, "end": v(216.13, 53.36) * mm});
            skLineSegment(sketch, "E3944", {"start": v(216.13, 53.36) * mm, "end": v(215.63, 53.52) * mm});
            skLineSegment(sketch, "E3945", {"start": v(215.63, 53.52) * mm, "end": v(215.13, 53.68) * mm});
            skLineSegment(sketch, "E3946", {"start": v(215.13, 53.68) * mm, "end": v(214.88, 53.78) * mm});
            skLineSegment(sketch, "E3947", {"start": v(214.88, 53.78) * mm, "end": v(214.65, 53.88) * mm});
            skLineSegment(sketch, "E3948", {"start": v(214.65, 53.88) * mm, "end": v(214.41, 54) * mm});
            skLineSegment(sketch, "E3949", {"start": v(214.41, 54) * mm, "end": v(214.18, 54.13) * mm});
            skArc(sketch, "E3950", {"start": v(214.18, 54.13) * mm, "mid": v(212.83, 54.59) * mm, "end": v(211.4, 54.44) * mm});
            skArc(sketch, "E3951", {"start": v(211.4, 54.44) * mm, "mid": v(210.57, 54.54) * mm, "end": v(210.12, 55.25) * mm});
            skArc(sketch, "E3952", {"start": v(210.12, 55.25) * mm, "mid": v(209.34, 57.72) * mm, "end": v(207.76, 59.78) * mm});
            skArc(sketch, "E3953", {"start": v(207.76, 59.78) * mm, "mid": v(206.87, 60.84) * mm, "end": v(206.3, 62.1) * mm});
            skArc(sketch, "E3954", {"start": v(206.3, 62.1) * mm, "mid": v(206.1, 63.17) * mm, "end": v(206.12, 64.26) * mm});
            skArc(sketch, "E3955", {"start": v(206.12, 64.26) * mm, "mid": v(206.32, 64.97) * mm, "end": v(206.73, 65.6) * mm});
            skArc(sketch, "E3956", {"start": v(206.73, 65.6) * mm, "mid": v(206.73, 65.77) * mm, "end": v(206.56, 65.8) * mm});
            skArc(sketch, "E3957", {"start": v(206.56, 65.8) * mm, "mid": v(206.44, 65.74) * mm, "end": v(206.3, 65.73) * mm});
            skArc(sketch, "E3958", {"start": v(206.3, 65.73) * mm, "mid": v(206.16, 65.84) * mm, "end": v(206.2, 66) * mm});
            skArc(sketch, "E3959", {"start": v(206.2, 66) * mm, "mid": v(206.56, 66.37) * mm, "end": v(206.91, 66.75) * mm});
            skArc(sketch, "E3960", {"start": v(206.91, 66.75) * mm, "mid": v(207, 66.95) * mm, "end": v(206.92, 67.15) * mm});
            skArc(sketch, "E3961", {"start": v(206.92, 67.15) * mm, "mid": v(206.73, 67.3) * mm, "end": v(206.52, 67.4) * mm});
            skArc(sketch, "E3962", {"start": v(206.52, 67.4) * mm, "mid": v(206.43, 67.5) * mm, "end": v(206.45, 67.63) * mm});
            skArc(sketch, "E3963", {"start": v(206.45, 67.63) * mm, "mid": v(206.72, 67.92) * mm, "end": v(207.06, 68.14) * mm});
            skArc(sketch, "E3964", {"start": v(207.06, 68.14) * mm, "mid": v(207.26, 68.35) * mm, "end": v(207.27, 68.64) * mm});
            skArc(sketch, "E3965", {"start": v(207.27, 68.64) * mm, "mid": v(206.81, 69.66) * mm, "end": v(206.2, 70.6) * mm});
            skArc(sketch, "E3966", {"start": v(206.2, 70.6) * mm, "mid": v(205.83, 71.23) * mm, "end": v(205.63, 71.93) * mm});
            skArc(sketch, "E3967", {"start": v(205.63, 71.93) * mm, "mid": v(205.72, 72.15) * mm, "end": v(205.96, 72.18) * mm});
            skArc(sketch, "E3968", {"start": v(205.96, 72.18) * mm, "mid": v(206.2, 72.02) * mm, "end": v(206.38, 71.8) * mm});
            skArc(sketch, "E3969", {"start": v(206.38, 71.8) * mm, "mid": v(207.2, 70.42) * mm, "end": v(207.95, 69) * mm});
            skArc(sketch, "E3970", {"start": v(207.95, 69) * mm, "mid": v(208.2, 68.8) * mm, "end": v(208.53, 68.86) * mm});
            skArc(sketch, "E3971", {"start": v(208.53, 68.86) * mm, "mid": v(208.83, 68.96) * mm, "end": v(209.13, 68.86) * mm});
            skArc(sketch, "E3972", {"start": v(209.13, 68.86) * mm, "mid": v(209.34, 68.84) * mm, "end": v(209.44, 69.02) * mm});
            skArc(sketch, "E3973", {"start": v(209.44, 69.02) * mm, "mid": v(209.45, 69.26) * mm, "end": v(209.48, 69.5) * mm});
            skArc(sketch, "E3974", {"start": v(209.48, 69.5) * mm, "mid": v(209.28, 69.44) * mm, "end": v(209.08, 69.51) * mm});
            skArc(sketch, "E3975", {"start": v(209.08, 69.51) * mm, "mid": v(208.53, 70.1) * mm, "end": v(208.22, 70.86) * mm});
            skArc(sketch, "E3976", {"start": v(208.22, 70.86) * mm, "mid": v(208.25, 71.23) * mm, "end": v(208.45, 71.53) * mm});
            skArc(sketch, "E3977", {"start": v(208.45, 71.53) * mm, "mid": v(208.52, 71.58) * mm, "end": v(208.59, 71.6) * mm});
            skLineSegment(sketch, "E3978", {"start": v(208.59, 71.6) * mm, "end": v(208.58, 71.6) * mm});
            skArc(sketch, "E3979", {"start": v(208.58, 71.6) * mm, "mid": v(208.3, 71.77) * mm, "end": v(208.24, 72.08) * mm});
            skArc(sketch, "E3980", {"start": v(208.24, 72.08) * mm, "mid": v(208.4, 72.32) * mm, "end": v(208.7, 72.33) * mm});
            skArc(sketch, "E3981", {"start": v(208.7, 72.33) * mm, "mid": v(208.9, 72.14) * mm, "end": v(208.94, 71.87) * mm});
            skArc(sketch, "E3982", {"start": v(208.94, 71.87) * mm, "mid": v(208.88, 71.73) * mm, "end": v(208.76, 71.63) * mm});
            skLineSegment(sketch, "E3983", {"start": v(208.76, 71.63) * mm, "end": v(208.76, 71.63) * mm});
            skArc(sketch, "E3984", {"start": v(208.76, 71.63) * mm, "mid": v(208.91, 71.6) * mm, "end": v(209.03, 71.5) * mm});
            skArc(sketch, "E3985", {"start": v(209.03, 71.5) * mm, "mid": v(209.47, 70.7) * mm, "end": v(209.64, 69.8) * mm});
            skArc(sketch, "E3986", {"start": v(209.64, 69.8) * mm, "mid": v(209.64, 69.76) * mm, "end": v(209.63, 69.72) * mm});
            skLineSegment(sketch, "E3987", {"start": v(209.63, 69.72) * mm, "end": v(209.64, 69.71) * mm});
            skArc(sketch, "E3988", {"start": v(209.64, 69.71) * mm, "mid": v(209.7, 69.66) * mm, "end": v(209.7, 69.58) * mm});
            skArc(sketch, "E3989", {"start": v(209.7, 69.58) * mm, "mid": v(209.68, 69.47) * mm, "end": v(209.7, 69.37) * mm});
            skArc(sketch, "E3990", {"start": v(209.7, 69.37) * mm, "mid": v(209.76, 69.31) * mm, "end": v(209.84, 69.33) * mm});
            skArc(sketch, "E3991", {"start": v(209.84, 69.33) * mm, "mid": v(209.96, 69.49) * mm, "end": v(210.03, 69.67) * mm});
            skArc(sketch, "E3992", {"start": v(210.03, 69.67) * mm, "mid": v(210.4, 70.45) * mm, "end": v(211.06, 71) * mm});
            skArc(sketch, "E3993", {"start": v(211.06, 71) * mm, "mid": v(211.24, 71.1) * mm, "end": v(211.4, 71.25) * mm});
            skArc(sketch, "E3994", {"start": v(211.4, 71.25) * mm, "mid": v(211.7, 71.33) * mm, "end": v(211.9, 71.08) * mm});
            skArc(sketch, "E3995", {"start": v(211.9, 71.08) * mm, "mid": v(211.98, 70.83) * mm, "end": v(212.17, 70.63) * mm});
            skArc(sketch, "E3996", {"start": v(212.17, 70.63) * mm, "mid": v(212.4, 70.65) * mm, "end": v(212.46, 70.86) * mm});
            skArc(sketch, "E3997", {"start": v(212.46, 70.86) * mm, "mid": v(212.17, 71.43) * mm, "end": v(211.75, 71.9) * mm});
            skArc(sketch, "E3998", {"start": v(211.75, 71.9) * mm, "mid": v(211.63, 72.16) * mm, "end": v(211.75, 72.4) * mm});
            skArc(sketch, "E3999", {"start": v(211.75, 72.4) * mm, "mid": v(212.07, 72.54) * mm, "end": v(212.4, 72.45) * mm});
            skArc(sketch, "E4000", {"start": v(212.4, 72.45) * mm, "mid": v(212.93, 72.52) * mm, "end": v(212.95, 73.05) * mm});
            skArc(sketch, "E4001", {"start": v(212.95, 73.05) * mm, "mid": v(212.93, 73.17) * mm, "end": v(213.03, 73.24) * mm});
            skArc(sketch, "E4002", {"start": v(213.03, 73.24) * mm, "mid": v(213.13, 73.28) * mm, "end": v(213.21, 73.36) * mm});
            skArc(sketch, "E4003", {"start": v(213.21, 73.36) * mm, "mid": v(213.27, 73.49) * mm, "end": v(213.29, 73.63) * mm});
            skArc(sketch, "E4004", {"start": v(213.29, 73.63) * mm, "mid": v(213.3, 73.67) * mm, "end": v(213.34, 73.68) * mm});
            skArc(sketch, "E4005", {"start": v(213.34, 73.68) * mm, "mid": v(213.47, 73.66) * mm, "end": v(213.6, 73.61) * mm});
            skArc(sketch, "E4006", {"start": v(213.6, 73.61) * mm, "mid": v(213.87, 73.63) * mm, "end": v(213.96, 73.9) * mm});
            skArc(sketch, "E4007", {"start": v(213.96, 73.9) * mm, "mid": v(213.93, 74.3) * mm, "end": v(214.03, 74.71) * mm});
            skArc(sketch, "E4008", {"start": v(214.03, 74.71) * mm, "mid": v(214.23, 74.82) * mm, "end": v(214.38, 74.64) * mm});
            skArc(sketch, "E4009", {"start": v(214.38, 74.64) * mm, "mid": v(214.4, 74.04) * mm, "end": v(214.46, 73.43) * mm});
            skArc(sketch, "E4010", {"start": v(214.46, 73.43) * mm, "mid": v(214.64, 73.28) * mm, "end": v(214.8, 73.45) * mm});
            skArc(sketch, "E4011", {"start": v(214.8, 73.45) * mm, "mid": v(214.9, 73.62) * mm, "end": v(215.1, 73.62) * mm});
            skArc(sketch, "E4012", {"start": v(215.1, 73.62) * mm, "mid": v(215.3, 73.6) * mm, "end": v(215.46, 73.73) * mm});
            skArc(sketch, "E4013", {"start": v(215.46, 73.73) * mm, "mid": v(215.6, 73.86) * mm, "end": v(215.79, 73.9) * mm});
            skArc(sketch, "E4014", {"start": v(215.79, 73.9) * mm, "mid": v(215.87, 73.85) * mm, "end": v(215.83, 73.75) * mm});
            skArc(sketch, "E4015", {"start": v(215.83, 73.75) * mm, "mid": v(215.68, 73.4) * mm, "end": v(215.95, 73.12) * mm});
            skArc(sketch, "E4016", {"start": v(215.95, 73.12) * mm, "mid": v(216.28, 73.19) * mm, "end": v(216.42, 73.5) * mm});
            skArc(sketch, "E4017", {"start": v(216.42, 73.5) * mm, "mid": v(216.4, 73.83) * mm, "end": v(216.38, 74.16) * mm});
            skArc(sketch, "E4018", {"start": v(216.38, 74.16) * mm, "mid": v(216.41, 75.12) * mm, "end": v(216.66, 76.04) * mm});
            skArc(sketch, "E4019", {"start": v(233.21, 69.86) * mm, "mid": v(233.45, 69.67) * mm, "end": v(233.32, 69.4) * mm});
            skArc(sketch, "E4020", {"start": v(233.32, 69.4) * mm, "mid": v(232.5, 69.1) * mm, "end": v(231.64, 69) * mm});
            skArc(sketch, "E4021", {"start": v(231.64, 69) * mm, "mid": v(231.41, 69.2) * mm, "end": v(231.53, 69.46) * mm});
            skArc(sketch, "E4022", {"start": v(231.53, 69.46) * mm, "mid": v(232.35, 69.77) * mm, "end": v(233.21, 69.86) * mm});
            skArc(sketch, "E4023", {"start": v(228.65, 61.36) * mm, "mid": v(229.05, 61.51) * mm, "end": v(229.47, 61.44) * mm});
            skArc(sketch, "E4024", {"start": v(229.47, 61.44) * mm, "mid": v(229.64, 61.22) * mm, "end": v(229.56, 60.95) * mm});
            skArc(sketch, "E4025", {"start": v(229.56, 60.95) * mm, "mid": v(229.15, 60.75) * mm, "end": v(228.7, 60.8) * mm});
            skArc(sketch, "E4026", {"start": v(228.7, 60.8) * mm, "mid": v(228.51, 61.07) * mm, "end": v(228.65, 61.36) * mm});
            skArc(sketch, "E4027", {"start": v(224.3, 55.29) * mm, "mid": v(224.38, 55.34) * mm, "end": v(224.47, 55.34) * mm});
            skArc(sketch, "E4028", {"start": v(224.47, 55.34) * mm, "mid": v(224.62, 55.26) * mm, "end": v(224.75, 55.13) * mm});
            skArc(sketch, "E4029", {"start": v(224.75, 55.13) * mm, "mid": v(224.74, 54.85) * mm, "end": v(224.48, 54.77) * mm});
            skArc(sketch, "E4030", {"start": v(224.48, 54.77) * mm, "mid": v(224.27, 54.99) * mm, "end": v(224.3, 55.29) * mm});
            skArc(sketch, "E4031", {"start": v(225.87, 55.14) * mm, "mid": v(225.96, 55.17) * mm, "end": v(226.05, 55.17) * mm});
            skArc(sketch, "E4032", {"start": v(226.05, 55.17) * mm, "mid": v(226.13, 55.14) * mm, "end": v(226.2, 55.09) * mm});
            skArc(sketch, "E4033", {"start": v(226.2, 55.09) * mm, "mid": v(226.26, 54.73) * mm, "end": v(225.94, 54.56) * mm});
            skArc(sketch, "E4034", {"start": v(225.94, 54.56) * mm, "mid": v(225.69, 54.83) * mm, "end": v(225.87, 55.14) * mm});
            skArc(sketch, "E4035", {"start": v(194.46, 80.25) * mm, "mid": v(194.06, 81.38) * mm, "end": v(195.16, 81.84) * mm});
            skArc(sketch, "E4036", {"start": v(195.16, 81.84) * mm, "mid": v(195.67, 80.73) * mm, "end": v(194.56, 80.21) * mm});
            skArc(sketch, "E4037", {"start": v(194.56, 80.21) * mm, "mid": v(194.54, 80.22) * mm, "end": v(194.51, 80.23) * mm});
            skArc(sketch, "E4038", {"start": v(194.51, 80.23) * mm, "mid": v(194.49, 80.24) * mm, "end": v(194.46, 80.25) * mm});
            skArc(sketch, "E4039", {"start": v(191.06, 75.64) * mm, "mid": v(191.79, 76.36) * mm, "end": v(192.56, 75.69) * mm});
            skArc(sketch, "E4040", {"start": v(192.56, 75.69) * mm, "mid": v(192.02, 74.86) * mm, "end": v(191.1, 75.24) * mm});
            skArc(sketch, "E4041", {"start": v(191.1, 75.24) * mm, "mid": v(191.08, 75.3) * mm, "end": v(191.06, 75.35) * mm});
            skArc(sketch, "E4042", {"start": v(191.06, 75.35) * mm, "mid": v(191.05, 75.5) * mm, "end": v(191.06, 75.64) * mm});
            skArc(sketch, "E4043", {"start": v(197.13, 74.58) * mm, "mid": v(198.04, 75.9) * mm, "end": v(199.6, 75.6) * mm});
            skArc(sketch, "E4044", {"start": v(199.6, 75.6) * mm, "mid": v(200.38, 74.6) * mm, "end": v(200.85, 73.43) * mm});
            skArc(sketch, "E4045", {"start": v(200.85, 73.43) * mm, "mid": v(200.6, 73.01) * mm, "end": v(200.17, 73.26) * mm});
            skArc(sketch, "E4046", {"start": v(200.17, 73.26) * mm, "mid": v(199.91, 73.52) * mm, "end": v(199.55, 73.45) * mm});
            skArc(sketch, "E4047", {"start": v(199.55, 73.45) * mm, "mid": v(197.97, 73.22) * mm, "end": v(197.13, 74.58) * mm});
            skArc(sketch, "E4048", {"start": v(191.57, 73.38) * mm, "mid": v(192.56, 73.93) * mm, "end": v(193.33, 73.1) * mm});
            skArc(sketch, "E4049", {"start": v(193.33, 73.1) * mm, "mid": v(192.63, 72.17) * mm, "end": v(191.62, 72.73) * mm});
            skArc(sketch, "E4050", {"start": v(191.62, 72.73) * mm, "mid": v(191.56, 72.92) * mm, "end": v(191.53, 73.13) * mm});
            skArc(sketch, "E4051", {"start": v(191.53, 73.13) * mm, "mid": v(191.54, 73.25) * mm, "end": v(191.57, 73.38) * mm});
            skArc(sketch, "E4052", {"start": v(195, 78.7) * mm, "mid": v(195.16, 78.7) * mm, "end": v(195.27, 78.58) * mm});
            skArc(sketch, "E4053", {"start": v(195.27, 78.58) * mm, "mid": v(195.4, 78.05) * mm, "end": v(195.29, 77.51) * mm});
            skArc(sketch, "E4054", {"start": v(195.29, 77.51) * mm, "mid": v(194.64, 75.47) * mm, "end": v(194.45, 73.33) * mm});
            skArc(sketch, "E4055", {"start": v(194.45, 73.33) * mm, "mid": v(194.51, 72.87) * mm, "end": v(194.67, 72.42) * mm});
            skArc(sketch, "E4056", {"start": v(194.67, 72.42) * mm, "mid": v(194.61, 72.1) * mm, "end": v(194.28, 72.06) * mm});
            skArc(sketch, "E4057", {"start": v(194.28, 72.06) * mm, "mid": v(193.86, 72) * mm, "end": v(193.8, 71.59) * mm});
            skArc(sketch, "E4058", {"start": v(193.8, 71.59) * mm, "mid": v(194.19, 71.33) * mm, "end": v(194.63, 71.46) * mm});
            skArc(sketch, "E4059", {"start": v(194.63, 71.46) * mm, "mid": v(195.18, 71.66) * mm, "end": v(195.7, 71.43) * mm});
            skArc(sketch, "E4060", {"start": v(195.7, 71.43) * mm, "mid": v(195.83, 71.36) * mm, "end": v(195.97, 71.36) * mm});
            skArc(sketch, "E4061", {"start": v(195.97, 71.36) * mm, "mid": v(196.74, 71.18) * mm, "end": v(196.95, 70.43) * mm});
            skArc(sketch, "E4062", {"start": v(196.95, 70.43) * mm, "mid": v(196.97, 70.25) * mm, "end": v(197.1, 70.11) * mm});
            skArc(sketch, "E4063", {"start": v(197.1, 70.11) * mm, "mid": v(197.85, 69.7) * mm, "end": v(198.6, 69.25) * mm});
            skArc(sketch, "E4064", {"start": v(198.6, 69.25) * mm, "mid": v(198.82, 69.2) * mm, "end": v(199.04, 69.28) * mm});
            skArc(sketch, "E4065", {"start": v(199.04, 69.28) * mm, "mid": v(200.16, 70.35) * mm, "end": v(201.15, 71.55) * mm});
            skArc(sketch, "E4066", {"start": v(201.15, 71.55) * mm, "mid": v(201.69, 71.7) * mm, "end": v(201.98, 71.23) * mm});
            skArc(sketch, "E4067", {"start": v(201.98, 71.23) * mm, "mid": v(201.28, 69.84) * mm, "end": v(199.85, 69.24) * mm});
            skArc(sketch, "E4068", {"start": v(199.85, 69.24) * mm, "mid": v(199.09, 68.84) * mm, "end": v(198.9, 68) * mm});
            skArc(sketch, "E4069", {"start": v(198.9, 68) * mm, "mid": v(199.49, 66.93) * mm, "end": v(200.53, 66.31) * mm});
            skArc(sketch, "E4070", {"start": v(200.53, 66.31) * mm, "mid": v(200.77, 66.04) * mm, "end": v(200.63, 65.71) * mm});
            skArc(sketch, "E4071", {"start": v(200.63, 65.71) * mm, "mid": v(200.51, 65.15) * mm, "end": v(201.08, 65.03) * mm});
            skArc(sketch, "E4072", {"start": v(201.08, 65.03) * mm, "mid": v(202.27, 65.66) * mm, "end": v(203.56, 66.06) * mm});
            skArc(sketch, "E4073", {"start": v(203.56, 66.06) * mm, "mid": v(204.25, 65.88) * mm, "end": v(204.5, 65.21) * mm});
            skArc(sketch, "E4074", {"start": v(204.5, 65.21) * mm, "mid": v(204.12, 64.61) * mm, "end": v(203.4, 64.57) * mm});
            skArc(sketch, "E4075", {"start": v(203.4, 64.57) * mm, "mid": v(202.15, 64.82) * mm, "end": v(200.91, 64.5) * mm});
            skArc(sketch, "E4076", {"start": v(200.91, 64.5) * mm, "mid": v(200.8, 64.42) * mm, "end": v(200.74, 64.3) * mm});
            skArc(sketch, "E4077", {"start": v(200.74, 64.3) * mm, "mid": v(200.58, 63.83) * mm, "end": v(200.46, 63.33) * mm});
            skArc(sketch, "E4078", {"start": v(200.46, 63.33) * mm, "mid": v(200.45, 62.5) * mm, "end": v(200.72, 61.7) * mm});
            skArc(sketch, "E4079", {"start": v(200.72, 61.7) * mm, "mid": v(200.8, 61.24) * mm, "end": v(200.6, 60.81) * mm});
            skArc(sketch, "E4080", {"start": v(200.6, 60.81) * mm, "mid": v(200.44, 60.18) * mm, "end": v(200.9, 59.73) * mm});
            skArc(sketch, "E4081", {"start": v(200.9, 59.73) * mm, "mid": v(201.4, 59.66) * mm, "end": v(201.88, 59.67) * mm});
            skArc(sketch, "E4082", {"start": v(201.88, 59.67) * mm, "mid": v(204.29, 59.6) * mm, "end": v(206.57, 58.85) * mm});
            skArc(sketch, "E4083", {"start": v(206.57, 58.85) * mm, "mid": v(206.98, 58.07) * mm, "end": v(206.36, 57.44) * mm});
            skArc(sketch, "E4084", {"start": v(206.36, 57.44) * mm, "mid": v(205.05, 57.65) * mm, "end": v(204.13, 58.61) * mm});
            skArc(sketch, "E4085", {"start": v(204.13, 58.61) * mm, "mid": v(203.4, 59.03) * mm, "end": v(202.75, 58.48) * mm});
            skArc(sketch, "E4086", {"start": v(202.75, 58.48) * mm, "mid": v(202.66, 58.33) * mm, "end": v(202.5, 58.27) * mm});
            skArc(sketch, "E4087", {"start": v(202.5, 58.27) * mm, "mid": v(202.32, 58.3) * mm, "end": v(202.16, 58.36) * mm});
            skArc(sketch, "E4088", {"start": v(202.16, 58.36) * mm, "mid": v(201.4, 58.38) * mm, "end": v(200.97, 57.74) * mm});
            skArc(sketch, "E4089", {"start": v(200.97, 57.74) * mm, "mid": v(200.03, 55.2) * mm, "end": v(197.87, 53.54) * mm});
            skArc(sketch, "E4090", {"start": v(197.87, 53.54) * mm, "mid": v(197.56, 53.5) * mm, "end": v(197.27, 53.62) * mm});
            skArc(sketch, "E4091", {"start": v(197.27, 53.62) * mm, "mid": v(196.73, 54.01) * mm, "end": v(196.2, 54.42) * mm});
            skArc(sketch, "E4092", {"start": v(196.2, 54.42) * mm, "mid": v(195.77, 54.52) * mm, "end": v(195.43, 54.23) * mm});
            skArc(sketch, "E4093", {"start": v(195.43, 54.23) * mm, "mid": v(195.35, 53.59) * mm, "end": v(195.6, 52.99) * mm});
            skArc(sketch, "E4094", {"start": v(195.6, 52.99) * mm, "mid": v(195.7, 52.57) * mm, "end": v(195.43, 52.24) * mm});
            skArc(sketch, "E4095", {"start": v(195.43, 52.24) * mm, "mid": v(195, 52.24) * mm, "end": v(194.74, 52.57) * mm});
            skArc(sketch, "E4096", {"start": v(194.74, 52.57) * mm, "mid": v(194.18, 53.3) * mm, "end": v(193.26, 53.4) * mm});
            skArc(sketch, "E4097", {"start": v(193.26, 53.4) * mm, "mid": v(190.67, 53.14) * mm, "end": v(188.18, 53.92) * mm});
            skArc(sketch, "E4098", {"start": v(188.18, 53.92) * mm, "mid": v(187.46, 53.97) * mm, "end": v(186.97, 53.45) * mm});
            skArc(sketch, "E4099", {"start": v(186.97, 53.45) * mm, "mid": v(186.8, 52.67) * mm, "end": v(186.85, 51.87) * mm});
            skArc(sketch, "E4100", {"start": v(186.85, 51.87) * mm, "mid": v(186.96, 51.7) * mm, "end": v(187.16, 51.65) * mm});
            skArc(sketch, "E4101", {"start": v(187.16, 51.65) * mm, "mid": v(187.39, 51.53) * mm, "end": v(187.35, 51.28) * mm});
            skArc(sketch, "E4102", {"start": v(187.35, 51.28) * mm, "mid": v(187.07, 51.15) * mm, "end": v(186.76, 51.24) * mm});
            skArc(sketch, "E4103", {"start": v(186.76, 51.24) * mm, "mid": v(186.33, 51.3) * mm, "end": v(186.03, 50.98) * mm});
            skArc(sketch, "E4104", {"start": v(186.03, 50.98) * mm, "mid": v(185.95, 50.56) * mm, "end": v(185.87, 50.15) * mm});
            skArc(sketch, "E4105", {"start": v(185.87, 50.15) * mm, "mid": v(185.48, 49.66) * mm, "end": v(184.86, 49.73) * mm});
            skArc(sketch, "E4106", {"start": v(184.86, 49.73) * mm, "mid": v(184.6, 50.3) * mm, "end": v(184.92, 50.82) * mm});
            skArc(sketch, "E4107", {"start": v(184.92, 50.82) * mm, "mid": v(185.03, 50.97) * mm, "end": v(185, 51.15) * mm});
            skArc(sketch, "E4108", {"start": v(185, 51.15) * mm, "mid": v(184.87, 51.21) * mm, "end": v(184.75, 51.1) * mm});
            skArc(sketch, "E4109", {"start": v(184.75, 51.1) * mm, "mid": v(184.73, 51.08) * mm, "end": v(184.7, 51.08) * mm});
            skArc(sketch, "E4110", {"start": v(184.7, 51.08) * mm, "mid": v(184.48, 51.4) * mm, "end": v(184.7, 51.73) * mm});
            skArc(sketch, "E4111", {"start": v(184.7, 51.73) * mm, "mid": v(185.73, 52.5) * mm, "end": v(186.22, 53.68) * mm});
            skArc(sketch, "E4112", {"start": v(186.22, 53.68) * mm, "mid": v(186.19, 53.96) * mm, "end": v(186.02, 54.19) * mm});
            skArc(sketch, "E4113", {"start": v(186.02, 54.19) * mm, "mid": v(185.66, 54.45) * mm, "end": v(185.29, 54.68) * mm});
            skArc(sketch, "E4114", {"start": v(185.29, 54.68) * mm, "mid": v(183.78, 55.64) * mm, "end": v(182.43, 56.82) * mm});
            skArc(sketch, "E4115", {"start": v(182.43, 56.82) * mm, "mid": v(182.33, 57.02) * mm, "end": v(182.38, 57.24) * mm});
            skArc(sketch, "E4116", {"start": v(182.38, 57.24) * mm, "mid": v(182.35, 57.65) * mm, "end": v(181.94, 57.73) * mm});
            skArc(sketch, "E4117", {"start": v(181.94, 57.73) * mm, "mid": v(181.6, 57.68) * mm, "end": v(181.29, 57.82) * mm});
            skArc(sketch, "E4118", {"start": v(181.29, 57.82) * mm, "mid": v(180.85, 58.74) * mm, "end": v(181.2, 59.7) * mm});
            skArc(sketch, "E4119", {"start": v(181.2, 59.7) * mm, "mid": v(181.44, 60.77) * mm, "end": v(180.57, 61.45) * mm});
            skArc(sketch, "E4120", {"start": v(180.57, 61.45) * mm, "mid": v(179.87, 61.41) * mm, "end": v(179.21, 61.15) * mm});
            skArc(sketch, "E4121", {"start": v(179.21, 61.15) * mm, "mid": v(178.95, 60.84) * mm, "end": v(178.9, 60.44) * mm});
            skArc(sketch, "E4122", {"start": v(178.9, 60.44) * mm, "mid": v(178.63, 59.85) * mm, "end": v(178, 59.96) * mm});
            skArc(sketch, "E4123", {"start": v(178, 59.96) * mm, "mid": v(177.74, 60.66) * mm, "end": v(178.09, 61.33) * mm});
            skArc(sketch, "E4124", {"start": v(178.09, 61.33) * mm, "mid": v(178.97, 61.85) * mm, "end": v(179.97, 62.09) * mm});
            skArc(sketch, "E4125", {"start": v(179.97, 62.09) * mm, "mid": v(180.24, 62.38) * mm, "end": v(179.98, 62.68) * mm});
            skArc(sketch, "E4126", {"start": v(179.98, 62.68) * mm, "mid": v(179.4, 62.74) * mm, "end": v(178.83, 62.81) * mm});
            skArc(sketch, "E4127", {"start": v(178.83, 62.81) * mm, "mid": v(178.68, 62.8) * mm, "end": v(178.55, 62.74) * mm});
            skArc(sketch, "E4128", {"start": v(178.55, 62.74) * mm, "mid": v(178.51, 62.68) * mm, "end": v(178.54, 62.61) * mm});
            skArc(sketch, "E4129", {"start": v(178.54, 62.61) * mm, "mid": v(178.56, 62.53) * mm, "end": v(178.48, 62.5) * mm});
            skArc(sketch, "E4130", {"start": v(178.48, 62.5) * mm, "mid": v(178.3, 62.65) * mm, "end": v(178.27, 62.88) * mm});
            skArc(sketch, "E4131", {"start": v(178.27, 62.88) * mm, "mid": v(178.43, 63.06) * mm, "end": v(178.67, 63.07) * mm});
            skArc(sketch, "E4132", {"start": v(178.67, 63.07) * mm, "mid": v(179.74, 62.93) * mm, "end": v(180.76, 63.3) * mm});
            skArc(sketch, "E4133", {"start": v(180.76, 63.3) * mm, "mid": v(180.93, 63.6) * mm, "end": v(180.8, 63.92) * mm});
            skArc(sketch, "E4134", {"start": v(180.8, 63.92) * mm, "mid": v(180.46, 64) * mm, "end": v(180.2, 63.78) * mm});
            skArc(sketch, "E4135", {"start": v(180.2, 63.78) * mm, "mid": v(179.88, 63.51) * mm, "end": v(179.47, 63.6) * mm});
            skArc(sketch, "E4136", {"start": v(179.47, 63.6) * mm, "mid": v(179.12, 64.25) * mm, "end": v(179.36, 64.94) * mm});
            skArc(sketch, "E4137", {"start": v(179.36, 64.94) * mm, "mid": v(180.05, 65.23) * mm, "end": v(180.72, 64.92) * mm});
            skArc(sketch, "E4138", {"start": v(180.72, 64.92) * mm, "mid": v(181.06, 64.75) * mm, "end": v(181.42, 64.88) * mm});
            skArc(sketch, "E4139", {"start": v(181.42, 64.88) * mm, "mid": v(181.58, 65.23) * mm, "end": v(181.43, 65.58) * mm});
            skArc(sketch, "E4140", {"start": v(181.43, 65.58) * mm, "mid": v(180.3, 66.35) * mm, "end": v(178.96, 66.67) * mm});
            skArc(sketch, "E4141", {"start": v(178.96, 66.67) * mm, "mid": v(177.62, 66.97) * mm, "end": v(176.46, 67.71) * mm});
            skArc(sketch, "E4142", {"start": v(176.46, 67.71) * mm, "mid": v(176.31, 68.18) * mm, "end": v(176.65, 68.55) * mm});
            skArc(sketch, "E4143", {"start": v(176.65, 68.55) * mm, "mid": v(177.35, 68.55) * mm, "end": v(177.94, 68.17) * mm});
            skArc(sketch, "E4144", {"start": v(177.94, 68.17) * mm, "mid": v(179.45, 66.9) * mm, "end": v(181.3, 66.23) * mm});
            skArc(sketch, "E4145", {"start": v(181.3, 66.23) * mm, "mid": v(181.73, 66.37) * mm, "end": v(181.82, 66.81) * mm});
            skArc(sketch, "E4146", {"start": v(181.82, 66.81) * mm, "mid": v(181.98, 68.53) * mm, "end": v(183.26, 69.7) * mm});
            skArc(sketch, "E4147", {"start": v(183.26, 69.7) * mm, "mid": v(183.6, 69.92) * mm, "end": v(183.83, 70.27) * mm});
            skArc(sketch, "E4148", {"start": v(183.83, 70.27) * mm, "mid": v(184.74, 71.43) * mm, "end": v(186.16, 71.84) * mm});
            skArc(sketch, "E4149", {"start": v(186.16, 71.84) * mm, "mid": v(187.6, 72.57) * mm, "end": v(187.73, 74.18) * mm});
            skArc(sketch, "E4150", {"start": v(187.73, 74.18) * mm, "mid": v(187.82, 74.7) * mm, "end": v(188.35, 74.8) * mm});
            skArc(sketch, "E4151", {"start": v(188.35, 74.8) * mm, "mid": v(188.96, 74.26) * mm, "end": v(189.2, 73.48) * mm});
            skArc(sketch, "E4152", {"start": v(189.2, 73.48) * mm, "mid": v(189.64, 72.62) * mm, "end": v(190.57, 72.4) * mm});
            skArc(sketch, "E4153", {"start": v(190.57, 72.4) * mm, "mid": v(191.45, 72.4) * mm, "end": v(192.28, 72.1) * mm});
            skArc(sketch, "E4154", {"start": v(192.28, 72.1) * mm, "mid": v(193.14, 72.14) * mm, "end": v(193.43, 72.95) * mm});
            skArc(sketch, "E4155", {"start": v(193.43, 72.95) * mm, "mid": v(193.34, 75.73) * mm, "end": v(194.44, 78.28) * mm});
            skArc(sketch, "E4156", {"start": v(194.44, 78.28) * mm, "mid": v(194.69, 78.53) * mm, "end": v(195, 78.7) * mm});
            skArc(sketch, "E4157", {"start": v(200.59, 69.07) * mm, "mid": v(201.15, 69.33) * mm, "end": v(201.68, 69.01) * mm});
            skArc(sketch, "E4158", {"start": v(201.68, 69.01) * mm, "mid": v(201.88, 68.17) * mm, "end": v(201.58, 67.36) * mm});
            skArc(sketch, "E4159", {"start": v(201.58, 67.36) * mm, "mid": v(201.01, 67.1) * mm, "end": v(200.48, 67.43) * mm});
            skArc(sketch, "E4160", {"start": v(200.48, 67.43) * mm, "mid": v(200.29, 68.27) * mm, "end": v(200.59, 69.07) * mm});
            skArc(sketch, "E4161", {"start": v(176.76, 63.3) * mm, "mid": v(176.68, 64.25) * mm, "end": v(177.62, 64.4) * mm});
            skArc(sketch, "E4162", {"start": v(177.62, 64.4) * mm, "mid": v(177.82, 63.46) * mm, "end": v(176.9, 63.2) * mm});
            skArc(sketch, "E4163", {"start": v(176.9, 63.2) * mm, "mid": v(176.87, 63.22) * mm, "end": v(176.84, 63.24) * mm});
            skArc(sketch, "E4164", {"start": v(176.84, 63.24) * mm, "mid": v(176.8, 63.27) * mm, "end": v(176.76, 63.3) * mm});
            skArc(sketch, "E4165", {"start": v(201.67, 61.25) * mm, "mid": v(202.31, 60.81) * mm, "end": v(202.14, 60.06) * mm});
            skArc(sketch, "E4166", {"start": v(202.14, 60.06) * mm, "mid": v(201.37, 59.94) * mm, "end": v(200.98, 60.6) * mm});
            skArc(sketch, "E4167", {"start": v(200.98, 60.6) * mm, "mid": v(201.04, 60.86) * mm, "end": v(201.2, 61.06) * mm});
            skArc(sketch, "E4168", {"start": v(201.2, 61.06) * mm, "mid": v(201.42, 61.2) * mm, "end": v(201.67, 61.25) * mm});
            skArc(sketch, "E4169", {"start": v(183, 55.92) * mm, "mid": v(183.21, 55.92) * mm, "end": v(183.33, 55.74) * mm});
            skArc(sketch, "E4170", {"start": v(183.33, 55.74) * mm, "mid": v(183.07, 54.6) * mm, "end": v(182.24, 53.77) * mm});
            skArc(sketch, "E4171", {"start": v(182.24, 53.77) * mm, "mid": v(181.45, 53.94) * mm, "end": v(181.49, 54.75) * mm});
            skArc(sketch, "E4172", {"start": v(181.49, 54.75) * mm, "mid": v(182.2, 55.4) * mm, "end": v(183, 55.92) * mm});
            skArc(sketch, "E4173", {"start": v(195.13, 50.74) * mm, "mid": v(195.84, 51.32) * mm, "end": v(196.51, 50.7) * mm});
            skArc(sketch, "E4174", {"start": v(196.51, 50.7) * mm, "mid": v(195.92, 49.94) * mm, "end": v(195.15, 50.5) * mm});
            skArc(sketch, "E4175", {"start": v(195.15, 50.5) * mm, "mid": v(195.14, 50.6) * mm, "end": v(195.13, 50.69) * mm});
            skArc(sketch, "E4176", {"start": v(195.13, 50.69) * mm, "mid": v(195.13, 50.71) * mm, "end": v(195.13, 50.74) * mm});
            skArc(sketch, "E4177", {"start": v(187.67, 50.63) * mm, "mid": v(188.5, 50.99) * mm, "end": v(189, 50.24) * mm});
            skArc(sketch, "E4178", {"start": v(189, 50.24) * mm, "mid": v(188.27, 49.64) * mm, "end": v(187.64, 50.34) * mm});
            skArc(sketch, "E4179", {"start": v(187.64, 50.34) * mm, "mid": v(187.65, 50.45) * mm, "end": v(187.66, 50.57) * mm});
            skArc(sketch, "E4180", {"start": v(187.66, 50.57) * mm, "mid": v(187.66, 50.6) * mm, "end": v(187.67, 50.63) * mm});
            skArc(sketch, "E4181", {"start": v(190.48, 49.7) * mm, "mid": v(190, 51.07) * mm, "end": v(191.32, 51.65) * mm});
            skArc(sketch, "E4182", {"start": v(191.32, 51.65) * mm, "mid": v(191.99, 50.36) * mm, "end": v(190.74, 49.62) * mm});
            skArc(sketch, "E4183", {"start": v(190.74, 49.62) * mm, "mid": v(190.67, 49.64) * mm, "end": v(190.6, 49.66) * mm});
            skArc(sketch, "E4184", {"start": v(190.6, 49.66) * mm, "mid": v(190.54, 49.68) * mm, "end": v(190.48, 49.7) * mm});
            skArc(sketch, "E4185", {"start": v(183.99, 49.64) * mm, "mid": v(184.28, 49.55) * mm, "end": v(184.47, 49.32) * mm});
            skArc(sketch, "E4186", {"start": v(184.47, 49.32) * mm, "mid": v(184.4, 48.65) * mm, "end": v(183.8, 48.34) * mm});
            skArc(sketch, "E4187", {"start": v(183.8, 48.34) * mm, "mid": v(183.26, 48.7) * mm, "end": v(183.34, 49.34) * mm});
            skArc(sketch, "E4188", {"start": v(183.34, 49.34) * mm, "mid": v(183.63, 49.57) * mm, "end": v(183.99, 49.64) * mm});
            skArc(sketch, "E4189", {"start": v(111.72, 78.38) * mm, "mid": v(112.16, 78.14) * mm, "end": v(112.17, 77.64) * mm});
            skArc(sketch, "E4190", {"start": v(112.17, 77.64) * mm, "mid": v(111.2, 75.78) * mm, "end": v(110.32, 73.88) * mm});
            skArc(sketch, "E4191", {"start": v(110.32, 73.88) * mm, "mid": v(109.87, 71.67) * mm, "end": v(110.37, 69.47) * mm});
            skArc(sketch, "E4192", {"start": v(110.37, 69.47) * mm, "mid": v(110.86, 69.22) * mm, "end": v(111.22, 69.65) * mm});
            skArc(sketch, "E4193", {"start": v(111.22, 69.65) * mm, "mid": v(111.32, 70.08) * mm, "end": v(111.56, 70.45) * mm});
            skArc(sketch, "E4194", {"start": v(111.56, 70.45) * mm, "mid": v(112.05, 70.55) * mm, "end": v(112.31, 70.13) * mm});
            skArc(sketch, "E4195", {"start": v(112.31, 70.13) * mm, "mid": v(112.07, 69.38) * mm, "end": v(111.49, 68.85) * mm});
            skArc(sketch, "E4196", {"start": v(111.49, 68.85) * mm, "mid": v(111.11, 68.33) * mm, "end": v(111.33, 67.72) * mm});
            skArc(sketch, "E4197", {"start": v(111.33, 67.72) * mm, "mid": v(111.97, 66.85) * mm, "end": v(112.21, 65.8) * mm});
            skArc(sketch, "E4198", {"start": v(112.21, 65.8) * mm, "mid": v(112.92, 65) * mm, "end": v(113.86, 65.52) * mm});
            skArc(sketch, "E4199", {"start": v(113.86, 65.52) * mm, "mid": v(114.76, 66.77) * mm, "end": v(116.13, 67.47) * mm});
            skArc(sketch, "E4200", {"start": v(116.13, 67.47) * mm, "mid": v(117.4, 67.6) * mm, "end": v(118.65, 67.37) * mm});
            skArc(sketch, "E4201", {"start": v(118.65, 67.37) * mm, "mid": v(118.92, 67.02) * mm, "end": v(118.67, 66.66) * mm});
            skArc(sketch, "E4202", {"start": v(118.67, 66.66) * mm, "mid": v(115.94, 65.35) * mm, "end": v(113.49, 63.58) * mm});
            skArc(sketch, "E4203", {"start": v(113.49, 63.58) * mm, "mid": v(113.26, 63.07) * mm, "end": v(113.5, 62.57) * mm});
            skArc(sketch, "E4204", {"start": v(113.5, 62.57) * mm, "mid": v(113.73, 61.89) * mm, "end": v(113.26, 61.34) * mm});
            skArc(sketch, "E4205", {"start": v(113.26, 61.34) * mm, "mid": v(113.13, 61.24) * mm, "end": v(113.09, 61.08) * mm});
            skArc(sketch, "E4206", {"start": v(113.09, 61.08) * mm, "mid": v(113.14, 60.27) * mm, "end": v(113.17, 59.47) * mm});
            skArc(sketch, "E4207", {"start": v(113.17, 59.47) * mm, "mid": v(113.24, 59.26) * mm, "end": v(113.42, 59.13) * mm});
            skArc(sketch, "E4208", {"start": v(113.42, 59.13) * mm, "mid": v(114.81, 58.8) * mm, "end": v(116.24, 58.64) * mm});
            skArc(sketch, "E4209", {"start": v(116.24, 58.64) * mm, "mid": v(116.63, 58.33) * mm, "end": v(116.47, 57.86) * mm});
            skArc(sketch, "E4210", {"start": v(116.47, 57.86) * mm, "mid": v(115.04, 57.58) * mm, "end": v(113.88, 58.45) * mm});
            skArc(sketch, "E4211", {"start": v(113.88, 58.45) * mm, "mid": v(113.28, 58.94) * mm, "end": v(112.5, 58.85) * mm});
            skArc(sketch, "E4212", {"start": v(112.5, 58.85) * mm, "mid": v(111.82, 57.94) * mm, "end": v(112.02, 56.82) * mm});
            skArc(sketch, "E4213", {"start": v(112.02, 56.82) * mm, "mid": v(112.1, 56.57) * mm, "end": v(112.05, 56.3) * mm});
            skArc(sketch, "E4214", {"start": v(112.05, 56.3) * mm, "mid": v(111.99, 56.07) * mm, "end": v(112.03, 55.83) * mm});
            skArc(sketch, "E4215", {"start": v(112.03, 55.83) * mm, "mid": v(112.12, 55.62) * mm, "end": v(112.22, 55.4) * mm});
            skArc(sketch, "E4216", {"start": v(112.22, 55.4) * mm, "mid": v(112.76, 54.3) * mm, "end": v(113.31, 53.18) * mm});
            skArc(sketch, "E4217", {"start": v(113.31, 53.18) * mm, "mid": v(113.3, 52.78) * mm, "end": v(112.94, 52.6) * mm});
            skArc(sketch, "E4218", {"start": v(112.94, 52.6) * mm, "mid": v(112.64, 52.7) * mm, "end": v(112.48, 52.98) * mm});
            skArc(sketch, "E4219", {"start": v(112.48, 52.98) * mm, "mid": v(112.04, 54.1) * mm, "end": v(111.26, 55.03) * mm});
            skArc(sketch, "E4220", {"start": v(111.26, 55.03) * mm, "mid": v(110.88, 55.24) * mm, "end": v(110.45, 55.29) * mm});
            skArc(sketch, "E4221", {"start": v(110.45, 55.29) * mm, "mid": v(109.97, 55.2) * mm, "end": v(109.51, 55.06) * mm});
            skArc(sketch, "E4222", {"start": v(109.51, 55.06) * mm, "mid": v(108.87, 54.65) * mm, "end": v(108.4, 54.06) * mm});
            skArc(sketch, "E4223", {"start": v(108.4, 54.06) * mm, "mid": v(108.1, 53.77) * mm, "end": v(107.7, 53.67) * mm});
            skArc(sketch, "E4224", {"start": v(107.7, 53.67) * mm, "mid": v(107.02, 53.27) * mm, "end": v(107.12, 52.5) * mm});
            skArc(sketch, "E4225", {"start": v(107.12, 52.5) * mm, "mid": v(108.38, 50.31) * mm, "end": v(108.76, 47.82) * mm});
            skArc(sketch, "E4226", {"start": v(108.76, 47.82) * mm, "mid": v(108.47, 47.3) * mm, "end": v(107.88, 47.18) * mm});
            skArc(sketch, "E4227", {"start": v(107.88, 47.18) * mm, "mid": v(107.43, 47.58) * mm, "end": v(107.45, 48.18) * mm});
            skArc(sketch, "E4228", {"start": v(107.45, 48.18) * mm, "mid": v(107.72, 49.35) * mm, "end": v(107.35, 50.48) * mm});
            skArc(sketch, "E4229", {"start": v(107.35, 50.48) * mm, "mid": v(107.1, 50.72) * mm, "end": v(106.76, 50.82) * mm});
            skArc(sketch, "E4230", {"start": v(106.76, 50.82) * mm, "mid": v(106.58, 50.89) * mm, "end": v(106.48, 51.05) * mm});
            skArc(sketch, "E4231", {"start": v(106.48, 51.05) * mm, "mid": v(105.27, 52.14) * mm, "end": v(103.79, 51.47) * mm});
            skArc(sketch, "E4232", {"start": v(103.79, 51.47) * mm, "mid": v(103.53, 51.2) * mm, "end": v(103.2, 51.07) * mm});
            skArc(sketch, "E4233", {"start": v(103.2, 51.07) * mm, "mid": v(101.65, 51.14) * mm, "end": v(100.28, 51.85) * mm});
            skArc(sketch, "E4234", {"start": v(100.28, 51.85) * mm, "mid": v(100.01, 52.27) * mm, "end": v(100.03, 52.76) * mm});
            skArc(sketch, "E4235", {"start": v(100.03, 52.76) * mm, "mid": v(99.8, 53.64) * mm, "end": v(98.9, 53.73) * mm});
            skArc(sketch, "E4236", {"start": v(98.9, 53.73) * mm, "mid": v(98.44, 53.75) * mm, "end": v(98.24, 54.16) * mm});
            skArc(sketch, "E4237", {"start": v(98.24, 54.16) * mm, "mid": v(98.05, 55.6) * mm, "end": v(97.26, 56.81) * mm});
            skArc(sketch, "E4238", {"start": v(97.26, 56.81) * mm, "mid": v(96.76, 57.39) * mm, "end": v(96.36, 58.04) * mm});
            skArc(sketch, "E4239", {"start": v(96.36, 58.04) * mm, "mid": v(95.73, 59.69) * mm, "end": v(95.45, 61.43) * mm});
            skArc(sketch, "E4240", {"start": v(95.45, 61.43) * mm, "mid": v(95.46, 65.39) * mm, "end": v(96.08, 69.3) * mm});
            skArc(sketch, "E4241", {"start": v(96.08, 69.3) * mm, "mid": v(96.47, 69.88) * mm, "end": v(96.92, 70.41) * mm});
            skArc(sketch, "E4242", {"start": v(96.92, 70.41) * mm, "mid": v(97.52, 71.02) * mm, "end": v(98.17, 71.57) * mm});
            skArc(sketch, "E4243", {"start": v(98.17, 71.57) * mm, "mid": v(98.2, 71.64) * mm, "end": v(98.18, 71.72) * mm});
            skArc(sketch, "E4244", {"start": v(98.18, 71.72) * mm, "mid": v(98.1, 71.75) * mm, "end": v(98.03, 71.72) * mm});
            skArc(sketch, "E4245", {"start": v(98.03, 71.72) * mm, "mid": v(97.94, 71.68) * mm, "end": v(97.84, 71.7) * mm});
            skArc(sketch, "E4246", {"start": v(97.84, 71.7) * mm, "mid": v(97.63, 72.06) * mm, "end": v(97.9, 72.4) * mm});
            skArc(sketch, "E4247", {"start": v(97.9, 72.4) * mm, "mid": v(98.3, 72.26) * mm, "end": v(98.33, 71.84) * mm});
            skArc(sketch, "E4248", {"start": v(98.33, 71.84) * mm, "mid": v(98.34, 71.75) * mm, "end": v(98.43, 71.74) * mm});
            skArc(sketch, "E4249", {"start": v(98.43, 71.74) * mm, "mid": v(99.22, 72.05) * mm, "end": v(100.06, 72.16) * mm});
            skArc(sketch, "E4250", {"start": v(100.06, 72.16) * mm, "mid": v(100.9, 72.38) * mm, "end": v(101.52, 73) * mm});
            skArc(sketch, "E4251", {"start": v(101.52, 73) * mm, "mid": v(101.58, 73.22) * mm, "end": v(101.5, 73.43) * mm});
            skArc(sketch, "E4252", {"start": v(101.5, 73.43) * mm, "mid": v(101.3, 73.78) * mm, "end": v(101.16, 74.16) * mm});
            skArc(sketch, "E4253", {"start": v(101.16, 74.16) * mm, "mid": v(101.01, 74.73) * mm, "end": v(100.9, 75.3) * mm});
            skArc(sketch, "E4254", {"start": v(100.9, 75.3) * mm, "mid": v(100.86, 75.53) * mm, "end": v(100.85, 75.77) * mm});
            skArc(sketch, "E4255", {"start": v(100.85, 75.77) * mm, "mid": v(101.33, 76.26) * mm, "end": v(101.83, 75.79) * mm});
            skArc(sketch, "E4256", {"start": v(101.83, 75.79) * mm, "mid": v(101.86, 74.72) * mm, "end": v(101.86, 73.66) * mm});
            skArc(sketch, "E4257", {"start": v(101.86, 73.66) * mm, "mid": v(102.32, 72.89) * mm, "end": v(103.22, 72.94) * mm});
            skArc(sketch, "E4258", {"start": v(103.22, 72.94) * mm, "mid": v(104.43, 73.6) * mm, "end": v(105.75, 74) * mm});
            skArc(sketch, "E4259", {"start": v(105.75, 74) * mm, "mid": v(105.99, 74) * mm, "end": v(106.21, 73.93) * mm});
            skArc(sketch, "E4260", {"start": v(106.21, 73.93) * mm, "mid": v(106.4, 73.77) * mm, "end": v(106.5, 73.56) * mm});
            skArc(sketch, "E4261", {"start": v(106.5, 73.56) * mm, "mid": v(107.47, 72.77) * mm, "end": v(108.57, 73.37) * mm});
            skArc(sketch, "E4262", {"start": v(108.57, 73.37) * mm, "mid": v(109.62, 75.47) * mm, "end": v(110.58, 77.61) * mm});
            skArc(sketch, "E4263", {"start": v(110.58, 77.61) * mm, "mid": v(111.04, 78.17) * mm, "end": v(111.72, 78.38) * mm});
            skArc(sketch, "E4264", {"start": v(97.7, 72.95) * mm, "mid": v(97.97, 74) * mm, "end": v(99.03, 73.76) * mm});
            skArc(sketch, "E4265", {"start": v(99.03, 73.76) * mm, "mid": v(99.04, 73.74) * mm, "end": v(99.05, 73.72) * mm});
            skArc(sketch, "E4266", {"start": v(99.05, 73.72) * mm, "mid": v(99.06, 73.7) * mm, "end": v(99.07, 73.68) * mm});
            skArc(sketch, "E4267", {"start": v(99.07, 73.68) * mm, "mid": v(98.74, 72.65) * mm, "end": v(97.7, 72.95) * mm});
            skArc(sketch, "E4268", {"start": v(113.31, 67.67) * mm, "mid": v(114.25, 67.16) * mm, "end": v(113.96, 66.14) * mm});
            skArc(sketch, "E4269", {"start": v(113.96, 66.14) * mm, "mid": v(112.88, 66.24) * mm, "end": v(112.82, 67.32) * mm});
            skArc(sketch, "E4270", {"start": v(112.82, 67.32) * mm, "mid": v(112.93, 67.45) * mm, "end": v(113.07, 67.56) * mm});
            skArc(sketch, "E4271", {"start": v(113.07, 67.56) * mm, "mid": v(113.19, 67.63) * mm, "end": v(113.31, 67.67) * mm});
            skArc(sketch, "E4272", {"start": v(112.88, 57.16) * mm, "mid": v(113.38, 57.6) * mm, "end": v(114.04, 57.7) * mm});
            skArc(sketch, "E4273", {"start": v(114.04, 57.7) * mm, "mid": v(114.38, 57.46) * mm, "end": v(114.35, 57.03) * mm});
            skArc(sketch, "E4274", {"start": v(114.35, 57.03) * mm, "mid": v(113.87, 56.6) * mm, "end": v(113.23, 56.47) * mm});
            skArc(sketch, "E4275", {"start": v(113.23, 56.47) * mm, "mid": v(112.85, 56.71) * mm, "end": v(112.88, 57.16) * mm});
            skArc(sketch, "E4276", {"start": v(107.56, 52.59) * mm, "mid": v(107.76, 53.3) * mm, "end": v(108.48, 53.15) * mm});
            skArc(sketch, "E4277", {"start": v(108.48, 53.15) * mm, "mid": v(108.5, 53.13) * mm, "end": v(108.51, 53.1) * mm});
            skArc(sketch, "E4278", {"start": v(108.51, 53.1) * mm, "mid": v(108.53, 53.06) * mm, "end": v(108.55, 53.02) * mm});
            skArc(sketch, "E4279", {"start": v(108.55, 53.02) * mm, "mid": v(108.26, 52.33) * mm, "end": v(107.56, 52.59) * mm});
            skArc(sketch, "E4280", {"start": v(96.85, 52.37) * mm, "mid": v(97.32, 52.86) * mm, "end": v(97.87, 52.46) * mm});
            skArc(sketch, "E4281", {"start": v(97.87, 52.46) * mm, "mid": v(97.87, 52.43) * mm, "end": v(97.87, 52.4) * mm});
            skArc(sketch, "E4282", {"start": v(97.87, 52.4) * mm, "mid": v(97.87, 52.33) * mm, "end": v(97.86, 52.27) * mm});
            skArc(sketch, "E4283", {"start": v(97.86, 52.27) * mm, "mid": v(97.3, 51.85) * mm, "end": v(96.85, 52.37) * mm});
            skLineSegment(sketch, "E4284", {"start": v(129.27, 74.97) * mm, "end": v(129.26, 74.99) * mm});
            skLineSegment(sketch, "E4285", {"start": v(129.26, 74.99) * mm, "end": v(129.25, 75) * mm});
            skLineSegment(sketch, "E4286", {"start": v(129.25, 75) * mm, "end": v(129.24, 75.03) * mm});
            skLineSegment(sketch, "E4287", {"start": v(129.24, 75.03) * mm, "end": v(129.23, 75.05) * mm});
            skLineSegment(sketch, "E4288", {"start": v(129.23, 75.05) * mm, "end": v(129.22, 75.07) * mm});
            skLineSegment(sketch, "E4289", {"start": v(129.22, 75.07) * mm, "end": v(129.2, 75.09) * mm});
            skLineSegment(sketch, "E4290", {"start": v(129.2, 75.09) * mm, "end": v(129.2, 75.1) * mm});
            skLineSegment(sketch, "E4291", {"start": v(129.2, 75.1) * mm, "end": v(129.2, 75.12) * mm});
            skLineSegment(sketch, "E4292", {"start": v(129.2, 75.12) * mm, "end": v(129.18, 75.14) * mm});
            skLineSegment(sketch, "E4293", {"start": v(129.18, 75.14) * mm, "end": v(129.17, 75.16) * mm});
            skLineSegment(sketch, "E4294", {"start": v(129.17, 75.16) * mm, "end": v(129.17, 75.18) * mm});
            skLineSegment(sketch, "E4295", {"start": v(129.17, 75.18) * mm, "end": v(129.16, 75.2) * mm});
            skLineSegment(sketch, "E4296", {"start": v(129.16, 75.2) * mm, "end": v(129.15, 75.22) * mm});
            skLineSegment(sketch, "E4297", {"start": v(129.15, 75.22) * mm, "end": v(129.14, 75.24) * mm});
            skLineSegment(sketch, "E4298", {"start": v(129.14, 75.24) * mm, "end": v(129.13, 75.26) * mm});
            skLineSegment(sketch, "E4299", {"start": v(129.13, 75.26) * mm, "end": v(129.13, 75.28) * mm});
            skLineSegment(sketch, "E4300", {"start": v(129.13, 75.28) * mm, "end": v(129.12, 75.3) * mm});
            skLineSegment(sketch, "E4301", {"start": v(129.12, 75.3) * mm, "end": v(129.11, 75.32) * mm});
            skLineSegment(sketch, "E4302", {"start": v(129.11, 75.32) * mm, "end": v(129.1, 75.34) * mm});
            skLineSegment(sketch, "E4303", {"start": v(129.1, 75.34) * mm, "end": v(129.1, 75.36) * mm});
            skLineSegment(sketch, "E4304", {"start": v(129.1, 75.36) * mm, "end": v(129.09, 75.38) * mm});
            skLineSegment(sketch, "E4305", {"start": v(129.09, 75.38) * mm, "end": v(129.08, 75.4) * mm});
            skLineSegment(sketch, "E4306", {"start": v(129.08, 75.4) * mm, "end": v(129.08, 75.42) * mm});
            skLineSegment(sketch, "E4307", {"start": v(129.08, 75.42) * mm, "end": v(129.07, 75.43) * mm});
            skLineSegment(sketch, "E4308", {"start": v(129.07, 75.43) * mm, "end": v(129.06, 75.45) * mm});
            skLineSegment(sketch, "E4309", {"start": v(129.06, 75.45) * mm, "end": v(129.06, 75.47) * mm});
            skLineSegment(sketch, "E4310", {"start": v(129.06, 75.47) * mm, "end": v(129.05, 75.5) * mm});
            skLineSegment(sketch, "E4311", {"start": v(129.05, 75.5) * mm, "end": v(129.04, 75.51) * mm});
            skLineSegment(sketch, "E4312", {"start": v(129.04, 75.51) * mm, "end": v(129.04, 75.53) * mm});
            skLineSegment(sketch, "E4313", {"start": v(129.04, 75.53) * mm, "end": v(129.03, 75.55) * mm});
            skLineSegment(sketch, "E4314", {"start": v(129.03, 75.55) * mm, "end": v(129.03, 75.57) * mm});
            skLineSegment(sketch, "E4315", {"start": v(129.03, 75.57) * mm, "end": v(129.02, 75.58) * mm});
            skLineSegment(sketch, "E4316", {"start": v(129.02, 75.58) * mm, "end": v(129.01, 75.6) * mm});
            skLineSegment(sketch, "E4317", {"start": v(129.01, 75.6) * mm, "end": v(129, 75.62) * mm});
            skLineSegment(sketch, "E4318", {"start": v(129, 75.62) * mm, "end": v(129, 75.64) * mm});
            skLineSegment(sketch, "E4319", {"start": v(129, 75.64) * mm, "end": v(129, 75.66) * mm});
            skLineSegment(sketch, "E4320", {"start": v(129, 75.66) * mm, "end": v(129, 75.68) * mm});
            skLineSegment(sketch, "E4321", {"start": v(129, 75.68) * mm, "end": v(128.99, 75.7) * mm});
            skLineSegment(sketch, "E4322", {"start": v(128.99, 75.7) * mm, "end": v(128.98, 75.71) * mm});
            skLineSegment(sketch, "E4323", {"start": v(128.98, 75.71) * mm, "end": v(128.98, 75.73) * mm});
            skLineSegment(sketch, "E4324", {"start": v(128.98, 75.73) * mm, "end": v(128.98, 75.75) * mm});
            skLineSegment(sketch, "E4325", {"start": v(128.98, 75.75) * mm, "end": v(128.97, 75.77) * mm});
            skLineSegment(sketch, "E4326", {"start": v(128.97, 75.77) * mm, "end": v(128.97, 75.78) * mm});
            skLineSegment(sketch, "E4327", {"start": v(128.97, 75.78) * mm, "end": v(128.96, 75.8) * mm});
            skLineSegment(sketch, "E4328", {"start": v(128.96, 75.8) * mm, "end": v(128.96, 75.82) * mm});
            skLineSegment(sketch, "E4329", {"start": v(128.96, 75.82) * mm, "end": v(128.95, 75.84) * mm});
            skLineSegment(sketch, "E4330", {"start": v(128.95, 75.84) * mm, "end": v(128.95, 75.85) * mm});
            skLineSegment(sketch, "E4331", {"start": v(128.95, 75.85) * mm, "end": v(128.95, 75.87) * mm});
            skLineSegment(sketch, "E4332", {"start": v(128.95, 75.87) * mm, "end": v(128.94, 75.89) * mm});
            skLineSegment(sketch, "E4333", {"start": v(128.94, 75.89) * mm, "end": v(128.94, 75.9) * mm});
            skLineSegment(sketch, "E4334", {"start": v(128.94, 75.9) * mm, "end": v(128.94, 75.92) * mm});
            skLineSegment(sketch, "E4335", {"start": v(128.94, 75.92) * mm, "end": v(128.93, 75.94) * mm});
            skLineSegment(sketch, "E4336", {"start": v(128.93, 75.94) * mm, "end": v(128.93, 75.96) * mm});
            skLineSegment(sketch, "E4337", {"start": v(128.93, 75.96) * mm, "end": v(128.93, 75.97) * mm});
            skLineSegment(sketch, "E4338", {"start": v(128.93, 75.97) * mm, "end": v(128.93, 76) * mm});
            skLineSegment(sketch, "E4339", {"start": v(128.93, 76) * mm, "end": v(128.92, 76) * mm});
            skLineSegment(sketch, "E4340", {"start": v(128.92, 76) * mm, "end": v(128.92, 76.03) * mm});
            skLineSegment(sketch, "E4341", {"start": v(128.92, 76.03) * mm, "end": v(128.92, 76.04) * mm});
            skLineSegment(sketch, "E4342", {"start": v(128.92, 76.04) * mm, "end": v(128.92, 76.06) * mm});
            skLineSegment(sketch, "E4343", {"start": v(128.92, 76.06) * mm, "end": v(128.91, 76.07) * mm});
            skLineSegment(sketch, "E4344", {"start": v(128.91, 76.07) * mm, "end": v(128.91, 76.1) * mm});
            skLineSegment(sketch, "E4345", {"start": v(128.91, 76.1) * mm, "end": v(128.9, 76.1) * mm});
            skLineSegment(sketch, "E4346", {"start": v(128.9, 76.1) * mm, "end": v(128.9, 76.12) * mm});
            skLineSegment(sketch, "E4347", {"start": v(128.9, 76.12) * mm, "end": v(128.9, 76.14) * mm});
            skLineSegment(sketch, "E4348", {"start": v(128.9, 76.14) * mm, "end": v(128.9, 76.16) * mm});
            skLineSegment(sketch, "E4349", {"start": v(128.9, 76.16) * mm, "end": v(128.9, 76.17) * mm});
            skLineSegment(sketch, "E4350", {"start": v(128.9, 76.17) * mm, "end": v(128.9, 76.19) * mm});
            skLineSegment(sketch, "E4351", {"start": v(128.9, 76.19) * mm, "end": v(128.9, 76.2) * mm});
            skLineSegment(sketch, "E4352", {"start": v(128.9, 76.2) * mm, "end": v(128.9, 76.22) * mm});
            skLineSegment(sketch, "E4353", {"start": v(128.9, 76.22) * mm, "end": v(128.9, 76.23) * mm});
            skLineSegment(sketch, "E4354", {"start": v(128.9, 76.23) * mm, "end": v(128.9, 76.25) * mm});
            skLineSegment(sketch, "E4355", {"start": v(128.9, 76.25) * mm, "end": v(128.9, 76.26) * mm});
            skLineSegment(sketch, "E4356", {"start": v(128.9, 76.26) * mm, "end": v(128.9, 76.28) * mm});
            skLineSegment(sketch, "E4357", {"start": v(128.9, 76.28) * mm, "end": v(128.9, 76.3) * mm});
            skLineSegment(sketch, "E4358", {"start": v(128.9, 76.3) * mm, "end": v(128.9, 76.3) * mm});
            skLineSegment(sketch, "E4359", {"start": v(128.9, 76.3) * mm, "end": v(128.9, 76.32) * mm});
            skLineSegment(sketch, "E4360", {"start": v(128.9, 76.32) * mm, "end": v(128.9, 76.34) * mm});
            skLineSegment(sketch, "E4361", {"start": v(128.9, 76.34) * mm, "end": v(128.9, 76.35) * mm});
            skLineSegment(sketch, "E4362", {"start": v(128.9, 76.35) * mm, "end": v(128.9, 76.37) * mm});
            skLineSegment(sketch, "E4363", {"start": v(128.9, 76.37) * mm, "end": v(128.9, 76.38) * mm});
            skLineSegment(sketch, "E4364", {"start": v(128.9, 76.38) * mm, "end": v(128.9, 76.4) * mm});
            skLineSegment(sketch, "E4365", {"start": v(128.9, 76.4) * mm, "end": v(128.9, 76.41) * mm});
            skLineSegment(sketch, "E4366", {"start": v(128.9, 76.41) * mm, "end": v(128.9, 76.43) * mm});
            skLineSegment(sketch, "E4367", {"start": v(128.9, 76.43) * mm, "end": v(128.9, 76.44) * mm});
            skLineSegment(sketch, "E4368", {"start": v(128.9, 76.44) * mm, "end": v(128.9, 76.45) * mm});
            skLineSegment(sketch, "E4369", {"start": v(128.9, 76.45) * mm, "end": v(128.9, 76.47) * mm});
            skLineSegment(sketch, "E4370", {"start": v(128.9, 76.47) * mm, "end": v(128.9, 76.48) * mm});
            skLineSegment(sketch, "E4371", {"start": v(128.9, 76.48) * mm, "end": v(128.9, 76.5) * mm});
            skLineSegment(sketch, "E4372", {"start": v(128.9, 76.5) * mm, "end": v(128.9, 76.5) * mm});
            skLineSegment(sketch, "E4373", {"start": v(128.9, 76.5) * mm, "end": v(128.9, 76.52) * mm});
            skLineSegment(sketch, "E4374", {"start": v(128.9, 76.52) * mm, "end": v(128.9, 76.54) * mm});
            skLineSegment(sketch, "E4375", {"start": v(128.9, 76.54) * mm, "end": v(128.9, 76.55) * mm});
            skLineSegment(sketch, "E4376", {"start": v(128.9, 76.55) * mm, "end": v(128.9, 76.56) * mm});
            skLineSegment(sketch, "E4377", {"start": v(128.9, 76.56) * mm, "end": v(128.9, 76.57) * mm});
            skLineSegment(sketch, "E4378", {"start": v(128.9, 76.57) * mm, "end": v(128.9, 76.59) * mm});
            skLineSegment(sketch, "E4379", {"start": v(128.9, 76.59) * mm, "end": v(128.9, 76.6) * mm});
            skLineSegment(sketch, "E4380", {"start": v(128.9, 76.6) * mm, "end": v(128.91, 76.61) * mm});
            skLineSegment(sketch, "E4381", {"start": v(128.91, 76.61) * mm, "end": v(128.91, 76.62) * mm});
            skLineSegment(sketch, "E4382", {"start": v(128.91, 76.62) * mm, "end": v(128.91, 76.64) * mm});
            skLineSegment(sketch, "E4383", {"start": v(128.91, 76.64) * mm, "end": v(128.92, 76.65) * mm});
            skLineSegment(sketch, "E4384", {"start": v(128.92, 76.65) * mm, "end": v(128.92, 76.66) * mm});
            skLineSegment(sketch, "E4385", {"start": v(128.92, 76.66) * mm, "end": v(128.92, 76.67) * mm});
            skLineSegment(sketch, "E4386", {"start": v(128.92, 76.67) * mm, "end": v(128.92, 76.68) * mm});
            skLineSegment(sketch, "E4387", {"start": v(128.92, 76.68) * mm, "end": v(128.93, 76.7) * mm});
            skLineSegment(sketch, "E4388", {"start": v(128.93, 76.7) * mm, "end": v(128.93, 76.7) * mm});
            skLineSegment(sketch, "E4389", {"start": v(128.93, 76.7) * mm, "end": v(128.93, 76.72) * mm});
            skLineSegment(sketch, "E4390", {"start": v(128.93, 76.72) * mm, "end": v(128.93, 76.73) * mm});
            skLineSegment(sketch, "E4391", {"start": v(128.93, 76.73) * mm, "end": v(128.94, 76.74) * mm});
            skLineSegment(sketch, "E4392", {"start": v(128.94, 76.74) * mm, "end": v(128.94, 76.75) * mm});
            skLineSegment(sketch, "E4393", {"start": v(128.94, 76.75) * mm, "end": v(128.94, 76.76) * mm});
            skLineSegment(sketch, "E4394", {"start": v(128.94, 76.76) * mm, "end": v(128.95, 76.77) * mm});
            skLineSegment(sketch, "E4395", {"start": v(128.95, 76.77) * mm, "end": v(128.95, 76.78) * mm});
            skLineSegment(sketch, "E4396", {"start": v(128.95, 76.78) * mm, "end": v(128.95, 76.8) * mm});
            skLineSegment(sketch, "E4397", {"start": v(128.95, 76.8) * mm, "end": v(128.96, 76.8) * mm});
            skLineSegment(sketch, "E4398", {"start": v(128.96, 76.8) * mm, "end": v(128.96, 76.82) * mm});
            skLineSegment(sketch, "E4399", {"start": v(128.96, 76.82) * mm, "end": v(128.96, 76.83) * mm});
            skLineSegment(sketch, "E4400", {"start": v(128.96, 76.83) * mm, "end": v(128.97, 76.84) * mm});
            skLineSegment(sketch, "E4401", {"start": v(128.97, 76.84) * mm, "end": v(128.97, 76.85) * mm});
            skLineSegment(sketch, "E4402", {"start": v(128.97, 76.85) * mm, "end": v(128.97, 76.85) * mm});
            skLineSegment(sketch, "E4403", {"start": v(128.97, 76.85) * mm, "end": v(128.98, 76.86) * mm});
            skLineSegment(sketch, "E4404", {"start": v(128.98, 76.86) * mm, "end": v(128.98, 76.87) * mm});
            skLineSegment(sketch, "E4405", {"start": v(128.98, 76.87) * mm, "end": v(128.99, 76.88) * mm});
            skLineSegment(sketch, "E4406", {"start": v(128.99, 76.88) * mm, "end": v(128.99, 76.9) * mm});
            skLineSegment(sketch, "E4407", {"start": v(128.99, 76.9) * mm, "end": v(129, 76.9) * mm});
            skLineSegment(sketch, "E4408", {"start": v(129, 76.9) * mm, "end": v(129, 76.9) * mm});
            skLineSegment(sketch, "E4409", {"start": v(129, 76.9) * mm, "end": v(129, 76.92) * mm});
            skLineSegment(sketch, "E4410", {"start": v(129, 76.92) * mm, "end": v(129, 76.93) * mm});
            skLineSegment(sketch, "E4411", {"start": v(129, 76.93) * mm, "end": v(129.01, 76.93) * mm});
            skLineSegment(sketch, "E4412", {"start": v(129.01, 76.93) * mm, "end": v(129.02, 76.94) * mm});
            skLineSegment(sketch, "E4413", {"start": v(129.02, 76.94) * mm, "end": v(129.02, 76.95) * mm});
            skLineSegment(sketch, "E4414", {"start": v(129.02, 76.95) * mm, "end": v(129.03, 76.96) * mm});
            skLineSegment(sketch, "E4415", {"start": v(129.03, 76.96) * mm, "end": v(129.03, 76.97) * mm});
            skLineSegment(sketch, "E4416", {"start": v(129.03, 76.97) * mm, "end": v(129.04, 76.97) * mm});
            skLineSegment(sketch, "E4417", {"start": v(129.04, 76.97) * mm, "end": v(129.04, 76.98) * mm});
            skLineSegment(sketch, "E4418", {"start": v(129.04, 76.98) * mm, "end": v(129.05, 76.99) * mm});
            skLineSegment(sketch, "E4419", {"start": v(129.05, 76.99) * mm, "end": v(129.05, 77) * mm});
            skLineSegment(sketch, "E4420", {"start": v(129.05, 77) * mm, "end": v(129.06, 77) * mm});
            skLineSegment(sketch, "E4421", {"start": v(129.06, 77) * mm, "end": v(129.06, 77) * mm});
            skLineSegment(sketch, "E4422", {"start": v(129.06, 77) * mm, "end": v(129.07, 77.02) * mm});
            skLineSegment(sketch, "E4423", {"start": v(129.07, 77.02) * mm, "end": v(129.07, 77.02) * mm});
            skLineSegment(sketch, "E4424", {"start": v(129.07, 77.02) * mm, "end": v(129.08, 77.03) * mm});
            skLineSegment(sketch, "E4425", {"start": v(129.08, 77.03) * mm, "end": v(129.08, 77.03) * mm});
            skLineSegment(sketch, "E4426", {"start": v(129.08, 77.03) * mm, "end": v(129.09, 77.04) * mm});
            skLineSegment(sketch, "E4427", {"start": v(129.09, 77.04) * mm, "end": v(129.1, 77.05) * mm});
            skLineSegment(sketch, "E4428", {"start": v(129.1, 77.05) * mm, "end": v(129.1, 77.05) * mm});
            skLineSegment(sketch, "E4429", {"start": v(129.1, 77.05) * mm, "end": v(129.1, 77.06) * mm});
            skLineSegment(sketch, "E4430", {"start": v(129.1, 77.06) * mm, "end": v(129.11, 77.06) * mm});
            skLineSegment(sketch, "E4431", {"start": v(129.11, 77.06) * mm, "end": v(129.12, 77.07) * mm});
            skLineSegment(sketch, "E4432", {"start": v(129.12, 77.07) * mm, "end": v(129.12, 77.07) * mm});
            skLineSegment(sketch, "E4433", {"start": v(129.12, 77.07) * mm, "end": v(129.13, 77.08) * mm});
            skLineSegment(sketch, "E4434", {"start": v(129.13, 77.08) * mm, "end": v(129.14, 77.08) * mm});
            skLineSegment(sketch, "E4435", {"start": v(129.14, 77.08) * mm, "end": v(129.14, 77.08) * mm});
            skLineSegment(sketch, "E4436", {"start": v(129.14, 77.08) * mm, "end": v(129.15, 77.09) * mm});
            skLineSegment(sketch, "E4437", {"start": v(129.15, 77.09) * mm, "end": v(129.16, 77.1) * mm});
            skLineSegment(sketch, "E4438", {"start": v(129.16, 77.1) * mm, "end": v(129.16, 77.1) * mm});
            skLineSegment(sketch, "E4439", {"start": v(129.16, 77.1) * mm, "end": v(129.17, 77.1) * mm});
            skLineSegment(sketch, "E4440", {"start": v(129.17, 77.1) * mm, "end": v(129.18, 77.1) * mm});
            skLineSegment(sketch, "E4441", {"start": v(129.18, 77.1) * mm, "end": v(129.18, 77.1) * mm});
            skLineSegment(sketch, "E4442", {"start": v(129.18, 77.1) * mm, "end": v(129.19, 77.11) * mm});
            skLineSegment(sketch, "E4443", {"start": v(129.19, 77.11) * mm, "end": v(129.2, 77.11) * mm});
            skLineSegment(sketch, "E4444", {"start": v(129.2, 77.11) * mm, "end": v(129.2, 77.12) * mm});
            skLineSegment(sketch, "E4445", {"start": v(129.2, 77.12) * mm, "end": v(129.21, 77.12) * mm});
            skLineSegment(sketch, "E4446", {"start": v(129.21, 77.12) * mm, "end": v(129.22, 77.12) * mm});
            skLineSegment(sketch, "E4447", {"start": v(129.22, 77.12) * mm, "end": v(129.22, 77.12) * mm});
            skLineSegment(sketch, "E4448", {"start": v(129.22, 77.12) * mm, "end": v(129.23, 77.13) * mm});
            skLineSegment(sketch, "E4449", {"start": v(129.23, 77.13) * mm, "end": v(129.24, 77.13) * mm});
            skLineSegment(sketch, "E4450", {"start": v(129.24, 77.13) * mm, "end": v(129.25, 77.13) * mm});
            skLineSegment(sketch, "E4451", {"start": v(129.25, 77.13) * mm, "end": v(129.25, 77.13) * mm});
            skLineSegment(sketch, "E4452", {"start": v(129.25, 77.13) * mm, "end": v(129.26, 77.13) * mm});
            skLineSegment(sketch, "E4453", {"start": v(129.26, 77.13) * mm, "end": v(129.27, 77.13) * mm});
            skLineSegment(sketch, "E4454", {"start": v(129.27, 77.13) * mm, "end": v(129.28, 77.13) * mm});
            skLineSegment(sketch, "E4455", {"start": v(129.28, 77.13) * mm, "end": v(129.28, 77.13) * mm});
            skLineSegment(sketch, "E4456", {"start": v(129.28, 77.13) * mm, "end": v(129.3, 77.13) * mm});
            skLineSegment(sketch, "E4457", {"start": v(129.3, 77.13) * mm, "end": v(129.3, 77.13) * mm});
            skLineSegment(sketch, "E4458", {"start": v(129.3, 77.13) * mm, "end": v(129.31, 77.13) * mm});
            skLineSegment(sketch, "E4459", {"start": v(129.31, 77.13) * mm, "end": v(129.32, 77.13) * mm});
            skLineSegment(sketch, "E4460", {"start": v(129.32, 77.13) * mm, "end": v(129.33, 77.13) * mm});
            skLineSegment(sketch, "E4461", {"start": v(129.33, 77.13) * mm, "end": v(129.34, 77.13) * mm});
            skLineSegment(sketch, "E4462", {"start": v(129.34, 77.13) * mm, "end": v(129.35, 77.13) * mm});
            skLineSegment(sketch, "E4463", {"start": v(129.35, 77.13) * mm, "end": v(129.35, 77.13) * mm});
            skLineSegment(sketch, "E4464", {"start": v(129.35, 77.13) * mm, "end": v(129.36, 77.13) * mm});
            skLineSegment(sketch, "E4465", {"start": v(129.36, 77.13) * mm, "end": v(129.37, 77.13) * mm});
            skLineSegment(sketch, "E4466", {"start": v(129.37, 77.13) * mm, "end": v(129.38, 77.13) * mm});
            skLineSegment(sketch, "E4467", {"start": v(129.38, 77.13) * mm, "end": v(129.39, 77.13) * mm});
            skLineSegment(sketch, "E4468", {"start": v(129.39, 77.13) * mm, "end": v(129.4, 77.12) * mm});
            skLineSegment(sketch, "E4469", {"start": v(129.4, 77.12) * mm, "end": v(129.4, 77.12) * mm});
            skLineSegment(sketch, "E4470", {"start": v(129.4, 77.12) * mm, "end": v(129.41, 77.12) * mm});
            skLineSegment(sketch, "E4471", {"start": v(129.41, 77.12) * mm, "end": v(129.42, 77.12) * mm});
            skLineSegment(sketch, "E4472", {"start": v(129.42, 77.12) * mm, "end": v(129.43, 77.11) * mm});
            skLineSegment(sketch, "E4473", {"start": v(129.43, 77.11) * mm, "end": v(129.44, 77.1) * mm});
            skLineSegment(sketch, "E4474", {"start": v(129.44, 77.1) * mm, "end": v(129.45, 77.1) * mm});
            skLineSegment(sketch, "E4475", {"start": v(129.45, 77.1) * mm, "end": v(129.46, 77.1) * mm});
            skLineSegment(sketch, "E4476", {"start": v(129.46, 77.1) * mm, "end": v(129.46, 77.1) * mm});
            skLineSegment(sketch, "E4477", {"start": v(129.46, 77.1) * mm, "end": v(129.47, 77.1) * mm});
            skLineSegment(sketch, "E4478", {"start": v(129.47, 77.1) * mm, "end": v(129.48, 77.1) * mm});
            skLineSegment(sketch, "E4479", {"start": v(129.48, 77.1) * mm, "end": v(129.5, 77.09) * mm});
            skLineSegment(sketch, "E4480", {"start": v(129.5, 77.09) * mm, "end": v(129.5, 77.08) * mm});
            skLineSegment(sketch, "E4481", {"start": v(129.5, 77.08) * mm, "end": v(129.5, 77.08) * mm});
            skLineSegment(sketch, "E4482", {"start": v(129.5, 77.08) * mm, "end": v(129.52, 77.07) * mm});
            skLineSegment(sketch, "E4483", {"start": v(129.52, 77.07) * mm, "end": v(129.53, 77.07) * mm});
            skLineSegment(sketch, "E4484", {"start": v(129.53, 77.07) * mm, "end": v(129.54, 77.06) * mm});
            skLineSegment(sketch, "E4485", {"start": v(129.54, 77.06) * mm, "end": v(129.54, 77.05) * mm});
            skLineSegment(sketch, "E4486", {"start": v(129.54, 77.05) * mm, "end": v(129.55, 77.05) * mm});
            skLineSegment(sketch, "E4487", {"start": v(129.55, 77.05) * mm, "end": v(129.56, 77.04) * mm});
            skLineSegment(sketch, "E4488", {"start": v(129.56, 77.04) * mm, "end": v(129.57, 77.04) * mm});
            skLineSegment(sketch, "E4489", {"start": v(129.57, 77.04) * mm, "end": v(129.58, 77.03) * mm});
            skLineSegment(sketch, "E4490", {"start": v(129.58, 77.03) * mm, "end": v(129.6, 77.02) * mm});
            skLineSegment(sketch, "E4491", {"start": v(129.6, 77.02) * mm, "end": v(129.6, 77.02) * mm});
            skLineSegment(sketch, "E4492", {"start": v(129.6, 77.02) * mm, "end": v(129.6, 77) * mm});
            skLineSegment(sketch, "E4493", {"start": v(129.6, 77) * mm, "end": v(129.62, 77) * mm});
            skLineSegment(sketch, "E4494", {"start": v(129.62, 77) * mm, "end": v(129.63, 77) * mm});
            skLineSegment(sketch, "E4495", {"start": v(129.63, 77) * mm, "end": v(129.64, 76.98) * mm});
            skLineSegment(sketch, "E4496", {"start": v(129.64, 76.98) * mm, "end": v(129.65, 76.98) * mm});
            skLineSegment(sketch, "E4497", {"start": v(129.65, 76.98) * mm, "end": v(129.66, 76.97) * mm});
            skLineSegment(sketch, "E4498", {"start": v(129.66, 76.97) * mm, "end": v(129.67, 76.96) * mm});
            skLineSegment(sketch, "E4499", {"start": v(129.67, 76.96) * mm, "end": v(129.68, 76.95) * mm});
            skLineSegment(sketch, "E4500", {"start": v(129.68, 76.95) * mm, "end": v(129.69, 76.94) * mm});
            skLineSegment(sketch, "E4501", {"start": v(129.69, 76.94) * mm, "end": v(129.7, 76.93) * mm});
            skLineSegment(sketch, "E4502", {"start": v(129.7, 76.93) * mm, "end": v(129.7, 76.92) * mm});
            skLineSegment(sketch, "E4503", {"start": v(129.7, 76.92) * mm, "end": v(129.72, 76.91) * mm});
            skLineSegment(sketch, "E4504", {"start": v(129.72, 76.91) * mm, "end": v(129.72, 76.9) * mm});
            skLineSegment(sketch, "E4505", {"start": v(129.72, 76.9) * mm, "end": v(129.73, 76.9) * mm});
            skLineSegment(sketch, "E4506", {"start": v(129.73, 76.9) * mm, "end": v(129.74, 76.88) * mm});
            skLineSegment(sketch, "E4507", {"start": v(129.74, 76.88) * mm, "end": v(129.75, 76.87) * mm});
            skLineSegment(sketch, "E4508", {"start": v(129.75, 76.87) * mm, "end": v(129.76, 76.87) * mm});
            skLineSegment(sketch, "E4509", {"start": v(129.76, 76.87) * mm, "end": v(129.76, 76.86) * mm});
            skLineSegment(sketch, "E4510", {"start": v(129.76, 76.86) * mm, "end": v(129.77, 76.85) * mm});
            skLineSegment(sketch, "E4511", {"start": v(129.77, 76.85) * mm, "end": v(129.77, 76.85) * mm});
            skLineSegment(sketch, "E4512", {"start": v(129.77, 76.85) * mm, "end": v(129.78, 76.84) * mm});
            skLineSegment(sketch, "E4513", {"start": v(129.78, 76.84) * mm, "end": v(129.78, 76.84) * mm});
            skLineSegment(sketch, "E4514", {"start": v(129.78, 76.84) * mm, "end": v(129.79, 76.83) * mm});
            skLineSegment(sketch, "E4515", {"start": v(129.79, 76.83) * mm, "end": v(129.8, 76.82) * mm});
            skLineSegment(sketch, "E4516", {"start": v(129.8, 76.82) * mm, "end": v(129.8, 76.82) * mm});
            skLineSegment(sketch, "E4517", {"start": v(129.8, 76.82) * mm, "end": v(129.8, 76.81) * mm});
            skLineSegment(sketch, "E4518", {"start": v(129.8, 76.81) * mm, "end": v(129.8, 76.8) * mm});
            skLineSegment(sketch, "E4519", {"start": v(129.8, 76.8) * mm, "end": v(129.81, 76.8) * mm});
            skLineSegment(sketch, "E4520", {"start": v(129.81, 76.8) * mm, "end": v(129.82, 76.8) * mm});
            skLineSegment(sketch, "E4521", {"start": v(129.82, 76.8) * mm, "end": v(129.82, 76.79) * mm});
            skLineSegment(sketch, "E4522", {"start": v(129.82, 76.79) * mm, "end": v(129.83, 76.78) * mm});
            skLineSegment(sketch, "E4523", {"start": v(129.83, 76.78) * mm, "end": v(129.83, 76.77) * mm});
            skLineSegment(sketch, "E4524", {"start": v(129.83, 76.77) * mm, "end": v(129.84, 76.77) * mm});
            skLineSegment(sketch, "E4525", {"start": v(129.84, 76.77) * mm, "end": v(129.84, 76.76) * mm});
            skLineSegment(sketch, "E4526", {"start": v(129.84, 76.76) * mm, "end": v(129.85, 76.76) * mm});
            skLineSegment(sketch, "E4527", {"start": v(129.85, 76.76) * mm, "end": v(129.86, 76.75) * mm});
            skLineSegment(sketch, "E4528", {"start": v(129.86, 76.75) * mm, "end": v(129.86, 76.74) * mm});
            skLineSegment(sketch, "E4529", {"start": v(129.86, 76.74) * mm, "end": v(129.87, 76.73) * mm});
            skLineSegment(sketch, "E4530", {"start": v(129.87, 76.73) * mm, "end": v(129.87, 76.73) * mm});
            skLineSegment(sketch, "E4531", {"start": v(129.87, 76.73) * mm, "end": v(129.88, 76.72) * mm});
            skLineSegment(sketch, "E4532", {"start": v(129.88, 76.72) * mm, "end": v(129.88, 76.71) * mm});
            skLineSegment(sketch, "E4533", {"start": v(129.88, 76.71) * mm, "end": v(129.89, 76.7) * mm});
            skLineSegment(sketch, "E4534", {"start": v(129.89, 76.7) * mm, "end": v(129.9, 76.7) * mm});
            skLineSegment(sketch, "E4535", {"start": v(129.9, 76.7) * mm, "end": v(129.9, 76.7) * mm});
            skLineSegment(sketch, "E4536", {"start": v(129.9, 76.7) * mm, "end": v(129.9, 76.69) * mm});
            skLineSegment(sketch, "E4537", {"start": v(129.9, 76.69) * mm, "end": v(129.9, 76.68) * mm});
            skLineSegment(sketch, "E4538", {"start": v(129.9, 76.68) * mm, "end": v(129.91, 76.67) * mm});
            skLineSegment(sketch, "E4539", {"start": v(129.91, 76.67) * mm, "end": v(129.92, 76.66) * mm});
            skLineSegment(sketch, "E4540", {"start": v(129.92, 76.66) * mm, "end": v(129.92, 76.66) * mm});
            skLineSegment(sketch, "E4541", {"start": v(129.92, 76.66) * mm, "end": v(129.93, 76.65) * mm});
            skLineSegment(sketch, "E4542", {"start": v(129.93, 76.65) * mm, "end": v(129.93, 76.64) * mm});
            skLineSegment(sketch, "E4543", {"start": v(129.93, 76.64) * mm, "end": v(129.94, 76.63) * mm});
            skLineSegment(sketch, "E4544", {"start": v(129.94, 76.63) * mm, "end": v(129.94, 76.63) * mm});
            skLineSegment(sketch, "E4545", {"start": v(129.94, 76.63) * mm, "end": v(129.95, 76.62) * mm});
            skLineSegment(sketch, "E4546", {"start": v(129.95, 76.62) * mm, "end": v(129.95, 76.6) * mm});
            skLineSegment(sketch, "E4547", {"start": v(129.95, 76.6) * mm, "end": v(129.96, 76.6) * mm});
            skLineSegment(sketch, "E4548", {"start": v(129.96, 76.6) * mm, "end": v(129.96, 76.6) * mm});
            skLineSegment(sketch, "E4549", {"start": v(129.96, 76.6) * mm, "end": v(129.97, 76.59) * mm});
            skLineSegment(sketch, "E4550", {"start": v(129.97, 76.59) * mm, "end": v(129.97, 76.58) * mm});
            skLineSegment(sketch, "E4551", {"start": v(129.97, 76.58) * mm, "end": v(129.98, 76.57) * mm});
            skLineSegment(sketch, "E4552", {"start": v(129.98, 76.57) * mm, "end": v(129.98, 76.56) * mm});
            skLineSegment(sketch, "E4553", {"start": v(129.98, 76.56) * mm, "end": v(129.99, 76.55) * mm});
            skLineSegment(sketch, "E4554", {"start": v(129.99, 76.55) * mm, "end": v(130, 76.54) * mm});
            skLineSegment(sketch, "E4555", {"start": v(130, 76.54) * mm, "end": v(130, 76.54) * mm});
            skLineSegment(sketch, "E4556", {"start": v(130, 76.54) * mm, "end": v(130, 76.53) * mm});
            skLineSegment(sketch, "E4557", {"start": v(130, 76.53) * mm, "end": v(130.01, 76.52) * mm});
            skLineSegment(sketch, "E4558", {"start": v(130.01, 76.52) * mm, "end": v(130.02, 76.5) * mm});
            skLineSegment(sketch, "E4559", {"start": v(130.02, 76.5) * mm, "end": v(130.02, 76.5) * mm});
            skLineSegment(sketch, "E4560", {"start": v(130.02, 76.5) * mm, "end": v(130.03, 76.5) * mm});
            skLineSegment(sketch, "E4561", {"start": v(130.03, 76.5) * mm, "end": v(130.03, 76.48) * mm});
            skLineSegment(sketch, "E4562", {"start": v(130.03, 76.48) * mm, "end": v(130.04, 76.47) * mm});
            skLineSegment(sketch, "E4563", {"start": v(130.04, 76.47) * mm, "end": v(130.04, 76.46) * mm});
            skLineSegment(sketch, "E4564", {"start": v(130.04, 76.46) * mm, "end": v(130.05, 76.46) * mm});
            skLineSegment(sketch, "E4565", {"start": v(130.05, 76.46) * mm, "end": v(130.05, 76.45) * mm});
            skLineSegment(sketch, "E4566", {"start": v(130.05, 76.45) * mm, "end": v(130.06, 76.44) * mm});
            skLineSegment(sketch, "E4567", {"start": v(130.06, 76.44) * mm, "end": v(130.06, 76.43) * mm});
            skLineSegment(sketch, "E4568", {"start": v(130.06, 76.43) * mm, "end": v(130.07, 76.42) * mm});
            skLineSegment(sketch, "E4569", {"start": v(130.07, 76.42) * mm, "end": v(130.07, 76.4) * mm});
            skLineSegment(sketch, "E4570", {"start": v(130.07, 76.4) * mm, "end": v(130.08, 76.4) * mm});
            skLineSegment(sketch, "E4571", {"start": v(130.08, 76.4) * mm, "end": v(130.08, 76.4) * mm});
            skLineSegment(sketch, "E4572", {"start": v(130.08, 76.4) * mm, "end": v(130.09, 76.39) * mm});
            skLineSegment(sketch, "E4573", {"start": v(130.09, 76.39) * mm, "end": v(130.1, 76.38) * mm});
            skLineSegment(sketch, "E4574", {"start": v(130.1, 76.38) * mm, "end": v(130.1, 76.37) * mm});
            skLineSegment(sketch, "E4575", {"start": v(130.1, 76.37) * mm, "end": v(130.1, 76.37) * mm});
            skLineSegment(sketch, "E4576", {"start": v(130.1, 76.37) * mm, "end": v(130.1, 76.36) * mm});
            skLineSegment(sketch, "E4577", {"start": v(130.1, 76.36) * mm, "end": v(130.1, 76.36) * mm});
            skLineSegment(sketch, "E4578", {"start": v(130.1, 76.36) * mm, "end": v(130.1, 76.35) * mm});
            skLineSegment(sketch, "E4579", {"start": v(130.1, 76.35) * mm, "end": v(130.11, 76.34) * mm});
            skLineSegment(sketch, "E4580", {"start": v(130.11, 76.34) * mm, "end": v(130.12, 76.34) * mm});
            skLineSegment(sketch, "E4581", {"start": v(130.12, 76.34) * mm, "end": v(130.12, 76.33) * mm});
            skLineSegment(sketch, "E4582", {"start": v(130.12, 76.33) * mm, "end": v(130.12, 76.33) * mm});
            skLineSegment(sketch, "E4583", {"start": v(130.12, 76.33) * mm, "end": v(130.13, 76.32) * mm});
            skLineSegment(sketch, "E4584", {"start": v(130.13, 76.32) * mm, "end": v(130.13, 76.32) * mm});
            skLineSegment(sketch, "E4585", {"start": v(130.13, 76.32) * mm, "end": v(130.13, 76.31) * mm});
            skLineSegment(sketch, "E4586", {"start": v(130.13, 76.31) * mm, "end": v(130.14, 76.3) * mm});
            skLineSegment(sketch, "E4587", {"start": v(130.14, 76.3) * mm, "end": v(130.14, 76.3) * mm});
            skLineSegment(sketch, "E4588", {"start": v(130.14, 76.3) * mm, "end": v(130.15, 76.3) * mm});
            skLineSegment(sketch, "E4589", {"start": v(130.15, 76.3) * mm, "end": v(130.15, 76.29) * mm});
            skLineSegment(sketch, "E4590", {"start": v(130.15, 76.29) * mm, "end": v(130.15, 76.28) * mm});
            skLineSegment(sketch, "E4591", {"start": v(130.15, 76.28) * mm, "end": v(130.16, 76.28) * mm});
            skLineSegment(sketch, "E4592", {"start": v(130.16, 76.28) * mm, "end": v(130.16, 76.27) * mm});
            skLineSegment(sketch, "E4593", {"start": v(130.16, 76.27) * mm, "end": v(130.17, 76.27) * mm});
            skLineSegment(sketch, "E4594", {"start": v(130.17, 76.27) * mm, "end": v(130.17, 76.26) * mm});
            skLineSegment(sketch, "E4595", {"start": v(130.17, 76.26) * mm, "end": v(130.17, 76.26) * mm});
            skLineSegment(sketch, "E4596", {"start": v(130.17, 76.26) * mm, "end": v(130.18, 76.25) * mm});
            skLineSegment(sketch, "E4597", {"start": v(130.18, 76.25) * mm, "end": v(130.18, 76.25) * mm});
            skLineSegment(sketch, "E4598", {"start": v(130.18, 76.25) * mm, "end": v(130.19, 76.24) * mm});
            skLineSegment(sketch, "E4599", {"start": v(130.19, 76.24) * mm, "end": v(130.19, 76.24) * mm});
            skLineSegment(sketch, "E4600", {"start": v(130.19, 76.24) * mm, "end": v(130.2, 76.23) * mm});
            skLineSegment(sketch, "E4601", {"start": v(130.2, 76.23) * mm, "end": v(130.2, 76.23) * mm});
            skLineSegment(sketch, "E4602", {"start": v(130.2, 76.23) * mm, "end": v(130.2, 76.22) * mm});
            skLineSegment(sketch, "E4603", {"start": v(130.2, 76.22) * mm, "end": v(130.2, 76.22) * mm});
            skLineSegment(sketch, "E4604", {"start": v(130.2, 76.22) * mm, "end": v(130.21, 76.21) * mm});
            skLineSegment(sketch, "E4605", {"start": v(130.21, 76.21) * mm, "end": v(130.21, 76.2) * mm});
            skLineSegment(sketch, "E4606", {"start": v(130.21, 76.2) * mm, "end": v(130.22, 76.2) * mm});
            skLineSegment(sketch, "E4607", {"start": v(130.22, 76.2) * mm, "end": v(130.22, 76.2) * mm});
            skLineSegment(sketch, "E4608", {"start": v(130.22, 76.2) * mm, "end": v(130.23, 76.2) * mm});
            skLineSegment(sketch, "E4609", {"start": v(130.23, 76.2) * mm, "end": v(130.23, 76.19) * mm});
            skLineSegment(sketch, "E4610", {"start": v(130.23, 76.19) * mm, "end": v(130.24, 76.18) * mm});
            skLineSegment(sketch, "E4611", {"start": v(130.24, 76.18) * mm, "end": v(130.24, 76.18) * mm});
            skLineSegment(sketch, "E4612", {"start": v(130.24, 76.18) * mm, "end": v(130.24, 76.17) * mm});
            skLineSegment(sketch, "E4613", {"start": v(130.24, 76.17) * mm, "end": v(130.25, 76.17) * mm});
            skLineSegment(sketch, "E4614", {"start": v(130.25, 76.17) * mm, "end": v(130.25, 76.16) * mm});
            skLineSegment(sketch, "E4615", {"start": v(130.25, 76.16) * mm, "end": v(130.26, 76.16) * mm});
            skLineSegment(sketch, "E4616", {"start": v(130.26, 76.16) * mm, "end": v(130.26, 76.15) * mm});
            skLineSegment(sketch, "E4617", {"start": v(130.26, 76.15) * mm, "end": v(130.27, 76.15) * mm});
            skLineSegment(sketch, "E4618", {"start": v(130.27, 76.15) * mm, "end": v(130.27, 76.14) * mm});
            skLineSegment(sketch, "E4619", {"start": v(130.27, 76.14) * mm, "end": v(130.27, 76.14) * mm});
            skLineSegment(sketch, "E4620", {"start": v(130.27, 76.14) * mm, "end": v(130.28, 76.13) * mm});
            skLineSegment(sketch, "E4621", {"start": v(130.28, 76.13) * mm, "end": v(130.28, 76.13) * mm});
            skLineSegment(sketch, "E4622", {"start": v(130.28, 76.13) * mm, "end": v(130.29, 76.12) * mm});
            skLineSegment(sketch, "E4623", {"start": v(130.29, 76.12) * mm, "end": v(130.3, 76.12) * mm});
            skLineSegment(sketch, "E4624", {"start": v(130.3, 76.12) * mm, "end": v(130.3, 76.12) * mm});
            skLineSegment(sketch, "E4625", {"start": v(130.3, 76.12) * mm, "end": v(130.3, 76.11) * mm});
            skLineSegment(sketch, "E4626", {"start": v(130.3, 76.11) * mm, "end": v(130.3, 76.1) * mm});
            skLineSegment(sketch, "E4627", {"start": v(130.3, 76.1) * mm, "end": v(130.31, 76.1) * mm});
            skLineSegment(sketch, "E4628", {"start": v(130.31, 76.1) * mm, "end": v(130.32, 76.1) * mm});
            skLineSegment(sketch, "E4629", {"start": v(130.32, 76.1) * mm, "end": v(130.32, 76.1) * mm});
            skLineSegment(sketch, "E4630", {"start": v(130.32, 76.1) * mm, "end": v(130.32, 76.09) * mm});
            skLineSegment(sketch, "E4631", {"start": v(130.32, 76.09) * mm, "end": v(130.33, 76.09) * mm});
            skLineSegment(sketch, "E4632", {"start": v(130.33, 76.09) * mm, "end": v(130.33, 76.08) * mm});
            skLineSegment(sketch, "E4633", {"start": v(130.33, 76.08) * mm, "end": v(130.34, 76.08) * mm});
            skLineSegment(sketch, "E4634", {"start": v(130.34, 76.08) * mm, "end": v(130.34, 76.07) * mm});
            skLineSegment(sketch, "E4635", {"start": v(130.34, 76.07) * mm, "end": v(130.35, 76.07) * mm});
            skLineSegment(sketch, "E4636", {"start": v(130.35, 76.07) * mm, "end": v(130.35, 76.07) * mm});
            skLineSegment(sketch, "E4637", {"start": v(130.35, 76.07) * mm, "end": v(130.36, 76.06) * mm});
            skLineSegment(sketch, "E4638", {"start": v(130.36, 76.06) * mm, "end": v(130.36, 76.06) * mm});
            skLineSegment(sketch, "E4639", {"start": v(130.36, 76.06) * mm, "end": v(130.37, 76.05) * mm});
            skLineSegment(sketch, "E4640", {"start": v(130.37, 76.05) * mm, "end": v(130.37, 76.05) * mm});
            skLineSegment(sketch, "E4641", {"start": v(130.37, 76.05) * mm, "end": v(130.38, 76.05) * mm});
            skLineSegment(sketch, "E4642", {"start": v(130.38, 76.05) * mm, "end": v(130.38, 76.04) * mm});
            skLineSegment(sketch, "E4643", {"start": v(130.38, 76.04) * mm, "end": v(130.39, 76.04) * mm});
            skLineSegment(sketch, "E4644", {"start": v(130.39, 76.04) * mm, "end": v(130.4, 76.03) * mm});
            skLineSegment(sketch, "E4645", {"start": v(130.4, 76.03) * mm, "end": v(130.4, 76.03) * mm});
            skLineSegment(sketch, "E4646", {"start": v(130.4, 76.03) * mm, "end": v(130.4, 76.02) * mm});
            skLineSegment(sketch, "E4647", {"start": v(130.4, 76.02) * mm, "end": v(130.41, 76.02) * mm});
            skLineSegment(sketch, "E4648", {"start": v(130.41, 76.02) * mm, "end": v(130.42, 76.02) * mm});
            skLineSegment(sketch, "E4649", {"start": v(130.42, 76.02) * mm, "end": v(130.42, 76.01) * mm});
            skLineSegment(sketch, "E4650", {"start": v(130.42, 76.01) * mm, "end": v(130.43, 76) * mm});
            skLineSegment(sketch, "E4651", {"start": v(130.43, 76) * mm, "end": v(130.43, 76) * mm});
            skLineSegment(sketch, "E4652", {"start": v(130.43, 76) * mm, "end": v(130.44, 76) * mm});
            skLineSegment(sketch, "E4653", {"start": v(130.44, 76) * mm, "end": v(130.44, 76) * mm});
            skLineSegment(sketch, "E4654", {"start": v(130.44, 76) * mm, "end": v(130.45, 76) * mm});
            skLineSegment(sketch, "E4655", {"start": v(130.45, 76) * mm, "end": v(130.45, 76) * mm});
            skLineSegment(sketch, "E4656", {"start": v(130.45, 76) * mm, "end": v(130.46, 75.99) * mm});
            skLineSegment(sketch, "E4657", {"start": v(130.46, 75.99) * mm, "end": v(130.46, 75.98) * mm});
            skLineSegment(sketch, "E4658", {"start": v(130.46, 75.98) * mm, "end": v(130.47, 75.98) * mm});
            skLineSegment(sketch, "E4659", {"start": v(130.47, 75.98) * mm, "end": v(130.47, 75.98) * mm});
            skLineSegment(sketch, "E4660", {"start": v(130.47, 75.98) * mm, "end": v(130.48, 75.97) * mm});
            skLineSegment(sketch, "E4661", {"start": v(130.48, 75.97) * mm, "end": v(130.48, 75.97) * mm});
            skLineSegment(sketch, "E4662", {"start": v(130.48, 75.97) * mm, "end": v(130.49, 75.97) * mm});
            skLineSegment(sketch, "E4663", {"start": v(130.49, 75.97) * mm, "end": v(130.5, 75.96) * mm});
            skLineSegment(sketch, "E4664", {"start": v(130.5, 75.96) * mm, "end": v(130.5, 75.96) * mm});
            skLineSegment(sketch, "E4665", {"start": v(130.5, 75.96) * mm, "end": v(130.51, 75.95) * mm});
            skLineSegment(sketch, "E4666", {"start": v(130.51, 75.95) * mm, "end": v(130.52, 75.95) * mm});
            skLineSegment(sketch, "E4667", {"start": v(130.52, 75.95) * mm, "end": v(130.52, 75.95) * mm});
            skLineSegment(sketch, "E4668", {"start": v(130.52, 75.95) * mm, "end": v(130.53, 75.94) * mm});
            skLineSegment(sketch, "E4669", {"start": v(130.53, 75.94) * mm, "end": v(130.53, 75.94) * mm});
            skLineSegment(sketch, "E4670", {"start": v(130.53, 75.94) * mm, "end": v(130.54, 75.94) * mm});
            skLineSegment(sketch, "E4671", {"start": v(130.54, 75.94) * mm, "end": v(130.54, 75.93) * mm});
            skLineSegment(sketch, "E4672", {"start": v(130.54, 75.93) * mm, "end": v(130.55, 75.93) * mm});
            skLineSegment(sketch, "E4673", {"start": v(130.55, 75.93) * mm, "end": v(130.56, 75.93) * mm});
            skLineSegment(sketch, "E4674", {"start": v(130.56, 75.93) * mm, "end": v(130.56, 75.93) * mm});
            skLineSegment(sketch, "E4675", {"start": v(130.56, 75.93) * mm, "end": v(130.57, 75.92) * mm});
            skLineSegment(sketch, "E4676", {"start": v(130.57, 75.92) * mm, "end": v(130.57, 75.92) * mm});
            skLineSegment(sketch, "E4677", {"start": v(130.57, 75.92) * mm, "end": v(130.58, 75.92) * mm});
            skLineSegment(sketch, "E4678", {"start": v(130.58, 75.92) * mm, "end": v(130.58, 75.92) * mm});
            skLineSegment(sketch, "E4679", {"start": v(130.58, 75.92) * mm, "end": v(130.59, 75.91) * mm});
            skLineSegment(sketch, "E4680", {"start": v(130.59, 75.91) * mm, "end": v(130.6, 75.91) * mm});
            skLineSegment(sketch, "E4681", {"start": v(130.6, 75.91) * mm, "end": v(130.6, 75.9) * mm});
            skLineSegment(sketch, "E4682", {"start": v(130.6, 75.9) * mm, "end": v(130.6, 75.9) * mm});
            skLineSegment(sketch, "E4683", {"start": v(130.6, 75.9) * mm, "end": v(130.61, 75.9) * mm});
            skLineSegment(sketch, "E4684", {"start": v(130.61, 75.9) * mm, "end": v(130.62, 75.9) * mm});
            skLineSegment(sketch, "E4685", {"start": v(130.62, 75.9) * mm, "end": v(130.63, 75.9) * mm});
            skLineSegment(sketch, "E4686", {"start": v(130.63, 75.9) * mm, "end": v(130.63, 75.9) * mm});
            skLineSegment(sketch, "E4687", {"start": v(130.63, 75.9) * mm, "end": v(130.64, 75.9) * mm});
            skLineSegment(sketch, "E4688", {"start": v(130.64, 75.9) * mm, "end": v(130.64, 75.89) * mm});
            skLineSegment(sketch, "E4689", {"start": v(130.64, 75.89) * mm, "end": v(130.65, 75.89) * mm});
            skLineSegment(sketch, "E4690", {"start": v(130.65, 75.89) * mm, "end": v(130.65, 75.88) * mm});
            skLineSegment(sketch, "E4691", {"start": v(130.65, 75.88) * mm, "end": v(130.66, 75.88) * mm});
            skLineSegment(sketch, "E4692", {"start": v(130.66, 75.88) * mm, "end": v(130.66, 75.88) * mm});
            skLineSegment(sketch, "E4693", {"start": v(130.66, 75.88) * mm, "end": v(130.67, 75.88) * mm});
            skLineSegment(sketch, "E4694", {"start": v(130.67, 75.88) * mm, "end": v(130.68, 75.88) * mm});
            skLineSegment(sketch, "E4695", {"start": v(130.68, 75.88) * mm, "end": v(130.68, 75.87) * mm});
            skLineSegment(sketch, "E4696", {"start": v(130.68, 75.87) * mm, "end": v(130.69, 75.87) * mm});
            skLineSegment(sketch, "E4697", {"start": v(130.69, 75.87) * mm, "end": v(130.7, 75.87) * mm});
            skLineSegment(sketch, "E4698", {"start": v(130.7, 75.87) * mm, "end": v(130.7, 75.87) * mm});
            skLineSegment(sketch, "E4699", {"start": v(130.7, 75.87) * mm, "end": v(130.7, 75.86) * mm});
            skLineSegment(sketch, "E4700", {"start": v(130.7, 75.86) * mm, "end": v(130.72, 75.86) * mm});
            skLineSegment(sketch, "E4701", {"start": v(130.72, 75.86) * mm, "end": v(130.72, 75.86) * mm});
            skLineSegment(sketch, "E4702", {"start": v(130.72, 75.86) * mm, "end": v(130.73, 75.86) * mm});
            skLineSegment(sketch, "E4703", {"start": v(130.73, 75.86) * mm, "end": v(130.73, 75.86) * mm});
            skLineSegment(sketch, "E4704", {"start": v(130.73, 75.86) * mm, "end": v(130.74, 75.85) * mm});
            skLineSegment(sketch, "E4705", {"start": v(130.74, 75.85) * mm, "end": v(130.74, 75.85) * mm});
            skLineSegment(sketch, "E4706", {"start": v(130.74, 75.85) * mm, "end": v(130.75, 75.85) * mm});
            skLineSegment(sketch, "E4707", {"start": v(130.75, 75.85) * mm, "end": v(130.76, 75.85) * mm});
            skLineSegment(sketch, "E4708", {"start": v(130.76, 75.85) * mm, "end": v(130.76, 75.85) * mm});
            skLineSegment(sketch, "E4709", {"start": v(130.76, 75.85) * mm, "end": v(130.77, 75.85) * mm});
            skLineSegment(sketch, "E4710", {"start": v(130.77, 75.85) * mm, "end": v(130.77, 75.85) * mm});
            skLineSegment(sketch, "E4711", {"start": v(130.77, 75.85) * mm, "end": v(130.78, 75.84) * mm});
            skLineSegment(sketch, "E4712", {"start": v(130.78, 75.84) * mm, "end": v(130.78, 75.84) * mm});
            skLineSegment(sketch, "E4713", {"start": v(130.78, 75.84) * mm, "end": v(130.8, 75.84) * mm});
            skLineSegment(sketch, "E4714", {"start": v(130.8, 75.84) * mm, "end": v(130.8, 75.84) * mm});
            skLineSegment(sketch, "E4715", {"start": v(130.8, 75.84) * mm, "end": v(130.81, 75.84) * mm});
            skLineSegment(sketch, "E4716", {"start": v(130.81, 75.84) * mm, "end": v(130.82, 75.83) * mm});
            skLineSegment(sketch, "E4717", {"start": v(130.82, 75.83) * mm, "end": v(130.83, 75.83) * mm});
            skLineSegment(sketch, "E4718", {"start": v(130.83, 75.83) * mm, "end": v(130.83, 75.83) * mm});
            skLineSegment(sketch, "E4719", {"start": v(130.83, 75.83) * mm, "end": v(130.84, 75.83) * mm});
            skLineSegment(sketch, "E4720", {"start": v(130.84, 75.83) * mm, "end": v(130.84, 75.83) * mm});
            skLineSegment(sketch, "E4721", {"start": v(130.84, 75.83) * mm, "end": v(130.85, 75.83) * mm});
            skLineSegment(sketch, "E4722", {"start": v(130.85, 75.83) * mm, "end": v(130.85, 75.83) * mm});
            skLineSegment(sketch, "E4723", {"start": v(130.85, 75.83) * mm, "end": v(130.86, 75.83) * mm});
            skLineSegment(sketch, "E4724", {"start": v(130.86, 75.83) * mm, "end": v(130.87, 75.83) * mm});
            skLineSegment(sketch, "E4725", {"start": v(130.87, 75.83) * mm, "end": v(130.87, 75.82) * mm});
            skLineSegment(sketch, "E4726", {"start": v(130.87, 75.82) * mm, "end": v(130.88, 75.82) * mm});
            skLineSegment(sketch, "E4727", {"start": v(130.88, 75.82) * mm, "end": v(130.88, 75.82) * mm});
            skLineSegment(sketch, "E4728", {"start": v(130.88, 75.82) * mm, "end": v(130.89, 75.82) * mm});
            skLineSegment(sketch, "E4729", {"start": v(130.89, 75.82) * mm, "end": v(130.9, 75.82) * mm});
            skLineSegment(sketch, "E4730", {"start": v(130.9, 75.82) * mm, "end": v(130.9, 75.82) * mm});
            skLineSegment(sketch, "E4731", {"start": v(130.9, 75.82) * mm, "end": v(130.91, 75.82) * mm});
            skLineSegment(sketch, "E4732", {"start": v(130.91, 75.82) * mm, "end": v(130.92, 75.82) * mm});
            skLineSegment(sketch, "E4733", {"start": v(130.92, 75.82) * mm, "end": v(130.93, 75.82) * mm});
            skLineSegment(sketch, "E4734", {"start": v(130.93, 75.82) * mm, "end": v(130.93, 75.82) * mm});
            skLineSegment(sketch, "E4735", {"start": v(130.93, 75.82) * mm, "end": v(130.94, 75.82) * mm});
            skLineSegment(sketch, "E4736", {"start": v(130.94, 75.82) * mm, "end": v(130.94, 75.82) * mm});
            skLineSegment(sketch, "E4737", {"start": v(130.94, 75.82) * mm, "end": v(130.95, 75.82) * mm});
            skLineSegment(sketch, "E4738", {"start": v(130.95, 75.82) * mm, "end": v(130.96, 75.82) * mm});
            skLineSegment(sketch, "E4739", {"start": v(130.96, 75.82) * mm, "end": v(130.96, 75.82) * mm});
            skLineSegment(sketch, "E4740", {"start": v(130.96, 75.82) * mm, "end": v(130.97, 75.81) * mm});
            skLineSegment(sketch, "E4741", {"start": v(130.97, 75.81) * mm, "end": v(130.97, 75.81) * mm});
            skLineSegment(sketch, "E4742", {"start": v(130.97, 75.81) * mm, "end": v(130.98, 75.81) * mm});
            skLineSegment(sketch, "E4743", {"start": v(130.98, 75.81) * mm, "end": v(130.99, 75.81) * mm});
            skLineSegment(sketch, "E4744", {"start": v(130.99, 75.81) * mm, "end": v(131, 75.81) * mm});
            skLineSegment(sketch, "E4745", {"start": v(131, 75.81) * mm, "end": v(131, 75.81) * mm});
            skLineSegment(sketch, "E4746", {"start": v(131, 75.81) * mm, "end": v(131.01, 75.81) * mm});
            skLineSegment(sketch, "E4747", {"start": v(131.01, 75.81) * mm, "end": v(131.02, 75.81) * mm});
            skLineSegment(sketch, "E4748", {"start": v(131.02, 75.81) * mm, "end": v(131.02, 75.81) * mm});
            skLineSegment(sketch, "E4749", {"start": v(131.02, 75.81) * mm, "end": v(131.03, 75.81) * mm});
            skLineSegment(sketch, "E4750", {"start": v(131.03, 75.81) * mm, "end": v(131.03, 75.81) * mm});
            skLineSegment(sketch, "E4751", {"start": v(131.03, 75.81) * mm, "end": v(131.04, 75.81) * mm});
            skLineSegment(sketch, "E4752", {"start": v(131.04, 75.81) * mm, "end": v(131.05, 75.81) * mm});
            skLineSegment(sketch, "E4753", {"start": v(131.05, 75.81) * mm, "end": v(131.05, 75.81) * mm});
            skLineSegment(sketch, "E4754", {"start": v(131.05, 75.81) * mm, "end": v(131.06, 75.81) * mm});
            skLineSegment(sketch, "E4755", {"start": v(131.06, 75.81) * mm, "end": v(131.07, 75.81) * mm});
            skLineSegment(sketch, "E4756", {"start": v(131.07, 75.81) * mm, "end": v(131.07, 75.81) * mm});
            skLineSegment(sketch, "E4757", {"start": v(131.07, 75.81) * mm, "end": v(131.08, 75.81) * mm});
            skLineSegment(sketch, "E4758", {"start": v(131.08, 75.81) * mm, "end": v(131.08, 75.81) * mm});
            skLineSegment(sketch, "E4759", {"start": v(131.08, 75.81) * mm, "end": v(131.09, 75.81) * mm});
            skLineSegment(sketch, "E4760", {"start": v(131.09, 75.81) * mm, "end": v(131.1, 75.81) * mm});
            skLineSegment(sketch, "E4761", {"start": v(131.1, 75.81) * mm, "end": v(131.1, 75.82) * mm});
            skLineSegment(sketch, "E4762", {"start": v(131.1, 75.82) * mm, "end": v(131.1, 75.82) * mm});
            skLineSegment(sketch, "E4763", {"start": v(131.1, 75.82) * mm, "end": v(131.11, 75.82) * mm});
            skLineSegment(sketch, "E4764", {"start": v(131.11, 75.82) * mm, "end": v(131.12, 75.82) * mm});
            skLineSegment(sketch, "E4765", {"start": v(131.12, 75.82) * mm, "end": v(131.13, 75.82) * mm});
            skLineSegment(sketch, "E4766", {"start": v(131.13, 75.82) * mm, "end": v(131.13, 75.82) * mm});
            skLineSegment(sketch, "E4767", {"start": v(131.13, 75.82) * mm, "end": v(131.14, 75.82) * mm});
            skLineSegment(sketch, "E4768", {"start": v(131.14, 75.82) * mm, "end": v(131.15, 75.82) * mm});
            skLineSegment(sketch, "E4769", {"start": v(131.15, 75.82) * mm, "end": v(131.15, 75.82) * mm});
            skLineSegment(sketch, "E4770", {"start": v(131.15, 75.82) * mm, "end": v(131.16, 75.82) * mm});
            skLineSegment(sketch, "E4771", {"start": v(131.16, 75.82) * mm, "end": v(131.16, 75.82) * mm});
            skLineSegment(sketch, "E4772", {"start": v(131.16, 75.82) * mm, "end": v(131.17, 75.82) * mm});
            skLineSegment(sketch, "E4773", {"start": v(131.17, 75.82) * mm, "end": v(131.18, 75.82) * mm});
            skLineSegment(sketch, "E4774", {"start": v(131.18, 75.82) * mm, "end": v(131.18, 75.82) * mm});
            skLineSegment(sketch, "E4775", {"start": v(131.18, 75.82) * mm, "end": v(131.19, 75.82) * mm});
            skLineSegment(sketch, "E4776", {"start": v(131.19, 75.82) * mm, "end": v(131.2, 75.83) * mm});
            skLineSegment(sketch, "E4777", {"start": v(131.2, 75.83) * mm, "end": v(131.2, 75.83) * mm});
            skLineSegment(sketch, "E4778", {"start": v(131.2, 75.83) * mm, "end": v(131.21, 75.83) * mm});
            skLineSegment(sketch, "E4779", {"start": v(131.21, 75.83) * mm, "end": v(131.22, 75.83) * mm});
            skLineSegment(sketch, "E4780", {"start": v(131.22, 75.83) * mm, "end": v(131.23, 75.83) * mm});
            skLineSegment(sketch, "E4781", {"start": v(131.23, 75.83) * mm, "end": v(131.23, 75.83) * mm});
            skLineSegment(sketch, "E4782", {"start": v(131.23, 75.83) * mm, "end": v(131.24, 75.83) * mm});
            skLineSegment(sketch, "E4783", {"start": v(131.24, 75.83) * mm, "end": v(131.24, 75.83) * mm});
            skLineSegment(sketch, "E4784", {"start": v(131.24, 75.83) * mm, "end": v(131.25, 75.84) * mm});
            skLineSegment(sketch, "E4785", {"start": v(131.25, 75.84) * mm, "end": v(131.26, 75.84) * mm});
            skLineSegment(sketch, "E4786", {"start": v(131.26, 75.84) * mm, "end": v(131.26, 75.84) * mm});
            skLineSegment(sketch, "E4787", {"start": v(131.26, 75.84) * mm, "end": v(131.27, 75.84) * mm});
            skLineSegment(sketch, "E4788", {"start": v(131.27, 75.84) * mm, "end": v(131.28, 75.84) * mm});
            skLineSegment(sketch, "E4789", {"start": v(131.28, 75.84) * mm, "end": v(131.28, 75.84) * mm});
            skLineSegment(sketch, "E4790", {"start": v(131.28, 75.84) * mm, "end": v(131.29, 75.84) * mm});
            skLineSegment(sketch, "E4791", {"start": v(131.29, 75.84) * mm, "end": v(131.3, 75.85) * mm});
            skLineSegment(sketch, "E4792", {"start": v(131.3, 75.85) * mm, "end": v(131.3, 75.85) * mm});
            skLineSegment(sketch, "E4793", {"start": v(131.3, 75.85) * mm, "end": v(131.31, 75.85) * mm});
            skLineSegment(sketch, "E4794", {"start": v(131.31, 75.85) * mm, "end": v(131.32, 75.85) * mm});
            skLineSegment(sketch, "E4795", {"start": v(131.32, 75.85) * mm, "end": v(131.33, 75.85) * mm});
            skLineSegment(sketch, "E4796", {"start": v(131.33, 75.85) * mm, "end": v(131.33, 75.86) * mm});
            skLineSegment(sketch, "E4797", {"start": v(131.33, 75.86) * mm, "end": v(131.34, 75.86) * mm});
            skLineSegment(sketch, "E4798", {"start": v(131.34, 75.86) * mm, "end": v(131.34, 75.86) * mm});
            skLineSegment(sketch, "E4799", {"start": v(131.34, 75.86) * mm, "end": v(131.35, 75.86) * mm});
            skLineSegment(sketch, "E4800", {"start": v(131.35, 75.86) * mm, "end": v(131.36, 75.86) * mm});
            skLineSegment(sketch, "E4801", {"start": v(131.36, 75.86) * mm, "end": v(131.36, 75.86) * mm});
            skLineSegment(sketch, "E4802", {"start": v(131.36, 75.86) * mm, "end": v(131.37, 75.87) * mm});
            skLineSegment(sketch, "E4803", {"start": v(131.37, 75.87) * mm, "end": v(131.38, 75.87) * mm});
            skLineSegment(sketch, "E4804", {"start": v(131.38, 75.87) * mm, "end": v(131.38, 75.87) * mm});
            skLineSegment(sketch, "E4805", {"start": v(131.38, 75.87) * mm, "end": v(131.39, 75.87) * mm});
            skLineSegment(sketch, "E4806", {"start": v(131.39, 75.87) * mm, "end": v(131.4, 75.87) * mm});
            skLineSegment(sketch, "E4807", {"start": v(131.4, 75.87) * mm, "end": v(131.4, 75.88) * mm});
            skLineSegment(sketch, "E4808", {"start": v(131.4, 75.88) * mm, "end": v(131.4, 75.88) * mm});
            skLineSegment(sketch, "E4809", {"start": v(131.4, 75.88) * mm, "end": v(131.41, 75.88) * mm});
            skLineSegment(sketch, "E4810", {"start": v(131.41, 75.88) * mm, "end": v(131.42, 75.88) * mm});
            skLineSegment(sketch, "E4811", {"start": v(131.42, 75.88) * mm, "end": v(131.43, 75.89) * mm});
            skLineSegment(sketch, "E4812", {"start": v(131.43, 75.89) * mm, "end": v(131.43, 75.89) * mm});
            skLineSegment(sketch, "E4813", {"start": v(131.43, 75.89) * mm, "end": v(131.44, 75.9) * mm});
            skLineSegment(sketch, "E4814", {"start": v(131.44, 75.9) * mm, "end": v(131.45, 75.9) * mm});
            skLineSegment(sketch, "E4815", {"start": v(131.45, 75.9) * mm, "end": v(131.45, 75.9) * mm});
            skLineSegment(sketch, "E4816", {"start": v(131.45, 75.9) * mm, "end": v(131.46, 75.9) * mm});
            skLineSegment(sketch, "E4817", {"start": v(131.46, 75.9) * mm, "end": v(131.47, 75.9) * mm});
            skLineSegment(sketch, "E4818", {"start": v(131.47, 75.9) * mm, "end": v(131.48, 75.9) * mm});
            skLineSegment(sketch, "E4819", {"start": v(131.48, 75.9) * mm, "end": v(131.48, 75.9) * mm});
            skLineSegment(sketch, "E4820", {"start": v(131.48, 75.9) * mm, "end": v(131.5, 75.91) * mm});
            skLineSegment(sketch, "E4821", {"start": v(131.5, 75.91) * mm, "end": v(131.5, 75.91) * mm});
            skLineSegment(sketch, "E4822", {"start": v(131.5, 75.91) * mm, "end": v(131.5, 75.92) * mm});
            skLineSegment(sketch, "E4823", {"start": v(131.5, 75.92) * mm, "end": v(131.51, 75.92) * mm});
            skLineSegment(sketch, "E4824", {"start": v(131.51, 75.92) * mm, "end": v(131.52, 75.92) * mm});
            skLineSegment(sketch, "E4825", {"start": v(131.52, 75.92) * mm, "end": v(131.53, 75.92) * mm});
            skLineSegment(sketch, "E4826", {"start": v(131.53, 75.92) * mm, "end": v(131.54, 75.93) * mm});
            skLineSegment(sketch, "E4827", {"start": v(131.54, 75.93) * mm, "end": v(131.54, 75.93) * mm});
            skLineSegment(sketch, "E4828", {"start": v(131.54, 75.93) * mm, "end": v(131.55, 75.93) * mm});
            skLineSegment(sketch, "E4829", {"start": v(131.55, 75.93) * mm, "end": v(131.56, 75.93) * mm});
            skLineSegment(sketch, "E4830", {"start": v(131.56, 75.93) * mm, "end": v(131.57, 75.94) * mm});
            skLineSegment(sketch, "E4831", {"start": v(131.57, 75.94) * mm, "end": v(131.57, 75.94) * mm});
            skLineSegment(sketch, "E4832", {"start": v(131.57, 75.94) * mm, "end": v(131.58, 75.94) * mm});
            skLineSegment(sketch, "E4833", {"start": v(131.58, 75.94) * mm, "end": v(131.59, 75.94) * mm});
            skLineSegment(sketch, "E4834", {"start": v(131.59, 75.94) * mm, "end": v(131.6, 75.95) * mm});
            skLineSegment(sketch, "E4835", {"start": v(131.6, 75.95) * mm, "end": v(131.6, 75.95) * mm});
            skLineSegment(sketch, "E4836", {"start": v(131.6, 75.95) * mm, "end": v(131.61, 75.95) * mm});
            skLineSegment(sketch, "E4837", {"start": v(131.61, 75.95) * mm, "end": v(131.62, 75.96) * mm});
            skLineSegment(sketch, "E4838", {"start": v(131.62, 75.96) * mm, "end": v(131.63, 75.96) * mm});
            skLineSegment(sketch, "E4839", {"start": v(131.63, 75.96) * mm, "end": v(131.63, 75.96) * mm});
            skLineSegment(sketch, "E4840", {"start": v(131.63, 75.96) * mm, "end": v(131.64, 75.96) * mm});
            skLineSegment(sketch, "E4841", {"start": v(131.64, 75.96) * mm, "end": v(131.65, 75.96) * mm});
            skLineSegment(sketch, "E4842", {"start": v(131.65, 75.96) * mm, "end": v(131.65, 75.97) * mm});
            skLineSegment(sketch, "E4843", {"start": v(131.65, 75.97) * mm, "end": v(131.66, 75.97) * mm});
            skLineSegment(sketch, "E4844", {"start": v(131.66, 75.97) * mm, "end": v(131.67, 75.97) * mm});
            skLineSegment(sketch, "E4845", {"start": v(131.67, 75.97) * mm, "end": v(131.67, 75.97) * mm});
            skLineSegment(sketch, "E4846", {"start": v(131.67, 75.97) * mm, "end": v(131.68, 75.97) * mm});
            skLineSegment(sketch, "E4847", {"start": v(131.68, 75.97) * mm, "end": v(131.68, 75.97) * mm});
            skLineSegment(sketch, "E4848", {"start": v(131.68, 75.97) * mm, "end": v(131.7, 75.98) * mm});
            skLineSegment(sketch, "E4849", {"start": v(131.7, 75.98) * mm, "end": v(131.7, 75.98) * mm});
            skLineSegment(sketch, "E4850", {"start": v(131.7, 75.98) * mm, "end": v(131.71, 75.98) * mm});
            skLineSegment(sketch, "E4851", {"start": v(131.71, 75.98) * mm, "end": v(131.72, 75.98) * mm});
            skLineSegment(sketch, "E4852", {"start": v(131.72, 75.98) * mm, "end": v(131.73, 75.99) * mm});
            skLineSegment(sketch, "E4853", {"start": v(131.73, 75.99) * mm, "end": v(131.73, 75.99) * mm});
            skLineSegment(sketch, "E4854", {"start": v(131.73, 75.99) * mm, "end": v(131.74, 75.99) * mm});
            skLineSegment(sketch, "E4855", {"start": v(131.74, 75.99) * mm, "end": v(131.74, 75.99) * mm});
            skLineSegment(sketch, "E4856", {"start": v(131.74, 75.99) * mm, "end": v(131.75, 76) * mm});
            skLineSegment(sketch, "E4857", {"start": v(131.75, 76) * mm, "end": v(131.76, 76) * mm});
            skLineSegment(sketch, "E4858", {"start": v(131.76, 76) * mm, "end": v(131.76, 76) * mm});
            skLineSegment(sketch, "E4859", {"start": v(131.76, 76) * mm, "end": v(131.77, 76) * mm});
            skLineSegment(sketch, "E4860", {"start": v(131.77, 76) * mm, "end": v(131.77, 76) * mm});
            skLineSegment(sketch, "E4861", {"start": v(131.77, 76) * mm, "end": v(131.78, 76) * mm});
            skLineSegment(sketch, "E4862", {"start": v(131.78, 76) * mm, "end": v(131.78, 76) * mm});
            skLineSegment(sketch, "E4863", {"start": v(131.78, 76) * mm, "end": v(131.79, 76) * mm});
            skLineSegment(sketch, "E4864", {"start": v(131.79, 76) * mm, "end": v(131.8, 76) * mm});
            skLineSegment(sketch, "E4865", {"start": v(131.8, 76) * mm, "end": v(131.8, 76) * mm});
            skLineSegment(sketch, "E4866", {"start": v(131.8, 76) * mm, "end": v(131.81, 76) * mm});
            skLineSegment(sketch, "E4867", {"start": v(131.81, 76) * mm, "end": v(131.82, 76) * mm});
            skLineSegment(sketch, "E4868", {"start": v(131.82, 76) * mm, "end": v(131.82, 76) * mm});
            skLineSegment(sketch, "E4869", {"start": v(131.82, 76) * mm, "end": v(131.83, 76) * mm});
            skLineSegment(sketch, "E4870", {"start": v(131.83, 76) * mm, "end": v(131.83, 76) * mm});
            skLineSegment(sketch, "E4871", {"start": v(131.83, 76) * mm, "end": v(131.84, 76) * mm});
            skLineSegment(sketch, "E4872", {"start": v(131.84, 76) * mm, "end": v(131.84, 76) * mm});
            skLineSegment(sketch, "E4873", {"start": v(131.84, 76) * mm, "end": v(131.85, 76) * mm});
            skLineSegment(sketch, "E4874", {"start": v(131.85, 76) * mm, "end": v(131.85, 76) * mm});
            skLineSegment(sketch, "E4875", {"start": v(131.85, 76) * mm, "end": v(131.86, 76) * mm});
            skLineSegment(sketch, "E4876", {"start": v(131.86, 76) * mm, "end": v(131.86, 76) * mm});
            skLineSegment(sketch, "E4877", {"start": v(131.86, 76) * mm, "end": v(131.87, 76) * mm});
            skLineSegment(sketch, "E4878", {"start": v(131.87, 76) * mm, "end": v(131.87, 76.01) * mm});
            skLineSegment(sketch, "E4879", {"start": v(131.87, 76.01) * mm, "end": v(131.88, 76.01) * mm});
            skLineSegment(sketch, "E4880", {"start": v(131.88, 76.01) * mm, "end": v(131.88, 76.01) * mm});
            skLineSegment(sketch, "E4881", {"start": v(131.88, 76.01) * mm, "end": v(131.89, 76.01) * mm});
            skLineSegment(sketch, "E4882", {"start": v(131.89, 76.01) * mm, "end": v(131.89, 76.01) * mm});
            skLineSegment(sketch, "E4883", {"start": v(131.89, 76.01) * mm, "end": v(131.9, 76.01) * mm});
            skLineSegment(sketch, "E4884", {"start": v(131.9, 76.01) * mm, "end": v(131.9, 76.01) * mm});
            skLineSegment(sketch, "E4885", {"start": v(131.9, 76.01) * mm, "end": v(131.91, 76.01) * mm});
            skLineSegment(sketch, "E4886", {"start": v(131.91, 76.01) * mm, "end": v(131.91, 76.01) * mm});
            skLineSegment(sketch, "E4887", {"start": v(131.91, 76.01) * mm, "end": v(131.92, 76.01) * mm});
            skLineSegment(sketch, "E4888", {"start": v(131.92, 76.01) * mm, "end": v(131.92, 76.01) * mm});
            skLineSegment(sketch, "E4889", {"start": v(131.92, 76.01) * mm, "end": v(131.93, 76.01) * mm});
            skLineSegment(sketch, "E4890", {"start": v(131.93, 76.01) * mm, "end": v(131.93, 76.01) * mm});
            skLineSegment(sketch, "E4891", {"start": v(131.93, 76.01) * mm, "end": v(131.94, 76.01) * mm});
            skLineSegment(sketch, "E4892", {"start": v(131.94, 76.01) * mm, "end": v(131.94, 76) * mm});
            skLineSegment(sketch, "E4893", {"start": v(131.94, 76) * mm, "end": v(131.95, 76) * mm});
            skLineSegment(sketch, "E4894", {"start": v(131.95, 76) * mm, "end": v(131.95, 76) * mm});
            skLineSegment(sketch, "E4895", {"start": v(131.95, 76) * mm, "end": v(131.96, 76) * mm});
            skLineSegment(sketch, "E4896", {"start": v(131.96, 76) * mm, "end": v(131.96, 76) * mm});
            skLineSegment(sketch, "E4897", {"start": v(131.96, 76) * mm, "end": v(131.97, 76) * mm});
            skLineSegment(sketch, "E4898", {"start": v(131.97, 76) * mm, "end": v(131.97, 76) * mm});
            skLineSegment(sketch, "E4899", {"start": v(131.97, 76) * mm, "end": v(131.98, 76) * mm});
            skLineSegment(sketch, "E4900", {"start": v(131.98, 76) * mm, "end": v(131.98, 76) * mm});
            skLineSegment(sketch, "E4901", {"start": v(131.98, 76) * mm, "end": v(131.99, 76) * mm});
            skLineSegment(sketch, "E4902", {"start": v(131.99, 76) * mm, "end": v(131.99, 76) * mm});
            skLineSegment(sketch, "E4903", {"start": v(131.99, 76) * mm, "end": v(132, 76) * mm});
            skLineSegment(sketch, "E4904", {"start": v(132, 76) * mm, "end": v(132, 76) * mm});
            skLineSegment(sketch, "E4905", {"start": v(132, 76) * mm, "end": v(132.01, 76) * mm});
            skLineSegment(sketch, "E4906", {"start": v(132.01, 76) * mm, "end": v(132.02, 75.99) * mm});
            skLineSegment(sketch, "E4907", {"start": v(132.02, 75.99) * mm, "end": v(132.02, 75.99) * mm});
            skLineSegment(sketch, "E4908", {"start": v(132.02, 75.99) * mm, "end": v(132.03, 75.98) * mm});
            skLineSegment(sketch, "E4909", {"start": v(132.03, 75.98) * mm, "end": v(132.03, 75.98) * mm});
            skLineSegment(sketch, "E4910", {"start": v(132.03, 75.98) * mm, "end": v(132.04, 75.98) * mm});
            skLineSegment(sketch, "E4911", {"start": v(132.04, 75.98) * mm, "end": v(132.04, 75.98) * mm});
            skLineSegment(sketch, "E4912", {"start": v(132.04, 75.98) * mm, "end": v(132.04, 75.97) * mm});
            skLineSegment(sketch, "E4913", {"start": v(132.04, 75.97) * mm, "end": v(132.04, 75.97) * mm});
            skLineSegment(sketch, "E4914", {"start": v(132.04, 75.97) * mm, "end": v(132.05, 75.97) * mm});
            skLineSegment(sketch, "E4915", {"start": v(132.05, 75.97) * mm, "end": v(132.05, 75.97) * mm});
            skLineSegment(sketch, "E4916", {"start": v(132.05, 75.97) * mm, "end": v(132.05, 75.96) * mm});
            skLineSegment(sketch, "E4917", {"start": v(132.05, 75.96) * mm, "end": v(132.05, 75.96) * mm});
            skLineSegment(sketch, "E4918", {"start": v(132.05, 75.96) * mm, "end": v(132.06, 75.96) * mm});
            skLineSegment(sketch, "E4919", {"start": v(132.06, 75.96) * mm, "end": v(132.06, 75.96) * mm});
            skLineSegment(sketch, "E4920", {"start": v(132.06, 75.96) * mm, "end": v(132.06, 75.95) * mm});
            skLineSegment(sketch, "E4921", {"start": v(132.06, 75.95) * mm, "end": v(132.06, 75.95) * mm});
            skLineSegment(sketch, "E4922", {"start": v(132.06, 75.95) * mm, "end": v(132.07, 75.95) * mm});
            skLineSegment(sketch, "E4923", {"start": v(132.07, 75.95) * mm, "end": v(132.07, 75.94) * mm});
            skLineSegment(sketch, "E4924", {"start": v(132.07, 75.94) * mm, "end": v(132.07, 75.94) * mm});
            skLineSegment(sketch, "E4925", {"start": v(132.07, 75.94) * mm, "end": v(132.07, 75.93) * mm});
            skLineSegment(sketch, "E4926", {"start": v(132.07, 75.93) * mm, "end": v(132.07, 75.93) * mm});
            skLineSegment(sketch, "E4927", {"start": v(132.07, 75.93) * mm, "end": v(132.08, 75.93) * mm});
            skLineSegment(sketch, "E4928", {"start": v(132.08, 75.93) * mm, "end": v(132.08, 75.93) * mm});
            skLineSegment(sketch, "E4929", {"start": v(132.08, 75.93) * mm, "end": v(132.08, 75.92) * mm});
            skLineSegment(sketch, "E4930", {"start": v(132.08, 75.92) * mm, "end": v(132.08, 75.92) * mm});
            skLineSegment(sketch, "E4931", {"start": v(132.08, 75.92) * mm, "end": v(132.08, 75.91) * mm});
            skLineSegment(sketch, "E4932", {"start": v(132.08, 75.91) * mm, "end": v(132.08, 75.91) * mm});
            skLineSegment(sketch, "E4933", {"start": v(132.08, 75.91) * mm, "end": v(132.08, 75.9) * mm});
            skLineSegment(sketch, "E4934", {"start": v(132.08, 75.9) * mm, "end": v(132.09, 75.9) * mm});
            skLineSegment(sketch, "E4935", {"start": v(132.09, 75.9) * mm, "end": v(132.09, 75.9) * mm});
            skLineSegment(sketch, "E4936", {"start": v(132.09, 75.9) * mm, "end": v(132.1, 75.89) * mm});
            skLineSegment(sketch, "E4937", {"start": v(132.1, 75.89) * mm, "end": v(132.1, 75.89) * mm});
            skLineSegment(sketch, "E4938", {"start": v(132.1, 75.89) * mm, "end": v(132.1, 75.88) * mm});
            skLineSegment(sketch, "E4939", {"start": v(132.1, 75.88) * mm, "end": v(132.1, 75.88) * mm});
            skLineSegment(sketch, "E4940", {"start": v(132.1, 75.88) * mm, "end": v(132.1, 75.87) * mm});
            skLineSegment(sketch, "E4941", {"start": v(132.1, 75.87) * mm, "end": v(132.1, 75.87) * mm});
            skLineSegment(sketch, "E4942", {"start": v(132.1, 75.87) * mm, "end": v(132.1, 75.86) * mm});
            skLineSegment(sketch, "E4943", {"start": v(132.1, 75.86) * mm, "end": v(132.1, 75.86) * mm});
            skLineSegment(sketch, "E4944", {"start": v(132.1, 75.86) * mm, "end": v(132.1, 75.85) * mm});
            skLineSegment(sketch, "E4945", {"start": v(132.1, 75.85) * mm, "end": v(132.1, 75.85) * mm});
            skLineSegment(sketch, "E4946", {"start": v(132.1, 75.85) * mm, "end": v(132.1, 75.84) * mm});
            skLineSegment(sketch, "E4947", {"start": v(132.1, 75.84) * mm, "end": v(132.1, 75.84) * mm});
            skLineSegment(sketch, "E4948", {"start": v(132.1, 75.84) * mm, "end": v(132.1, 75.83) * mm});
            skLineSegment(sketch, "E4949", {"start": v(132.1, 75.83) * mm, "end": v(132.1, 75.83) * mm});
            skLineSegment(sketch, "E4950", {"start": v(132.1, 75.83) * mm, "end": v(132.1, 75.82) * mm});
            skLineSegment(sketch, "E4951", {"start": v(132.1, 75.82) * mm, "end": v(132.1, 75.82) * mm});
            skLineSegment(sketch, "E4952", {"start": v(132.1, 75.82) * mm, "end": v(132.1, 75.81) * mm});
            skLineSegment(sketch, "E4953", {"start": v(132.1, 75.81) * mm, "end": v(132.1, 75.8) * mm});
            skLineSegment(sketch, "E4954", {"start": v(132.1, 75.8) * mm, "end": v(132.1, 75.8) * mm});
            skLineSegment(sketch, "E4955", {"start": v(132.1, 75.8) * mm, "end": v(132.1, 75.79) * mm});
            skLineSegment(sketch, "E4956", {"start": v(132.1, 75.79) * mm, "end": v(132.1, 75.78) * mm});
            skLineSegment(sketch, "E4957", {"start": v(132.1, 75.78) * mm, "end": v(132.1, 75.78) * mm});
            skLineSegment(sketch, "E4958", {"start": v(132.1, 75.78) * mm, "end": v(132.1, 75.77) * mm});
            skLineSegment(sketch, "E4959", {"start": v(132.1, 75.77) * mm, "end": v(132.1, 75.77) * mm});
            skLineSegment(sketch, "E4960", {"start": v(132.1, 75.77) * mm, "end": v(132.1, 75.76) * mm});
            skLineSegment(sketch, "E4961", {"start": v(132.1, 75.76) * mm, "end": v(132.1, 75.76) * mm});
            skLineSegment(sketch, "E4962", {"start": v(132.1, 75.76) * mm, "end": v(132.1, 75.75) * mm});
            skLineSegment(sketch, "E4963", {"start": v(132.1, 75.75) * mm, "end": v(132.1, 75.75) * mm});
            skLineSegment(sketch, "E4964", {"start": v(132.1, 75.75) * mm, "end": v(132.1, 75.74) * mm});
            skLineSegment(sketch, "E4965", {"start": v(132.1, 75.74) * mm, "end": v(132.1, 75.74) * mm});
            skLineSegment(sketch, "E4966", {"start": v(132.1, 75.74) * mm, "end": v(132.1, 75.73) * mm});
            skLineSegment(sketch, "E4967", {"start": v(132.1, 75.73) * mm, "end": v(132.1, 75.73) * mm});
            skLineSegment(sketch, "E4968", {"start": v(132.1, 75.73) * mm, "end": v(132.1, 75.72) * mm});
            skLineSegment(sketch, "E4969", {"start": v(132.1, 75.72) * mm, "end": v(132.09, 75.72) * mm});
            skLineSegment(sketch, "E4970", {"start": v(132.09, 75.72) * mm, "end": v(132.09, 75.71) * mm});
            skLineSegment(sketch, "E4971", {"start": v(132.09, 75.71) * mm, "end": v(132.09, 75.7) * mm});
            skLineSegment(sketch, "E4972", {"start": v(132.09, 75.7) * mm, "end": v(132.09, 75.7) * mm});
            skLineSegment(sketch, "E4973", {"start": v(132.09, 75.7) * mm, "end": v(132.08, 75.7) * mm});
            skLineSegment(sketch, "E4974", {"start": v(132.08, 75.7) * mm, "end": v(132.08, 75.69) * mm});
            skLineSegment(sketch, "E4975", {"start": v(132.08, 75.69) * mm, "end": v(132.08, 75.68) * mm});
            skLineSegment(sketch, "E4976", {"start": v(132.08, 75.68) * mm, "end": v(132.08, 75.67) * mm});
            skLineSegment(sketch, "E4977", {"start": v(132.08, 75.67) * mm, "end": v(132.08, 75.67) * mm});
            skLineSegment(sketch, "E4978", {"start": v(132.08, 75.67) * mm, "end": v(132.08, 75.66) * mm});
            skLineSegment(sketch, "E4979", {"start": v(132.08, 75.66) * mm, "end": v(132.08, 75.66) * mm});
            skLineSegment(sketch, "E4980", {"start": v(132.08, 75.66) * mm, "end": v(132.08, 75.65) * mm});
            skLineSegment(sketch, "E4981", {"start": v(132.08, 75.65) * mm, "end": v(132.08, 75.65) * mm});
            skLineSegment(sketch, "E4982", {"start": v(132.08, 75.65) * mm, "end": v(132.07, 75.64) * mm});
            skLineSegment(sketch, "E4983", {"start": v(132.07, 75.64) * mm, "end": v(132.07, 75.63) * mm});
            skLineSegment(sketch, "E4984", {"start": v(132.07, 75.63) * mm, "end": v(132.07, 75.63) * mm});
            skLineSegment(sketch, "E4985", {"start": v(132.07, 75.63) * mm, "end": v(132.07, 75.62) * mm});
            skLineSegment(sketch, "E4986", {"start": v(132.07, 75.62) * mm, "end": v(132.07, 75.62) * mm});
            skLineSegment(sketch, "E4987", {"start": v(132.07, 75.62) * mm, "end": v(132.07, 75.6) * mm});
            skLineSegment(sketch, "E4988", {"start": v(132.07, 75.6) * mm, "end": v(132.06, 75.6) * mm});
            skLineSegment(sketch, "E4989", {"start": v(132.06, 75.6) * mm, "end": v(132.06, 75.6) * mm});
            skLineSegment(sketch, "E4990", {"start": v(132.06, 75.6) * mm, "end": v(132.06, 75.58) * mm});
            skLineSegment(sketch, "E4991", {"start": v(132.06, 75.58) * mm, "end": v(132.06, 75.58) * mm});
            skLineSegment(sketch, "E4992", {"start": v(132.06, 75.58) * mm, "end": v(132.06, 75.57) * mm});
            skLineSegment(sketch, "E4993", {"start": v(132.06, 75.57) * mm, "end": v(132.05, 75.57) * mm});
            skLineSegment(sketch, "E4994", {"start": v(132.05, 75.57) * mm, "end": v(132.05, 75.56) * mm});
            skLineSegment(sketch, "E4995", {"start": v(132.05, 75.56) * mm, "end": v(132.05, 75.55) * mm});
            skLineSegment(sketch, "E4996", {"start": v(132.05, 75.55) * mm, "end": v(132.05, 75.55) * mm});
            skLineSegment(sketch, "E4997", {"start": v(132.05, 75.55) * mm, "end": v(132.05, 75.54) * mm});
            skLineSegment(sketch, "E4998", {"start": v(132.05, 75.54) * mm, "end": v(132.04, 75.53) * mm});
            skLineSegment(sketch, "E4999", {"start": v(132.04, 75.53) * mm, "end": v(132.04, 75.52) * mm});
            skLineSegment(sketch, "E5000", {"start": v(132.04, 75.52) * mm, "end": v(132.04, 75.52) * mm});
            skLineSegment(sketch, "E5001", {"start": v(132.04, 75.52) * mm, "end": v(132.04, 75.51) * mm});
            skLineSegment(sketch, "E5002", {"start": v(132.04, 75.51) * mm, "end": v(132.04, 75.5) * mm});
            skLineSegment(sketch, "E5003", {"start": v(132.04, 75.5) * mm, "end": v(132.03, 75.5) * mm});
            skLineSegment(sketch, "E5004", {"start": v(132.03, 75.5) * mm, "end": v(132.03, 75.5) * mm});
            skLineSegment(sketch, "E5005", {"start": v(132.03, 75.5) * mm, "end": v(132.03, 75.48) * mm});
            skLineSegment(sketch, "E5006", {"start": v(132.03, 75.48) * mm, "end": v(132.03, 75.48) * mm});
            skLineSegment(sketch, "E5007", {"start": v(132.03, 75.48) * mm, "end": v(132.02, 75.47) * mm});
            skLineSegment(sketch, "E5008", {"start": v(132.02, 75.47) * mm, "end": v(132.02, 75.46) * mm});
            skLineSegment(sketch, "E5009", {"start": v(132.02, 75.46) * mm, "end": v(132.02, 75.45) * mm});
            skLineSegment(sketch, "E5010", {"start": v(132.02, 75.45) * mm, "end": v(132.02, 75.45) * mm});
            skLineSegment(sketch, "E5011", {"start": v(132.02, 75.45) * mm, "end": v(132.01, 75.44) * mm});
            skLineSegment(sketch, "E5012", {"start": v(132.01, 75.44) * mm, "end": v(132.01, 75.43) * mm});
            skLineSegment(sketch, "E5013", {"start": v(132.01, 75.43) * mm, "end": v(132, 75.42) * mm});
            skLineSegment(sketch, "E5014", {"start": v(132, 75.42) * mm, "end": v(132, 75.42) * mm});
            skLineSegment(sketch, "E5015", {"start": v(132, 75.42) * mm, "end": v(132, 75.4) * mm});
            skLineSegment(sketch, "E5016", {"start": v(132, 75.4) * mm, "end": v(132, 75.4) * mm});
            skLineSegment(sketch, "E5017", {"start": v(132, 75.4) * mm, "end": v(132, 75.39) * mm});
            skLineSegment(sketch, "E5018", {"start": v(132, 75.39) * mm, "end": v(132, 75.38) * mm});
            skLineSegment(sketch, "E5019", {"start": v(132, 75.38) * mm, "end": v(132, 75.37) * mm});
            skLineSegment(sketch, "E5020", {"start": v(132, 75.37) * mm, "end": v(131.99, 75.36) * mm});
            skLineSegment(sketch, "E5021", {"start": v(131.99, 75.36) * mm, "end": v(131.98, 75.35) * mm});
            skLineSegment(sketch, "E5022", {"start": v(131.98, 75.35) * mm, "end": v(131.98, 75.35) * mm});
            skLineSegment(sketch, "E5023", {"start": v(131.98, 75.35) * mm, "end": v(131.98, 75.34) * mm});
            skLineSegment(sketch, "E5024", {"start": v(131.98, 75.34) * mm, "end": v(131.98, 75.33) * mm});
            skLineSegment(sketch, "E5025", {"start": v(131.98, 75.33) * mm, "end": v(131.97, 75.32) * mm});
            skLineSegment(sketch, "E5026", {"start": v(131.97, 75.32) * mm, "end": v(131.97, 75.31) * mm});
            skLineSegment(sketch, "E5027", {"start": v(131.97, 75.31) * mm, "end": v(131.97, 75.3) * mm});
            skLineSegment(sketch, "E5028", {"start": v(131.97, 75.3) * mm, "end": v(131.96, 75.3) * mm});
            skLineSegment(sketch, "E5029", {"start": v(131.96, 75.3) * mm, "end": v(131.96, 75.29) * mm});
            skLineSegment(sketch, "E5030", {"start": v(131.96, 75.29) * mm, "end": v(131.96, 75.28) * mm});
            skLineSegment(sketch, "E5031", {"start": v(131.96, 75.28) * mm, "end": v(131.95, 75.26) * mm});
            skLineSegment(sketch, "E5032", {"start": v(131.95, 75.26) * mm, "end": v(131.95, 75.25) * mm});
            skLineSegment(sketch, "E5033", {"start": v(131.95, 75.25) * mm, "end": v(131.94, 75.24) * mm});
            skLineSegment(sketch, "E5034", {"start": v(131.94, 75.24) * mm, "end": v(131.94, 75.23) * mm});
            skLineSegment(sketch, "E5035", {"start": v(131.94, 75.23) * mm, "end": v(131.93, 75.21) * mm});
            skLineSegment(sketch, "E5036", {"start": v(131.93, 75.21) * mm, "end": v(131.93, 75.2) * mm});
            skLineSegment(sketch, "E5037", {"start": v(131.93, 75.2) * mm, "end": v(131.92, 75.19) * mm});
            skLineSegment(sketch, "E5038", {"start": v(131.92, 75.19) * mm, "end": v(131.92, 75.18) * mm});
            skLineSegment(sketch, "E5039", {"start": v(131.92, 75.18) * mm, "end": v(131.91, 75.16) * mm});
            skLineSegment(sketch, "E5040", {"start": v(131.91, 75.16) * mm, "end": v(131.9, 75.15) * mm});
            skLineSegment(sketch, "E5041", {"start": v(131.9, 75.15) * mm, "end": v(131.9, 75.14) * mm});
            skLineSegment(sketch, "E5042", {"start": v(131.9, 75.14) * mm, "end": v(131.9, 75.13) * mm});
            skLineSegment(sketch, "E5043", {"start": v(131.9, 75.13) * mm, "end": v(131.9, 75.11) * mm});
            skLineSegment(sketch, "E5044", {"start": v(131.9, 75.11) * mm, "end": v(131.9, 75.1) * mm});
            skLineSegment(sketch, "E5045", {"start": v(131.9, 75.1) * mm, "end": v(131.89, 75.09) * mm});
            skLineSegment(sketch, "E5046", {"start": v(131.89, 75.09) * mm, "end": v(131.88, 75.08) * mm});
            skLineSegment(sketch, "E5047", {"start": v(131.88, 75.08) * mm, "end": v(131.88, 75.06) * mm});
            skLineSegment(sketch, "E5048", {"start": v(131.88, 75.06) * mm, "end": v(131.87, 75.04) * mm});
            skLineSegment(sketch, "E5049", {"start": v(131.87, 75.04) * mm, "end": v(131.86, 75.01) * mm});
            skLineSegment(sketch, "E5050", {"start": v(131.86, 75.01) * mm, "end": v(131.85, 74.99) * mm});
            skLineSegment(sketch, "E5051", {"start": v(131.85, 74.99) * mm, "end": v(131.84, 74.96) * mm});
            skLineSegment(sketch, "E5052", {"start": v(131.84, 74.96) * mm, "end": v(131.84, 74.94) * mm});
            skLineSegment(sketch, "E5053", {"start": v(131.84, 74.94) * mm, "end": v(131.83, 74.9) * mm});
            skLineSegment(sketch, "E5054", {"start": v(131.83, 74.9) * mm, "end": v(131.82, 74.88) * mm});
            skLineSegment(sketch, "E5055", {"start": v(131.82, 74.88) * mm, "end": v(131.81, 74.86) * mm});
            skLineSegment(sketch, "E5056", {"start": v(131.81, 74.86) * mm, "end": v(131.8, 74.83) * mm});
            skLineSegment(sketch, "E5057", {"start": v(131.8, 74.83) * mm, "end": v(131.8, 74.8) * mm});
            skLineSegment(sketch, "E5058", {"start": v(131.8, 74.8) * mm, "end": v(131.8, 74.8) * mm});
            skLineSegment(sketch, "E5059", {"start": v(131.8, 74.8) * mm, "end": v(131.79, 74.78) * mm});
            skLineSegment(sketch, "E5060", {"start": v(131.79, 74.78) * mm, "end": v(131.78, 74.77) * mm});
            skLineSegment(sketch, "E5061", {"start": v(131.78, 74.77) * mm, "end": v(131.78, 74.75) * mm});
            skLineSegment(sketch, "E5062", {"start": v(131.78, 74.75) * mm, "end": v(131.78, 74.74) * mm});
            skLineSegment(sketch, "E5063", {"start": v(131.78, 74.74) * mm, "end": v(131.77, 74.73) * mm});
            skLineSegment(sketch, "E5064", {"start": v(131.77, 74.73) * mm, "end": v(131.77, 74.72) * mm});
            skLineSegment(sketch, "E5065", {"start": v(131.77, 74.72) * mm, "end": v(131.77, 74.7) * mm});
            skLineSegment(sketch, "E5066", {"start": v(131.77, 74.7) * mm, "end": v(131.76, 74.7) * mm});
            skLineSegment(sketch, "E5067", {"start": v(131.76, 74.7) * mm, "end": v(131.76, 74.68) * mm});
            skLineSegment(sketch, "E5068", {"start": v(131.76, 74.68) * mm, "end": v(131.75, 74.67) * mm});
            skLineSegment(sketch, "E5069", {"start": v(131.75, 74.67) * mm, "end": v(131.75, 74.65) * mm});
            skLineSegment(sketch, "E5070", {"start": v(131.75, 74.65) * mm, "end": v(131.75, 74.64) * mm});
            skLineSegment(sketch, "E5071", {"start": v(131.75, 74.64) * mm, "end": v(131.74, 74.63) * mm});
            skLineSegment(sketch, "E5072", {"start": v(131.74, 74.63) * mm, "end": v(131.74, 74.61) * mm});
            skLineSegment(sketch, "E5073", {"start": v(131.74, 74.61) * mm, "end": v(131.74, 74.6) * mm});
            skLineSegment(sketch, "E5074", {"start": v(131.74, 74.6) * mm, "end": v(131.73, 74.59) * mm});
            skLineSegment(sketch, "E5075", {"start": v(131.73, 74.59) * mm, "end": v(131.73, 74.58) * mm});
            skLineSegment(sketch, "E5076", {"start": v(131.73, 74.58) * mm, "end": v(131.73, 74.56) * mm});
            skLineSegment(sketch, "E5077", {"start": v(131.73, 74.56) * mm, "end": v(131.72, 74.55) * mm});
            skLineSegment(sketch, "E5078", {"start": v(131.72, 74.55) * mm, "end": v(131.72, 74.54) * mm});
            skLineSegment(sketch, "E5079", {"start": v(131.72, 74.54) * mm, "end": v(131.72, 74.53) * mm});
            skLineSegment(sketch, "E5080", {"start": v(131.72, 74.53) * mm, "end": v(131.71, 74.51) * mm});
            skLineSegment(sketch, "E5081", {"start": v(131.71, 74.51) * mm, "end": v(131.71, 74.5) * mm});
            skLineSegment(sketch, "E5082", {"start": v(131.71, 74.5) * mm, "end": v(131.7, 74.5) * mm});
            skLineSegment(sketch, "E5083", {"start": v(131.7, 74.5) * mm, "end": v(131.7, 74.48) * mm});
            skLineSegment(sketch, "E5084", {"start": v(131.7, 74.48) * mm, "end": v(131.7, 74.47) * mm});
            skLineSegment(sketch, "E5085", {"start": v(131.7, 74.47) * mm, "end": v(131.7, 74.45) * mm});
            skLineSegment(sketch, "E5086", {"start": v(131.7, 74.45) * mm, "end": v(131.7, 74.44) * mm});
            skLineSegment(sketch, "E5087", {"start": v(131.7, 74.44) * mm, "end": v(131.7, 74.43) * mm});
            skLineSegment(sketch, "E5088", {"start": v(131.7, 74.43) * mm, "end": v(131.69, 74.42) * mm});
            skLineSegment(sketch, "E5089", {"start": v(131.69, 74.42) * mm, "end": v(131.69, 74.4) * mm});
            skLineSegment(sketch, "E5090", {"start": v(131.69, 74.4) * mm, "end": v(131.68, 74.4) * mm});
            skLineSegment(sketch, "E5091", {"start": v(131.68, 74.4) * mm, "end": v(131.68, 74.38) * mm});
            skLineSegment(sketch, "E5092", {"start": v(131.68, 74.38) * mm, "end": v(131.68, 74.37) * mm});
            skLineSegment(sketch, "E5093", {"start": v(131.68, 74.37) * mm, "end": v(131.68, 74.36) * mm});
            skLineSegment(sketch, "E5094", {"start": v(131.68, 74.36) * mm, "end": v(131.67, 74.35) * mm});
            skLineSegment(sketch, "E5095", {"start": v(131.67, 74.35) * mm, "end": v(131.67, 74.34) * mm});
            skLineSegment(sketch, "E5096", {"start": v(131.67, 74.34) * mm, "end": v(131.67, 74.32) * mm});
            skLineSegment(sketch, "E5097", {"start": v(131.67, 74.32) * mm, "end": v(131.67, 74.31) * mm});
            skLineSegment(sketch, "E5098", {"start": v(131.67, 74.31) * mm, "end": v(131.66, 74.3) * mm});
            skLineSegment(sketch, "E5099", {"start": v(131.66, 74.3) * mm, "end": v(131.66, 74.29) * mm});
            skLineSegment(sketch, "E5100", {"start": v(131.66, 74.29) * mm, "end": v(131.66, 74.28) * mm});
            skLineSegment(sketch, "E5101", {"start": v(131.66, 74.28) * mm, "end": v(131.66, 74.27) * mm});
            skLineSegment(sketch, "E5102", {"start": v(131.66, 74.27) * mm, "end": v(131.65, 74.26) * mm});
            skLineSegment(sketch, "E5103", {"start": v(131.65, 74.26) * mm, "end": v(131.65, 74.25) * mm});
            skLineSegment(sketch, "E5104", {"start": v(131.65, 74.25) * mm, "end": v(131.65, 74.23) * mm});
            skLineSegment(sketch, "E5105", {"start": v(131.65, 74.23) * mm, "end": v(131.65, 74.22) * mm});
            skLineSegment(sketch, "E5106", {"start": v(131.65, 74.22) * mm, "end": v(131.64, 74.21) * mm});
            skLineSegment(sketch, "E5107", {"start": v(131.64, 74.21) * mm, "end": v(131.64, 74.2) * mm});
            skLineSegment(sketch, "E5108", {"start": v(131.64, 74.2) * mm, "end": v(131.64, 74.2) * mm});
            skLineSegment(sketch, "E5109", {"start": v(131.64, 74.2) * mm, "end": v(131.64, 74.18) * mm});
            skLineSegment(sketch, "E5110", {"start": v(131.64, 74.18) * mm, "end": v(131.64, 74.17) * mm});
            skLineSegment(sketch, "E5111", {"start": v(131.64, 74.17) * mm, "end": v(131.63, 74.16) * mm});
            skLineSegment(sketch, "E5112", {"start": v(131.63, 74.16) * mm, "end": v(131.63, 74.15) * mm});
            skLineSegment(sketch, "E5113", {"start": v(131.63, 74.15) * mm, "end": v(131.63, 74.14) * mm});
            skLineSegment(sketch, "E5114", {"start": v(131.63, 74.14) * mm, "end": v(131.63, 74.13) * mm});
            skLineSegment(sketch, "E5115", {"start": v(131.63, 74.13) * mm, "end": v(131.63, 74.12) * mm});
            skLineSegment(sketch, "E5116", {"start": v(131.63, 74.12) * mm, "end": v(131.63, 74.1) * mm});
            skLineSegment(sketch, "E5117", {"start": v(131.63, 74.1) * mm, "end": v(131.62, 74.1) * mm});
            skLineSegment(sketch, "E5118", {"start": v(131.62, 74.1) * mm, "end": v(131.62, 74.09) * mm});
            skLineSegment(sketch, "E5119", {"start": v(131.62, 74.09) * mm, "end": v(131.62, 74.08) * mm});
            skLineSegment(sketch, "E5120", {"start": v(131.62, 74.08) * mm, "end": v(131.62, 74.07) * mm});
            skLineSegment(sketch, "E5121", {"start": v(131.62, 74.07) * mm, "end": v(131.62, 74.06) * mm});
            skLineSegment(sketch, "E5122", {"start": v(131.62, 74.06) * mm, "end": v(131.62, 74.05) * mm});
            skLineSegment(sketch, "E5123", {"start": v(131.62, 74.05) * mm, "end": v(131.61, 74.04) * mm});
            skLineSegment(sketch, "E5124", {"start": v(131.61, 74.04) * mm, "end": v(131.61, 74.04) * mm});
            skLineSegment(sketch, "E5125", {"start": v(131.61, 74.04) * mm, "end": v(131.61, 74.03) * mm});
            skLineSegment(sketch, "E5126", {"start": v(131.61, 74.03) * mm, "end": v(131.61, 74.03) * mm});
            skLineSegment(sketch, "E5127", {"start": v(131.61, 74.03) * mm, "end": v(131.61, 74.02) * mm});
            skLineSegment(sketch, "E5128", {"start": v(131.61, 74.02) * mm, "end": v(131.61, 74.02) * mm});
            skLineSegment(sketch, "E5129", {"start": v(131.61, 74.02) * mm, "end": v(131.61, 74.01) * mm});
            skLineSegment(sketch, "E5130", {"start": v(131.61, 74.01) * mm, "end": v(131.6, 74) * mm});
            skLineSegment(sketch, "E5131", {"start": v(131.6, 74) * mm, "end": v(131.6, 74) * mm});
            skLineSegment(sketch, "E5132", {"start": v(131.6, 74) * mm, "end": v(131.6, 73.99) * mm});
            skLineSegment(sketch, "E5133", {"start": v(131.6, 73.99) * mm, "end": v(131.6, 73.98) * mm});
            skLineSegment(sketch, "E5134", {"start": v(131.6, 73.98) * mm, "end": v(131.6, 73.98) * mm});
            skLineSegment(sketch, "E5135", {"start": v(131.6, 73.98) * mm, "end": v(131.6, 73.97) * mm});
            skLineSegment(sketch, "E5136", {"start": v(131.6, 73.97) * mm, "end": v(131.6, 73.97) * mm});
            skLineSegment(sketch, "E5137", {"start": v(131.6, 73.97) * mm, "end": v(131.6, 73.96) * mm});
            skLineSegment(sketch, "E5138", {"start": v(131.6, 73.96) * mm, "end": v(131.6, 73.96) * mm});
            skLineSegment(sketch, "E5139", {"start": v(131.6, 73.96) * mm, "end": v(131.6, 73.95) * mm});
            skLineSegment(sketch, "E5140", {"start": v(131.6, 73.95) * mm, "end": v(131.6, 73.95) * mm});
            skLineSegment(sketch, "E5141", {"start": v(131.6, 73.95) * mm, "end": v(131.6, 73.94) * mm});
            skLineSegment(sketch, "E5142", {"start": v(131.6, 73.94) * mm, "end": v(131.6, 73.94) * mm});
            skLineSegment(sketch, "E5143", {"start": v(131.6, 73.94) * mm, "end": v(131.6, 73.93) * mm});
            skLineSegment(sketch, "E5144", {"start": v(131.6, 73.93) * mm, "end": v(131.6, 73.93) * mm});
            skLineSegment(sketch, "E5145", {"start": v(131.6, 73.93) * mm, "end": v(131.6, 73.92) * mm});
            skLineSegment(sketch, "E5146", {"start": v(131.6, 73.92) * mm, "end": v(131.6, 73.92) * mm});
            skLineSegment(sketch, "E5147", {"start": v(131.6, 73.92) * mm, "end": v(131.6, 73.91) * mm});
            skLineSegment(sketch, "E5148", {"start": v(131.6, 73.91) * mm, "end": v(131.6, 73.9) * mm});
            skLineSegment(sketch, "E5149", {"start": v(131.6, 73.9) * mm, "end": v(131.6, 73.9) * mm});
            skLineSegment(sketch, "E5150", {"start": v(131.6, 73.9) * mm, "end": v(131.6, 73.89) * mm});
            skLineSegment(sketch, "E5151", {"start": v(131.6, 73.89) * mm, "end": v(131.6, 73.88) * mm});
            skLineSegment(sketch, "E5152", {"start": v(131.6, 73.88) * mm, "end": v(131.6, 73.88) * mm});
            skLineSegment(sketch, "E5153", {"start": v(131.6, 73.88) * mm, "end": v(131.6, 73.87) * mm});
            skLineSegment(sketch, "E5154", {"start": v(131.6, 73.87) * mm, "end": v(131.6, 73.87) * mm});
            skLineSegment(sketch, "E5155", {"start": v(131.6, 73.87) * mm, "end": v(131.6, 73.86) * mm});
            skLineSegment(sketch, "E5156", {"start": v(131.6, 73.86) * mm, "end": v(131.6, 73.86) * mm});
            skLineSegment(sketch, "E5157", {"start": v(131.6, 73.86) * mm, "end": v(131.6, 73.85) * mm});
            skLineSegment(sketch, "E5158", {"start": v(131.6, 73.85) * mm, "end": v(131.6, 73.85) * mm});
            skLineSegment(sketch, "E5159", {"start": v(131.6, 73.85) * mm, "end": v(131.6, 73.84) * mm});
            skLineSegment(sketch, "E5160", {"start": v(131.6, 73.84) * mm, "end": v(131.6, 73.83) * mm});
            skLineSegment(sketch, "E5161", {"start": v(131.6, 73.83) * mm, "end": v(131.6, 73.83) * mm});
            skLineSegment(sketch, "E5162", {"start": v(131.6, 73.83) * mm, "end": v(131.6, 73.82) * mm});
            skLineSegment(sketch, "E5163", {"start": v(131.6, 73.82) * mm, "end": v(131.6, 73.81) * mm});
            skLineSegment(sketch, "E5164", {"start": v(131.6, 73.81) * mm, "end": v(131.6, 73.8) * mm});
            skLineSegment(sketch, "E5165", {"start": v(131.6, 73.8) * mm, "end": v(131.6, 73.8) * mm});
            skLineSegment(sketch, "E5166", {"start": v(131.6, 73.8) * mm, "end": v(131.6, 73.79) * mm});
            skLineSegment(sketch, "E5167", {"start": v(131.6, 73.79) * mm, "end": v(131.6, 73.78) * mm});
            skLineSegment(sketch, "E5168", {"start": v(131.6, 73.78) * mm, "end": v(131.6, 73.78) * mm});
            skLineSegment(sketch, "E5169", {"start": v(131.6, 73.78) * mm, "end": v(131.6, 73.77) * mm});
            skLineSegment(sketch, "E5170", {"start": v(131.6, 73.77) * mm, "end": v(131.6, 73.77) * mm});
            skLineSegment(sketch, "E5171", {"start": v(131.6, 73.77) * mm, "end": v(131.6, 73.76) * mm});
            skLineSegment(sketch, "E5172", {"start": v(131.6, 73.76) * mm, "end": v(131.6, 73.75) * mm});
            skLineSegment(sketch, "E5173", {"start": v(131.6, 73.75) * mm, "end": v(131.6, 73.75) * mm});
            skLineSegment(sketch, "E5174", {"start": v(131.6, 73.75) * mm, "end": v(131.6, 73.74) * mm});
            skLineSegment(sketch, "E5175", {"start": v(131.6, 73.74) * mm, "end": v(131.6, 73.74) * mm});
            skLineSegment(sketch, "E5176", {"start": v(131.6, 73.74) * mm, "end": v(131.6, 73.73) * mm});
            skLineSegment(sketch, "E5177", {"start": v(131.6, 73.73) * mm, "end": v(131.6, 73.72) * mm});
            skLineSegment(sketch, "E5178", {"start": v(131.6, 73.72) * mm, "end": v(131.59, 73.72) * mm});
            skLineSegment(sketch, "E5179", {"start": v(131.59, 73.72) * mm, "end": v(131.59, 73.71) * mm});
            skLineSegment(sketch, "E5180", {"start": v(131.59, 73.71) * mm, "end": v(131.59, 73.7) * mm});
            skLineSegment(sketch, "E5181", {"start": v(131.59, 73.7) * mm, "end": v(131.59, 73.7) * mm});
            skLineSegment(sketch, "E5182", {"start": v(131.59, 73.7) * mm, "end": v(131.58, 73.68) * mm});
            skLineSegment(sketch, "E5183", {"start": v(131.58, 73.68) * mm, "end": v(131.58, 73.68) * mm});
            skLineSegment(sketch, "E5184", {"start": v(131.58, 73.68) * mm, "end": v(131.58, 73.67) * mm});
            skLineSegment(sketch, "E5185", {"start": v(131.58, 73.67) * mm, "end": v(131.58, 73.67) * mm});
            skLineSegment(sketch, "E5186", {"start": v(131.58, 73.67) * mm, "end": v(131.58, 73.66) * mm});
            skLineSegment(sketch, "E5187", {"start": v(131.58, 73.66) * mm, "end": v(131.58, 73.66) * mm});
            skLineSegment(sketch, "E5188", {"start": v(131.58, 73.66) * mm, "end": v(131.58, 73.65) * mm});
            skLineSegment(sketch, "E5189", {"start": v(131.58, 73.65) * mm, "end": v(131.58, 73.65) * mm});
            skLineSegment(sketch, "E5190", {"start": v(131.58, 73.65) * mm, "end": v(131.58, 73.64) * mm});
            skLineSegment(sketch, "E5191", {"start": v(131.58, 73.64) * mm, "end": v(131.57, 73.64) * mm});
            skLineSegment(sketch, "E5192", {"start": v(131.57, 73.64) * mm, "end": v(131.57, 73.63) * mm});
            skLineSegment(sketch, "E5193", {"start": v(131.57, 73.63) * mm, "end": v(131.57, 73.63) * mm});
            skLineSegment(sketch, "E5194", {"start": v(131.57, 73.63) * mm, "end": v(131.57, 73.62) * mm});
            skLineSegment(sketch, "E5195", {"start": v(131.57, 73.62) * mm, "end": v(131.57, 73.62) * mm});
            skLineSegment(sketch, "E5196", {"start": v(131.57, 73.62) * mm, "end": v(131.57, 73.61) * mm});
            skLineSegment(sketch, "E5197", {"start": v(131.57, 73.61) * mm, "end": v(131.57, 73.6) * mm});
            skLineSegment(sketch, "E5198", {"start": v(131.57, 73.6) * mm, "end": v(131.56, 73.6) * mm});
            skLineSegment(sketch, "E5199", {"start": v(131.56, 73.6) * mm, "end": v(131.56, 73.6) * mm});
            skLineSegment(sketch, "E5200", {"start": v(131.56, 73.6) * mm, "end": v(131.56, 73.59) * mm});
            skLineSegment(sketch, "E5201", {"start": v(131.56, 73.59) * mm, "end": v(131.56, 73.58) * mm});
            skLineSegment(sketch, "E5202", {"start": v(131.56, 73.58) * mm, "end": v(131.56, 73.58) * mm});
            skLineSegment(sketch, "E5203", {"start": v(131.56, 73.58) * mm, "end": v(131.55, 73.57) * mm});
            skLineSegment(sketch, "E5204", {"start": v(131.55, 73.57) * mm, "end": v(131.55, 73.57) * mm});
            skLineSegment(sketch, "E5205", {"start": v(131.55, 73.57) * mm, "end": v(131.55, 73.56) * mm});
            skLineSegment(sketch, "E5206", {"start": v(131.55, 73.56) * mm, "end": v(131.55, 73.56) * mm});
            skLineSegment(sketch, "E5207", {"start": v(131.55, 73.56) * mm, "end": v(131.55, 73.55) * mm});
            skLineSegment(sketch, "E5208", {"start": v(131.55, 73.55) * mm, "end": v(131.54, 73.55) * mm});
            skLineSegment(sketch, "E5209", {"start": v(131.54, 73.55) * mm, "end": v(131.54, 73.54) * mm});
            skLineSegment(sketch, "E5210", {"start": v(131.54, 73.54) * mm, "end": v(131.54, 73.54) * mm});
            skLineSegment(sketch, "E5211", {"start": v(131.54, 73.54) * mm, "end": v(131.54, 73.53) * mm});
            skLineSegment(sketch, "E5212", {"start": v(131.54, 73.53) * mm, "end": v(131.53, 73.53) * mm});
            skLineSegment(sketch, "E5213", {"start": v(131.53, 73.53) * mm, "end": v(131.53, 73.52) * mm});
            skLineSegment(sketch, "E5214", {"start": v(131.53, 73.52) * mm, "end": v(131.53, 73.52) * mm});
            skLineSegment(sketch, "E5215", {"start": v(131.53, 73.52) * mm, "end": v(131.53, 73.51) * mm});
            skLineSegment(sketch, "E5216", {"start": v(131.53, 73.51) * mm, "end": v(131.52, 73.5) * mm});
            skLineSegment(sketch, "E5217", {"start": v(131.52, 73.5) * mm, "end": v(131.52, 73.5) * mm});
            skLineSegment(sketch, "E5218", {"start": v(131.52, 73.5) * mm, "end": v(131.51, 73.49) * mm});
            skLineSegment(sketch, "E5219", {"start": v(131.51, 73.49) * mm, "end": v(131.51, 73.49) * mm});
            skLineSegment(sketch, "E5220", {"start": v(131.51, 73.49) * mm, "end": v(131.5, 73.48) * mm});
            skLineSegment(sketch, "E5221", {"start": v(131.5, 73.48) * mm, "end": v(131.5, 73.48) * mm});
            skLineSegment(sketch, "E5222", {"start": v(131.5, 73.48) * mm, "end": v(131.5, 73.47) * mm});
            skLineSegment(sketch, "E5223", {"start": v(131.5, 73.47) * mm, "end": v(131.5, 73.47) * mm});
            skLineSegment(sketch, "E5224", {"start": v(131.5, 73.47) * mm, "end": v(131.5, 73.46) * mm});
            skLineSegment(sketch, "E5225", {"start": v(131.5, 73.46) * mm, "end": v(131.5, 73.46) * mm});
            skLineSegment(sketch, "E5226", {"start": v(131.5, 73.46) * mm, "end": v(131.49, 73.45) * mm});
            skLineSegment(sketch, "E5227", {"start": v(131.49, 73.45) * mm, "end": v(131.49, 73.45) * mm});
            skLineSegment(sketch, "E5228", {"start": v(131.49, 73.45) * mm, "end": v(131.48, 73.45) * mm});
            skLineSegment(sketch, "E5229", {"start": v(131.48, 73.45) * mm, "end": v(131.48, 73.44) * mm});
            skLineSegment(sketch, "E5230", {"start": v(131.48, 73.44) * mm, "end": v(131.48, 73.44) * mm});
            skLineSegment(sketch, "E5231", {"start": v(131.48, 73.44) * mm, "end": v(131.47, 73.44) * mm});
            skLineSegment(sketch, "E5232", {"start": v(131.47, 73.44) * mm, "end": v(131.47, 73.43) * mm});
            skLineSegment(sketch, "E5233", {"start": v(131.47, 73.43) * mm, "end": v(131.47, 73.43) * mm});
            skLineSegment(sketch, "E5234", {"start": v(131.47, 73.43) * mm, "end": v(131.46, 73.43) * mm});
            skLineSegment(sketch, "E5235", {"start": v(131.46, 73.43) * mm, "end": v(131.46, 73.42) * mm});
            skLineSegment(sketch, "E5236", {"start": v(131.46, 73.42) * mm, "end": v(131.46, 73.42) * mm});
            skLineSegment(sketch, "E5237", {"start": v(131.46, 73.42) * mm, "end": v(131.45, 73.41) * mm});
            skLineSegment(sketch, "E5238", {"start": v(131.45, 73.41) * mm, "end": v(131.45, 73.4) * mm});
            skLineSegment(sketch, "E5239", {"start": v(131.45, 73.4) * mm, "end": v(131.44, 73.4) * mm});
            skLineSegment(sketch, "E5240", {"start": v(131.44, 73.4) * mm, "end": v(131.43, 73.4) * mm});
            skLineSegment(sketch, "E5241", {"start": v(131.43, 73.4) * mm, "end": v(131.43, 73.4) * mm});
            skLineSegment(sketch, "E5242", {"start": v(131.43, 73.4) * mm, "end": v(131.42, 73.39) * mm});
            skLineSegment(sketch, "E5243", {"start": v(131.42, 73.39) * mm, "end": v(131.42, 73.38) * mm});
            skLineSegment(sketch, "E5244", {"start": v(131.42, 73.38) * mm, "end": v(131.4, 73.38) * mm});
            skLineSegment(sketch, "E5245", {"start": v(131.4, 73.38) * mm, "end": v(131.4, 73.37) * mm});
            skLineSegment(sketch, "E5246", {"start": v(131.4, 73.37) * mm, "end": v(131.4, 73.37) * mm});
            skLineSegment(sketch, "E5247", {"start": v(131.4, 73.37) * mm, "end": v(131.39, 73.37) * mm});
            skLineSegment(sketch, "E5248", {"start": v(131.39, 73.37) * mm, "end": v(131.38, 73.36) * mm});
            skLineSegment(sketch, "E5249", {"start": v(131.38, 73.36) * mm, "end": v(131.37, 73.36) * mm});
            skLineSegment(sketch, "E5250", {"start": v(131.37, 73.36) * mm, "end": v(131.37, 73.35) * mm});
            skLineSegment(sketch, "E5251", {"start": v(131.37, 73.35) * mm, "end": v(131.36, 73.35) * mm});
            skLineSegment(sketch, "E5252", {"start": v(131.36, 73.35) * mm, "end": v(131.35, 73.35) * mm});
            skLineSegment(sketch, "E5253", {"start": v(131.35, 73.35) * mm, "end": v(131.35, 73.34) * mm});
            skLineSegment(sketch, "E5254", {"start": v(131.35, 73.34) * mm, "end": v(131.34, 73.34) * mm});
            skLineSegment(sketch, "E5255", {"start": v(131.34, 73.34) * mm, "end": v(131.33, 73.34) * mm});
            skLineSegment(sketch, "E5256", {"start": v(131.33, 73.34) * mm, "end": v(131.32, 73.34) * mm});
            skLineSegment(sketch, "E5257", {"start": v(131.32, 73.34) * mm, "end": v(131.32, 73.33) * mm});
            skLineSegment(sketch, "E5258", {"start": v(131.32, 73.33) * mm, "end": v(131.3, 73.33) * mm});
            skLineSegment(sketch, "E5259", {"start": v(131.3, 73.33) * mm, "end": v(131.3, 73.33) * mm});
            skLineSegment(sketch, "E5260", {"start": v(131.3, 73.33) * mm, "end": v(131.28, 73.32) * mm});
            skLineSegment(sketch, "E5261", {"start": v(131.28, 73.32) * mm, "end": v(131.28, 73.32) * mm});
            skLineSegment(sketch, "E5262", {"start": v(131.28, 73.32) * mm, "end": v(131.27, 73.32) * mm});
            skLineSegment(sketch, "E5263", {"start": v(131.27, 73.32) * mm, "end": v(131.26, 73.32) * mm});
            skLineSegment(sketch, "E5264", {"start": v(131.26, 73.32) * mm, "end": v(131.25, 73.32) * mm});
            skLineSegment(sketch, "E5265", {"start": v(131.25, 73.32) * mm, "end": v(131.24, 73.32) * mm});
            skLineSegment(sketch, "E5266", {"start": v(131.24, 73.32) * mm, "end": v(131.23, 73.31) * mm});
            skLineSegment(sketch, "E5267", {"start": v(131.23, 73.31) * mm, "end": v(131.22, 73.31) * mm});
            skLineSegment(sketch, "E5268", {"start": v(131.22, 73.31) * mm, "end": v(131.22, 73.31) * mm});
            skLineSegment(sketch, "E5269", {"start": v(131.22, 73.31) * mm, "end": v(131.2, 73.31) * mm});
            skLineSegment(sketch, "E5270", {"start": v(131.2, 73.31) * mm, "end": v(131.2, 73.31) * mm});
            skLineSegment(sketch, "E5271", {"start": v(131.2, 73.31) * mm, "end": v(131.19, 73.31) * mm});
            skLineSegment(sketch, "E5272", {"start": v(131.19, 73.31) * mm, "end": v(131.18, 73.3) * mm});
            skLineSegment(sketch, "E5273", {"start": v(131.18, 73.3) * mm, "end": v(131.17, 73.3) * mm});
            skLineSegment(sketch, "E5274", {"start": v(131.17, 73.3) * mm, "end": v(131.16, 73.3) * mm});
            skLineSegment(sketch, "E5275", {"start": v(131.16, 73.3) * mm, "end": v(131.15, 73.3) * mm});
            skLineSegment(sketch, "E5276", {"start": v(131.15, 73.3) * mm, "end": v(131.14, 73.3) * mm});
            skLineSegment(sketch, "E5277", {"start": v(131.14, 73.3) * mm, "end": v(131.13, 73.3) * mm});
            skLineSegment(sketch, "E5278", {"start": v(131.13, 73.3) * mm, "end": v(131.12, 73.31) * mm});
            skLineSegment(sketch, "E5279", {"start": v(131.12, 73.31) * mm, "end": v(131.11, 73.31) * mm});
            skLineSegment(sketch, "E5280", {"start": v(131.11, 73.31) * mm, "end": v(131.1, 73.31) * mm});
            skLineSegment(sketch, "E5281", {"start": v(131.1, 73.31) * mm, "end": v(131.1, 73.31) * mm});
            skLineSegment(sketch, "E5282", {"start": v(131.1, 73.31) * mm, "end": v(131.09, 73.31) * mm});
            skLineSegment(sketch, "E5283", {"start": v(131.09, 73.31) * mm, "end": v(131.08, 73.31) * mm});
            skLineSegment(sketch, "E5284", {"start": v(131.08, 73.31) * mm, "end": v(131.07, 73.32) * mm});
            skLineSegment(sketch, "E5285", {"start": v(131.07, 73.32) * mm, "end": v(131.06, 73.32) * mm});
            skLineSegment(sketch, "E5286", {"start": v(131.06, 73.32) * mm, "end": v(131.05, 73.32) * mm});
            skLineSegment(sketch, "E5287", {"start": v(131.05, 73.32) * mm, "end": v(131.04, 73.32) * mm});
            skLineSegment(sketch, "E5288", {"start": v(131.04, 73.32) * mm, "end": v(131.03, 73.32) * mm});
            skLineSegment(sketch, "E5289", {"start": v(131.03, 73.32) * mm, "end": v(131.02, 73.32) * mm});
            skLineSegment(sketch, "E5290", {"start": v(131.02, 73.32) * mm, "end": v(131, 73.33) * mm});
            skLineSegment(sketch, "E5291", {"start": v(131, 73.33) * mm, "end": v(131, 73.33) * mm});
            skLineSegment(sketch, "E5292", {"start": v(131, 73.33) * mm, "end": v(130.98, 73.33) * mm});
            skLineSegment(sketch, "E5293", {"start": v(130.98, 73.33) * mm, "end": v(130.97, 73.33) * mm});
            skLineSegment(sketch, "E5294", {"start": v(130.97, 73.33) * mm, "end": v(130.96, 73.34) * mm});
            skLineSegment(sketch, "E5295", {"start": v(130.96, 73.34) * mm, "end": v(130.95, 73.34) * mm});
            skLineSegment(sketch, "E5296", {"start": v(130.95, 73.34) * mm, "end": v(130.94, 73.34) * mm});
            skLineSegment(sketch, "E5297", {"start": v(130.94, 73.34) * mm, "end": v(130.93, 73.34) * mm});
            skLineSegment(sketch, "E5298", {"start": v(130.93, 73.34) * mm, "end": v(130.92, 73.35) * mm});
            skLineSegment(sketch, "E5299", {"start": v(130.92, 73.35) * mm, "end": v(130.91, 73.35) * mm});
            skLineSegment(sketch, "E5300", {"start": v(130.91, 73.35) * mm, "end": v(130.9, 73.35) * mm});
            skLineSegment(sketch, "E5301", {"start": v(130.9, 73.35) * mm, "end": v(130.89, 73.36) * mm});
            skLineSegment(sketch, "E5302", {"start": v(130.89, 73.36) * mm, "end": v(130.88, 73.36) * mm});
            skLineSegment(sketch, "E5303", {"start": v(130.88, 73.36) * mm, "end": v(130.87, 73.36) * mm});
            skLineSegment(sketch, "E5304", {"start": v(130.87, 73.36) * mm, "end": v(130.86, 73.37) * mm});
            skLineSegment(sketch, "E5305", {"start": v(130.86, 73.37) * mm, "end": v(130.85, 73.37) * mm});
            skLineSegment(sketch, "E5306", {"start": v(130.85, 73.37) * mm, "end": v(130.83, 73.38) * mm});
            skLineSegment(sketch, "E5307", {"start": v(130.83, 73.38) * mm, "end": v(130.82, 73.38) * mm});
            skLineSegment(sketch, "E5308", {"start": v(130.82, 73.38) * mm, "end": v(130.81, 73.38) * mm});
            skLineSegment(sketch, "E5309", {"start": v(130.81, 73.38) * mm, "end": v(130.8, 73.39) * mm});
            skLineSegment(sketch, "E5310", {"start": v(130.8, 73.39) * mm, "end": v(130.8, 73.4) * mm});
            skLineSegment(sketch, "E5311", {"start": v(130.8, 73.4) * mm, "end": v(130.78, 73.4) * mm});
            skLineSegment(sketch, "E5312", {"start": v(130.78, 73.4) * mm, "end": v(130.77, 73.4) * mm});
            skLineSegment(sketch, "E5313", {"start": v(130.77, 73.4) * mm, "end": v(130.76, 73.4) * mm});
            skLineSegment(sketch, "E5314", {"start": v(130.76, 73.4) * mm, "end": v(130.74, 73.41) * mm});
            skLineSegment(sketch, "E5315", {"start": v(130.74, 73.41) * mm, "end": v(130.73, 73.42) * mm});
            skLineSegment(sketch, "E5316", {"start": v(130.73, 73.42) * mm, "end": v(130.72, 73.42) * mm});
            skLineSegment(sketch, "E5317", {"start": v(130.72, 73.42) * mm, "end": v(130.71, 73.43) * mm});
            skLineSegment(sketch, "E5318", {"start": v(130.71, 73.43) * mm, "end": v(130.7, 73.43) * mm});
            skLineSegment(sketch, "E5319", {"start": v(130.7, 73.43) * mm, "end": v(130.69, 73.44) * mm});
            skLineSegment(sketch, "E5320", {"start": v(130.69, 73.44) * mm, "end": v(130.68, 73.45) * mm});
            skLineSegment(sketch, "E5321", {"start": v(130.68, 73.45) * mm, "end": v(130.66, 73.45) * mm});
            skLineSegment(sketch, "E5322", {"start": v(130.66, 73.45) * mm, "end": v(130.65, 73.46) * mm});
            skLineSegment(sketch, "E5323", {"start": v(130.65, 73.46) * mm, "end": v(130.64, 73.46) * mm});
            skLineSegment(sketch, "E5324", {"start": v(130.64, 73.46) * mm, "end": v(130.63, 73.47) * mm});
            skLineSegment(sketch, "E5325", {"start": v(130.63, 73.47) * mm, "end": v(130.62, 73.48) * mm});
            skLineSegment(sketch, "E5326", {"start": v(130.62, 73.48) * mm, "end": v(130.6, 73.48) * mm});
            skLineSegment(sketch, "E5327", {"start": v(130.6, 73.48) * mm, "end": v(130.6, 73.49) * mm});
            skLineSegment(sketch, "E5328", {"start": v(130.6, 73.49) * mm, "end": v(130.58, 73.5) * mm});
            skLineSegment(sketch, "E5329", {"start": v(130.58, 73.5) * mm, "end": v(130.57, 73.5) * mm});
            skLineSegment(sketch, "E5330", {"start": v(130.57, 73.5) * mm, "end": v(130.56, 73.51) * mm});
            skLineSegment(sketch, "E5331", {"start": v(130.56, 73.51) * mm, "end": v(130.55, 73.52) * mm});
            skLineSegment(sketch, "E5332", {"start": v(130.55, 73.52) * mm, "end": v(130.53, 73.52) * mm});
            skLineSegment(sketch, "E5333", {"start": v(130.53, 73.52) * mm, "end": v(130.52, 73.53) * mm});
            skLineSegment(sketch, "E5334", {"start": v(130.52, 73.53) * mm, "end": v(130.51, 73.54) * mm});
            skLineSegment(sketch, "E5335", {"start": v(130.51, 73.54) * mm, "end": v(130.5, 73.55) * mm});
            skLineSegment(sketch, "E5336", {"start": v(130.5, 73.55) * mm, "end": v(130.49, 73.55) * mm});
            skLineSegment(sketch, "E5337", {"start": v(130.49, 73.55) * mm, "end": v(130.48, 73.56) * mm});
            skLineSegment(sketch, "E5338", {"start": v(130.48, 73.56) * mm, "end": v(130.46, 73.57) * mm});
            skLineSegment(sketch, "E5339", {"start": v(130.46, 73.57) * mm, "end": v(130.45, 73.58) * mm});
            skLineSegment(sketch, "E5340", {"start": v(130.45, 73.58) * mm, "end": v(130.44, 73.59) * mm});
            skLineSegment(sketch, "E5341", {"start": v(130.44, 73.59) * mm, "end": v(130.43, 73.6) * mm});
            skLineSegment(sketch, "E5342", {"start": v(130.43, 73.6) * mm, "end": v(130.41, 73.6) * mm});
            skLineSegment(sketch, "E5343", {"start": v(130.41, 73.6) * mm, "end": v(130.4, 73.61) * mm});
            skLineSegment(sketch, "E5344", {"start": v(130.4, 73.61) * mm, "end": v(130.4, 73.62) * mm});
            skLineSegment(sketch, "E5345", {"start": v(130.4, 73.62) * mm, "end": v(130.38, 73.63) * mm});
            skLineSegment(sketch, "E5346", {"start": v(130.38, 73.63) * mm, "end": v(130.37, 73.64) * mm});
            skLineSegment(sketch, "E5347", {"start": v(130.37, 73.64) * mm, "end": v(130.35, 73.65) * mm});
            skLineSegment(sketch, "E5348", {"start": v(130.35, 73.65) * mm, "end": v(130.34, 73.65) * mm});
            skLineSegment(sketch, "E5349", {"start": v(130.34, 73.65) * mm, "end": v(130.33, 73.66) * mm});
            skLineSegment(sketch, "E5350", {"start": v(130.33, 73.66) * mm, "end": v(130.32, 73.67) * mm});
            skLineSegment(sketch, "E5351", {"start": v(130.32, 73.67) * mm, "end": v(130.3, 73.68) * mm});
            skLineSegment(sketch, "E5352", {"start": v(130.3, 73.68) * mm, "end": v(130.3, 73.7) * mm});
            skLineSegment(sketch, "E5353", {"start": v(130.3, 73.7) * mm, "end": v(130.28, 73.7) * mm});
            skLineSegment(sketch, "E5354", {"start": v(130.28, 73.7) * mm, "end": v(130.27, 73.71) * mm});
            skLineSegment(sketch, "E5355", {"start": v(130.27, 73.71) * mm, "end": v(130.26, 73.72) * mm});
            skLineSegment(sketch, "E5356", {"start": v(130.26, 73.72) * mm, "end": v(130.25, 73.73) * mm});
            skLineSegment(sketch, "E5357", {"start": v(130.25, 73.73) * mm, "end": v(130.23, 73.74) * mm});
            skLineSegment(sketch, "E5358", {"start": v(130.23, 73.74) * mm, "end": v(130.22, 73.75) * mm});
            skLineSegment(sketch, "E5359", {"start": v(130.22, 73.75) * mm, "end": v(130.2, 73.76) * mm});
            skLineSegment(sketch, "E5360", {"start": v(130.2, 73.76) * mm, "end": v(130.2, 73.77) * mm});
            skLineSegment(sketch, "E5361", {"start": v(130.2, 73.77) * mm, "end": v(130.18, 73.78) * mm});
            skLineSegment(sketch, "E5362", {"start": v(130.18, 73.78) * mm, "end": v(130.17, 73.8) * mm});
            skLineSegment(sketch, "E5363", {"start": v(130.17, 73.8) * mm, "end": v(130.16, 73.8) * mm});
            skLineSegment(sketch, "E5364", {"start": v(130.16, 73.8) * mm, "end": v(130.15, 73.81) * mm});
            skLineSegment(sketch, "E5365", {"start": v(130.15, 73.81) * mm, "end": v(130.14, 73.82) * mm});
            skLineSegment(sketch, "E5366", {"start": v(130.14, 73.82) * mm, "end": v(130.12, 73.83) * mm});
            skLineSegment(sketch, "E5367", {"start": v(130.12, 73.83) * mm, "end": v(130.11, 73.84) * mm});
            skLineSegment(sketch, "E5368", {"start": v(130.11, 73.84) * mm, "end": v(130.1, 73.85) * mm});
            skLineSegment(sketch, "E5369", {"start": v(130.1, 73.85) * mm, "end": v(130.09, 73.87) * mm});
            skLineSegment(sketch, "E5370", {"start": v(130.09, 73.87) * mm, "end": v(130.08, 73.88) * mm});
            skLineSegment(sketch, "E5371", {"start": v(130.08, 73.88) * mm, "end": v(130.06, 73.89) * mm});
            skLineSegment(sketch, "E5372", {"start": v(130.06, 73.89) * mm, "end": v(130.05, 73.9) * mm});
            skLineSegment(sketch, "E5373", {"start": v(130.05, 73.9) * mm, "end": v(130.04, 73.91) * mm});
            skLineSegment(sketch, "E5374", {"start": v(130.04, 73.91) * mm, "end": v(130.03, 73.92) * mm});
            skLineSegment(sketch, "E5375", {"start": v(130.03, 73.92) * mm, "end": v(130.02, 73.93) * mm});
            skLineSegment(sketch, "E5376", {"start": v(130.02, 73.93) * mm, "end": v(130, 73.95) * mm});
            skLineSegment(sketch, "E5377", {"start": v(130, 73.95) * mm, "end": v(130, 73.96) * mm});
            skLineSegment(sketch, "E5378", {"start": v(130, 73.96) * mm, "end": v(129.98, 73.97) * mm});
            skLineSegment(sketch, "E5379", {"start": v(129.98, 73.97) * mm, "end": v(129.97, 73.98) * mm});
            skLineSegment(sketch, "E5380", {"start": v(129.97, 73.98) * mm, "end": v(129.96, 74) * mm});
            skLineSegment(sketch, "E5381", {"start": v(129.96, 74) * mm, "end": v(129.94, 74) * mm});
            skLineSegment(sketch, "E5382", {"start": v(129.94, 74) * mm, "end": v(129.93, 74.02) * mm});
            skLineSegment(sketch, "E5383", {"start": v(129.93, 74.02) * mm, "end": v(129.92, 74.03) * mm});
            skLineSegment(sketch, "E5384", {"start": v(129.92, 74.03) * mm, "end": v(129.9, 74.04) * mm});
            skLineSegment(sketch, "E5385", {"start": v(129.9, 74.04) * mm, "end": v(129.9, 74.06) * mm});
            skLineSegment(sketch, "E5386", {"start": v(129.9, 74.06) * mm, "end": v(129.88, 74.07) * mm});
            skLineSegment(sketch, "E5387", {"start": v(129.88, 74.07) * mm, "end": v(129.87, 74.08) * mm});
            skLineSegment(sketch, "E5388", {"start": v(129.87, 74.08) * mm, "end": v(129.86, 74.1) * mm});
            skLineSegment(sketch, "E5389", {"start": v(129.86, 74.1) * mm, "end": v(129.85, 74.1) * mm});
            skLineSegment(sketch, "E5390", {"start": v(129.85, 74.1) * mm, "end": v(129.84, 74.12) * mm});
            skLineSegment(sketch, "E5391", {"start": v(129.84, 74.12) * mm, "end": v(129.83, 74.13) * mm});
            skLineSegment(sketch, "E5392", {"start": v(129.83, 74.13) * mm, "end": v(129.81, 74.15) * mm});
            skLineSegment(sketch, "E5393", {"start": v(129.81, 74.15) * mm, "end": v(129.8, 74.16) * mm});
            skLineSegment(sketch, "E5394", {"start": v(129.8, 74.16) * mm, "end": v(129.8, 74.17) * mm});
            skLineSegment(sketch, "E5395", {"start": v(129.8, 74.17) * mm, "end": v(129.78, 74.19) * mm});
            skLineSegment(sketch, "E5396", {"start": v(129.78, 74.19) * mm, "end": v(129.77, 74.2) * mm});
            skLineSegment(sketch, "E5397", {"start": v(129.77, 74.2) * mm, "end": v(129.76, 74.21) * mm});
            skLineSegment(sketch, "E5398", {"start": v(129.76, 74.21) * mm, "end": v(129.75, 74.23) * mm});
            skLineSegment(sketch, "E5399", {"start": v(129.75, 74.23) * mm, "end": v(129.73, 74.24) * mm});
            skLineSegment(sketch, "E5400", {"start": v(129.73, 74.24) * mm, "end": v(129.72, 74.26) * mm});
            skLineSegment(sketch, "E5401", {"start": v(129.72, 74.26) * mm, "end": v(129.71, 74.27) * mm});
            skLineSegment(sketch, "E5402", {"start": v(129.71, 74.27) * mm, "end": v(129.7, 74.28) * mm});
            skLineSegment(sketch, "E5403", {"start": v(129.7, 74.28) * mm, "end": v(129.69, 74.3) * mm});
            skLineSegment(sketch, "E5404", {"start": v(129.69, 74.3) * mm, "end": v(129.68, 74.31) * mm});
            skLineSegment(sketch, "E5405", {"start": v(129.68, 74.31) * mm, "end": v(129.67, 74.33) * mm});
            skLineSegment(sketch, "E5406", {"start": v(129.67, 74.33) * mm, "end": v(129.66, 74.34) * mm});
            skLineSegment(sketch, "E5407", {"start": v(129.66, 74.34) * mm, "end": v(129.65, 74.36) * mm});
            skLineSegment(sketch, "E5408", {"start": v(129.65, 74.36) * mm, "end": v(129.63, 74.37) * mm});
            skLineSegment(sketch, "E5409", {"start": v(129.63, 74.37) * mm, "end": v(129.62, 74.39) * mm});
            skLineSegment(sketch, "E5410", {"start": v(129.62, 74.39) * mm, "end": v(129.61, 74.4) * mm});
            skLineSegment(sketch, "E5411", {"start": v(129.61, 74.4) * mm, "end": v(129.6, 74.42) * mm});
            skLineSegment(sketch, "E5412", {"start": v(129.6, 74.42) * mm, "end": v(129.6, 74.43) * mm});
            skLineSegment(sketch, "E5413", {"start": v(129.6, 74.43) * mm, "end": v(129.58, 74.45) * mm});
            skLineSegment(sketch, "E5414", {"start": v(129.58, 74.45) * mm, "end": v(129.57, 74.46) * mm});
            skLineSegment(sketch, "E5415", {"start": v(129.57, 74.46) * mm, "end": v(129.56, 74.48) * mm});
            skLineSegment(sketch, "E5416", {"start": v(129.56, 74.48) * mm, "end": v(129.55, 74.5) * mm});
            skLineSegment(sketch, "E5417", {"start": v(129.55, 74.5) * mm, "end": v(129.54, 74.5) * mm});
            skLineSegment(sketch, "E5418", {"start": v(129.54, 74.5) * mm, "end": v(129.53, 74.52) * mm});
            skLineSegment(sketch, "E5419", {"start": v(129.53, 74.52) * mm, "end": v(129.52, 74.54) * mm});
            skLineSegment(sketch, "E5420", {"start": v(129.52, 74.54) * mm, "end": v(129.5, 74.55) * mm});
            skLineSegment(sketch, "E5421", {"start": v(129.5, 74.55) * mm, "end": v(129.5, 74.57) * mm});
            skLineSegment(sketch, "E5422", {"start": v(129.5, 74.57) * mm, "end": v(129.49, 74.58) * mm});
            skLineSegment(sketch, "E5423", {"start": v(129.49, 74.58) * mm, "end": v(129.48, 74.6) * mm});
            skLineSegment(sketch, "E5424", {"start": v(129.48, 74.6) * mm, "end": v(129.47, 74.62) * mm});
            skLineSegment(sketch, "E5425", {"start": v(129.47, 74.62) * mm, "end": v(129.46, 74.63) * mm});
            skLineSegment(sketch, "E5426", {"start": v(129.46, 74.63) * mm, "end": v(129.45, 74.65) * mm});
            skLineSegment(sketch, "E5427", {"start": v(129.45, 74.65) * mm, "end": v(129.44, 74.66) * mm});
            skLineSegment(sketch, "E5428", {"start": v(129.44, 74.66) * mm, "end": v(129.43, 74.68) * mm});
            skLineSegment(sketch, "E5429", {"start": v(129.43, 74.68) * mm, "end": v(129.42, 74.7) * mm});
            skLineSegment(sketch, "E5430", {"start": v(129.42, 74.7) * mm, "end": v(129.4, 74.71) * mm});
            skLineSegment(sketch, "E5431", {"start": v(129.4, 74.71) * mm, "end": v(129.4, 74.73) * mm});
            skLineSegment(sketch, "E5432", {"start": v(129.4, 74.73) * mm, "end": v(129.39, 74.75) * mm});
            skLineSegment(sketch, "E5433", {"start": v(129.39, 74.75) * mm, "end": v(129.38, 74.76) * mm});
            skLineSegment(sketch, "E5434", {"start": v(129.38, 74.76) * mm, "end": v(129.37, 74.78) * mm});
            skLineSegment(sketch, "E5435", {"start": v(129.37, 74.78) * mm, "end": v(129.36, 74.8) * mm});
            skLineSegment(sketch, "E5436", {"start": v(129.36, 74.8) * mm, "end": v(129.35, 74.81) * mm});
            skLineSegment(sketch, "E5437", {"start": v(129.35, 74.81) * mm, "end": v(129.34, 74.83) * mm});
            skLineSegment(sketch, "E5438", {"start": v(129.34, 74.83) * mm, "end": v(129.33, 74.85) * mm});
            skLineSegment(sketch, "E5439", {"start": v(129.33, 74.85) * mm, "end": v(129.32, 74.86) * mm});
            skLineSegment(sketch, "E5440", {"start": v(129.32, 74.86) * mm, "end": v(129.31, 74.88) * mm});
            skLineSegment(sketch, "E5441", {"start": v(129.31, 74.88) * mm, "end": v(129.3, 74.9) * mm});
            skLineSegment(sketch, "E5442", {"start": v(129.3, 74.9) * mm, "end": v(129.3, 74.91) * mm});
            skLineSegment(sketch, "E5443", {"start": v(129.3, 74.91) * mm, "end": v(129.28, 74.93) * mm});
            skLineSegment(sketch, "E5444", {"start": v(129.28, 74.93) * mm, "end": v(129.28, 74.95) * mm});
            skLineSegment(sketch, "E5445", {"start": v(129.28, 74.95) * mm, "end": v(129.27, 74.97) * mm});
            skArc(sketch, "E5446", {"start": v(135.52, 76.37) * mm, "mid": v(135.98, 76.03) * mm, "end": v(136.55, 76.1) * mm});
            skArc(sketch, "E5447", {"start": v(136.55, 76.1) * mm, "mid": v(136.77, 76.53) * mm, "end": v(136.48, 76.9) * mm});
            skArc(sketch, "E5448", {"start": v(136.48, 76.9) * mm, "mid": v(136.05, 76.95) * mm, "end": v(135.63, 76.82) * mm});
            skArc(sketch, "E5449", {"start": v(135.63, 76.82) * mm, "mid": v(135.48, 76.62) * mm, "end": v(135.52, 76.37) * mm});
            skArc(sketch, "E5450", {"start": v(136.25, 73.77) * mm, "mid": v(136.48, 73.25) * mm, "end": v(137.02, 73.06) * mm});
            skArc(sketch, "E5451", {"start": v(137.02, 73.06) * mm, "mid": v(137.42, 73.37) * mm, "end": v(137.3, 73.85) * mm});
            skArc(sketch, "E5452", {"start": v(137.3, 73.85) * mm, "mid": v(136.95, 74.06) * mm, "end": v(136.56, 74.1) * mm});
            skArc(sketch, "E5453", {"start": v(136.56, 74.1) * mm, "mid": v(136.34, 74) * mm, "end": v(136.25, 73.77) * mm});
            skArc(sketch, "E5454", {"start": v(138, 57.38) * mm, "mid": v(139.46, 56.05) * mm, "end": v(141.44, 56) * mm});
            skArc(sketch, "E5455", {"start": v(141.44, 56) * mm, "mid": v(142.14, 55.98) * mm, "end": v(142.44, 55.35) * mm});
            skArc(sketch, "E5456", {"start": v(142.44, 55.35) * mm, "mid": v(142.18, 54.95) * mm, "end": v(141.7, 54.92) * mm});
            skArc(sketch, "E5457", {"start": v(141.7, 54.92) * mm, "mid": v(140.08, 55.29) * mm, "end": v(138.44, 55.05) * mm});
            skArc(sketch, "E5458", {"start": v(138.44, 55.05) * mm, "mid": v(137.99, 54.74) * mm, "end": v(137.78, 54.23) * mm});
            skArc(sketch, "E5459", {"start": v(137.78, 54.23) * mm, "mid": v(137.57, 53.73) * mm, "end": v(137.13, 53.42) * mm});
            skArc(sketch, "E5460", {"start": v(137.13, 53.42) * mm, "mid": v(137.08, 53.37) * mm, "end": v(137.1, 53.3) * mm});
            skArc(sketch, "E5461", {"start": v(137.1, 53.3) * mm, "mid": v(137.36, 53.08) * mm, "end": v(137.65, 52.91) * mm});
            skArc(sketch, "E5462", {"start": v(137.65, 52.91) * mm, "mid": v(138.27, 52.7) * mm, "end": v(138.92, 52.6) * mm});
            skArc(sketch, "E5463", {"start": v(138.92, 52.6) * mm, "mid": v(139.06, 52.53) * mm, "end": v(139.1, 52.38) * mm});
            skArc(sketch, "E5464", {"start": v(139.1, 52.38) * mm, "mid": v(139.04, 52.24) * mm, "end": v(138.9, 52.2) * mm});
            skArc(sketch, "E5465", {"start": v(138.9, 52.2) * mm, "mid": v(137.3, 52.26) * mm, "end": v(135.71, 52.14) * mm});
            skArc(sketch, "E5466", {"start": v(135.71, 52.14) * mm, "mid": v(134.94, 51.47) * mm, "end": v(135.27, 50.51) * mm});
            skArc(sketch, "E5467", {"start": v(135.27, 50.51) * mm, "mid": v(135.77, 50.05) * mm, "end": v(136.17, 49.5) * mm});
            skArc(sketch, "E5468", {"start": v(136.17, 49.5) * mm, "mid": v(136.18, 49.3) * mm, "end": v(136.04, 49.18) * mm});
            skArc(sketch, "E5469", {"start": v(136.04, 49.18) * mm, "mid": v(133.97, 49.26) * mm, "end": v(132.33, 50.52) * mm});
            skArc(sketch, "E5470", {"start": v(132.33, 50.52) * mm, "mid": v(130.8, 51.86) * mm, "end": v(128.84, 52.35) * mm});
            skArc(sketch, "E5471", {"start": v(128.84, 52.35) * mm, "mid": v(127.73, 52.58) * mm, "end": v(126.78, 53.2) * mm});
            skArc(sketch, "E5472", {"start": v(126.78, 53.2) * mm, "mid": v(125.9, 53.9) * mm, "end": v(124.9, 54.39) * mm});
            skArc(sketch, "E5473", {"start": v(124.9, 54.39) * mm, "mid": v(124.64, 54.61) * mm, "end": v(124.62, 54.95) * mm});
            skArc(sketch, "E5474", {"start": v(124.62, 54.95) * mm, "mid": v(124.85, 55.2) * mm, "end": v(125.2, 55.22) * mm});
            skArc(sketch, "E5475", {"start": v(125.2, 55.22) * mm, "mid": v(125.55, 55.25) * mm, "end": v(125.78, 55.54) * mm});
            skArc(sketch, "E5476", {"start": v(125.78, 55.54) * mm, "mid": v(125.7, 55.9) * mm, "end": v(125.4, 56.09) * mm});
            skArc(sketch, "E5477", {"start": v(125.4, 56.09) * mm, "mid": v(124.74, 56.28) * mm, "end": v(124.19, 56.68) * mm});
            skArc(sketch, "E5478", {"start": v(124.19, 56.68) * mm, "mid": v(123.04, 57.31) * mm, "end": v(121.75, 57.2) * mm});
            skArc(sketch, "E5479", {"start": v(121.75, 57.2) * mm, "mid": v(121.1, 56.87) * mm, "end": v(120.5, 56.44) * mm});
            skArc(sketch, "E5480", {"start": v(120.5, 56.44) * mm, "mid": v(120.16, 56.34) * mm, "end": v(119.86, 56.51) * mm});
            skArc(sketch, "E5481", {"start": v(119.86, 56.51) * mm, "mid": v(119.78, 56.85) * mm, "end": v(119.97, 57.15) * mm});
            skArc(sketch, "E5482", {"start": v(119.97, 57.15) * mm, "mid": v(121.27, 57.84) * mm, "end": v(122.68, 58.29) * mm});
            skArc(sketch, "E5483", {"start": v(122.68, 58.29) * mm, "mid": v(122.8, 58.5) * mm, "end": v(122.76, 58.74) * mm});
            skArc(sketch, "E5484", {"start": v(122.76, 58.74) * mm, "mid": v(121.25, 60.08) * mm, "end": v(120.84, 62.05) * mm});
            skArc(sketch, "E5485", {"start": v(120.84, 62.05) * mm, "mid": v(121.12, 63.56) * mm, "end": v(121.6, 65.02) * mm});
            skArc(sketch, "E5486", {"start": v(121.6, 65.02) * mm, "mid": v(121.67, 65.36) * mm, "end": v(121.6, 65.7) * mm});
            skArc(sketch, "E5487", {"start": v(121.6, 65.7) * mm, "mid": v(121.56, 66.03) * mm, "end": v(121.68, 66.35) * mm});
            skArc(sketch, "E5488", {"start": v(121.68, 66.35) * mm, "mid": v(121.86, 66.68) * mm, "end": v(121.98, 67.04) * mm});
            skArc(sketch, "E5489", {"start": v(121.98, 67.04) * mm, "mid": v(122.65, 68.4) * mm, "end": v(123.85, 69.34) * mm});
            skArc(sketch, "E5490", {"start": v(123.85, 69.34) * mm, "mid": v(124.54, 70.44) * mm, "end": v(123.82, 71.52) * mm});
            skArc(sketch, "E5491", {"start": v(123.82, 71.52) * mm, "mid": v(122.17, 72.63) * mm, "end": v(121, 74.24) * mm});
            skArc(sketch, "E5492", {"start": v(121, 74.24) * mm, "mid": v(120.9, 74.84) * mm, "end": v(121.17, 75.39) * mm});
            skArc(sketch, "E5493", {"start": v(121.17, 75.39) * mm, "mid": v(121.61, 75.59) * mm, "end": v(122.07, 75.4) * mm});
            skArc(sketch, "E5494", {"start": v(122.07, 75.4) * mm, "mid": v(123.85, 73.4) * mm, "end": v(125.4, 71.22) * mm});
            skArc(sketch, "E5495", {"start": v(125.4, 71.22) * mm, "mid": v(126, 70.78) * mm, "end": v(126.75, 70.87) * mm});
            skArc(sketch, "E5496", {"start": v(126.75, 70.87) * mm, "mid": v(127.12, 71.56) * mm, "end": v(126.65, 72.18) * mm});
            skArc(sketch, "E5497", {"start": v(126.65, 72.18) * mm, "mid": v(125.9, 73.64) * mm, "end": v(127.29, 74.52) * mm});
            skArc(sketch, "E5498", {"start": v(127.29, 74.52) * mm, "mid": v(127.83, 74.25) * mm, "end": v(128.1, 73.71) * mm});
            skArc(sketch, "E5499", {"start": v(128.1, 73.71) * mm, "mid": v(130.05, 71.82) * mm, "end": v(132.49, 73.02) * mm});
            skArc(sketch, "E5500", {"start": v(132.49, 73.02) * mm, "mid": v(133.23, 74.8) * mm, "end": v(133.61, 76.68) * mm});
            skArc(sketch, "E5501", {"start": v(133.61, 76.68) * mm, "mid": v(133.83, 77.08) * mm, "end": v(134.26, 77.2) * mm});
            skArc(sketch, "E5502", {"start": v(134.26, 77.2) * mm, "mid": v(134.66, 76.98) * mm, "end": v(134.78, 76.55) * mm});
            skArc(sketch, "E5503", {"start": v(134.78, 76.55) * mm, "mid": v(134.6, 75.5) * mm, "end": v(134.37, 74.48) * mm});
            skArc(sketch, "E5504", {"start": v(134.37, 74.48) * mm, "mid": v(134.1, 73.45) * mm, "end": v(133.87, 72.42) * mm});
            skArc(sketch, "E5505", {"start": v(133.87, 72.42) * mm, "mid": v(133.73, 72.02) * mm, "end": v(133.47, 71.68) * mm});
            skArc(sketch, "E5506", {"start": v(133.47, 71.68) * mm, "mid": v(133.32, 71.24) * mm, "end": v(133.56, 70.84) * mm});
            skArc(sketch, "E5507", {"start": v(133.56, 70.84) * mm, "mid": v(134.17, 70.77) * mm, "end": v(134.56, 71.26) * mm});
            skArc(sketch, "E5508", {"start": v(134.56, 71.26) * mm, "mid": v(135.17, 72.17) * mm, "end": v(136.25, 72.37) * mm});
            skArc(sketch, "E5509", {"start": v(136.25, 72.37) * mm, "mid": v(137, 71.67) * mm, "end": v(136.76, 70.67) * mm});
            skArc(sketch, "E5510", {"start": v(136.76, 70.67) * mm, "mid": v(136.54, 70.2) * mm, "end": v(136.55, 69.7) * mm});
            skLineSegment(sketch, "E5511", {"start": v(136.55, 69.7) * mm, "end": v(136.57, 69.64) * mm});
            skLineSegment(sketch, "E5512", {"start": v(136.57, 69.64) * mm, "end": v(136.6, 69.58) * mm});
            skLineSegment(sketch, "E5513", {"start": v(136.6, 69.58) * mm, "end": v(136.68, 69.47) * mm});
            skLineSegment(sketch, "E5514", {"start": v(136.68, 69.47) * mm, "end": v(136.79, 69.37) * mm});
            skLineSegment(sketch, "E5515", {"start": v(136.79, 69.37) * mm, "end": v(136.91, 69.28) * mm});
            skLineSegment(sketch, "E5516", {"start": v(136.91, 69.28) * mm, "end": v(137.04, 69.22) * mm});
            skLineSegment(sketch, "E5517", {"start": v(137.04, 69.22) * mm, "end": v(137.1, 69.2) * mm});
            skLineSegment(sketch, "E5518", {"start": v(137.1, 69.2) * mm, "end": v(137.17, 69.19) * mm});
            skLineSegment(sketch, "E5519", {"start": v(137.17, 69.19) * mm, "end": v(137.23, 69.19) * mm});
            skLineSegment(sketch, "E5520", {"start": v(137.23, 69.19) * mm, "end": v(137.29, 69.2) * mm});
            skLineSegment(sketch, "E5521", {"start": v(137.29, 69.2) * mm, "end": v(137.34, 69.22) * mm});
            skLineSegment(sketch, "E5522", {"start": v(137.34, 69.22) * mm, "end": v(137.38, 69.25) * mm});
            skArc(sketch, "E5523", {"start": v(137.38, 69.25) * mm, "mid": v(137.95, 69.8) * mm, "end": v(138.52, 70.35) * mm});
            skArc(sketch, "E5524", {"start": v(138.52, 70.35) * mm, "mid": v(140.94, 72.5) * mm, "end": v(143.44, 74.53) * mm});
            skArc(sketch, "E5525", {"start": v(143.44, 74.53) * mm, "mid": v(144.53, 74.65) * mm, "end": v(145.1, 73.72) * mm});
            skArc(sketch, "E5526", {"start": v(145.1, 73.72) * mm, "mid": v(144.97, 73.46) * mm, "end": v(144.68, 73.44) * mm});
            skArc(sketch, "E5527", {"start": v(144.68, 73.44) * mm, "mid": v(143.63, 73.56) * mm, "end": v(142.69, 73.1) * mm});
            skArc(sketch, "E5528", {"start": v(142.69, 73.1) * mm, "mid": v(140.59, 70.71) * mm, "end": v(138.82, 68.08) * mm});
            skArc(sketch, "E5529", {"start": v(138.82, 68.08) * mm, "mid": v(138.45, 66.98) * mm, "end": v(138.97, 65.95) * mm});
            skArc(sketch, "E5530", {"start": v(138.97, 65.95) * mm, "mid": v(139.37, 65.94) * mm, "end": v(139.6, 65.6) * mm});
            skArc(sketch, "E5531", {"start": v(139.6, 65.6) * mm, "mid": v(139.66, 64.33) * mm, "end": v(139.66, 63.06) * mm});
            skArc(sketch, "E5532", {"start": v(139.66, 63.06) * mm, "mid": v(139.74, 61.78) * mm, "end": v(140.03, 60.53) * mm});
            skArc(sketch, "E5533", {"start": v(140.03, 60.53) * mm, "mid": v(140.1, 59.5) * mm, "end": v(139.72, 58.53) * mm});
            skArc(sketch, "E5534", {"start": v(139.72, 58.53) * mm, "mid": v(139.17, 57.98) * mm, "end": v(138.4, 57.93) * mm});
            skLineSegment(sketch, "E5535", {"start": v(138.4, 57.93) * mm, "end": v(138.36, 57.94) * mm});
            skLineSegment(sketch, "E5536", {"start": v(138.36, 57.94) * mm, "end": v(138.32, 57.93) * mm});
            skLineSegment(sketch, "E5537", {"start": v(138.32, 57.93) * mm, "end": v(138.28, 57.92) * mm});
            skLineSegment(sketch, "E5538", {"start": v(138.28, 57.92) * mm, "end": v(138.24, 57.9) * mm});
            skLineSegment(sketch, "E5539", {"start": v(138.24, 57.9) * mm, "end": v(138.17, 57.84) * mm});
            skLineSegment(sketch, "E5540", {"start": v(138.17, 57.84) * mm, "end": v(138.1, 57.76) * mm});
            skLineSegment(sketch, "E5541", {"start": v(138.1, 57.76) * mm, "end": v(138.06, 57.67) * mm});
            skLineSegment(sketch, "E5542", {"start": v(138.06, 57.67) * mm, "end": v(138.02, 57.57) * mm});
            skLineSegment(sketch, "E5543", {"start": v(138.02, 57.57) * mm, "end": v(138, 57.47) * mm});
            skLineSegment(sketch, "E5544", {"start": v(138, 57.47) * mm, "end": v(138, 57.38) * mm});
            skArc(sketch, "E5545", {"start": v(145.31, 75.66) * mm, "mid": v(145.58, 75.2) * mm, "end": v(146.1, 75.3) * mm});
            skArc(sketch, "E5546", {"start": v(146.1, 75.3) * mm, "mid": v(146.75, 76.25) * mm, "end": v(147.01, 77.36) * mm});
            skArc(sketch, "E5547", {"start": v(147.01, 77.36) * mm, "mid": v(146.74, 77.8) * mm, "end": v(146.24, 77.7) * mm});
            skArc(sketch, "E5548", {"start": v(146.24, 77.7) * mm, "mid": v(145.59, 76.77) * mm, "end": v(145.31, 75.66) * mm});
            skArc(sketch, "E5549", {"start": v(148.15, 78.28) * mm, "mid": v(148.46, 77.73) * mm, "end": v(149.09, 77.7) * mm});
            skArc(sketch, "E5550", {"start": v(149.09, 77.7) * mm, "mid": v(149.4, 78.24) * mm, "end": v(149.06, 78.74) * mm});
            skArc(sketch, "E5551", {"start": v(149.06, 78.74) * mm, "mid": v(148.73, 78.8) * mm, "end": v(148.42, 78.72) * mm});
            skArc(sketch, "E5552", {"start": v(148.42, 78.72) * mm, "mid": v(148.22, 78.54) * mm, "end": v(148.15, 78.28) * mm});
            skArc(sketch, "E5553", {"start": v(139.29, 67.3) * mm, "mid": v(139.69, 67.04) * mm, "end": v(140.15, 67.16) * mm});
            skArc(sketch, "E5554", {"start": v(140.15, 67.16) * mm, "mid": v(140.36, 67.58) * mm, "end": v(140.2, 68.02) * mm});
            skArc(sketch, "E5555", {"start": v(140.2, 68.02) * mm, "mid": v(139.95, 68.16) * mm, "end": v(139.67, 68.2) * mm});
            skArc(sketch, "E5556", {"start": v(139.67, 68.2) * mm, "mid": v(139.27, 67.94) * mm, "end": v(139.26, 67.46) * mm});
            skArc(sketch, "E5557", {"start": v(139.26, 67.46) * mm, "mid": v(139.27, 67.43) * mm, "end": v(139.27, 67.38) * mm});
            skArc(sketch, "E5558", {"start": v(139.27, 67.38) * mm, "mid": v(139.27, 67.34) * mm, "end": v(139.29, 67.3) * mm});
            skArc(sketch, "E5559", {"start": v(119.54, 66.56) * mm, "mid": v(120.6, 66.33) * mm, "end": v(121.28, 67.17) * mm});
            skArc(sketch, "E5560", {"start": v(121.28, 67.17) * mm, "mid": v(120.87, 68.2) * mm, "end": v(119.78, 68.43) * mm});
            skArc(sketch, "E5561", {"start": v(119.78, 68.43) * mm, "mid": v(119.35, 68.15) * mm, "end": v(119.15, 67.69) * mm});
            skArc(sketch, "E5562", {"start": v(119.15, 67.69) * mm, "mid": v(119.21, 67.08) * mm, "end": v(119.54, 66.56) * mm});
            skArc(sketch, "E5563", {"start": v(116.45, 69) * mm, "mid": v(116.77, 68.67) * mm, "end": v(117.13, 68.38) * mm});
            skArc(sketch, "E5564", {"start": v(117.13, 68.38) * mm, "mid": v(117.71, 68.37) * mm, "end": v(117.93, 68.9) * mm});
            skArc(sketch, "E5565", {"start": v(117.93, 68.9) * mm, "mid": v(117.52, 69.64) * mm, "end": v(116.77, 70) * mm});
            skArc(sketch, "E5566", {"start": v(116.77, 70) * mm, "mid": v(116.23, 69.76) * mm, "end": v(116.25, 69.17) * mm});
            skArc(sketch, "E5567", {"start": v(116.25, 69.17) * mm, "mid": v(116.3, 69.12) * mm, "end": v(116.35, 69.08) * mm});
            skArc(sketch, "E5568", {"start": v(116.35, 69.08) * mm, "mid": v(116.4, 69.05) * mm, "end": v(116.45, 69) * mm});
            skArc(sketch, "E5569", {"start": v(117.46, 59.6) * mm, "mid": v(118.83, 59.43) * mm, "end": v(119.36, 60.7) * mm});
            skArc(sketch, "E5570", {"start": v(119.36, 60.7) * mm, "mid": v(118.3, 61.58) * mm, "end": v(117.13, 60.85) * mm});
            skArc(sketch, "E5571", {"start": v(117.13, 60.85) * mm, "mid": v(117.06, 60.54) * mm, "end": v(117.1, 60.23) * mm});
            skArc(sketch, "E5572", {"start": v(117.1, 60.23) * mm, "mid": v(117.23, 59.89) * mm, "end": v(117.46, 59.6) * mm});
            skArc(sketch, "E5573", {"start": v(120.18, 59.25) * mm, "mid": v(120.26, 58.97) * mm, "end": v(120.47, 58.77) * mm});
            skArc(sketch, "E5574", {"start": v(120.47, 58.77) * mm, "mid": v(120.72, 58.73) * mm, "end": v(120.95, 58.85) * mm});
            skArc(sketch, "E5575", {"start": v(120.95, 58.85) * mm, "mid": v(121.1, 59.12) * mm, "end": v(121.15, 59.42) * mm});
            skArc(sketch, "E5576", {"start": v(121.15, 59.42) * mm, "mid": v(120.85, 59.82) * mm, "end": v(120.36, 59.7) * mm});
            skArc(sketch, "E5577", {"start": v(120.36, 59.7) * mm, "mid": v(120.28, 59.6) * mm, "end": v(120.23, 59.5) * mm});
            skArc(sketch, "E5578", {"start": v(120.23, 59.5) * mm, "mid": v(120.2, 59.37) * mm, "end": v(120.18, 59.25) * mm});
            skSolve(sketch);
        }
        {
            var Q0;
            {var subQ0=sQuery(id+"F2.wireOp",EDGE,"E2986");Q0=makeQuery(id+"F2.imprint","IMPRINT",FACE,{"disambiguationData":[TD([[makeQuery(id+"F2.imprint","IMPRINT",EDGE,{"derivedFrom":subQ0}),-1.0]])]});}
            var Q1;
            {var subQ7=sQuery(id+"F2.wireOp",EDGE,"E3297");Q1=makeQuery(id+"F2.imprint","IMPRINT",FACE,{"disambiguationData":[TD([[makeQuery(id+"F2.imprint","IMPRINT",EDGE,{"derivedFrom":subQ7}),-1.0]])]});}
            var Q2;
            {var subQ0=sQuery(id+"F2.wireOp",EDGE,"E3083");Q2=makeQuery(id+"F2.imprint","IMPRINT",FACE,{"disambiguationData":[TD([[makeQuery(id+"F2.imprint","IMPRINT",EDGE,{"derivedFrom":subQ0}),-1.0]])]});}
            var Q3;
            {var subQ5=sQuery(id+"F2.wireOp",EDGE,"E2624");Q3=makeQuery(id+"F2.imprint","IMPRINT",FACE,{"disambiguationData":[TD([[makeQuery(id+"F2.imprint","IMPRINT",EDGE,{"derivedFrom":subQ5}),-1.0]])]});}
            var Q4;
            {var subQ5=sQuery(id+"F2.wireOp",EDGE,"E2433");Q4=makeQuery(id+"F2.imprint","IMPRINT",FACE,{"disambiguationData":[TD([[makeQuery(id+"F2.imprint","IMPRINT",EDGE,{"derivedFrom":subQ5}),-1.0]])]});}
            var Q5;
            {var subQ1=sQuery(id+"F2.wireOp",EDGE,"E2753");Q5=makeQuery(id+"F2.imprint","IMPRINT",FACE,{"disambiguationData":[TD([[makeQuery(id+"F2.imprint","IMPRINT",EDGE,{"derivedFrom":subQ1}),1.0]])]});}
            var Q6;
            {var subQ1=sQuery(id+"F2.wireOp",EDGE,"E2753");Q6=makeQuery(id+"F2.imprint","IMPRINT",FACE,{"disambiguationData":[TD([[makeQuery(id+"F2.imprint","IMPRINT",EDGE,{"derivedFrom":subQ1}),-1.0]])]});}
            var Q7;
            {var subQ8=sQuery(id+"F2.wireOp",EDGE,"E2782");Q7=makeQuery(id+"F2.imprint","IMPRINT",FACE,{"disambiguationData":[TD([[makeQuery(id+"F2.imprint","IMPRINT",EDGE,{"derivedFrom":subQ8}),-1.0]])]});}
            var Q8;
            {var subQ0=sQuery(id+"F2.wireOp",EDGE,"E2782");Q8=makeQuery(id+"F2.imprint","IMPRINT",FACE,{"disambiguationData":[TD([[makeQuery(id+"F2.imprint","IMPRINT",EDGE,{"derivedFrom":subQ0}),1.0]])]});}
            var Q9;
            {var subQ12=sQuery(id+"F2.wireOp",EDGE,"E3346");Q9=makeQuery(id+"F2.imprint","IMPRINT",FACE,{"disambiguationData":[TD([[makeQuery(id+"F2.imprint","IMPRINT",EDGE,{"derivedFrom":subQ12}),-1.0]])]});}
            extrude(context, id + "F3", {"entities" : qUnion([Q0, Q1, Q2, Q3, Q4, Q5, Q6, Q7, Q8, Q9]), "operationType" : NewBodyOperationType.REMOVE, "oppositeDirection" : true, "depth" : 0.8 * mm, "offsetDistance" : 25 * mm});
        }
        {
            var Q0;
            {var subQ11=sQuery(id+"F2.wireOp",EDGE,"E2986");Q0=makeQuery(id+"F2.imprint","IMPRINT",FACE,{"disambiguationData":[TD([[makeQuery(id+"F2.imprint","IMPRINT",EDGE,{"derivedFrom":subQ11}),1.0]])]});}
            var Q1;
            {var subQ5=sQuery(id+"F2.wireOp",EDGE,"E3234");Q1=makeQuery(id+"F2.imprint","IMPRINT",FACE,{"disambiguationData":[TD([[makeQuery(id+"F2.imprint","IMPRINT",EDGE,{"derivedFrom":subQ5}),-1.0]])]});}
            var Q2;
            {var subQ11=sQuery(id+"F2.wireOp",EDGE,"E3083");Q2=makeQuery(id+"F2.imprint","IMPRINT",FACE,{"disambiguationData":[TD([[makeQuery(id+"F2.imprint","IMPRINT",EDGE,{"derivedFrom":subQ11}),1.0]])]});}
            var Q3;
            {var subQ9=sQuery(id+"F2.wireOp",EDGE,"E2784");Q3=makeQuery(id+"F2.imprint","IMPRINT",FACE,{"disambiguationData":[TD([[makeQuery(id+"F2.imprint","IMPRINT",EDGE,{"derivedFrom":subQ9}),-1.0]])]});}
            var Q4;
            {var subQ12=sQuery(id+"F2.wireOp",EDGE,"E2433");Q4=makeQuery(id+"F2.imprint","IMPRINT",FACE,{"disambiguationData":[TD([[makeQuery(id+"F2.imprint","IMPRINT",EDGE,{"derivedFrom":subQ12}),1.0]])]});}
            var Q5;
            {var subQ10=sQuery(id+"F2.wireOp",EDGE,"E2582");Q5=makeQuery(id+"F2.imprint","IMPRINT",FACE,{"disambiguationData":[TD([[makeQuery(id+"F2.imprint","IMPRINT",EDGE,{"derivedFrom":subQ10}),-1.0]])]});}
            var Q6;
            {var subQ3=sQuery(id+"F2.wireOp",EDGE,"E2832");Q6=makeQuery(id+"F2.imprint","IMPRINT",FACE,{"disambiguationData":[TD([[makeQuery(id+"F2.imprint","IMPRINT",EDGE,{"derivedFrom":subQ3}),1.0]])]});}
            var Q7;
            {var subQ15=sQuery(id+"F2.wireOp",EDGE,"E2832");Q7=makeQuery(id+"F2.imprint","IMPRINT",FACE,{"disambiguationData":[TD([[makeQuery(id+"F2.imprint","IMPRINT",EDGE,{"derivedFrom":subQ15}),-1.0]])]});}
            var Q8;
            {var subQ5=sQuery(id+"F2.wireOp",EDGE,"E2872");Q8=makeQuery(id+"F2.imprint","IMPRINT",FACE,{"disambiguationData":[TD([[makeQuery(id+"F2.imprint","IMPRINT",EDGE,{"derivedFrom":subQ5}),1.0]])]});}
            extrude(context, id + "F4", {"entities" : qUnion([Q0, Q1, Q2, Q3, Q4, Q5, Q6, Q7, Q8]), "operationType" : NewBodyOperationType.REMOVE, "oppositeDirection" : true, "depth" : 0.5 * mm, "offsetDistance" : 25 * mm});
        }
        {
            var Q0;
            {var subQ10=sQuery(id+"F2.wireOp",EDGE,"E3011");Q0=makeQuery(id+"F2.imprint","IMPRINT",FACE,{"disambiguationData":[TD([[makeQuery(id+"F2.imprint","IMPRINT",EDGE,{"derivedFrom":subQ10}),1.0]])]});}
            var Q1;
            {var subQ6=sQuery(id+"F2.wireOp",EDGE,"E3172");Q1=makeQuery(id+"F2.imprint","IMPRINT",FACE,{"disambiguationData":[TD([[makeQuery(id+"F2.imprint","IMPRINT",EDGE,{"derivedFrom":subQ6}),-1.0]])]});}
            var Q2;
            {var subQ0=sQuery(id+"F2.wireOp",EDGE,"E2706");Q2=makeQuery(id+"F2.imprint","IMPRINT",FACE,{"disambiguationData":[TD([[makeQuery(id+"F2.imprint","IMPRINT",EDGE,{"derivedFrom":subQ0}),-1.0]])]});}
            var Q3;
            {var subQ0=sQuery(id+"F2.wireOp",EDGE,"E2835");Q3=makeQuery(id+"F2.imprint","IMPRINT",FACE,{"disambiguationData":[TD([[makeQuery(id+"F2.imprint","IMPRINT",EDGE,{"derivedFrom":subQ0}),-1.0]])]});}
            var Q4;
            {var subQ10=sQuery(id+"F2.wireOp",EDGE,"E2582");Q4=makeQuery(id+"F2.imprint","IMPRINT",FACE,{"disambiguationData":[TD([[makeQuery(id+"F2.imprint","IMPRINT",EDGE,{"derivedFrom":subQ10}),1.0]])]});}
            var Q5;
            {var subQ5=sQuery(id+"F2.wireOp",EDGE,"E2510");Q5=makeQuery(id+"F2.imprint","IMPRINT",FACE,{"disambiguationData":[TD([[makeQuery(id+"F2.imprint","IMPRINT",EDGE,{"derivedFrom":subQ5}),-1.0]])]});}
            var Q6;
            {var subQ5=sQuery(id+"F2.wireOp",EDGE,"E2903");Q6=makeQuery(id+"F2.imprint","IMPRINT",FACE,{"disambiguationData":[TD([[makeQuery(id+"F2.imprint","IMPRINT",EDGE,{"derivedFrom":subQ5}),-1.0]])]});}
            var Q7;
            {var subQ0=sQuery(id+"F2.wireOp",EDGE,"E3533");Q7=makeQuery(id+"F2.imprint","IMPRINT",FACE,{"disambiguationData":[TD([[makeQuery(id+"F2.imprint","IMPRINT",EDGE,{"derivedFrom":subQ0}),-1.0]])]});}
            extrude(context, id + "F5", {"entities" : qUnion([Q0, Q1, Q2, Q3, Q4, Q5, Q6, Q7]), "operationType" : NewBodyOperationType.REMOVE, "oppositeDirection" : true, "depth" : 0.25 * mm, "offsetDistance" : 25 * mm});
        }
    });
